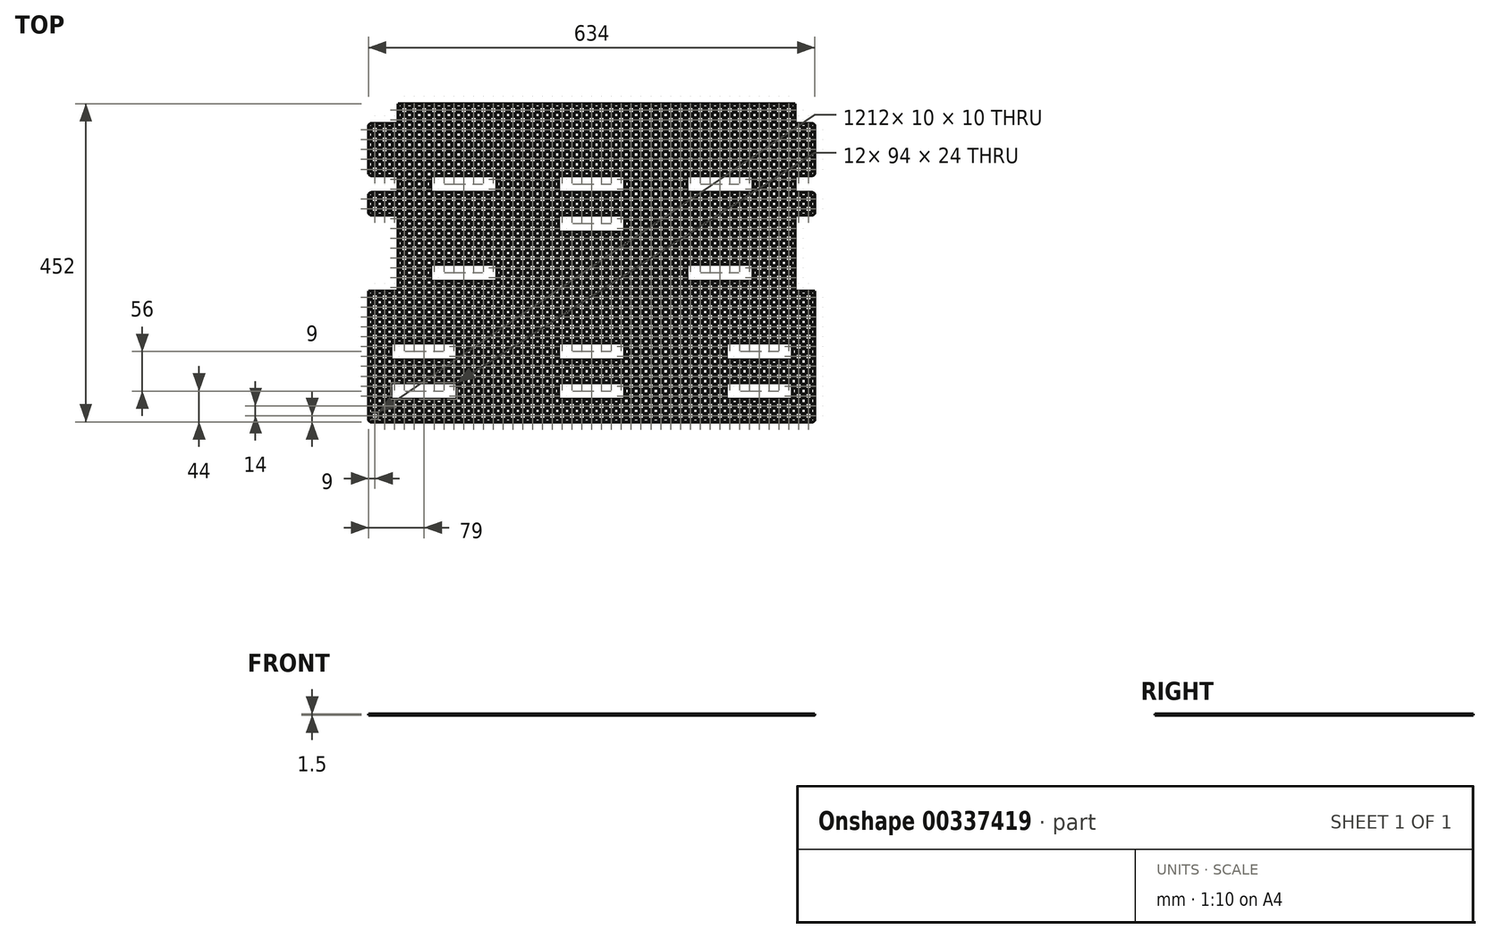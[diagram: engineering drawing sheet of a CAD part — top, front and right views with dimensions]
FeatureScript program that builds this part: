
annotation { "Feature Type Name" : "Feature", "Feature Type Description" : "" }
export const myFeature = defineFeature(function(context is Context, id is Id, definition is map)
    precondition{}
    {
        {
            var Q0;
            Q0=qCreatedBy(makeId("Top.planeOp"),FACE);
            var sketch = newSketch(context, id + "F0", { "sketchPlane" : qUnion([Q0])});
            skLineSegment(sketch, "E0.bottom", {"start": v(-317, 0) * mm, "end": v(317, 0) * mm});
            skLineSegment(sketch, "E0.top", {"start": v(-317, -452) * mm, "end": v(317, -452) * mm});
            skLineSegment(sketch, "E0.left", {"start": v(-317, 0) * mm, "end": v(-317, -452) * mm});
            skLineSegment(sketch, "E0.right", {"start": v(317, 0) * mm, "end": v(317, -452) * mm});
            skLineSegment(sketch, "E1", {"start": v(-317, 16) * mm, "end": v(317, 16) * mm, "construction": true});
            skLineSegment(sketch, "E2", {"start": v(-314.5, 16) * mm, "end": v(-314.5, -452) * mm, "construction": true});
            skLineSegment(sketch, "E3", {"start": v(-300, 16) * mm, "end": v(-300, -452) * mm, "construction": true});
            skLineSegment(sketch, "E4", {"start": v(-285.5, 16) * mm, "end": v(-285.5, -452) * mm, "construction": true});
            skLineSegment(sketch, "E5", {"start": v(285.5, 16) * mm, "end": v(285.5, -452) * mm, "construction": true});
            skLineSegment(sketch, "E6", {"start": v(300, 16) * mm, "end": v(300, -452) * mm, "construction": true});
            skLineSegment(sketch, "E7", {"start": v(314.5, 16) * mm, "end": v(314.5, -452) * mm, "construction": true});
            skLineSegment(sketch, "E8", {"start": v(-300, 0) * mm, "end": v(300, 0) * mm, "construction": true});
            skLineSegment(sketch, "E9", {"start": v(-314.5, -22) * mm, "end": v(314.5, -22) * mm, "construction": true});
            skLineSegment(sketch, "E10", {"start": v(-314.5, -112.5) * mm, "end": v(314.5, -112.5) * mm, "construction": true});
            skLineSegment(sketch, "E11", {"start": v(-314.5, -254) * mm, "end": v(314.5, -254) * mm, "construction": true});
            skLineSegment(sketch, "E12", {"start": v(-314.5, -231.78) * mm, "end": v(314.5, -231.78) * mm, "construction": true});
            skLineSegment(sketch, "E13", {"start": v(-314.5, -193) * mm, "end": v(314.5, -193) * mm, "construction": true});
            skCircle(sketch, "E14", {"center": v(-305, -22) * mm, "radius": 3.5 * mm, "construction": true});
            skCircle(sketch, "E15", {"center": v(-296, -112.5) * mm, "radius": 3.5 * mm, "construction": true});
            skCircle(sketch, "E16", {"center": v(-300, -254) * mm, "radius": 3.5 * mm, "construction": true});
            skCircle(sketch, "E17", {"center": v(295, -22) * mm, "radius": 3.5 * mm, "construction": true});
            skCircle(sketch, "E18", {"center": v(304, -112.5) * mm, "radius": 3.5 * mm, "construction": true});
            skCircle(sketch, "E19", {"center": v(300, -254) * mm, "radius": 3.5 * mm, "construction": true});
            skSolve(sketch);
        }
        {
            var Q0;
            Q0=qCreatedBy(makeId("Top.planeOp"),FACE);
            var sketch = newSketch(context, id + "F1", { "sketchPlane" : qUnion([Q0])});
            skLineSegment(sketch, "E20.bottom", {"start": v(-313, -438) * mm, "end": v(-303, -438) * mm});
            skLineSegment(sketch, "E20.top", {"start": v(-313, -448) * mm, "end": v(-303, -448) * mm});
            skLineSegment(sketch, "E20.left", {"start": v(-313, -438) * mm, "end": v(-313, -448) * mm});
            skLineSegment(sketch, "E20.right", {"start": v(-303, -438) * mm, "end": v(-303, -448) * mm});
            skLineSegment(sketch, "E21.0.1.0", {"start": v(-313, -424) * mm, "end": v(-303, -424) * mm});
            skLineSegment(sketch, "E21.0.1.1", {"start": v(-313, -434) * mm, "end": v(-303, -434) * mm});
            skLineSegment(sketch, "E21.0.1.2", {"start": v(-313, -424) * mm, "end": v(-313, -434) * mm});
            skLineSegment(sketch, "E21.0.1.3", {"start": v(-303, -424) * mm, "end": v(-303, -434) * mm});
            skLineSegment(sketch, "E21.0.2.0", {"start": v(-313, -410) * mm, "end": v(-303, -410) * mm});
            skLineSegment(sketch, "E21.0.2.1", {"start": v(-313, -420) * mm, "end": v(-303, -420) * mm});
            skLineSegment(sketch, "E21.0.2.2", {"start": v(-313, -410) * mm, "end": v(-313, -420) * mm});
            skLineSegment(sketch, "E21.0.2.3", {"start": v(-303, -410) * mm, "end": v(-303, -420) * mm});
            skLineSegment(sketch, "E21.0.3.0", {"start": v(-313, -396) * mm, "end": v(-303, -396) * mm});
            skLineSegment(sketch, "E21.0.3.1", {"start": v(-313, -406) * mm, "end": v(-303, -406) * mm});
            skLineSegment(sketch, "E21.0.3.2", {"start": v(-313, -396) * mm, "end": v(-313, -406) * mm});
            skLineSegment(sketch, "E21.0.3.3", {"start": v(-303, -396) * mm, "end": v(-303, -406) * mm});
            skLineSegment(sketch, "E21.0.4.0", {"start": v(-313, -382) * mm, "end": v(-303, -382) * mm});
            skLineSegment(sketch, "E21.0.4.1", {"start": v(-313, -392) * mm, "end": v(-303, -392) * mm});
            skLineSegment(sketch, "E21.0.4.2", {"start": v(-313, -382) * mm, "end": v(-313, -392) * mm});
            skLineSegment(sketch, "E21.0.4.3", {"start": v(-303, -382) * mm, "end": v(-303, -392) * mm});
            skLineSegment(sketch, "E21.0.5.0", {"start": v(-313, -368) * mm, "end": v(-303, -368) * mm});
            skLineSegment(sketch, "E21.0.5.1", {"start": v(-313, -378) * mm, "end": v(-303, -378) * mm});
            skLineSegment(sketch, "E21.0.5.2", {"start": v(-313, -368) * mm, "end": v(-313, -378) * mm});
            skLineSegment(sketch, "E21.0.5.3", {"start": v(-303, -368) * mm, "end": v(-303, -378) * mm});
            skLineSegment(sketch, "E21.0.6.0", {"start": v(-313, -354) * mm, "end": v(-303, -354) * mm});
            skLineSegment(sketch, "E21.0.6.1", {"start": v(-313, -364) * mm, "end": v(-303, -364) * mm});
            skLineSegment(sketch, "E21.0.6.2", {"start": v(-313, -354) * mm, "end": v(-313, -364) * mm});
            skLineSegment(sketch, "E21.0.6.3", {"start": v(-303, -354) * mm, "end": v(-303, -364) * mm});
            skLineSegment(sketch, "E21.0.7.0", {"start": v(-313, -340) * mm, "end": v(-303, -340) * mm});
            skLineSegment(sketch, "E21.0.7.1", {"start": v(-313, -350) * mm, "end": v(-303, -350) * mm});
            skLineSegment(sketch, "E21.0.7.2", {"start": v(-313, -340) * mm, "end": v(-313, -350) * mm});
            skLineSegment(sketch, "E21.0.7.3", {"start": v(-303, -340) * mm, "end": v(-303, -350) * mm});
            skLineSegment(sketch, "E21.0.8.0", {"start": v(-313, -326) * mm, "end": v(-303, -326) * mm});
            skLineSegment(sketch, "E21.0.8.1", {"start": v(-313, -336) * mm, "end": v(-303, -336) * mm});
            skLineSegment(sketch, "E21.0.8.2", {"start": v(-313, -326) * mm, "end": v(-313, -336) * mm});
            skLineSegment(sketch, "E21.0.8.3", {"start": v(-303, -326) * mm, "end": v(-303, -336) * mm});
            skLineSegment(sketch, "E21.0.9.0", {"start": v(-313, -312) * mm, "end": v(-303, -312) * mm});
            skLineSegment(sketch, "E21.0.9.1", {"start": v(-313, -322) * mm, "end": v(-303, -322) * mm});
            skLineSegment(sketch, "E21.0.9.2", {"start": v(-313, -312) * mm, "end": v(-313, -322) * mm});
            skLineSegment(sketch, "E21.0.9.3", {"start": v(-303, -312) * mm, "end": v(-303, -322) * mm});
            skLineSegment(sketch, "E21.0.10.0", {"start": v(-313, -298) * mm, "end": v(-303, -298) * mm});
            skLineSegment(sketch, "E21.0.10.1", {"start": v(-313, -308) * mm, "end": v(-303, -308) * mm});
            skLineSegment(sketch, "E21.0.10.2", {"start": v(-313, -298) * mm, "end": v(-313, -308) * mm});
            skLineSegment(sketch, "E21.0.10.3", {"start": v(-303, -298) * mm, "end": v(-303, -308) * mm});
            skLineSegment(sketch, "E21.0.11.0", {"start": v(-313, -284) * mm, "end": v(-303, -284) * mm});
            skLineSegment(sketch, "E21.0.11.1", {"start": v(-313, -294) * mm, "end": v(-303, -294) * mm});
            skLineSegment(sketch, "E21.0.11.2", {"start": v(-313, -284) * mm, "end": v(-313, -294) * mm});
            skLineSegment(sketch, "E21.0.11.3", {"start": v(-303, -284) * mm, "end": v(-303, -294) * mm});
            skLineSegment(sketch, "E21.0.12.0", {"start": v(-313, -270) * mm, "end": v(-303, -270) * mm});
            skLineSegment(sketch, "E21.0.12.1", {"start": v(-313, -280) * mm, "end": v(-303, -280) * mm});
            skLineSegment(sketch, "E21.0.12.2", {"start": v(-313, -270) * mm, "end": v(-313, -280) * mm});
            skLineSegment(sketch, "E21.0.12.3", {"start": v(-303, -270) * mm, "end": v(-303, -280) * mm});
            skLineSegment(sketch, "E21.0.13.0", {"start": v(-313, -256) * mm, "end": v(-303, -256) * mm});
            skLineSegment(sketch, "E21.0.13.1", {"start": v(-313, -266) * mm, "end": v(-303, -266) * mm});
            skLineSegment(sketch, "E21.0.13.2", {"start": v(-313, -256) * mm, "end": v(-313, -266) * mm});
            skLineSegment(sketch, "E21.0.13.3", {"start": v(-303, -256) * mm, "end": v(-303, -266) * mm});
            skLineSegment(sketch, "E21.0.14.0", {"start": v(-313, -242) * mm, "end": v(-303, -242) * mm});
            skLineSegment(sketch, "E21.0.14.1", {"start": v(-313, -252) * mm, "end": v(-303, -252) * mm});
            skLineSegment(sketch, "E21.0.14.2", {"start": v(-313, -242) * mm, "end": v(-313, -252) * mm});
            skLineSegment(sketch, "E21.0.14.3", {"start": v(-303, -242) * mm, "end": v(-303, -252) * mm});
            skLineSegment(sketch, "E21.0.15.0", {"start": v(-313, -228) * mm, "end": v(-303, -228) * mm});
            skLineSegment(sketch, "E21.0.15.1", {"start": v(-313, -238) * mm, "end": v(-303, -238) * mm});
            skLineSegment(sketch, "E21.0.15.2", {"start": v(-313, -228) * mm, "end": v(-313, -238) * mm});
            skLineSegment(sketch, "E21.0.15.3", {"start": v(-303, -228) * mm, "end": v(-303, -238) * mm});
            skLineSegment(sketch, "E21.0.16.0", {"start": v(-313, -214) * mm, "end": v(-303, -214) * mm});
            skLineSegment(sketch, "E21.0.16.1", {"start": v(-313, -224) * mm, "end": v(-303, -224) * mm});
            skLineSegment(sketch, "E21.0.16.2", {"start": v(-313, -214) * mm, "end": v(-313, -224) * mm});
            skLineSegment(sketch, "E21.0.16.3", {"start": v(-303, -214) * mm, "end": v(-303, -224) * mm});
            skLineSegment(sketch, "E21.0.17.0", {"start": v(-313, -200) * mm, "end": v(-303, -200) * mm});
            skLineSegment(sketch, "E21.0.17.1", {"start": v(-313, -210) * mm, "end": v(-303, -210) * mm});
            skLineSegment(sketch, "E21.0.17.2", {"start": v(-313, -200) * mm, "end": v(-313, -210) * mm});
            skLineSegment(sketch, "E21.0.17.3", {"start": v(-303, -200) * mm, "end": v(-303, -210) * mm});
            skLineSegment(sketch, "E21.0.18.0", {"start": v(-313, -186) * mm, "end": v(-303, -186) * mm});
            skLineSegment(sketch, "E21.0.18.1", {"start": v(-313, -196) * mm, "end": v(-303, -196) * mm});
            skLineSegment(sketch, "E21.0.18.2", {"start": v(-313, -186) * mm, "end": v(-313, -196) * mm});
            skLineSegment(sketch, "E21.0.18.3", {"start": v(-303, -186) * mm, "end": v(-303, -196) * mm});
            skLineSegment(sketch, "E21.0.19.0", {"start": v(-313, -172) * mm, "end": v(-303, -172) * mm});
            skLineSegment(sketch, "E21.0.19.1", {"start": v(-313, -182) * mm, "end": v(-303, -182) * mm});
            skLineSegment(sketch, "E21.0.19.2", {"start": v(-313, -172) * mm, "end": v(-313, -182) * mm});
            skLineSegment(sketch, "E21.0.19.3", {"start": v(-303, -172) * mm, "end": v(-303, -182) * mm});
            skLineSegment(sketch, "E21.0.20.0", {"start": v(-313, -158) * mm, "end": v(-303, -158) * mm});
            skLineSegment(sketch, "E21.0.20.1", {"start": v(-313, -168) * mm, "end": v(-303, -168) * mm});
            skLineSegment(sketch, "E21.0.20.2", {"start": v(-313, -158) * mm, "end": v(-313, -168) * mm});
            skLineSegment(sketch, "E21.0.20.3", {"start": v(-303, -158) * mm, "end": v(-303, -168) * mm});
            skLineSegment(sketch, "E21.0.21.0", {"start": v(-313, -144) * mm, "end": v(-303, -144) * mm});
            skLineSegment(sketch, "E21.0.21.1", {"start": v(-313, -154) * mm, "end": v(-303, -154) * mm});
            skLineSegment(sketch, "E21.0.21.2", {"start": v(-313, -144) * mm, "end": v(-313, -154) * mm});
            skLineSegment(sketch, "E21.0.21.3", {"start": v(-303, -144) * mm, "end": v(-303, -154) * mm});
            skLineSegment(sketch, "E21.0.22.0", {"start": v(-313, -130) * mm, "end": v(-303, -130) * mm});
            skLineSegment(sketch, "E21.0.22.1", {"start": v(-313, -140) * mm, "end": v(-303, -140) * mm});
            skLineSegment(sketch, "E21.0.22.2", {"start": v(-313, -130) * mm, "end": v(-313, -140) * mm});
            skLineSegment(sketch, "E21.0.22.3", {"start": v(-303, -130) * mm, "end": v(-303, -140) * mm});
            skLineSegment(sketch, "E21.0.23.0", {"start": v(-313, -116) * mm, "end": v(-303, -116) * mm});
            skLineSegment(sketch, "E21.0.23.1", {"start": v(-313, -126) * mm, "end": v(-303, -126) * mm});
            skLineSegment(sketch, "E21.0.23.2", {"start": v(-313, -116) * mm, "end": v(-313, -126) * mm});
            skLineSegment(sketch, "E21.0.23.3", {"start": v(-303, -116) * mm, "end": v(-303, -126) * mm});
            skLineSegment(sketch, "E21.0.24.0", {"start": v(-313, -102) * mm, "end": v(-303, -102) * mm});
            skLineSegment(sketch, "E21.0.24.1", {"start": v(-313, -112) * mm, "end": v(-303, -112) * mm});
            skLineSegment(sketch, "E21.0.24.2", {"start": v(-313, -102) * mm, "end": v(-313, -112) * mm});
            skLineSegment(sketch, "E21.0.24.3", {"start": v(-303, -102) * mm, "end": v(-303, -112) * mm});
            skLineSegment(sketch, "E21.0.25.0", {"start": v(-313, -88) * mm, "end": v(-303, -88) * mm});
            skLineSegment(sketch, "E21.0.25.1", {"start": v(-313, -98) * mm, "end": v(-303, -98) * mm});
            skLineSegment(sketch, "E21.0.25.2", {"start": v(-313, -88) * mm, "end": v(-313, -98) * mm});
            skLineSegment(sketch, "E21.0.25.3", {"start": v(-303, -88) * mm, "end": v(-303, -98) * mm});
            skLineSegment(sketch, "E21.0.26.0", {"start": v(-313, -74) * mm, "end": v(-303, -74) * mm});
            skLineSegment(sketch, "E21.0.26.1", {"start": v(-313, -84) * mm, "end": v(-303, -84) * mm});
            skLineSegment(sketch, "E21.0.26.2", {"start": v(-313, -74) * mm, "end": v(-313, -84) * mm});
            skLineSegment(sketch, "E21.0.26.3", {"start": v(-303, -74) * mm, "end": v(-303, -84) * mm});
            skLineSegment(sketch, "E21.0.27.0", {"start": v(-313, -60) * mm, "end": v(-303, -60) * mm});
            skLineSegment(sketch, "E21.0.27.1", {"start": v(-313, -70) * mm, "end": v(-303, -70) * mm});
            skLineSegment(sketch, "E21.0.27.2", {"start": v(-313, -60) * mm, "end": v(-313, -70) * mm});
            skLineSegment(sketch, "E21.0.27.3", {"start": v(-303, -60) * mm, "end": v(-303, -70) * mm});
            skLineSegment(sketch, "E21.0.28.0", {"start": v(-313, -46) * mm, "end": v(-303, -46) * mm});
            skLineSegment(sketch, "E21.0.28.1", {"start": v(-313, -56) * mm, "end": v(-303, -56) * mm});
            skLineSegment(sketch, "E21.0.28.2", {"start": v(-313, -46) * mm, "end": v(-313, -56) * mm});
            skLineSegment(sketch, "E21.0.28.3", {"start": v(-303, -46) * mm, "end": v(-303, -56) * mm});
            skLineSegment(sketch, "E21.0.29.0", {"start": v(-313, -32) * mm, "end": v(-303, -32) * mm});
            skLineSegment(sketch, "E21.0.29.1", {"start": v(-313, -42) * mm, "end": v(-303, -42) * mm});
            skLineSegment(sketch, "E21.0.29.2", {"start": v(-313, -32) * mm, "end": v(-313, -42) * mm});
            skLineSegment(sketch, "E21.0.29.3", {"start": v(-303, -32) * mm, "end": v(-303, -42) * mm});
            skLineSegment(sketch, "E21.0.30.0", {"start": v(-313, -18) * mm, "end": v(-303, -18) * mm});
            skLineSegment(sketch, "E21.0.30.1", {"start": v(-313, -28) * mm, "end": v(-303, -28) * mm});
            skLineSegment(sketch, "E21.0.30.2", {"start": v(-313, -18) * mm, "end": v(-313, -28) * mm});
            skLineSegment(sketch, "E21.0.30.3", {"start": v(-303, -18) * mm, "end": v(-303, -28) * mm});
            skLineSegment(sketch, "E21.0.31.0", {"start": v(-313, -4) * mm, "end": v(-303, -4) * mm});
            skLineSegment(sketch, "E21.0.31.1", {"start": v(-313, -14) * mm, "end": v(-303, -14) * mm});
            skLineSegment(sketch, "E21.0.31.2", {"start": v(-313, -4) * mm, "end": v(-313, -14) * mm});
            skLineSegment(sketch, "E21.0.31.3", {"start": v(-303, -4) * mm, "end": v(-303, -14) * mm});
            skLineSegment(sketch, "E21.1.0.0", {"start": v(-299, -438) * mm, "end": v(-289, -438) * mm});
            skLineSegment(sketch, "E21.1.0.1", {"start": v(-299, -448) * mm, "end": v(-289, -448) * mm});
            skLineSegment(sketch, "E21.1.0.2", {"start": v(-299, -438) * mm, "end": v(-299, -448) * mm});
            skLineSegment(sketch, "E21.1.0.3", {"start": v(-289, -438) * mm, "end": v(-289, -448) * mm});
            skLineSegment(sketch, "E21.1.1.0", {"start": v(-299, -424) * mm, "end": v(-289, -424) * mm});
            skLineSegment(sketch, "E21.1.1.1", {"start": v(-299, -434) * mm, "end": v(-289, -434) * mm});
            skLineSegment(sketch, "E21.1.1.2", {"start": v(-299, -424) * mm, "end": v(-299, -434) * mm});
            skLineSegment(sketch, "E21.1.1.3", {"start": v(-289, -424) * mm, "end": v(-289, -434) * mm});
            skLineSegment(sketch, "E21.1.2.0", {"start": v(-299, -410) * mm, "end": v(-289, -410) * mm});
            skLineSegment(sketch, "E21.1.2.1", {"start": v(-299, -420) * mm, "end": v(-289, -420) * mm});
            skLineSegment(sketch, "E21.1.2.2", {"start": v(-299, -410) * mm, "end": v(-299, -420) * mm});
            skLineSegment(sketch, "E21.1.2.3", {"start": v(-289, -410) * mm, "end": v(-289, -420) * mm});
            skLineSegment(sketch, "E21.1.3.0", {"start": v(-299, -396) * mm, "end": v(-289, -396) * mm});
            skLineSegment(sketch, "E21.1.3.1", {"start": v(-299, -406) * mm, "end": v(-289, -406) * mm});
            skLineSegment(sketch, "E21.1.3.2", {"start": v(-299, -396) * mm, "end": v(-299, -406) * mm});
            skLineSegment(sketch, "E21.1.3.3", {"start": v(-289, -396) * mm, "end": v(-289, -406) * mm});
            skLineSegment(sketch, "E21.1.4.0", {"start": v(-299, -382) * mm, "end": v(-289, -382) * mm});
            skLineSegment(sketch, "E21.1.4.1", {"start": v(-299, -392) * mm, "end": v(-289, -392) * mm});
            skLineSegment(sketch, "E21.1.4.2", {"start": v(-299, -382) * mm, "end": v(-299, -392) * mm});
            skLineSegment(sketch, "E21.1.4.3", {"start": v(-289, -382) * mm, "end": v(-289, -392) * mm});
            skLineSegment(sketch, "E21.1.5.0", {"start": v(-299, -368) * mm, "end": v(-289, -368) * mm});
            skLineSegment(sketch, "E21.1.5.1", {"start": v(-299, -378) * mm, "end": v(-289, -378) * mm});
            skLineSegment(sketch, "E21.1.5.2", {"start": v(-299, -368) * mm, "end": v(-299, -378) * mm});
            skLineSegment(sketch, "E21.1.5.3", {"start": v(-289, -368) * mm, "end": v(-289, -378) * mm});
            skLineSegment(sketch, "E21.1.6.0", {"start": v(-299, -354) * mm, "end": v(-289, -354) * mm});
            skLineSegment(sketch, "E21.1.6.1", {"start": v(-299, -364) * mm, "end": v(-289, -364) * mm});
            skLineSegment(sketch, "E21.1.6.2", {"start": v(-299, -354) * mm, "end": v(-299, -364) * mm});
            skLineSegment(sketch, "E21.1.6.3", {"start": v(-289, -354) * mm, "end": v(-289, -364) * mm});
            skLineSegment(sketch, "E21.1.7.0", {"start": v(-299, -340) * mm, "end": v(-289, -340) * mm});
            skLineSegment(sketch, "E21.1.7.1", {"start": v(-299, -350) * mm, "end": v(-289, -350) * mm});
            skLineSegment(sketch, "E21.1.7.2", {"start": v(-299, -340) * mm, "end": v(-299, -350) * mm});
            skLineSegment(sketch, "E21.1.7.3", {"start": v(-289, -340) * mm, "end": v(-289, -350) * mm});
            skLineSegment(sketch, "E21.1.8.0", {"start": v(-299, -326) * mm, "end": v(-289, -326) * mm});
            skLineSegment(sketch, "E21.1.8.1", {"start": v(-299, -336) * mm, "end": v(-289, -336) * mm});
            skLineSegment(sketch, "E21.1.8.2", {"start": v(-299, -326) * mm, "end": v(-299, -336) * mm});
            skLineSegment(sketch, "E21.1.8.3", {"start": v(-289, -326) * mm, "end": v(-289, -336) * mm});
            skLineSegment(sketch, "E21.1.9.0", {"start": v(-299, -312) * mm, "end": v(-289, -312) * mm});
            skLineSegment(sketch, "E21.1.9.1", {"start": v(-299, -322) * mm, "end": v(-289, -322) * mm});
            skLineSegment(sketch, "E21.1.9.2", {"start": v(-299, -312) * mm, "end": v(-299, -322) * mm});
            skLineSegment(sketch, "E21.1.9.3", {"start": v(-289, -312) * mm, "end": v(-289, -322) * mm});
            skLineSegment(sketch, "E21.1.10.0", {"start": v(-299, -298) * mm, "end": v(-289, -298) * mm});
            skLineSegment(sketch, "E21.1.10.1", {"start": v(-299, -308) * mm, "end": v(-289, -308) * mm});
            skLineSegment(sketch, "E21.1.10.2", {"start": v(-299, -298) * mm, "end": v(-299, -308) * mm});
            skLineSegment(sketch, "E21.1.10.3", {"start": v(-289, -298) * mm, "end": v(-289, -308) * mm});
            skLineSegment(sketch, "E21.1.11.0", {"start": v(-299, -284) * mm, "end": v(-289, -284) * mm});
            skLineSegment(sketch, "E21.1.11.1", {"start": v(-299, -294) * mm, "end": v(-289, -294) * mm});
            skLineSegment(sketch, "E21.1.11.2", {"start": v(-299, -284) * mm, "end": v(-299, -294) * mm});
            skLineSegment(sketch, "E21.1.11.3", {"start": v(-289, -284) * mm, "end": v(-289, -294) * mm});
            skLineSegment(sketch, "E21.1.12.0", {"start": v(-299, -270) * mm, "end": v(-289, -270) * mm});
            skLineSegment(sketch, "E21.1.12.1", {"start": v(-299, -280) * mm, "end": v(-289, -280) * mm});
            skLineSegment(sketch, "E21.1.12.2", {"start": v(-299, -270) * mm, "end": v(-299, -280) * mm});
            skLineSegment(sketch, "E21.1.12.3", {"start": v(-289, -270) * mm, "end": v(-289, -280) * mm});
            skLineSegment(sketch, "E21.1.13.0", {"start": v(-299, -256) * mm, "end": v(-289, -256) * mm});
            skLineSegment(sketch, "E21.1.13.1", {"start": v(-299, -266) * mm, "end": v(-289, -266) * mm});
            skLineSegment(sketch, "E21.1.13.2", {"start": v(-299, -256) * mm, "end": v(-299, -266) * mm});
            skLineSegment(sketch, "E21.1.13.3", {"start": v(-289, -256) * mm, "end": v(-289, -266) * mm});
            skLineSegment(sketch, "E21.1.14.0", {"start": v(-299, -242) * mm, "end": v(-289, -242) * mm});
            skLineSegment(sketch, "E21.1.14.1", {"start": v(-299, -252) * mm, "end": v(-289, -252) * mm});
            skLineSegment(sketch, "E21.1.14.2", {"start": v(-299, -242) * mm, "end": v(-299, -252) * mm});
            skLineSegment(sketch, "E21.1.14.3", {"start": v(-289, -242) * mm, "end": v(-289, -252) * mm});
            skLineSegment(sketch, "E21.1.15.0", {"start": v(-299, -228) * mm, "end": v(-289, -228) * mm});
            skLineSegment(sketch, "E21.1.15.1", {"start": v(-299, -238) * mm, "end": v(-289, -238) * mm});
            skLineSegment(sketch, "E21.1.15.2", {"start": v(-299, -228) * mm, "end": v(-299, -238) * mm});
            skLineSegment(sketch, "E21.1.15.3", {"start": v(-289, -228) * mm, "end": v(-289, -238) * mm});
            skLineSegment(sketch, "E21.1.16.0", {"start": v(-299, -214) * mm, "end": v(-289, -214) * mm});
            skLineSegment(sketch, "E21.1.16.1", {"start": v(-299, -224) * mm, "end": v(-289, -224) * mm});
            skLineSegment(sketch, "E21.1.16.2", {"start": v(-299, -214) * mm, "end": v(-299, -224) * mm});
            skLineSegment(sketch, "E21.1.16.3", {"start": v(-289, -214) * mm, "end": v(-289, -224) * mm});
            skLineSegment(sketch, "E21.1.17.0", {"start": v(-299, -200) * mm, "end": v(-289, -200) * mm});
            skLineSegment(sketch, "E21.1.17.1", {"start": v(-299, -210) * mm, "end": v(-289, -210) * mm});
            skLineSegment(sketch, "E21.1.17.2", {"start": v(-299, -200) * mm, "end": v(-299, -210) * mm});
            skLineSegment(sketch, "E21.1.17.3", {"start": v(-289, -200) * mm, "end": v(-289, -210) * mm});
            skLineSegment(sketch, "E21.1.18.0", {"start": v(-299, -186) * mm, "end": v(-289, -186) * mm});
            skLineSegment(sketch, "E21.1.18.1", {"start": v(-299, -196) * mm, "end": v(-289, -196) * mm});
            skLineSegment(sketch, "E21.1.18.2", {"start": v(-299, -186) * mm, "end": v(-299, -196) * mm});
            skLineSegment(sketch, "E21.1.18.3", {"start": v(-289, -186) * mm, "end": v(-289, -196) * mm});
            skLineSegment(sketch, "E21.1.19.0", {"start": v(-299, -172) * mm, "end": v(-289, -172) * mm});
            skLineSegment(sketch, "E21.1.19.1", {"start": v(-299, -182) * mm, "end": v(-289, -182) * mm});
            skLineSegment(sketch, "E21.1.19.2", {"start": v(-299, -172) * mm, "end": v(-299, -182) * mm});
            skLineSegment(sketch, "E21.1.19.3", {"start": v(-289, -172) * mm, "end": v(-289, -182) * mm});
            skLineSegment(sketch, "E21.1.20.0", {"start": v(-299, -158) * mm, "end": v(-289, -158) * mm});
            skLineSegment(sketch, "E21.1.20.1", {"start": v(-299, -168) * mm, "end": v(-289, -168) * mm});
            skLineSegment(sketch, "E21.1.20.2", {"start": v(-299, -158) * mm, "end": v(-299, -168) * mm});
            skLineSegment(sketch, "E21.1.20.3", {"start": v(-289, -158) * mm, "end": v(-289, -168) * mm});
            skLineSegment(sketch, "E21.1.21.0", {"start": v(-299, -144) * mm, "end": v(-289, -144) * mm});
            skLineSegment(sketch, "E21.1.21.1", {"start": v(-299, -154) * mm, "end": v(-289, -154) * mm});
            skLineSegment(sketch, "E21.1.21.2", {"start": v(-299, -144) * mm, "end": v(-299, -154) * mm});
            skLineSegment(sketch, "E21.1.21.3", {"start": v(-289, -144) * mm, "end": v(-289, -154) * mm});
            skLineSegment(sketch, "E21.1.22.0", {"start": v(-299, -130) * mm, "end": v(-289, -130) * mm});
            skLineSegment(sketch, "E21.1.22.1", {"start": v(-299, -140) * mm, "end": v(-289, -140) * mm});
            skLineSegment(sketch, "E21.1.22.2", {"start": v(-299, -130) * mm, "end": v(-299, -140) * mm});
            skLineSegment(sketch, "E21.1.22.3", {"start": v(-289, -130) * mm, "end": v(-289, -140) * mm});
            skLineSegment(sketch, "E21.1.23.0", {"start": v(-299, -116) * mm, "end": v(-289, -116) * mm});
            skLineSegment(sketch, "E21.1.23.1", {"start": v(-299, -126) * mm, "end": v(-289, -126) * mm});
            skLineSegment(sketch, "E21.1.23.2", {"start": v(-299, -116) * mm, "end": v(-299, -126) * mm});
            skLineSegment(sketch, "E21.1.23.3", {"start": v(-289, -116) * mm, "end": v(-289, -126) * mm});
            skLineSegment(sketch, "E21.1.24.0", {"start": v(-299, -102) * mm, "end": v(-289, -102) * mm});
            skLineSegment(sketch, "E21.1.24.1", {"start": v(-299, -112) * mm, "end": v(-289, -112) * mm});
            skLineSegment(sketch, "E21.1.24.2", {"start": v(-299, -102) * mm, "end": v(-299, -112) * mm});
            skLineSegment(sketch, "E21.1.24.3", {"start": v(-289, -102) * mm, "end": v(-289, -112) * mm});
            skLineSegment(sketch, "E21.1.25.0", {"start": v(-299, -88) * mm, "end": v(-289, -88) * mm});
            skLineSegment(sketch, "E21.1.25.1", {"start": v(-299, -98) * mm, "end": v(-289, -98) * mm});
            skLineSegment(sketch, "E21.1.25.2", {"start": v(-299, -88) * mm, "end": v(-299, -98) * mm});
            skLineSegment(sketch, "E21.1.25.3", {"start": v(-289, -88) * mm, "end": v(-289, -98) * mm});
            skLineSegment(sketch, "E21.1.26.0", {"start": v(-299, -74) * mm, "end": v(-289, -74) * mm});
            skLineSegment(sketch, "E21.1.26.1", {"start": v(-299, -84) * mm, "end": v(-289, -84) * mm});
            skLineSegment(sketch, "E21.1.26.2", {"start": v(-299, -74) * mm, "end": v(-299, -84) * mm});
            skLineSegment(sketch, "E21.1.26.3", {"start": v(-289, -74) * mm, "end": v(-289, -84) * mm});
            skLineSegment(sketch, "E21.1.27.0", {"start": v(-299, -60) * mm, "end": v(-289, -60) * mm});
            skLineSegment(sketch, "E21.1.27.1", {"start": v(-299, -70) * mm, "end": v(-289, -70) * mm});
            skLineSegment(sketch, "E21.1.27.2", {"start": v(-299, -60) * mm, "end": v(-299, -70) * mm});
            skLineSegment(sketch, "E21.1.27.3", {"start": v(-289, -60) * mm, "end": v(-289, -70) * mm});
            skLineSegment(sketch, "E21.1.28.0", {"start": v(-299, -46) * mm, "end": v(-289, -46) * mm});
            skLineSegment(sketch, "E21.1.28.1", {"start": v(-299, -56) * mm, "end": v(-289, -56) * mm});
            skLineSegment(sketch, "E21.1.28.2", {"start": v(-299, -46) * mm, "end": v(-299, -56) * mm});
            skLineSegment(sketch, "E21.1.28.3", {"start": v(-289, -46) * mm, "end": v(-289, -56) * mm});
            skLineSegment(sketch, "E21.1.29.0", {"start": v(-299, -32) * mm, "end": v(-289, -32) * mm});
            skLineSegment(sketch, "E21.1.29.1", {"start": v(-299, -42) * mm, "end": v(-289, -42) * mm});
            skLineSegment(sketch, "E21.1.29.2", {"start": v(-299, -32) * mm, "end": v(-299, -42) * mm});
            skLineSegment(sketch, "E21.1.29.3", {"start": v(-289, -32) * mm, "end": v(-289, -42) * mm});
            skLineSegment(sketch, "E21.1.30.0", {"start": v(-299, -18) * mm, "end": v(-289, -18) * mm});
            skLineSegment(sketch, "E21.1.30.1", {"start": v(-299, -28) * mm, "end": v(-289, -28) * mm});
            skLineSegment(sketch, "E21.1.30.2", {"start": v(-299, -18) * mm, "end": v(-299, -28) * mm});
            skLineSegment(sketch, "E21.1.30.3", {"start": v(-289, -18) * mm, "end": v(-289, -28) * mm});
            skLineSegment(sketch, "E21.1.31.0", {"start": v(-299, -4) * mm, "end": v(-289, -4) * mm});
            skLineSegment(sketch, "E21.1.31.1", {"start": v(-299, -14) * mm, "end": v(-289, -14) * mm});
            skLineSegment(sketch, "E21.1.31.2", {"start": v(-299, -4) * mm, "end": v(-299, -14) * mm});
            skLineSegment(sketch, "E21.1.31.3", {"start": v(-289, -4) * mm, "end": v(-289, -14) * mm});
            skLineSegment(sketch, "E21.2.0.0", {"start": v(-285, -438) * mm, "end": v(-275, -438) * mm});
            skLineSegment(sketch, "E21.2.0.1", {"start": v(-285, -448) * mm, "end": v(-275, -448) * mm});
            skLineSegment(sketch, "E21.2.0.2", {"start": v(-285, -438) * mm, "end": v(-285, -448) * mm});
            skLineSegment(sketch, "E21.2.0.3", {"start": v(-275, -438) * mm, "end": v(-275, -448) * mm});
            skLineSegment(sketch, "E21.2.1.0", {"start": v(-285, -424) * mm, "end": v(-275, -424) * mm});
            skLineSegment(sketch, "E21.2.1.1", {"start": v(-285, -434) * mm, "end": v(-275, -434) * mm});
            skLineSegment(sketch, "E21.2.1.2", {"start": v(-285, -424) * mm, "end": v(-285, -434) * mm});
            skLineSegment(sketch, "E21.2.1.3", {"start": v(-275, -424) * mm, "end": v(-275, -434) * mm});
            skLineSegment(sketch, "E21.2.2.0", {"start": v(-285, -410) * mm, "end": v(-275, -410) * mm});
            skLineSegment(sketch, "E21.2.2.1", {"start": v(-285, -420) * mm, "end": v(-275, -420) * mm});
            skLineSegment(sketch, "E21.2.2.2", {"start": v(-285, -410) * mm, "end": v(-285, -420) * mm});
            skLineSegment(sketch, "E21.2.2.3", {"start": v(-275, -410) * mm, "end": v(-275, -420) * mm});
            skLineSegment(sketch, "E21.2.3.0", {"start": v(-285, -396) * mm, "end": v(-275, -396) * mm});
            skLineSegment(sketch, "E21.2.3.1", {"start": v(-285, -406) * mm, "end": v(-275, -406) * mm});
            skLineSegment(sketch, "E21.2.3.2", {"start": v(-285, -396) * mm, "end": v(-285, -406) * mm});
            skLineSegment(sketch, "E21.2.3.3", {"start": v(-275, -396) * mm, "end": v(-275, -406) * mm});
            skLineSegment(sketch, "E21.2.4.0", {"start": v(-285, -382) * mm, "end": v(-275, -382) * mm});
            skLineSegment(sketch, "E21.2.4.1", {"start": v(-285, -392) * mm, "end": v(-275, -392) * mm});
            skLineSegment(sketch, "E21.2.4.2", {"start": v(-285, -382) * mm, "end": v(-285, -392) * mm});
            skLineSegment(sketch, "E21.2.4.3", {"start": v(-275, -382) * mm, "end": v(-275, -392) * mm});
            skLineSegment(sketch, "E21.2.5.0", {"start": v(-285, -368) * mm, "end": v(-275, -368) * mm});
            skLineSegment(sketch, "E21.2.5.1", {"start": v(-285, -378) * mm, "end": v(-275, -378) * mm});
            skLineSegment(sketch, "E21.2.5.2", {"start": v(-285, -368) * mm, "end": v(-285, -378) * mm});
            skLineSegment(sketch, "E21.2.5.3", {"start": v(-275, -368) * mm, "end": v(-275, -378) * mm});
            skLineSegment(sketch, "E21.2.6.0", {"start": v(-285, -354) * mm, "end": v(-275, -354) * mm});
            skLineSegment(sketch, "E21.2.6.1", {"start": v(-285, -364) * mm, "end": v(-275, -364) * mm});
            skLineSegment(sketch, "E21.2.6.2", {"start": v(-285, -354) * mm, "end": v(-285, -364) * mm});
            skLineSegment(sketch, "E21.2.6.3", {"start": v(-275, -354) * mm, "end": v(-275, -364) * mm});
            skLineSegment(sketch, "E21.2.7.0", {"start": v(-285, -340) * mm, "end": v(-275, -340) * mm});
            skLineSegment(sketch, "E21.2.7.1", {"start": v(-285, -350) * mm, "end": v(-275, -350) * mm});
            skLineSegment(sketch, "E21.2.7.2", {"start": v(-285, -340) * mm, "end": v(-285, -350) * mm});
            skLineSegment(sketch, "E21.2.7.3", {"start": v(-275, -340) * mm, "end": v(-275, -350) * mm});
            skLineSegment(sketch, "E21.2.8.0", {"start": v(-285, -326) * mm, "end": v(-275, -326) * mm});
            skLineSegment(sketch, "E21.2.8.1", {"start": v(-285, -336) * mm, "end": v(-275, -336) * mm});
            skLineSegment(sketch, "E21.2.8.2", {"start": v(-285, -326) * mm, "end": v(-285, -336) * mm});
            skLineSegment(sketch, "E21.2.8.3", {"start": v(-275, -326) * mm, "end": v(-275, -336) * mm});
            skLineSegment(sketch, "E21.2.9.0", {"start": v(-285, -312) * mm, "end": v(-275, -312) * mm});
            skLineSegment(sketch, "E21.2.9.1", {"start": v(-285, -322) * mm, "end": v(-275, -322) * mm});
            skLineSegment(sketch, "E21.2.9.2", {"start": v(-285, -312) * mm, "end": v(-285, -322) * mm});
            skLineSegment(sketch, "E21.2.9.3", {"start": v(-275, -312) * mm, "end": v(-275, -322) * mm});
            skLineSegment(sketch, "E21.2.10.0", {"start": v(-285, -298) * mm, "end": v(-275, -298) * mm});
            skLineSegment(sketch, "E21.2.10.1", {"start": v(-285, -308) * mm, "end": v(-275, -308) * mm});
            skLineSegment(sketch, "E21.2.10.2", {"start": v(-285, -298) * mm, "end": v(-285, -308) * mm});
            skLineSegment(sketch, "E21.2.10.3", {"start": v(-275, -298) * mm, "end": v(-275, -308) * mm});
            skLineSegment(sketch, "E21.2.11.0", {"start": v(-285, -284) * mm, "end": v(-275, -284) * mm});
            skLineSegment(sketch, "E21.2.11.1", {"start": v(-285, -294) * mm, "end": v(-275, -294) * mm});
            skLineSegment(sketch, "E21.2.11.2", {"start": v(-285, -284) * mm, "end": v(-285, -294) * mm});
            skLineSegment(sketch, "E21.2.11.3", {"start": v(-275, -284) * mm, "end": v(-275, -294) * mm});
            skLineSegment(sketch, "E21.2.12.0", {"start": v(-285, -270) * mm, "end": v(-275, -270) * mm});
            skLineSegment(sketch, "E21.2.12.1", {"start": v(-285, -280) * mm, "end": v(-275, -280) * mm});
            skLineSegment(sketch, "E21.2.12.2", {"start": v(-285, -270) * mm, "end": v(-285, -280) * mm});
            skLineSegment(sketch, "E21.2.12.3", {"start": v(-275, -270) * mm, "end": v(-275, -280) * mm});
            skLineSegment(sketch, "E21.2.13.0", {"start": v(-285, -256) * mm, "end": v(-275, -256) * mm});
            skLineSegment(sketch, "E21.2.13.1", {"start": v(-285, -266) * mm, "end": v(-275, -266) * mm});
            skLineSegment(sketch, "E21.2.13.2", {"start": v(-285, -256) * mm, "end": v(-285, -266) * mm});
            skLineSegment(sketch, "E21.2.13.3", {"start": v(-275, -256) * mm, "end": v(-275, -266) * mm});
            skLineSegment(sketch, "E21.2.14.0", {"start": v(-285, -242) * mm, "end": v(-275, -242) * mm});
            skLineSegment(sketch, "E21.2.14.1", {"start": v(-285, -252) * mm, "end": v(-275, -252) * mm});
            skLineSegment(sketch, "E21.2.14.2", {"start": v(-285, -242) * mm, "end": v(-285, -252) * mm});
            skLineSegment(sketch, "E21.2.14.3", {"start": v(-275, -242) * mm, "end": v(-275, -252) * mm});
            skLineSegment(sketch, "E21.2.15.0", {"start": v(-285, -228) * mm, "end": v(-275, -228) * mm});
            skLineSegment(sketch, "E21.2.15.1", {"start": v(-285, -238) * mm, "end": v(-275, -238) * mm});
            skLineSegment(sketch, "E21.2.15.2", {"start": v(-285, -228) * mm, "end": v(-285, -238) * mm});
            skLineSegment(sketch, "E21.2.15.3", {"start": v(-275, -228) * mm, "end": v(-275, -238) * mm});
            skLineSegment(sketch, "E21.2.16.0", {"start": v(-285, -214) * mm, "end": v(-275, -214) * mm});
            skLineSegment(sketch, "E21.2.16.1", {"start": v(-285, -224) * mm, "end": v(-275, -224) * mm});
            skLineSegment(sketch, "E21.2.16.2", {"start": v(-285, -214) * mm, "end": v(-285, -224) * mm});
            skLineSegment(sketch, "E21.2.16.3", {"start": v(-275, -214) * mm, "end": v(-275, -224) * mm});
            skLineSegment(sketch, "E21.2.17.0", {"start": v(-285, -200) * mm, "end": v(-275, -200) * mm});
            skLineSegment(sketch, "E21.2.17.1", {"start": v(-285, -210) * mm, "end": v(-275, -210) * mm});
            skLineSegment(sketch, "E21.2.17.2", {"start": v(-285, -200) * mm, "end": v(-285, -210) * mm});
            skLineSegment(sketch, "E21.2.17.3", {"start": v(-275, -200) * mm, "end": v(-275, -210) * mm});
            skLineSegment(sketch, "E21.2.18.0", {"start": v(-285, -186) * mm, "end": v(-275, -186) * mm});
            skLineSegment(sketch, "E21.2.18.1", {"start": v(-285, -196) * mm, "end": v(-275, -196) * mm});
            skLineSegment(sketch, "E21.2.18.2", {"start": v(-285, -186) * mm, "end": v(-285, -196) * mm});
            skLineSegment(sketch, "E21.2.18.3", {"start": v(-275, -186) * mm, "end": v(-275, -196) * mm});
            skLineSegment(sketch, "E21.2.19.0", {"start": v(-285, -172) * mm, "end": v(-275, -172) * mm});
            skLineSegment(sketch, "E21.2.19.1", {"start": v(-285, -182) * mm, "end": v(-275, -182) * mm});
            skLineSegment(sketch, "E21.2.19.2", {"start": v(-285, -172) * mm, "end": v(-285, -182) * mm});
            skLineSegment(sketch, "E21.2.19.3", {"start": v(-275, -172) * mm, "end": v(-275, -182) * mm});
            skLineSegment(sketch, "E21.2.20.0", {"start": v(-285, -158) * mm, "end": v(-275, -158) * mm});
            skLineSegment(sketch, "E21.2.20.1", {"start": v(-285, -168) * mm, "end": v(-275, -168) * mm});
            skLineSegment(sketch, "E21.2.20.2", {"start": v(-285, -158) * mm, "end": v(-285, -168) * mm});
            skLineSegment(sketch, "E21.2.20.3", {"start": v(-275, -158) * mm, "end": v(-275, -168) * mm});
            skLineSegment(sketch, "E21.2.21.0", {"start": v(-285, -144) * mm, "end": v(-275, -144) * mm});
            skLineSegment(sketch, "E21.2.21.1", {"start": v(-285, -154) * mm, "end": v(-275, -154) * mm});
            skLineSegment(sketch, "E21.2.21.2", {"start": v(-285, -144) * mm, "end": v(-285, -154) * mm});
            skLineSegment(sketch, "E21.2.21.3", {"start": v(-275, -144) * mm, "end": v(-275, -154) * mm});
            skLineSegment(sketch, "E21.2.22.0", {"start": v(-285, -130) * mm, "end": v(-275, -130) * mm});
            skLineSegment(sketch, "E21.2.22.1", {"start": v(-285, -140) * mm, "end": v(-275, -140) * mm});
            skLineSegment(sketch, "E21.2.22.2", {"start": v(-285, -130) * mm, "end": v(-285, -140) * mm});
            skLineSegment(sketch, "E21.2.22.3", {"start": v(-275, -130) * mm, "end": v(-275, -140) * mm});
            skLineSegment(sketch, "E21.2.23.0", {"start": v(-285, -116) * mm, "end": v(-275, -116) * mm});
            skLineSegment(sketch, "E21.2.23.1", {"start": v(-285, -126) * mm, "end": v(-275, -126) * mm});
            skLineSegment(sketch, "E21.2.23.2", {"start": v(-285, -116) * mm, "end": v(-285, -126) * mm});
            skLineSegment(sketch, "E21.2.23.3", {"start": v(-275, -116) * mm, "end": v(-275, -126) * mm});
            skLineSegment(sketch, "E21.2.24.0", {"start": v(-285, -102) * mm, "end": v(-275, -102) * mm});
            skLineSegment(sketch, "E21.2.24.1", {"start": v(-285, -112) * mm, "end": v(-275, -112) * mm});
            skLineSegment(sketch, "E21.2.24.2", {"start": v(-285, -102) * mm, "end": v(-285, -112) * mm});
            skLineSegment(sketch, "E21.2.24.3", {"start": v(-275, -102) * mm, "end": v(-275, -112) * mm});
            skLineSegment(sketch, "E21.2.25.0", {"start": v(-285, -88) * mm, "end": v(-275, -88) * mm});
            skLineSegment(sketch, "E21.2.25.1", {"start": v(-285, -98) * mm, "end": v(-275, -98) * mm});
            skLineSegment(sketch, "E21.2.25.2", {"start": v(-285, -88) * mm, "end": v(-285, -98) * mm});
            skLineSegment(sketch, "E21.2.25.3", {"start": v(-275, -88) * mm, "end": v(-275, -98) * mm});
            skLineSegment(sketch, "E21.2.26.0", {"start": v(-285, -74) * mm, "end": v(-275, -74) * mm});
            skLineSegment(sketch, "E21.2.26.1", {"start": v(-285, -84) * mm, "end": v(-275, -84) * mm});
            skLineSegment(sketch, "E21.2.26.2", {"start": v(-285, -74) * mm, "end": v(-285, -84) * mm});
            skLineSegment(sketch, "E21.2.26.3", {"start": v(-275, -74) * mm, "end": v(-275, -84) * mm});
            skLineSegment(sketch, "E21.2.27.0", {"start": v(-285, -60) * mm, "end": v(-275, -60) * mm});
            skLineSegment(sketch, "E21.2.27.1", {"start": v(-285, -70) * mm, "end": v(-275, -70) * mm});
            skLineSegment(sketch, "E21.2.27.2", {"start": v(-285, -60) * mm, "end": v(-285, -70) * mm});
            skLineSegment(sketch, "E21.2.27.3", {"start": v(-275, -60) * mm, "end": v(-275, -70) * mm});
            skLineSegment(sketch, "E21.2.28.0", {"start": v(-285, -46) * mm, "end": v(-275, -46) * mm});
            skLineSegment(sketch, "E21.2.28.1", {"start": v(-285, -56) * mm, "end": v(-275, -56) * mm});
            skLineSegment(sketch, "E21.2.28.2", {"start": v(-285, -46) * mm, "end": v(-285, -56) * mm});
            skLineSegment(sketch, "E21.2.28.3", {"start": v(-275, -46) * mm, "end": v(-275, -56) * mm});
            skLineSegment(sketch, "E21.2.29.0", {"start": v(-285, -32) * mm, "end": v(-275, -32) * mm});
            skLineSegment(sketch, "E21.2.29.1", {"start": v(-285, -42) * mm, "end": v(-275, -42) * mm});
            skLineSegment(sketch, "E21.2.29.2", {"start": v(-285, -32) * mm, "end": v(-285, -42) * mm});
            skLineSegment(sketch, "E21.2.29.3", {"start": v(-275, -32) * mm, "end": v(-275, -42) * mm});
            skLineSegment(sketch, "E21.2.30.0", {"start": v(-285, -18) * mm, "end": v(-275, -18) * mm});
            skLineSegment(sketch, "E21.2.30.1", {"start": v(-285, -28) * mm, "end": v(-275, -28) * mm});
            skLineSegment(sketch, "E21.2.30.2", {"start": v(-285, -18) * mm, "end": v(-285, -28) * mm});
            skLineSegment(sketch, "E21.2.30.3", {"start": v(-275, -18) * mm, "end": v(-275, -28) * mm});
            skLineSegment(sketch, "E21.2.31.0", {"start": v(-285, -4) * mm, "end": v(-275, -4) * mm});
            skLineSegment(sketch, "E21.2.31.1", {"start": v(-285, -14) * mm, "end": v(-275, -14) * mm});
            skLineSegment(sketch, "E21.2.31.2", {"start": v(-285, -4) * mm, "end": v(-285, -14) * mm});
            skLineSegment(sketch, "E21.2.31.3", {"start": v(-275, -4) * mm, "end": v(-275, -14) * mm});
            skLineSegment(sketch, "E21.3.0.0", {"start": v(-271, -438) * mm, "end": v(-261, -438) * mm});
            skLineSegment(sketch, "E21.3.0.1", {"start": v(-271, -448) * mm, "end": v(-261, -448) * mm});
            skLineSegment(sketch, "E21.3.0.2", {"start": v(-271, -438) * mm, "end": v(-271, -448) * mm});
            skLineSegment(sketch, "E21.3.0.3", {"start": v(-261, -438) * mm, "end": v(-261, -448) * mm});
            skLineSegment(sketch, "E21.3.1.0", {"start": v(-271, -424) * mm, "end": v(-261, -424) * mm});
            skLineSegment(sketch, "E21.3.1.1", {"start": v(-271, -434) * mm, "end": v(-261, -434) * mm});
            skLineSegment(sketch, "E21.3.1.2", {"start": v(-271, -424) * mm, "end": v(-271, -434) * mm});
            skLineSegment(sketch, "E21.3.1.3", {"start": v(-261, -424) * mm, "end": v(-261, -434) * mm});
            skLineSegment(sketch, "E21.3.2.0", {"start": v(-271, -410) * mm, "end": v(-261, -410) * mm});
            skLineSegment(sketch, "E21.3.2.1", {"start": v(-271, -420) * mm, "end": v(-261, -420) * mm});
            skLineSegment(sketch, "E21.3.2.2", {"start": v(-271, -410) * mm, "end": v(-271, -420) * mm});
            skLineSegment(sketch, "E21.3.2.3", {"start": v(-261, -410) * mm, "end": v(-261, -420) * mm});
            skLineSegment(sketch, "E21.3.3.0", {"start": v(-271, -396) * mm, "end": v(-261, -396) * mm});
            skLineSegment(sketch, "E21.3.3.1", {"start": v(-271, -406) * mm, "end": v(-261, -406) * mm});
            skLineSegment(sketch, "E21.3.3.2", {"start": v(-271, -396) * mm, "end": v(-271, -406) * mm});
            skLineSegment(sketch, "E21.3.3.3", {"start": v(-261, -396) * mm, "end": v(-261, -406) * mm});
            skLineSegment(sketch, "E21.3.4.0", {"start": v(-271, -382) * mm, "end": v(-261, -382) * mm});
            skLineSegment(sketch, "E21.3.4.1", {"start": v(-271, -392) * mm, "end": v(-261, -392) * mm});
            skLineSegment(sketch, "E21.3.4.2", {"start": v(-271, -382) * mm, "end": v(-271, -392) * mm});
            skLineSegment(sketch, "E21.3.4.3", {"start": v(-261, -382) * mm, "end": v(-261, -392) * mm});
            skLineSegment(sketch, "E21.3.5.0", {"start": v(-271, -368) * mm, "end": v(-261, -368) * mm});
            skLineSegment(sketch, "E21.3.5.1", {"start": v(-271, -378) * mm, "end": v(-261, -378) * mm});
            skLineSegment(sketch, "E21.3.5.2", {"start": v(-271, -368) * mm, "end": v(-271, -378) * mm});
            skLineSegment(sketch, "E21.3.5.3", {"start": v(-261, -368) * mm, "end": v(-261, -378) * mm});
            skLineSegment(sketch, "E21.3.6.0", {"start": v(-271, -354) * mm, "end": v(-261, -354) * mm});
            skLineSegment(sketch, "E21.3.6.1", {"start": v(-271, -364) * mm, "end": v(-261, -364) * mm});
            skLineSegment(sketch, "E21.3.6.2", {"start": v(-271, -354) * mm, "end": v(-271, -364) * mm});
            skLineSegment(sketch, "E21.3.6.3", {"start": v(-261, -354) * mm, "end": v(-261, -364) * mm});
            skLineSegment(sketch, "E21.3.7.0", {"start": v(-271, -340) * mm, "end": v(-261, -340) * mm});
            skLineSegment(sketch, "E21.3.7.1", {"start": v(-271, -350) * mm, "end": v(-261, -350) * mm});
            skLineSegment(sketch, "E21.3.7.2", {"start": v(-271, -340) * mm, "end": v(-271, -350) * mm});
            skLineSegment(sketch, "E21.3.7.3", {"start": v(-261, -340) * mm, "end": v(-261, -350) * mm});
            skLineSegment(sketch, "E21.3.8.0", {"start": v(-271, -326) * mm, "end": v(-261, -326) * mm});
            skLineSegment(sketch, "E21.3.8.1", {"start": v(-271, -336) * mm, "end": v(-261, -336) * mm});
            skLineSegment(sketch, "E21.3.8.2", {"start": v(-271, -326) * mm, "end": v(-271, -336) * mm});
            skLineSegment(sketch, "E21.3.8.3", {"start": v(-261, -326) * mm, "end": v(-261, -336) * mm});
            skLineSegment(sketch, "E21.3.9.0", {"start": v(-271, -312) * mm, "end": v(-261, -312) * mm});
            skLineSegment(sketch, "E21.3.9.1", {"start": v(-271, -322) * mm, "end": v(-261, -322) * mm});
            skLineSegment(sketch, "E21.3.9.2", {"start": v(-271, -312) * mm, "end": v(-271, -322) * mm});
            skLineSegment(sketch, "E21.3.9.3", {"start": v(-261, -312) * mm, "end": v(-261, -322) * mm});
            skLineSegment(sketch, "E21.3.10.0", {"start": v(-271, -298) * mm, "end": v(-261, -298) * mm});
            skLineSegment(sketch, "E21.3.10.1", {"start": v(-271, -308) * mm, "end": v(-261, -308) * mm});
            skLineSegment(sketch, "E21.3.10.2", {"start": v(-271, -298) * mm, "end": v(-271, -308) * mm});
            skLineSegment(sketch, "E21.3.10.3", {"start": v(-261, -298) * mm, "end": v(-261, -308) * mm});
            skLineSegment(sketch, "E21.3.11.0", {"start": v(-271, -284) * mm, "end": v(-261, -284) * mm});
            skLineSegment(sketch, "E21.3.11.1", {"start": v(-271, -294) * mm, "end": v(-261, -294) * mm});
            skLineSegment(sketch, "E21.3.11.2", {"start": v(-271, -284) * mm, "end": v(-271, -294) * mm});
            skLineSegment(sketch, "E21.3.11.3", {"start": v(-261, -284) * mm, "end": v(-261, -294) * mm});
            skLineSegment(sketch, "E21.3.12.0", {"start": v(-271, -270) * mm, "end": v(-261, -270) * mm});
            skLineSegment(sketch, "E21.3.12.1", {"start": v(-271, -280) * mm, "end": v(-261, -280) * mm});
            skLineSegment(sketch, "E21.3.12.2", {"start": v(-271, -270) * mm, "end": v(-271, -280) * mm});
            skLineSegment(sketch, "E21.3.12.3", {"start": v(-261, -270) * mm, "end": v(-261, -280) * mm});
            skLineSegment(sketch, "E21.3.13.0", {"start": v(-271, -256) * mm, "end": v(-261, -256) * mm});
            skLineSegment(sketch, "E21.3.13.1", {"start": v(-271, -266) * mm, "end": v(-261, -266) * mm});
            skLineSegment(sketch, "E21.3.13.2", {"start": v(-271, -256) * mm, "end": v(-271, -266) * mm});
            skLineSegment(sketch, "E21.3.13.3", {"start": v(-261, -256) * mm, "end": v(-261, -266) * mm});
            skLineSegment(sketch, "E21.3.14.0", {"start": v(-271, -242) * mm, "end": v(-261, -242) * mm});
            skLineSegment(sketch, "E21.3.14.1", {"start": v(-271, -252) * mm, "end": v(-261, -252) * mm});
            skLineSegment(sketch, "E21.3.14.2", {"start": v(-271, -242) * mm, "end": v(-271, -252) * mm});
            skLineSegment(sketch, "E21.3.14.3", {"start": v(-261, -242) * mm, "end": v(-261, -252) * mm});
            skLineSegment(sketch, "E21.3.15.0", {"start": v(-271, -228) * mm, "end": v(-261, -228) * mm});
            skLineSegment(sketch, "E21.3.15.1", {"start": v(-271, -238) * mm, "end": v(-261, -238) * mm});
            skLineSegment(sketch, "E21.3.15.2", {"start": v(-271, -228) * mm, "end": v(-271, -238) * mm});
            skLineSegment(sketch, "E21.3.15.3", {"start": v(-261, -228) * mm, "end": v(-261, -238) * mm});
            skLineSegment(sketch, "E21.3.16.0", {"start": v(-271, -214) * mm, "end": v(-261, -214) * mm});
            skLineSegment(sketch, "E21.3.16.1", {"start": v(-271, -224) * mm, "end": v(-261, -224) * mm});
            skLineSegment(sketch, "E21.3.16.2", {"start": v(-271, -214) * mm, "end": v(-271, -224) * mm});
            skLineSegment(sketch, "E21.3.16.3", {"start": v(-261, -214) * mm, "end": v(-261, -224) * mm});
            skLineSegment(sketch, "E21.3.17.0", {"start": v(-271, -200) * mm, "end": v(-261, -200) * mm});
            skLineSegment(sketch, "E21.3.17.1", {"start": v(-271, -210) * mm, "end": v(-261, -210) * mm});
            skLineSegment(sketch, "E21.3.17.2", {"start": v(-271, -200) * mm, "end": v(-271, -210) * mm});
            skLineSegment(sketch, "E21.3.17.3", {"start": v(-261, -200) * mm, "end": v(-261, -210) * mm});
            skLineSegment(sketch, "E21.3.18.0", {"start": v(-271, -186) * mm, "end": v(-261, -186) * mm});
            skLineSegment(sketch, "E21.3.18.1", {"start": v(-271, -196) * mm, "end": v(-261, -196) * mm});
            skLineSegment(sketch, "E21.3.18.2", {"start": v(-271, -186) * mm, "end": v(-271, -196) * mm});
            skLineSegment(sketch, "E21.3.18.3", {"start": v(-261, -186) * mm, "end": v(-261, -196) * mm});
            skLineSegment(sketch, "E21.3.19.0", {"start": v(-271, -172) * mm, "end": v(-261, -172) * mm});
            skLineSegment(sketch, "E21.3.19.1", {"start": v(-271, -182) * mm, "end": v(-261, -182) * mm});
            skLineSegment(sketch, "E21.3.19.2", {"start": v(-271, -172) * mm, "end": v(-271, -182) * mm});
            skLineSegment(sketch, "E21.3.19.3", {"start": v(-261, -172) * mm, "end": v(-261, -182) * mm});
            skLineSegment(sketch, "E21.3.20.0", {"start": v(-271, -158) * mm, "end": v(-261, -158) * mm});
            skLineSegment(sketch, "E21.3.20.1", {"start": v(-271, -168) * mm, "end": v(-261, -168) * mm});
            skLineSegment(sketch, "E21.3.20.2", {"start": v(-271, -158) * mm, "end": v(-271, -168) * mm});
            skLineSegment(sketch, "E21.3.20.3", {"start": v(-261, -158) * mm, "end": v(-261, -168) * mm});
            skLineSegment(sketch, "E21.3.21.0", {"start": v(-271, -144) * mm, "end": v(-261, -144) * mm});
            skLineSegment(sketch, "E21.3.21.1", {"start": v(-271, -154) * mm, "end": v(-261, -154) * mm});
            skLineSegment(sketch, "E21.3.21.2", {"start": v(-271, -144) * mm, "end": v(-271, -154) * mm});
            skLineSegment(sketch, "E21.3.21.3", {"start": v(-261, -144) * mm, "end": v(-261, -154) * mm});
            skLineSegment(sketch, "E21.3.22.0", {"start": v(-271, -130) * mm, "end": v(-261, -130) * mm});
            skLineSegment(sketch, "E21.3.22.1", {"start": v(-271, -140) * mm, "end": v(-261, -140) * mm});
            skLineSegment(sketch, "E21.3.22.2", {"start": v(-271, -130) * mm, "end": v(-271, -140) * mm});
            skLineSegment(sketch, "E21.3.22.3", {"start": v(-261, -130) * mm, "end": v(-261, -140) * mm});
            skLineSegment(sketch, "E21.3.23.0", {"start": v(-271, -116) * mm, "end": v(-261, -116) * mm});
            skLineSegment(sketch, "E21.3.23.1", {"start": v(-271, -126) * mm, "end": v(-261, -126) * mm});
            skLineSegment(sketch, "E21.3.23.2", {"start": v(-271, -116) * mm, "end": v(-271, -126) * mm});
            skLineSegment(sketch, "E21.3.23.3", {"start": v(-261, -116) * mm, "end": v(-261, -126) * mm});
            skLineSegment(sketch, "E21.3.24.0", {"start": v(-271, -102) * mm, "end": v(-261, -102) * mm});
            skLineSegment(sketch, "E21.3.24.1", {"start": v(-271, -112) * mm, "end": v(-261, -112) * mm});
            skLineSegment(sketch, "E21.3.24.2", {"start": v(-271, -102) * mm, "end": v(-271, -112) * mm});
            skLineSegment(sketch, "E21.3.24.3", {"start": v(-261, -102) * mm, "end": v(-261, -112) * mm});
            skLineSegment(sketch, "E21.3.25.0", {"start": v(-271, -88) * mm, "end": v(-261, -88) * mm});
            skLineSegment(sketch, "E21.3.25.1", {"start": v(-271, -98) * mm, "end": v(-261, -98) * mm});
            skLineSegment(sketch, "E21.3.25.2", {"start": v(-271, -88) * mm, "end": v(-271, -98) * mm});
            skLineSegment(sketch, "E21.3.25.3", {"start": v(-261, -88) * mm, "end": v(-261, -98) * mm});
            skLineSegment(sketch, "E21.3.26.0", {"start": v(-271, -74) * mm, "end": v(-261, -74) * mm});
            skLineSegment(sketch, "E21.3.26.1", {"start": v(-271, -84) * mm, "end": v(-261, -84) * mm});
            skLineSegment(sketch, "E21.3.26.2", {"start": v(-271, -74) * mm, "end": v(-271, -84) * mm});
            skLineSegment(sketch, "E21.3.26.3", {"start": v(-261, -74) * mm, "end": v(-261, -84) * mm});
            skLineSegment(sketch, "E21.3.27.0", {"start": v(-271, -60) * mm, "end": v(-261, -60) * mm});
            skLineSegment(sketch, "E21.3.27.1", {"start": v(-271, -70) * mm, "end": v(-261, -70) * mm});
            skLineSegment(sketch, "E21.3.27.2", {"start": v(-271, -60) * mm, "end": v(-271, -70) * mm});
            skLineSegment(sketch, "E21.3.27.3", {"start": v(-261, -60) * mm, "end": v(-261, -70) * mm});
            skLineSegment(sketch, "E21.3.28.0", {"start": v(-271, -46) * mm, "end": v(-261, -46) * mm});
            skLineSegment(sketch, "E21.3.28.1", {"start": v(-271, -56) * mm, "end": v(-261, -56) * mm});
            skLineSegment(sketch, "E21.3.28.2", {"start": v(-271, -46) * mm, "end": v(-271, -56) * mm});
            skLineSegment(sketch, "E21.3.28.3", {"start": v(-261, -46) * mm, "end": v(-261, -56) * mm});
            skLineSegment(sketch, "E21.3.29.0", {"start": v(-271, -32) * mm, "end": v(-261, -32) * mm});
            skLineSegment(sketch, "E21.3.29.1", {"start": v(-271, -42) * mm, "end": v(-261, -42) * mm});
            skLineSegment(sketch, "E21.3.29.2", {"start": v(-271, -32) * mm, "end": v(-271, -42) * mm});
            skLineSegment(sketch, "E21.3.29.3", {"start": v(-261, -32) * mm, "end": v(-261, -42) * mm});
            skLineSegment(sketch, "E21.3.30.0", {"start": v(-271, -18) * mm, "end": v(-261, -18) * mm});
            skLineSegment(sketch, "E21.3.30.1", {"start": v(-271, -28) * mm, "end": v(-261, -28) * mm});
            skLineSegment(sketch, "E21.3.30.2", {"start": v(-271, -18) * mm, "end": v(-271, -28) * mm});
            skLineSegment(sketch, "E21.3.30.3", {"start": v(-261, -18) * mm, "end": v(-261, -28) * mm});
            skLineSegment(sketch, "E21.3.31.0", {"start": v(-271, -4) * mm, "end": v(-261, -4) * mm});
            skLineSegment(sketch, "E21.3.31.1", {"start": v(-271, -14) * mm, "end": v(-261, -14) * mm});
            skLineSegment(sketch, "E21.3.31.2", {"start": v(-271, -4) * mm, "end": v(-271, -14) * mm});
            skLineSegment(sketch, "E21.3.31.3", {"start": v(-261, -4) * mm, "end": v(-261, -14) * mm});
            skLineSegment(sketch, "E21.direction1", {"start": v(-313, -448) * mm, "end": v(-299, -448) * mm, "construction": true});
            skLineSegment(sketch, "E21.direction2", {"start": v(-313, -448) * mm, "end": v(-313, -434) * mm, "construction": true});
            skLineSegment(sketch, "E22.bottom", {"start": v(303, -438) * mm, "end": v(313, -438) * mm});
            skLineSegment(sketch, "E22.top", {"start": v(303, -448) * mm, "end": v(313, -448) * mm});
            skLineSegment(sketch, "E22.left", {"start": v(303, -438) * mm, "end": v(303, -448) * mm});
            skLineSegment(sketch, "E22.right", {"start": v(313, -438) * mm, "end": v(313, -448) * mm});
            skLineSegment(sketch, "E23.0.1.0", {"start": v(303, -424) * mm, "end": v(313, -424) * mm});
            skLineSegment(sketch, "E23.0.1.1", {"start": v(303, -434) * mm, "end": v(313, -434) * mm});
            skLineSegment(sketch, "E23.0.1.2", {"start": v(303, -424) * mm, "end": v(303, -434) * mm});
            skLineSegment(sketch, "E23.0.1.3", {"start": v(313, -424) * mm, "end": v(313, -434) * mm});
            skLineSegment(sketch, "E23.0.2.0", {"start": v(303, -410) * mm, "end": v(313, -410) * mm});
            skLineSegment(sketch, "E23.0.2.1", {"start": v(303, -420) * mm, "end": v(313, -420) * mm});
            skLineSegment(sketch, "E23.0.2.2", {"start": v(303, -410) * mm, "end": v(303, -420) * mm});
            skLineSegment(sketch, "E23.0.2.3", {"start": v(313, -410) * mm, "end": v(313, -420) * mm});
            skLineSegment(sketch, "E23.0.3.0", {"start": v(303, -396) * mm, "end": v(313, -396) * mm});
            skLineSegment(sketch, "E23.0.3.1", {"start": v(303, -406) * mm, "end": v(313, -406) * mm});
            skLineSegment(sketch, "E23.0.3.2", {"start": v(303, -396) * mm, "end": v(303, -406) * mm});
            skLineSegment(sketch, "E23.0.3.3", {"start": v(313, -396) * mm, "end": v(313, -406) * mm});
            skLineSegment(sketch, "E23.0.4.0", {"start": v(303, -382) * mm, "end": v(313, -382) * mm});
            skLineSegment(sketch, "E23.0.4.1", {"start": v(303, -392) * mm, "end": v(313, -392) * mm});
            skLineSegment(sketch, "E23.0.4.2", {"start": v(303, -382) * mm, "end": v(303, -392) * mm});
            skLineSegment(sketch, "E23.0.4.3", {"start": v(313, -382) * mm, "end": v(313, -392) * mm});
            skLineSegment(sketch, "E23.0.5.0", {"start": v(303, -368) * mm, "end": v(313, -368) * mm});
            skLineSegment(sketch, "E23.0.5.1", {"start": v(303, -378) * mm, "end": v(313, -378) * mm});
            skLineSegment(sketch, "E23.0.5.2", {"start": v(303, -368) * mm, "end": v(303, -378) * mm});
            skLineSegment(sketch, "E23.0.5.3", {"start": v(313, -368) * mm, "end": v(313, -378) * mm});
            skLineSegment(sketch, "E23.0.6.0", {"start": v(303, -354) * mm, "end": v(313, -354) * mm});
            skLineSegment(sketch, "E23.0.6.1", {"start": v(303, -364) * mm, "end": v(313, -364) * mm});
            skLineSegment(sketch, "E23.0.6.2", {"start": v(303, -354) * mm, "end": v(303, -364) * mm});
            skLineSegment(sketch, "E23.0.6.3", {"start": v(313, -354) * mm, "end": v(313, -364) * mm});
            skLineSegment(sketch, "E23.0.7.0", {"start": v(303, -340) * mm, "end": v(313, -340) * mm});
            skLineSegment(sketch, "E23.0.7.1", {"start": v(303, -350) * mm, "end": v(313, -350) * mm});
            skLineSegment(sketch, "E23.0.7.2", {"start": v(303, -340) * mm, "end": v(303, -350) * mm});
            skLineSegment(sketch, "E23.0.7.3", {"start": v(313, -340) * mm, "end": v(313, -350) * mm});
            skLineSegment(sketch, "E23.0.8.0", {"start": v(303, -326) * mm, "end": v(313, -326) * mm});
            skLineSegment(sketch, "E23.0.8.1", {"start": v(303, -336) * mm, "end": v(313, -336) * mm});
            skLineSegment(sketch, "E23.0.8.2", {"start": v(303, -326) * mm, "end": v(303, -336) * mm});
            skLineSegment(sketch, "E23.0.8.3", {"start": v(313, -326) * mm, "end": v(313, -336) * mm});
            skLineSegment(sketch, "E23.0.9.0", {"start": v(303, -312) * mm, "end": v(313, -312) * mm});
            skLineSegment(sketch, "E23.0.9.1", {"start": v(303, -322) * mm, "end": v(313, -322) * mm});
            skLineSegment(sketch, "E23.0.9.2", {"start": v(303, -312) * mm, "end": v(303, -322) * mm});
            skLineSegment(sketch, "E23.0.9.3", {"start": v(313, -312) * mm, "end": v(313, -322) * mm});
            skLineSegment(sketch, "E23.0.10.0", {"start": v(303, -298) * mm, "end": v(313, -298) * mm});
            skLineSegment(sketch, "E23.0.10.1", {"start": v(303, -308) * mm, "end": v(313, -308) * mm});
            skLineSegment(sketch, "E23.0.10.2", {"start": v(303, -298) * mm, "end": v(303, -308) * mm});
            skLineSegment(sketch, "E23.0.10.3", {"start": v(313, -298) * mm, "end": v(313, -308) * mm});
            skLineSegment(sketch, "E23.0.11.0", {"start": v(303, -284) * mm, "end": v(313, -284) * mm});
            skLineSegment(sketch, "E23.0.11.1", {"start": v(303, -294) * mm, "end": v(313, -294) * mm});
            skLineSegment(sketch, "E23.0.11.2", {"start": v(303, -284) * mm, "end": v(303, -294) * mm});
            skLineSegment(sketch, "E23.0.11.3", {"start": v(313, -284) * mm, "end": v(313, -294) * mm});
            skLineSegment(sketch, "E23.0.12.0", {"start": v(303, -270) * mm, "end": v(313, -270) * mm});
            skLineSegment(sketch, "E23.0.12.1", {"start": v(303, -280) * mm, "end": v(313, -280) * mm});
            skLineSegment(sketch, "E23.0.12.2", {"start": v(303, -270) * mm, "end": v(303, -280) * mm});
            skLineSegment(sketch, "E23.0.12.3", {"start": v(313, -270) * mm, "end": v(313, -280) * mm});
            skLineSegment(sketch, "E23.0.13.0", {"start": v(303, -256) * mm, "end": v(313, -256) * mm});
            skLineSegment(sketch, "E23.0.13.1", {"start": v(303, -266) * mm, "end": v(313, -266) * mm});
            skLineSegment(sketch, "E23.0.13.2", {"start": v(303, -256) * mm, "end": v(303, -266) * mm});
            skLineSegment(sketch, "E23.0.13.3", {"start": v(313, -256) * mm, "end": v(313, -266) * mm});
            skLineSegment(sketch, "E23.0.14.0", {"start": v(303, -242) * mm, "end": v(313, -242) * mm});
            skLineSegment(sketch, "E23.0.14.1", {"start": v(303, -252) * mm, "end": v(313, -252) * mm});
            skLineSegment(sketch, "E23.0.14.2", {"start": v(303, -242) * mm, "end": v(303, -252) * mm});
            skLineSegment(sketch, "E23.0.14.3", {"start": v(313, -242) * mm, "end": v(313, -252) * mm});
            skLineSegment(sketch, "E23.0.15.0", {"start": v(303, -228) * mm, "end": v(313, -228) * mm});
            skLineSegment(sketch, "E23.0.15.1", {"start": v(303, -238) * mm, "end": v(313, -238) * mm});
            skLineSegment(sketch, "E23.0.15.2", {"start": v(303, -228) * mm, "end": v(303, -238) * mm});
            skLineSegment(sketch, "E23.0.15.3", {"start": v(313, -228) * mm, "end": v(313, -238) * mm});
            skLineSegment(sketch, "E23.0.16.0", {"start": v(303, -214) * mm, "end": v(313, -214) * mm});
            skLineSegment(sketch, "E23.0.16.1", {"start": v(303, -224) * mm, "end": v(313, -224) * mm});
            skLineSegment(sketch, "E23.0.16.2", {"start": v(303, -214) * mm, "end": v(303, -224) * mm});
            skLineSegment(sketch, "E23.0.16.3", {"start": v(313, -214) * mm, "end": v(313, -224) * mm});
            skLineSegment(sketch, "E23.0.17.0", {"start": v(303, -200) * mm, "end": v(313, -200) * mm});
            skLineSegment(sketch, "E23.0.17.1", {"start": v(303, -210) * mm, "end": v(313, -210) * mm});
            skLineSegment(sketch, "E23.0.17.2", {"start": v(303, -200) * mm, "end": v(303, -210) * mm});
            skLineSegment(sketch, "E23.0.17.3", {"start": v(313, -200) * mm, "end": v(313, -210) * mm});
            skLineSegment(sketch, "E23.0.18.0", {"start": v(303, -186) * mm, "end": v(313, -186) * mm});
            skLineSegment(sketch, "E23.0.18.1", {"start": v(303, -196) * mm, "end": v(313, -196) * mm});
            skLineSegment(sketch, "E23.0.18.2", {"start": v(303, -186) * mm, "end": v(303, -196) * mm});
            skLineSegment(sketch, "E23.0.18.3", {"start": v(313, -186) * mm, "end": v(313, -196) * mm});
            skLineSegment(sketch, "E23.0.19.0", {"start": v(303, -172) * mm, "end": v(313, -172) * mm});
            skLineSegment(sketch, "E23.0.19.1", {"start": v(303, -182) * mm, "end": v(313, -182) * mm});
            skLineSegment(sketch, "E23.0.19.2", {"start": v(303, -172) * mm, "end": v(303, -182) * mm});
            skLineSegment(sketch, "E23.0.19.3", {"start": v(313, -172) * mm, "end": v(313, -182) * mm});
            skLineSegment(sketch, "E23.0.20.0", {"start": v(303, -158) * mm, "end": v(313, -158) * mm});
            skLineSegment(sketch, "E23.0.20.1", {"start": v(303, -168) * mm, "end": v(313, -168) * mm});
            skLineSegment(sketch, "E23.0.20.2", {"start": v(303, -158) * mm, "end": v(303, -168) * mm});
            skLineSegment(sketch, "E23.0.20.3", {"start": v(313, -158) * mm, "end": v(313, -168) * mm});
            skLineSegment(sketch, "E23.0.21.0", {"start": v(303, -144) * mm, "end": v(313, -144) * mm});
            skLineSegment(sketch, "E23.0.21.1", {"start": v(303, -154) * mm, "end": v(313, -154) * mm});
            skLineSegment(sketch, "E23.0.21.2", {"start": v(303, -144) * mm, "end": v(303, -154) * mm});
            skLineSegment(sketch, "E23.0.21.3", {"start": v(313, -144) * mm, "end": v(313, -154) * mm});
            skLineSegment(sketch, "E23.0.22.0", {"start": v(303, -130) * mm, "end": v(313, -130) * mm});
            skLineSegment(sketch, "E23.0.22.1", {"start": v(303, -140) * mm, "end": v(313, -140) * mm});
            skLineSegment(sketch, "E23.0.22.2", {"start": v(303, -130) * mm, "end": v(303, -140) * mm});
            skLineSegment(sketch, "E23.0.22.3", {"start": v(313, -130) * mm, "end": v(313, -140) * mm});
            skLineSegment(sketch, "E23.0.23.0", {"start": v(303, -116) * mm, "end": v(313, -116) * mm});
            skLineSegment(sketch, "E23.0.23.1", {"start": v(303, -126) * mm, "end": v(313, -126) * mm});
            skLineSegment(sketch, "E23.0.23.2", {"start": v(303, -116) * mm, "end": v(303, -126) * mm});
            skLineSegment(sketch, "E23.0.23.3", {"start": v(313, -116) * mm, "end": v(313, -126) * mm});
            skLineSegment(sketch, "E23.0.24.0", {"start": v(303, -102) * mm, "end": v(313, -102) * mm});
            skLineSegment(sketch, "E23.0.24.1", {"start": v(303, -112) * mm, "end": v(313, -112) * mm});
            skLineSegment(sketch, "E23.0.24.2", {"start": v(303, -102) * mm, "end": v(303, -112) * mm});
            skLineSegment(sketch, "E23.0.24.3", {"start": v(313, -102) * mm, "end": v(313, -112) * mm});
            skLineSegment(sketch, "E23.0.25.0", {"start": v(303, -88) * mm, "end": v(313, -88) * mm});
            skLineSegment(sketch, "E23.0.25.1", {"start": v(303, -98) * mm, "end": v(313, -98) * mm});
            skLineSegment(sketch, "E23.0.25.2", {"start": v(303, -88) * mm, "end": v(303, -98) * mm});
            skLineSegment(sketch, "E23.0.25.3", {"start": v(313, -88) * mm, "end": v(313, -98) * mm});
            skLineSegment(sketch, "E23.0.26.0", {"start": v(303, -74) * mm, "end": v(313, -74) * mm});
            skLineSegment(sketch, "E23.0.26.1", {"start": v(303, -84) * mm, "end": v(313, -84) * mm});
            skLineSegment(sketch, "E23.0.26.2", {"start": v(303, -74) * mm, "end": v(303, -84) * mm});
            skLineSegment(sketch, "E23.0.26.3", {"start": v(313, -74) * mm, "end": v(313, -84) * mm});
            skLineSegment(sketch, "E23.0.27.0", {"start": v(303, -60) * mm, "end": v(313, -60) * mm});
            skLineSegment(sketch, "E23.0.27.1", {"start": v(303, -70) * mm, "end": v(313, -70) * mm});
            skLineSegment(sketch, "E23.0.27.2", {"start": v(303, -60) * mm, "end": v(303, -70) * mm});
            skLineSegment(sketch, "E23.0.27.3", {"start": v(313, -60) * mm, "end": v(313, -70) * mm});
            skLineSegment(sketch, "E23.0.28.0", {"start": v(303, -46) * mm, "end": v(313, -46) * mm});
            skLineSegment(sketch, "E23.0.28.1", {"start": v(303, -56) * mm, "end": v(313, -56) * mm});
            skLineSegment(sketch, "E23.0.28.2", {"start": v(303, -46) * mm, "end": v(303, -56) * mm});
            skLineSegment(sketch, "E23.0.28.3", {"start": v(313, -46) * mm, "end": v(313, -56) * mm});
            skLineSegment(sketch, "E23.0.29.0", {"start": v(303, -32) * mm, "end": v(313, -32) * mm});
            skLineSegment(sketch, "E23.0.29.1", {"start": v(303, -42) * mm, "end": v(313, -42) * mm});
            skLineSegment(sketch, "E23.0.29.2", {"start": v(303, -32) * mm, "end": v(303, -42) * mm});
            skLineSegment(sketch, "E23.0.29.3", {"start": v(313, -32) * mm, "end": v(313, -42) * mm});
            skLineSegment(sketch, "E23.0.30.0", {"start": v(303, -18) * mm, "end": v(313, -18) * mm});
            skLineSegment(sketch, "E23.0.30.1", {"start": v(303, -28) * mm, "end": v(313, -28) * mm});
            skLineSegment(sketch, "E23.0.30.2", {"start": v(303, -18) * mm, "end": v(303, -28) * mm});
            skLineSegment(sketch, "E23.0.30.3", {"start": v(313, -18) * mm, "end": v(313, -28) * mm});
            skLineSegment(sketch, "E23.0.31.0", {"start": v(303, -4) * mm, "end": v(313, -4) * mm});
            skLineSegment(sketch, "E23.0.31.1", {"start": v(303, -14) * mm, "end": v(313, -14) * mm});
            skLineSegment(sketch, "E23.0.31.2", {"start": v(303, -4) * mm, "end": v(303, -14) * mm});
            skLineSegment(sketch, "E23.0.31.3", {"start": v(313, -4) * mm, "end": v(313, -14) * mm});
            skLineSegment(sketch, "E23.1.0.0", {"start": v(289, -438) * mm, "end": v(299, -438) * mm});
            skLineSegment(sketch, "E23.1.0.1", {"start": v(289, -448) * mm, "end": v(299, -448) * mm});
            skLineSegment(sketch, "E23.1.0.2", {"start": v(289, -438) * mm, "end": v(289, -448) * mm});
            skLineSegment(sketch, "E23.1.0.3", {"start": v(299, -438) * mm, "end": v(299, -448) * mm});
            skLineSegment(sketch, "E23.1.1.0", {"start": v(289, -424) * mm, "end": v(299, -424) * mm});
            skLineSegment(sketch, "E23.1.1.1", {"start": v(289, -434) * mm, "end": v(299, -434) * mm});
            skLineSegment(sketch, "E23.1.1.2", {"start": v(289, -424) * mm, "end": v(289, -434) * mm});
            skLineSegment(sketch, "E23.1.1.3", {"start": v(299, -424) * mm, "end": v(299, -434) * mm});
            skLineSegment(sketch, "E23.1.2.0", {"start": v(289, -410) * mm, "end": v(299, -410) * mm});
            skLineSegment(sketch, "E23.1.2.1", {"start": v(289, -420) * mm, "end": v(299, -420) * mm});
            skLineSegment(sketch, "E23.1.2.2", {"start": v(289, -410) * mm, "end": v(289, -420) * mm});
            skLineSegment(sketch, "E23.1.2.3", {"start": v(299, -410) * mm, "end": v(299, -420) * mm});
            skLineSegment(sketch, "E23.1.3.0", {"start": v(289, -396) * mm, "end": v(299, -396) * mm});
            skLineSegment(sketch, "E23.1.3.1", {"start": v(289, -406) * mm, "end": v(299, -406) * mm});
            skLineSegment(sketch, "E23.1.3.2", {"start": v(289, -396) * mm, "end": v(289, -406) * mm});
            skLineSegment(sketch, "E23.1.3.3", {"start": v(299, -396) * mm, "end": v(299, -406) * mm});
            skLineSegment(sketch, "E23.1.4.0", {"start": v(289, -382) * mm, "end": v(299, -382) * mm});
            skLineSegment(sketch, "E23.1.4.1", {"start": v(289, -392) * mm, "end": v(299, -392) * mm});
            skLineSegment(sketch, "E23.1.4.2", {"start": v(289, -382) * mm, "end": v(289, -392) * mm});
            skLineSegment(sketch, "E23.1.4.3", {"start": v(299, -382) * mm, "end": v(299, -392) * mm});
            skLineSegment(sketch, "E23.1.5.0", {"start": v(289, -368) * mm, "end": v(299, -368) * mm});
            skLineSegment(sketch, "E23.1.5.1", {"start": v(289, -378) * mm, "end": v(299, -378) * mm});
            skLineSegment(sketch, "E23.1.5.2", {"start": v(289, -368) * mm, "end": v(289, -378) * mm});
            skLineSegment(sketch, "E23.1.5.3", {"start": v(299, -368) * mm, "end": v(299, -378) * mm});
            skLineSegment(sketch, "E23.1.6.0", {"start": v(289, -354) * mm, "end": v(299, -354) * mm});
            skLineSegment(sketch, "E23.1.6.1", {"start": v(289, -364) * mm, "end": v(299, -364) * mm});
            skLineSegment(sketch, "E23.1.6.2", {"start": v(289, -354) * mm, "end": v(289, -364) * mm});
            skLineSegment(sketch, "E23.1.6.3", {"start": v(299, -354) * mm, "end": v(299, -364) * mm});
            skLineSegment(sketch, "E23.1.7.0", {"start": v(289, -340) * mm, "end": v(299, -340) * mm});
            skLineSegment(sketch, "E23.1.7.1", {"start": v(289, -350) * mm, "end": v(299, -350) * mm});
            skLineSegment(sketch, "E23.1.7.2", {"start": v(289, -340) * mm, "end": v(289, -350) * mm});
            skLineSegment(sketch, "E23.1.7.3", {"start": v(299, -340) * mm, "end": v(299, -350) * mm});
            skLineSegment(sketch, "E23.1.8.0", {"start": v(289, -326) * mm, "end": v(299, -326) * mm});
            skLineSegment(sketch, "E23.1.8.1", {"start": v(289, -336) * mm, "end": v(299, -336) * mm});
            skLineSegment(sketch, "E23.1.8.2", {"start": v(289, -326) * mm, "end": v(289, -336) * mm});
            skLineSegment(sketch, "E23.1.8.3", {"start": v(299, -326) * mm, "end": v(299, -336) * mm});
            skLineSegment(sketch, "E23.1.9.0", {"start": v(289, -312) * mm, "end": v(299, -312) * mm});
            skLineSegment(sketch, "E23.1.9.1", {"start": v(289, -322) * mm, "end": v(299, -322) * mm});
            skLineSegment(sketch, "E23.1.9.2", {"start": v(289, -312) * mm, "end": v(289, -322) * mm});
            skLineSegment(sketch, "E23.1.9.3", {"start": v(299, -312) * mm, "end": v(299, -322) * mm});
            skLineSegment(sketch, "E23.1.10.0", {"start": v(289, -298) * mm, "end": v(299, -298) * mm});
            skLineSegment(sketch, "E23.1.10.1", {"start": v(289, -308) * mm, "end": v(299, -308) * mm});
            skLineSegment(sketch, "E23.1.10.2", {"start": v(289, -298) * mm, "end": v(289, -308) * mm});
            skLineSegment(sketch, "E23.1.10.3", {"start": v(299, -298) * mm, "end": v(299, -308) * mm});
            skLineSegment(sketch, "E23.1.11.0", {"start": v(289, -284) * mm, "end": v(299, -284) * mm});
            skLineSegment(sketch, "E23.1.11.1", {"start": v(289, -294) * mm, "end": v(299, -294) * mm});
            skLineSegment(sketch, "E23.1.11.2", {"start": v(289, -284) * mm, "end": v(289, -294) * mm});
            skLineSegment(sketch, "E23.1.11.3", {"start": v(299, -284) * mm, "end": v(299, -294) * mm});
            skLineSegment(sketch, "E23.1.12.0", {"start": v(289, -270) * mm, "end": v(299, -270) * mm});
            skLineSegment(sketch, "E23.1.12.1", {"start": v(289, -280) * mm, "end": v(299, -280) * mm});
            skLineSegment(sketch, "E23.1.12.2", {"start": v(289, -270) * mm, "end": v(289, -280) * mm});
            skLineSegment(sketch, "E23.1.12.3", {"start": v(299, -270) * mm, "end": v(299, -280) * mm});
            skLineSegment(sketch, "E23.1.13.0", {"start": v(289, -256) * mm, "end": v(299, -256) * mm});
            skLineSegment(sketch, "E23.1.13.1", {"start": v(289, -266) * mm, "end": v(299, -266) * mm});
            skLineSegment(sketch, "E23.1.13.2", {"start": v(289, -256) * mm, "end": v(289, -266) * mm});
            skLineSegment(sketch, "E23.1.13.3", {"start": v(299, -256) * mm, "end": v(299, -266) * mm});
            skLineSegment(sketch, "E23.1.14.0", {"start": v(289, -242) * mm, "end": v(299, -242) * mm});
            skLineSegment(sketch, "E23.1.14.1", {"start": v(289, -252) * mm, "end": v(299, -252) * mm});
            skLineSegment(sketch, "E23.1.14.2", {"start": v(289, -242) * mm, "end": v(289, -252) * mm});
            skLineSegment(sketch, "E23.1.14.3", {"start": v(299, -242) * mm, "end": v(299, -252) * mm});
            skLineSegment(sketch, "E23.1.15.0", {"start": v(289, -228) * mm, "end": v(299, -228) * mm});
            skLineSegment(sketch, "E23.1.15.1", {"start": v(289, -238) * mm, "end": v(299, -238) * mm});
            skLineSegment(sketch, "E23.1.15.2", {"start": v(289, -228) * mm, "end": v(289, -238) * mm});
            skLineSegment(sketch, "E23.1.15.3", {"start": v(299, -228) * mm, "end": v(299, -238) * mm});
            skLineSegment(sketch, "E23.1.16.0", {"start": v(289, -214) * mm, "end": v(299, -214) * mm});
            skLineSegment(sketch, "E23.1.16.1", {"start": v(289, -224) * mm, "end": v(299, -224) * mm});
            skLineSegment(sketch, "E23.1.16.2", {"start": v(289, -214) * mm, "end": v(289, -224) * mm});
            skLineSegment(sketch, "E23.1.16.3", {"start": v(299, -214) * mm, "end": v(299, -224) * mm});
            skLineSegment(sketch, "E23.1.17.0", {"start": v(289, -200) * mm, "end": v(299, -200) * mm});
            skLineSegment(sketch, "E23.1.17.1", {"start": v(289, -210) * mm, "end": v(299, -210) * mm});
            skLineSegment(sketch, "E23.1.17.2", {"start": v(289, -200) * mm, "end": v(289, -210) * mm});
            skLineSegment(sketch, "E23.1.17.3", {"start": v(299, -200) * mm, "end": v(299, -210) * mm});
            skLineSegment(sketch, "E23.1.18.0", {"start": v(289, -186) * mm, "end": v(299, -186) * mm});
            skLineSegment(sketch, "E23.1.18.1", {"start": v(289, -196) * mm, "end": v(299, -196) * mm});
            skLineSegment(sketch, "E23.1.18.2", {"start": v(289, -186) * mm, "end": v(289, -196) * mm});
            skLineSegment(sketch, "E23.1.18.3", {"start": v(299, -186) * mm, "end": v(299, -196) * mm});
            skLineSegment(sketch, "E23.1.19.0", {"start": v(289, -172) * mm, "end": v(299, -172) * mm});
            skLineSegment(sketch, "E23.1.19.1", {"start": v(289, -182) * mm, "end": v(299, -182) * mm});
            skLineSegment(sketch, "E23.1.19.2", {"start": v(289, -172) * mm, "end": v(289, -182) * mm});
            skLineSegment(sketch, "E23.1.19.3", {"start": v(299, -172) * mm, "end": v(299, -182) * mm});
            skLineSegment(sketch, "E23.1.20.0", {"start": v(289, -158) * mm, "end": v(299, -158) * mm});
            skLineSegment(sketch, "E23.1.20.1", {"start": v(289, -168) * mm, "end": v(299, -168) * mm});
            skLineSegment(sketch, "E23.1.20.2", {"start": v(289, -158) * mm, "end": v(289, -168) * mm});
            skLineSegment(sketch, "E23.1.20.3", {"start": v(299, -158) * mm, "end": v(299, -168) * mm});
            skLineSegment(sketch, "E23.1.21.0", {"start": v(289, -144) * mm, "end": v(299, -144) * mm});
            skLineSegment(sketch, "E23.1.21.1", {"start": v(289, -154) * mm, "end": v(299, -154) * mm});
            skLineSegment(sketch, "E23.1.21.2", {"start": v(289, -144) * mm, "end": v(289, -154) * mm});
            skLineSegment(sketch, "E23.1.21.3", {"start": v(299, -144) * mm, "end": v(299, -154) * mm});
            skLineSegment(sketch, "E23.1.22.0", {"start": v(289, -130) * mm, "end": v(299, -130) * mm});
            skLineSegment(sketch, "E23.1.22.1", {"start": v(289, -140) * mm, "end": v(299, -140) * mm});
            skLineSegment(sketch, "E23.1.22.2", {"start": v(289, -130) * mm, "end": v(289, -140) * mm});
            skLineSegment(sketch, "E23.1.22.3", {"start": v(299, -130) * mm, "end": v(299, -140) * mm});
            skLineSegment(sketch, "E23.1.23.0", {"start": v(289, -116) * mm, "end": v(299, -116) * mm});
            skLineSegment(sketch, "E23.1.23.1", {"start": v(289, -126) * mm, "end": v(299, -126) * mm});
            skLineSegment(sketch, "E23.1.23.2", {"start": v(289, -116) * mm, "end": v(289, -126) * mm});
            skLineSegment(sketch, "E23.1.23.3", {"start": v(299, -116) * mm, "end": v(299, -126) * mm});
            skLineSegment(sketch, "E23.1.24.0", {"start": v(289, -102) * mm, "end": v(299, -102) * mm});
            skLineSegment(sketch, "E23.1.24.1", {"start": v(289, -112) * mm, "end": v(299, -112) * mm});
            skLineSegment(sketch, "E23.1.24.2", {"start": v(289, -102) * mm, "end": v(289, -112) * mm});
            skLineSegment(sketch, "E23.1.24.3", {"start": v(299, -102) * mm, "end": v(299, -112) * mm});
            skLineSegment(sketch, "E23.1.25.0", {"start": v(289, -88) * mm, "end": v(299, -88) * mm});
            skLineSegment(sketch, "E23.1.25.1", {"start": v(289, -98) * mm, "end": v(299, -98) * mm});
            skLineSegment(sketch, "E23.1.25.2", {"start": v(289, -88) * mm, "end": v(289, -98) * mm});
            skLineSegment(sketch, "E23.1.25.3", {"start": v(299, -88) * mm, "end": v(299, -98) * mm});
            skLineSegment(sketch, "E23.1.26.0", {"start": v(289, -74) * mm, "end": v(299, -74) * mm});
            skLineSegment(sketch, "E23.1.26.1", {"start": v(289, -84) * mm, "end": v(299, -84) * mm});
            skLineSegment(sketch, "E23.1.26.2", {"start": v(289, -74) * mm, "end": v(289, -84) * mm});
            skLineSegment(sketch, "E23.1.26.3", {"start": v(299, -74) * mm, "end": v(299, -84) * mm});
            skLineSegment(sketch, "E23.1.27.0", {"start": v(289, -60) * mm, "end": v(299, -60) * mm});
            skLineSegment(sketch, "E23.1.27.1", {"start": v(289, -70) * mm, "end": v(299, -70) * mm});
            skLineSegment(sketch, "E23.1.27.2", {"start": v(289, -60) * mm, "end": v(289, -70) * mm});
            skLineSegment(sketch, "E23.1.27.3", {"start": v(299, -60) * mm, "end": v(299, -70) * mm});
            skLineSegment(sketch, "E23.1.28.0", {"start": v(289, -46) * mm, "end": v(299, -46) * mm});
            skLineSegment(sketch, "E23.1.28.1", {"start": v(289, -56) * mm, "end": v(299, -56) * mm});
            skLineSegment(sketch, "E23.1.28.2", {"start": v(289, -46) * mm, "end": v(289, -56) * mm});
            skLineSegment(sketch, "E23.1.28.3", {"start": v(299, -46) * mm, "end": v(299, -56) * mm});
            skLineSegment(sketch, "E23.1.29.0", {"start": v(289, -32) * mm, "end": v(299, -32) * mm});
            skLineSegment(sketch, "E23.1.29.1", {"start": v(289, -42) * mm, "end": v(299, -42) * mm});
            skLineSegment(sketch, "E23.1.29.2", {"start": v(289, -32) * mm, "end": v(289, -42) * mm});
            skLineSegment(sketch, "E23.1.29.3", {"start": v(299, -32) * mm, "end": v(299, -42) * mm});
            skLineSegment(sketch, "E23.1.30.0", {"start": v(289, -18) * mm, "end": v(299, -18) * mm});
            skLineSegment(sketch, "E23.1.30.1", {"start": v(289, -28) * mm, "end": v(299, -28) * mm});
            skLineSegment(sketch, "E23.1.30.2", {"start": v(289, -18) * mm, "end": v(289, -28) * mm});
            skLineSegment(sketch, "E23.1.30.3", {"start": v(299, -18) * mm, "end": v(299, -28) * mm});
            skLineSegment(sketch, "E23.1.31.0", {"start": v(289, -4) * mm, "end": v(299, -4) * mm});
            skLineSegment(sketch, "E23.1.31.1", {"start": v(289, -14) * mm, "end": v(299, -14) * mm});
            skLineSegment(sketch, "E23.1.31.2", {"start": v(289, -4) * mm, "end": v(289, -14) * mm});
            skLineSegment(sketch, "E23.1.31.3", {"start": v(299, -4) * mm, "end": v(299, -14) * mm});
            skLineSegment(sketch, "E23.2.0.0", {"start": v(275, -438) * mm, "end": v(285, -438) * mm});
            skLineSegment(sketch, "E23.2.0.1", {"start": v(275, -448) * mm, "end": v(285, -448) * mm});
            skLineSegment(sketch, "E23.2.0.2", {"start": v(275, -438) * mm, "end": v(275, -448) * mm});
            skLineSegment(sketch, "E23.2.0.3", {"start": v(285, -438) * mm, "end": v(285, -448) * mm});
            skLineSegment(sketch, "E23.2.1.0", {"start": v(275, -424) * mm, "end": v(285, -424) * mm});
            skLineSegment(sketch, "E23.2.1.1", {"start": v(275, -434) * mm, "end": v(285, -434) * mm});
            skLineSegment(sketch, "E23.2.1.2", {"start": v(275, -424) * mm, "end": v(275, -434) * mm});
            skLineSegment(sketch, "E23.2.1.3", {"start": v(285, -424) * mm, "end": v(285, -434) * mm});
            skLineSegment(sketch, "E23.2.2.0", {"start": v(275, -410) * mm, "end": v(285, -410) * mm});
            skLineSegment(sketch, "E23.2.2.1", {"start": v(275, -420) * mm, "end": v(285, -420) * mm});
            skLineSegment(sketch, "E23.2.2.2", {"start": v(275, -410) * mm, "end": v(275, -420) * mm});
            skLineSegment(sketch, "E23.2.2.3", {"start": v(285, -410) * mm, "end": v(285, -420) * mm});
            skLineSegment(sketch, "E23.2.3.0", {"start": v(275, -396) * mm, "end": v(285, -396) * mm});
            skLineSegment(sketch, "E23.2.3.1", {"start": v(275, -406) * mm, "end": v(285, -406) * mm});
            skLineSegment(sketch, "E23.2.3.2", {"start": v(275, -396) * mm, "end": v(275, -406) * mm});
            skLineSegment(sketch, "E23.2.3.3", {"start": v(285, -396) * mm, "end": v(285, -406) * mm});
            skLineSegment(sketch, "E23.2.4.0", {"start": v(275, -382) * mm, "end": v(285, -382) * mm});
            skLineSegment(sketch, "E23.2.4.1", {"start": v(275, -392) * mm, "end": v(285, -392) * mm});
            skLineSegment(sketch, "E23.2.4.2", {"start": v(275, -382) * mm, "end": v(275, -392) * mm});
            skLineSegment(sketch, "E23.2.4.3", {"start": v(285, -382) * mm, "end": v(285, -392) * mm});
            skLineSegment(sketch, "E23.2.5.0", {"start": v(275, -368) * mm, "end": v(285, -368) * mm});
            skLineSegment(sketch, "E23.2.5.1", {"start": v(275, -378) * mm, "end": v(285, -378) * mm});
            skLineSegment(sketch, "E23.2.5.2", {"start": v(275, -368) * mm, "end": v(275, -378) * mm});
            skLineSegment(sketch, "E23.2.5.3", {"start": v(285, -368) * mm, "end": v(285, -378) * mm});
            skLineSegment(sketch, "E23.2.6.0", {"start": v(275, -354) * mm, "end": v(285, -354) * mm});
            skLineSegment(sketch, "E23.2.6.1", {"start": v(275, -364) * mm, "end": v(285, -364) * mm});
            skLineSegment(sketch, "E23.2.6.2", {"start": v(275, -354) * mm, "end": v(275, -364) * mm});
            skLineSegment(sketch, "E23.2.6.3", {"start": v(285, -354) * mm, "end": v(285, -364) * mm});
            skLineSegment(sketch, "E23.2.7.0", {"start": v(275, -340) * mm, "end": v(285, -340) * mm});
            skLineSegment(sketch, "E23.2.7.1", {"start": v(275, -350) * mm, "end": v(285, -350) * mm});
            skLineSegment(sketch, "E23.2.7.2", {"start": v(275, -340) * mm, "end": v(275, -350) * mm});
            skLineSegment(sketch, "E23.2.7.3", {"start": v(285, -340) * mm, "end": v(285, -350) * mm});
            skLineSegment(sketch, "E23.2.8.0", {"start": v(275, -326) * mm, "end": v(285, -326) * mm});
            skLineSegment(sketch, "E23.2.8.1", {"start": v(275, -336) * mm, "end": v(285, -336) * mm});
            skLineSegment(sketch, "E23.2.8.2", {"start": v(275, -326) * mm, "end": v(275, -336) * mm});
            skLineSegment(sketch, "E23.2.8.3", {"start": v(285, -326) * mm, "end": v(285, -336) * mm});
            skLineSegment(sketch, "E23.2.9.0", {"start": v(275, -312) * mm, "end": v(285, -312) * mm});
            skLineSegment(sketch, "E23.2.9.1", {"start": v(275, -322) * mm, "end": v(285, -322) * mm});
            skLineSegment(sketch, "E23.2.9.2", {"start": v(275, -312) * mm, "end": v(275, -322) * mm});
            skLineSegment(sketch, "E23.2.9.3", {"start": v(285, -312) * mm, "end": v(285, -322) * mm});
            skLineSegment(sketch, "E23.2.10.0", {"start": v(275, -298) * mm, "end": v(285, -298) * mm});
            skLineSegment(sketch, "E23.2.10.1", {"start": v(275, -308) * mm, "end": v(285, -308) * mm});
            skLineSegment(sketch, "E23.2.10.2", {"start": v(275, -298) * mm, "end": v(275, -308) * mm});
            skLineSegment(sketch, "E23.2.10.3", {"start": v(285, -298) * mm, "end": v(285, -308) * mm});
            skLineSegment(sketch, "E23.2.11.0", {"start": v(275, -284) * mm, "end": v(285, -284) * mm});
            skLineSegment(sketch, "E23.2.11.1", {"start": v(275, -294) * mm, "end": v(285, -294) * mm});
            skLineSegment(sketch, "E23.2.11.2", {"start": v(275, -284) * mm, "end": v(275, -294) * mm});
            skLineSegment(sketch, "E23.2.11.3", {"start": v(285, -284) * mm, "end": v(285, -294) * mm});
            skLineSegment(sketch, "E23.2.12.0", {"start": v(275, -270) * mm, "end": v(285, -270) * mm});
            skLineSegment(sketch, "E23.2.12.1", {"start": v(275, -280) * mm, "end": v(285, -280) * mm});
            skLineSegment(sketch, "E23.2.12.2", {"start": v(275, -270) * mm, "end": v(275, -280) * mm});
            skLineSegment(sketch, "E23.2.12.3", {"start": v(285, -270) * mm, "end": v(285, -280) * mm});
            skLineSegment(sketch, "E23.2.13.0", {"start": v(275, -256) * mm, "end": v(285, -256) * mm});
            skLineSegment(sketch, "E23.2.13.1", {"start": v(275, -266) * mm, "end": v(285, -266) * mm});
            skLineSegment(sketch, "E23.2.13.2", {"start": v(275, -256) * mm, "end": v(275, -266) * mm});
            skLineSegment(sketch, "E23.2.13.3", {"start": v(285, -256) * mm, "end": v(285, -266) * mm});
            skLineSegment(sketch, "E23.2.14.0", {"start": v(275, -242) * mm, "end": v(285, -242) * mm});
            skLineSegment(sketch, "E23.2.14.1", {"start": v(275, -252) * mm, "end": v(285, -252) * mm});
            skLineSegment(sketch, "E23.2.14.2", {"start": v(275, -242) * mm, "end": v(275, -252) * mm});
            skLineSegment(sketch, "E23.2.14.3", {"start": v(285, -242) * mm, "end": v(285, -252) * mm});
            skLineSegment(sketch, "E23.2.15.0", {"start": v(275, -228) * mm, "end": v(285, -228) * mm});
            skLineSegment(sketch, "E23.2.15.1", {"start": v(275, -238) * mm, "end": v(285, -238) * mm});
            skLineSegment(sketch, "E23.2.15.2", {"start": v(275, -228) * mm, "end": v(275, -238) * mm});
            skLineSegment(sketch, "E23.2.15.3", {"start": v(285, -228) * mm, "end": v(285, -238) * mm});
            skLineSegment(sketch, "E23.2.16.0", {"start": v(275, -214) * mm, "end": v(285, -214) * mm});
            skLineSegment(sketch, "E23.2.16.1", {"start": v(275, -224) * mm, "end": v(285, -224) * mm});
            skLineSegment(sketch, "E23.2.16.2", {"start": v(275, -214) * mm, "end": v(275, -224) * mm});
            skLineSegment(sketch, "E23.2.16.3", {"start": v(285, -214) * mm, "end": v(285, -224) * mm});
            skLineSegment(sketch, "E23.2.17.0", {"start": v(275, -200) * mm, "end": v(285, -200) * mm});
            skLineSegment(sketch, "E23.2.17.1", {"start": v(275, -210) * mm, "end": v(285, -210) * mm});
            skLineSegment(sketch, "E23.2.17.2", {"start": v(275, -200) * mm, "end": v(275, -210) * mm});
            skLineSegment(sketch, "E23.2.17.3", {"start": v(285, -200) * mm, "end": v(285, -210) * mm});
            skLineSegment(sketch, "E23.2.18.0", {"start": v(275, -186) * mm, "end": v(285, -186) * mm});
            skLineSegment(sketch, "E23.2.18.1", {"start": v(275, -196) * mm, "end": v(285, -196) * mm});
            skLineSegment(sketch, "E23.2.18.2", {"start": v(275, -186) * mm, "end": v(275, -196) * mm});
            skLineSegment(sketch, "E23.2.18.3", {"start": v(285, -186) * mm, "end": v(285, -196) * mm});
            skLineSegment(sketch, "E23.2.19.0", {"start": v(275, -172) * mm, "end": v(285, -172) * mm});
            skLineSegment(sketch, "E23.2.19.1", {"start": v(275, -182) * mm, "end": v(285, -182) * mm});
            skLineSegment(sketch, "E23.2.19.2", {"start": v(275, -172) * mm, "end": v(275, -182) * mm});
            skLineSegment(sketch, "E23.2.19.3", {"start": v(285, -172) * mm, "end": v(285, -182) * mm});
            skLineSegment(sketch, "E23.2.20.0", {"start": v(275, -158) * mm, "end": v(285, -158) * mm});
            skLineSegment(sketch, "E23.2.20.1", {"start": v(275, -168) * mm, "end": v(285, -168) * mm});
            skLineSegment(sketch, "E23.2.20.2", {"start": v(275, -158) * mm, "end": v(275, -168) * mm});
            skLineSegment(sketch, "E23.2.20.3", {"start": v(285, -158) * mm, "end": v(285, -168) * mm});
            skLineSegment(sketch, "E23.2.21.0", {"start": v(275, -144) * mm, "end": v(285, -144) * mm});
            skLineSegment(sketch, "E23.2.21.1", {"start": v(275, -154) * mm, "end": v(285, -154) * mm});
            skLineSegment(sketch, "E23.2.21.2", {"start": v(275, -144) * mm, "end": v(275, -154) * mm});
            skLineSegment(sketch, "E23.2.21.3", {"start": v(285, -144) * mm, "end": v(285, -154) * mm});
            skLineSegment(sketch, "E23.2.22.0", {"start": v(275, -130) * mm, "end": v(285, -130) * mm});
            skLineSegment(sketch, "E23.2.22.1", {"start": v(275, -140) * mm, "end": v(285, -140) * mm});
            skLineSegment(sketch, "E23.2.22.2", {"start": v(275, -130) * mm, "end": v(275, -140) * mm});
            skLineSegment(sketch, "E23.2.22.3", {"start": v(285, -130) * mm, "end": v(285, -140) * mm});
            skLineSegment(sketch, "E23.2.23.0", {"start": v(275, -116) * mm, "end": v(285, -116) * mm});
            skLineSegment(sketch, "E23.2.23.1", {"start": v(275, -126) * mm, "end": v(285, -126) * mm});
            skLineSegment(sketch, "E23.2.23.2", {"start": v(275, -116) * mm, "end": v(275, -126) * mm});
            skLineSegment(sketch, "E23.2.23.3", {"start": v(285, -116) * mm, "end": v(285, -126) * mm});
            skLineSegment(sketch, "E23.2.24.0", {"start": v(275, -102) * mm, "end": v(285, -102) * mm});
            skLineSegment(sketch, "E23.2.24.1", {"start": v(275, -112) * mm, "end": v(285, -112) * mm});
            skLineSegment(sketch, "E23.2.24.2", {"start": v(275, -102) * mm, "end": v(275, -112) * mm});
            skLineSegment(sketch, "E23.2.24.3", {"start": v(285, -102) * mm, "end": v(285, -112) * mm});
            skLineSegment(sketch, "E23.2.25.0", {"start": v(275, -88) * mm, "end": v(285, -88) * mm});
            skLineSegment(sketch, "E23.2.25.1", {"start": v(275, -98) * mm, "end": v(285, -98) * mm});
            skLineSegment(sketch, "E23.2.25.2", {"start": v(275, -88) * mm, "end": v(275, -98) * mm});
            skLineSegment(sketch, "E23.2.25.3", {"start": v(285, -88) * mm, "end": v(285, -98) * mm});
            skLineSegment(sketch, "E23.2.26.0", {"start": v(275, -74) * mm, "end": v(285, -74) * mm});
            skLineSegment(sketch, "E23.2.26.1", {"start": v(275, -84) * mm, "end": v(285, -84) * mm});
            skLineSegment(sketch, "E23.2.26.2", {"start": v(275, -74) * mm, "end": v(275, -84) * mm});
            skLineSegment(sketch, "E23.2.26.3", {"start": v(285, -74) * mm, "end": v(285, -84) * mm});
            skLineSegment(sketch, "E23.2.27.0", {"start": v(275, -60) * mm, "end": v(285, -60) * mm});
            skLineSegment(sketch, "E23.2.27.1", {"start": v(275, -70) * mm, "end": v(285, -70) * mm});
            skLineSegment(sketch, "E23.2.27.2", {"start": v(275, -60) * mm, "end": v(275, -70) * mm});
            skLineSegment(sketch, "E23.2.27.3", {"start": v(285, -60) * mm, "end": v(285, -70) * mm});
            skLineSegment(sketch, "E23.2.28.0", {"start": v(275, -46) * mm, "end": v(285, -46) * mm});
            skLineSegment(sketch, "E23.2.28.1", {"start": v(275, -56) * mm, "end": v(285, -56) * mm});
            skLineSegment(sketch, "E23.2.28.2", {"start": v(275, -46) * mm, "end": v(275, -56) * mm});
            skLineSegment(sketch, "E23.2.28.3", {"start": v(285, -46) * mm, "end": v(285, -56) * mm});
            skLineSegment(sketch, "E23.2.29.0", {"start": v(275, -32) * mm, "end": v(285, -32) * mm});
            skLineSegment(sketch, "E23.2.29.1", {"start": v(275, -42) * mm, "end": v(285, -42) * mm});
            skLineSegment(sketch, "E23.2.29.2", {"start": v(275, -32) * mm, "end": v(275, -42) * mm});
            skLineSegment(sketch, "E23.2.29.3", {"start": v(285, -32) * mm, "end": v(285, -42) * mm});
            skLineSegment(sketch, "E23.2.30.0", {"start": v(275, -18) * mm, "end": v(285, -18) * mm});
            skLineSegment(sketch, "E23.2.30.1", {"start": v(275, -28) * mm, "end": v(285, -28) * mm});
            skLineSegment(sketch, "E23.2.30.2", {"start": v(275, -18) * mm, "end": v(275, -28) * mm});
            skLineSegment(sketch, "E23.2.30.3", {"start": v(285, -18) * mm, "end": v(285, -28) * mm});
            skLineSegment(sketch, "E23.2.31.0", {"start": v(275, -4) * mm, "end": v(285, -4) * mm});
            skLineSegment(sketch, "E23.2.31.1", {"start": v(275, -14) * mm, "end": v(285, -14) * mm});
            skLineSegment(sketch, "E23.2.31.2", {"start": v(275, -4) * mm, "end": v(275, -14) * mm});
            skLineSegment(sketch, "E23.2.31.3", {"start": v(285, -4) * mm, "end": v(285, -14) * mm});
            skLineSegment(sketch, "E23.3.0.0", {"start": v(261, -438) * mm, "end": v(271, -438) * mm});
            skLineSegment(sketch, "E23.3.0.1", {"start": v(261, -448) * mm, "end": v(271, -448) * mm});
            skLineSegment(sketch, "E23.3.0.2", {"start": v(261, -438) * mm, "end": v(261, -448) * mm});
            skLineSegment(sketch, "E23.3.0.3", {"start": v(271, -438) * mm, "end": v(271, -448) * mm});
            skLineSegment(sketch, "E23.3.1.0", {"start": v(261, -424) * mm, "end": v(271, -424) * mm});
            skLineSegment(sketch, "E23.3.1.1", {"start": v(261, -434) * mm, "end": v(271, -434) * mm});
            skLineSegment(sketch, "E23.3.1.2", {"start": v(261, -424) * mm, "end": v(261, -434) * mm});
            skLineSegment(sketch, "E23.3.1.3", {"start": v(271, -424) * mm, "end": v(271, -434) * mm});
            skLineSegment(sketch, "E23.3.2.0", {"start": v(261, -410) * mm, "end": v(271, -410) * mm});
            skLineSegment(sketch, "E23.3.2.1", {"start": v(261, -420) * mm, "end": v(271, -420) * mm});
            skLineSegment(sketch, "E23.3.2.2", {"start": v(261, -410) * mm, "end": v(261, -420) * mm});
            skLineSegment(sketch, "E23.3.2.3", {"start": v(271, -410) * mm, "end": v(271, -420) * mm});
            skLineSegment(sketch, "E23.3.3.0", {"start": v(261, -396) * mm, "end": v(271, -396) * mm});
            skLineSegment(sketch, "E23.3.3.1", {"start": v(261, -406) * mm, "end": v(271, -406) * mm});
            skLineSegment(sketch, "E23.3.3.2", {"start": v(261, -396) * mm, "end": v(261, -406) * mm});
            skLineSegment(sketch, "E23.3.3.3", {"start": v(271, -396) * mm, "end": v(271, -406) * mm});
            skLineSegment(sketch, "E23.3.4.0", {"start": v(261, -382) * mm, "end": v(271, -382) * mm});
            skLineSegment(sketch, "E23.3.4.1", {"start": v(261, -392) * mm, "end": v(271, -392) * mm});
            skLineSegment(sketch, "E23.3.4.2", {"start": v(261, -382) * mm, "end": v(261, -392) * mm});
            skLineSegment(sketch, "E23.3.4.3", {"start": v(271, -382) * mm, "end": v(271, -392) * mm});
            skLineSegment(sketch, "E23.3.5.0", {"start": v(261, -368) * mm, "end": v(271, -368) * mm});
            skLineSegment(sketch, "E23.3.5.1", {"start": v(261, -378) * mm, "end": v(271, -378) * mm});
            skLineSegment(sketch, "E23.3.5.2", {"start": v(261, -368) * mm, "end": v(261, -378) * mm});
            skLineSegment(sketch, "E23.3.5.3", {"start": v(271, -368) * mm, "end": v(271, -378) * mm});
            skLineSegment(sketch, "E23.3.6.0", {"start": v(261, -354) * mm, "end": v(271, -354) * mm});
            skLineSegment(sketch, "E23.3.6.1", {"start": v(261, -364) * mm, "end": v(271, -364) * mm});
            skLineSegment(sketch, "E23.3.6.2", {"start": v(261, -354) * mm, "end": v(261, -364) * mm});
            skLineSegment(sketch, "E23.3.6.3", {"start": v(271, -354) * mm, "end": v(271, -364) * mm});
            skLineSegment(sketch, "E23.3.7.0", {"start": v(261, -340) * mm, "end": v(271, -340) * mm});
            skLineSegment(sketch, "E23.3.7.1", {"start": v(261, -350) * mm, "end": v(271, -350) * mm});
            skLineSegment(sketch, "E23.3.7.2", {"start": v(261, -340) * mm, "end": v(261, -350) * mm});
            skLineSegment(sketch, "E23.3.7.3", {"start": v(271, -340) * mm, "end": v(271, -350) * mm});
            skLineSegment(sketch, "E23.3.8.0", {"start": v(261, -326) * mm, "end": v(271, -326) * mm});
            skLineSegment(sketch, "E23.3.8.1", {"start": v(261, -336) * mm, "end": v(271, -336) * mm});
            skLineSegment(sketch, "E23.3.8.2", {"start": v(261, -326) * mm, "end": v(261, -336) * mm});
            skLineSegment(sketch, "E23.3.8.3", {"start": v(271, -326) * mm, "end": v(271, -336) * mm});
            skLineSegment(sketch, "E23.3.9.0", {"start": v(261, -312) * mm, "end": v(271, -312) * mm});
            skLineSegment(sketch, "E23.3.9.1", {"start": v(261, -322) * mm, "end": v(271, -322) * mm});
            skLineSegment(sketch, "E23.3.9.2", {"start": v(261, -312) * mm, "end": v(261, -322) * mm});
            skLineSegment(sketch, "E23.3.9.3", {"start": v(271, -312) * mm, "end": v(271, -322) * mm});
            skLineSegment(sketch, "E23.3.10.0", {"start": v(261, -298) * mm, "end": v(271, -298) * mm});
            skLineSegment(sketch, "E23.3.10.1", {"start": v(261, -308) * mm, "end": v(271, -308) * mm});
            skLineSegment(sketch, "E23.3.10.2", {"start": v(261, -298) * mm, "end": v(261, -308) * mm});
            skLineSegment(sketch, "E23.3.10.3", {"start": v(271, -298) * mm, "end": v(271, -308) * mm});
            skLineSegment(sketch, "E23.3.11.0", {"start": v(261, -284) * mm, "end": v(271, -284) * mm});
            skLineSegment(sketch, "E23.3.11.1", {"start": v(261, -294) * mm, "end": v(271, -294) * mm});
            skLineSegment(sketch, "E23.3.11.2", {"start": v(261, -284) * mm, "end": v(261, -294) * mm});
            skLineSegment(sketch, "E23.3.11.3", {"start": v(271, -284) * mm, "end": v(271, -294) * mm});
            skLineSegment(sketch, "E23.3.12.0", {"start": v(261, -270) * mm, "end": v(271, -270) * mm});
            skLineSegment(sketch, "E23.3.12.1", {"start": v(261, -280) * mm, "end": v(271, -280) * mm});
            skLineSegment(sketch, "E23.3.12.2", {"start": v(261, -270) * mm, "end": v(261, -280) * mm});
            skLineSegment(sketch, "E23.3.12.3", {"start": v(271, -270) * mm, "end": v(271, -280) * mm});
            skLineSegment(sketch, "E23.3.13.0", {"start": v(261, -256) * mm, "end": v(271, -256) * mm});
            skLineSegment(sketch, "E23.3.13.1", {"start": v(261, -266) * mm, "end": v(271, -266) * mm});
            skLineSegment(sketch, "E23.3.13.2", {"start": v(261, -256) * mm, "end": v(261, -266) * mm});
            skLineSegment(sketch, "E23.3.13.3", {"start": v(271, -256) * mm, "end": v(271, -266) * mm});
            skLineSegment(sketch, "E23.3.14.0", {"start": v(261, -242) * mm, "end": v(271, -242) * mm});
            skLineSegment(sketch, "E23.3.14.1", {"start": v(261, -252) * mm, "end": v(271, -252) * mm});
            skLineSegment(sketch, "E23.3.14.2", {"start": v(261, -242) * mm, "end": v(261, -252) * mm});
            skLineSegment(sketch, "E23.3.14.3", {"start": v(271, -242) * mm, "end": v(271, -252) * mm});
            skLineSegment(sketch, "E23.3.15.0", {"start": v(261, -228) * mm, "end": v(271, -228) * mm});
            skLineSegment(sketch, "E23.3.15.1", {"start": v(261, -238) * mm, "end": v(271, -238) * mm});
            skLineSegment(sketch, "E23.3.15.2", {"start": v(261, -228) * mm, "end": v(261, -238) * mm});
            skLineSegment(sketch, "E23.3.15.3", {"start": v(271, -228) * mm, "end": v(271, -238) * mm});
            skLineSegment(sketch, "E23.3.16.0", {"start": v(261, -214) * mm, "end": v(271, -214) * mm});
            skLineSegment(sketch, "E23.3.16.1", {"start": v(261, -224) * mm, "end": v(271, -224) * mm});
            skLineSegment(sketch, "E23.3.16.2", {"start": v(261, -214) * mm, "end": v(261, -224) * mm});
            skLineSegment(sketch, "E23.3.16.3", {"start": v(271, -214) * mm, "end": v(271, -224) * mm});
            skLineSegment(sketch, "E23.3.17.0", {"start": v(261, -200) * mm, "end": v(271, -200) * mm});
            skLineSegment(sketch, "E23.3.17.1", {"start": v(261, -210) * mm, "end": v(271, -210) * mm});
            skLineSegment(sketch, "E23.3.17.2", {"start": v(261, -200) * mm, "end": v(261, -210) * mm});
            skLineSegment(sketch, "E23.3.17.3", {"start": v(271, -200) * mm, "end": v(271, -210) * mm});
            skLineSegment(sketch, "E23.3.18.0", {"start": v(261, -186) * mm, "end": v(271, -186) * mm});
            skLineSegment(sketch, "E23.3.18.1", {"start": v(261, -196) * mm, "end": v(271, -196) * mm});
            skLineSegment(sketch, "E23.3.18.2", {"start": v(261, -186) * mm, "end": v(261, -196) * mm});
            skLineSegment(sketch, "E23.3.18.3", {"start": v(271, -186) * mm, "end": v(271, -196) * mm});
            skLineSegment(sketch, "E23.3.19.0", {"start": v(261, -172) * mm, "end": v(271, -172) * mm});
            skLineSegment(sketch, "E23.3.19.1", {"start": v(261, -182) * mm, "end": v(271, -182) * mm});
            skLineSegment(sketch, "E23.3.19.2", {"start": v(261, -172) * mm, "end": v(261, -182) * mm});
            skLineSegment(sketch, "E23.3.19.3", {"start": v(271, -172) * mm, "end": v(271, -182) * mm});
            skLineSegment(sketch, "E23.3.20.0", {"start": v(261, -158) * mm, "end": v(271, -158) * mm});
            skLineSegment(sketch, "E23.3.20.1", {"start": v(261, -168) * mm, "end": v(271, -168) * mm});
            skLineSegment(sketch, "E23.3.20.2", {"start": v(261, -158) * mm, "end": v(261, -168) * mm});
            skLineSegment(sketch, "E23.3.20.3", {"start": v(271, -158) * mm, "end": v(271, -168) * mm});
            skLineSegment(sketch, "E23.3.21.0", {"start": v(261, -144) * mm, "end": v(271, -144) * mm});
            skLineSegment(sketch, "E23.3.21.1", {"start": v(261, -154) * mm, "end": v(271, -154) * mm});
            skLineSegment(sketch, "E23.3.21.2", {"start": v(261, -144) * mm, "end": v(261, -154) * mm});
            skLineSegment(sketch, "E23.3.21.3", {"start": v(271, -144) * mm, "end": v(271, -154) * mm});
            skLineSegment(sketch, "E23.3.22.0", {"start": v(261, -130) * mm, "end": v(271, -130) * mm});
            skLineSegment(sketch, "E23.3.22.1", {"start": v(261, -140) * mm, "end": v(271, -140) * mm});
            skLineSegment(sketch, "E23.3.22.2", {"start": v(261, -130) * mm, "end": v(261, -140) * mm});
            skLineSegment(sketch, "E23.3.22.3", {"start": v(271, -130) * mm, "end": v(271, -140) * mm});
            skLineSegment(sketch, "E23.3.23.0", {"start": v(261, -116) * mm, "end": v(271, -116) * mm});
            skLineSegment(sketch, "E23.3.23.1", {"start": v(261, -126) * mm, "end": v(271, -126) * mm});
            skLineSegment(sketch, "E23.3.23.2", {"start": v(261, -116) * mm, "end": v(261, -126) * mm});
            skLineSegment(sketch, "E23.3.23.3", {"start": v(271, -116) * mm, "end": v(271, -126) * mm});
            skLineSegment(sketch, "E23.3.24.0", {"start": v(261, -102) * mm, "end": v(271, -102) * mm});
            skLineSegment(sketch, "E23.3.24.1", {"start": v(261, -112) * mm, "end": v(271, -112) * mm});
            skLineSegment(sketch, "E23.3.24.2", {"start": v(261, -102) * mm, "end": v(261, -112) * mm});
            skLineSegment(sketch, "E23.3.24.3", {"start": v(271, -102) * mm, "end": v(271, -112) * mm});
            skLineSegment(sketch, "E23.3.25.0", {"start": v(261, -88) * mm, "end": v(271, -88) * mm});
            skLineSegment(sketch, "E23.3.25.1", {"start": v(261, -98) * mm, "end": v(271, -98) * mm});
            skLineSegment(sketch, "E23.3.25.2", {"start": v(261, -88) * mm, "end": v(261, -98) * mm});
            skLineSegment(sketch, "E23.3.25.3", {"start": v(271, -88) * mm, "end": v(271, -98) * mm});
            skLineSegment(sketch, "E23.3.26.0", {"start": v(261, -74) * mm, "end": v(271, -74) * mm});
            skLineSegment(sketch, "E23.3.26.1", {"start": v(261, -84) * mm, "end": v(271, -84) * mm});
            skLineSegment(sketch, "E23.3.26.2", {"start": v(261, -74) * mm, "end": v(261, -84) * mm});
            skLineSegment(sketch, "E23.3.26.3", {"start": v(271, -74) * mm, "end": v(271, -84) * mm});
            skLineSegment(sketch, "E23.3.27.0", {"start": v(261, -60) * mm, "end": v(271, -60) * mm});
            skLineSegment(sketch, "E23.3.27.1", {"start": v(261, -70) * mm, "end": v(271, -70) * mm});
            skLineSegment(sketch, "E23.3.27.2", {"start": v(261, -60) * mm, "end": v(261, -70) * mm});
            skLineSegment(sketch, "E23.3.27.3", {"start": v(271, -60) * mm, "end": v(271, -70) * mm});
            skLineSegment(sketch, "E23.3.28.0", {"start": v(261, -46) * mm, "end": v(271, -46) * mm});
            skLineSegment(sketch, "E23.3.28.1", {"start": v(261, -56) * mm, "end": v(271, -56) * mm});
            skLineSegment(sketch, "E23.3.28.2", {"start": v(261, -46) * mm, "end": v(261, -56) * mm});
            skLineSegment(sketch, "E23.3.28.3", {"start": v(271, -46) * mm, "end": v(271, -56) * mm});
            skLineSegment(sketch, "E23.3.29.0", {"start": v(261, -32) * mm, "end": v(271, -32) * mm});
            skLineSegment(sketch, "E23.3.29.1", {"start": v(261, -42) * mm, "end": v(271, -42) * mm});
            skLineSegment(sketch, "E23.3.29.2", {"start": v(261, -32) * mm, "end": v(261, -42) * mm});
            skLineSegment(sketch, "E23.3.29.3", {"start": v(271, -32) * mm, "end": v(271, -42) * mm});
            skLineSegment(sketch, "E23.3.30.0", {"start": v(261, -18) * mm, "end": v(271, -18) * mm});
            skLineSegment(sketch, "E23.3.30.1", {"start": v(261, -28) * mm, "end": v(271, -28) * mm});
            skLineSegment(sketch, "E23.3.30.2", {"start": v(261, -18) * mm, "end": v(261, -28) * mm});
            skLineSegment(sketch, "E23.3.30.3", {"start": v(271, -18) * mm, "end": v(271, -28) * mm});
            skLineSegment(sketch, "E23.3.31.0", {"start": v(261, -4) * mm, "end": v(271, -4) * mm});
            skLineSegment(sketch, "E23.3.31.1", {"start": v(261, -14) * mm, "end": v(271, -14) * mm});
            skLineSegment(sketch, "E23.3.31.2", {"start": v(261, -4) * mm, "end": v(261, -14) * mm});
            skLineSegment(sketch, "E23.3.31.3", {"start": v(271, -4) * mm, "end": v(271, -14) * mm});
            skLineSegment(sketch, "E23.direction1", {"start": v(303, -448) * mm, "end": v(289, -448) * mm, "construction": true});
            skLineSegment(sketch, "E23.direction2", {"start": v(303, -448) * mm, "end": v(303, -434) * mm, "construction": true});
            skSolve(sketch);
        }
        {
            var Q0;
            Q0=qCreatedBy(makeId("Top.planeOp"),FACE);
            var sketch = newSketch(context, id + "F2", { "sketchPlane" : qUnion([Q0])});
            skLineSegment(sketch, "E24.bottom", {"start": v(-317, 0) * mm, "end": v(-275, 0) * mm});
            skLineSegment(sketch, "E24.top", {"start": v(-317, -28) * mm, "end": v(-275, -28) * mm});
            skLineSegment(sketch, "E24.left", {"start": v(-317, 0) * mm, "end": v(-317, -28) * mm});
            skLineSegment(sketch, "E24.right", {"start": v(-275, 0) * mm, "end": v(-275, -28) * mm});
            skLineSegment(sketch, "E25.bottom", {"start": v(-317, -102) * mm, "end": v(-275, -102) * mm});
            skLineSegment(sketch, "E25.top", {"start": v(-317, -126) * mm, "end": v(-275, -126) * mm});
            skLineSegment(sketch, "E25.left", {"start": v(-317, -102) * mm, "end": v(-317, -126) * mm});
            skLineSegment(sketch, "E25.right", {"start": v(-275, -102) * mm, "end": v(-275, -126) * mm});
            skLineSegment(sketch, "E26.bottom", {"start": v(-317, -158) * mm, "end": v(-275, -158) * mm});
            skLineSegment(sketch, "E26.top", {"start": v(-317, -266) * mm, "end": v(-275, -266) * mm});
            skLineSegment(sketch, "E26.left", {"start": v(-317, -158) * mm, "end": v(-317, -266) * mm});
            skLineSegment(sketch, "E26.right", {"start": v(-275, -158) * mm, "end": v(-275, -266) * mm});
            skLineSegment(sketch, "E27.bottom", {"start": v(289, 0) * mm, "end": v(317, 0) * mm});
            skLineSegment(sketch, "E27.top", {"start": v(289, -28) * mm, "end": v(317, -28) * mm});
            skLineSegment(sketch, "E27.left", {"start": v(289, 0) * mm, "end": v(289, -28) * mm});
            skLineSegment(sketch, "E27.right", {"start": v(317, 0) * mm, "end": v(317, -28) * mm});
            skLineSegment(sketch, "E28.bottom", {"start": v(289, -102) * mm, "end": v(317, -102) * mm});
            skLineSegment(sketch, "E28.top", {"start": v(289, -126) * mm, "end": v(317, -126) * mm});
            skLineSegment(sketch, "E28.left", {"start": v(289, -102) * mm, "end": v(289, -126) * mm});
            skLineSegment(sketch, "E28.right", {"start": v(317, -102) * mm, "end": v(317, -126) * mm});
            skLineSegment(sketch, "E29.bottom", {"start": v(289, -158) * mm, "end": v(317, -158) * mm});
            skLineSegment(sketch, "E29.top", {"start": v(289, -266) * mm, "end": v(317, -266) * mm});
            skLineSegment(sketch, "E29.left", {"start": v(289, -158) * mm, "end": v(289, -266) * mm});
            skLineSegment(sketch, "E29.right", {"start": v(317, -158) * mm, "end": v(317, -266) * mm});
            skSolve(sketch);
        }
        {
            var Q0;
            Q0=qCreatedBy(makeId("Top.planeOp"),FACE);
            var sketch = newSketch(context, id + "F3", { "sketchPlane" : qUnion([Q0])});
            skLineSegment(sketch, "E30.bottom", {"start": v(-257, -438) * mm, "end": v(-247, -438) * mm});
            skLineSegment(sketch, "E30.top", {"start": v(-257, -448) * mm, "end": v(-247, -448) * mm});
            skLineSegment(sketch, "E30.left", {"start": v(-257, -438) * mm, "end": v(-257, -448) * mm});
            skLineSegment(sketch, "E30.right", {"start": v(-247, -438) * mm, "end": v(-247, -448) * mm});
            skLineSegment(sketch, "E31.0.1.0", {"start": v(-257, -424) * mm, "end": v(-247, -424) * mm});
            skLineSegment(sketch, "E31.0.1.1", {"start": v(-257, -434) * mm, "end": v(-247, -434) * mm});
            skLineSegment(sketch, "E31.0.1.2", {"start": v(-257, -424) * mm, "end": v(-257, -434) * mm});
            skLineSegment(sketch, "E31.0.1.3", {"start": v(-247, -424) * mm, "end": v(-247, -434) * mm});
            skLineSegment(sketch, "E31.0.2.0", {"start": v(-257, -410) * mm, "end": v(-247, -410) * mm});
            skLineSegment(sketch, "E31.0.2.1", {"start": v(-257, -420) * mm, "end": v(-247, -420) * mm});
            skLineSegment(sketch, "E31.0.2.2", {"start": v(-257, -410) * mm, "end": v(-257, -420) * mm});
            skLineSegment(sketch, "E31.0.2.3", {"start": v(-247, -410) * mm, "end": v(-247, -420) * mm});
            skLineSegment(sketch, "E31.0.3.0", {"start": v(-257, -396) * mm, "end": v(-247, -396) * mm});
            skLineSegment(sketch, "E31.0.3.1", {"start": v(-257, -406) * mm, "end": v(-247, -406) * mm});
            skLineSegment(sketch, "E31.0.3.2", {"start": v(-257, -396) * mm, "end": v(-257, -406) * mm});
            skLineSegment(sketch, "E31.0.3.3", {"start": v(-247, -396) * mm, "end": v(-247, -406) * mm});
            skLineSegment(sketch, "E31.0.4.0", {"start": v(-257, -382) * mm, "end": v(-247, -382) * mm});
            skLineSegment(sketch, "E31.0.4.1", {"start": v(-257, -392) * mm, "end": v(-247, -392) * mm});
            skLineSegment(sketch, "E31.0.4.2", {"start": v(-257, -382) * mm, "end": v(-257, -392) * mm});
            skLineSegment(sketch, "E31.0.4.3", {"start": v(-247, -382) * mm, "end": v(-247, -392) * mm});
            skLineSegment(sketch, "E31.0.5.0", {"start": v(-257, -368) * mm, "end": v(-247, -368) * mm});
            skLineSegment(sketch, "E31.0.5.1", {"start": v(-257, -378) * mm, "end": v(-247, -378) * mm});
            skLineSegment(sketch, "E31.0.5.2", {"start": v(-257, -368) * mm, "end": v(-257, -378) * mm});
            skLineSegment(sketch, "E31.0.5.3", {"start": v(-247, -368) * mm, "end": v(-247, -378) * mm});
            skLineSegment(sketch, "E31.0.6.0", {"start": v(-257, -354) * mm, "end": v(-247, -354) * mm});
            skLineSegment(sketch, "E31.0.6.1", {"start": v(-257, -364) * mm, "end": v(-247, -364) * mm});
            skLineSegment(sketch, "E31.0.6.2", {"start": v(-257, -354) * mm, "end": v(-257, -364) * mm});
            skLineSegment(sketch, "E31.0.6.3", {"start": v(-247, -354) * mm, "end": v(-247, -364) * mm});
            skLineSegment(sketch, "E31.0.7.0", {"start": v(-257, -340) * mm, "end": v(-247, -340) * mm});
            skLineSegment(sketch, "E31.0.7.1", {"start": v(-257, -350) * mm, "end": v(-247, -350) * mm});
            skLineSegment(sketch, "E31.0.7.2", {"start": v(-257, -340) * mm, "end": v(-257, -350) * mm});
            skLineSegment(sketch, "E31.0.7.3", {"start": v(-247, -340) * mm, "end": v(-247, -350) * mm});
            skLineSegment(sketch, "E31.0.8.0", {"start": v(-257, -326) * mm, "end": v(-247, -326) * mm});
            skLineSegment(sketch, "E31.0.8.1", {"start": v(-257, -336) * mm, "end": v(-247, -336) * mm});
            skLineSegment(sketch, "E31.0.8.2", {"start": v(-257, -326) * mm, "end": v(-257, -336) * mm});
            skLineSegment(sketch, "E31.0.8.3", {"start": v(-247, -326) * mm, "end": v(-247, -336) * mm});
            skLineSegment(sketch, "E31.0.9.0", {"start": v(-257, -312) * mm, "end": v(-247, -312) * mm});
            skLineSegment(sketch, "E31.0.9.1", {"start": v(-257, -322) * mm, "end": v(-247, -322) * mm});
            skLineSegment(sketch, "E31.0.9.2", {"start": v(-257, -312) * mm, "end": v(-257, -322) * mm});
            skLineSegment(sketch, "E31.0.9.3", {"start": v(-247, -312) * mm, "end": v(-247, -322) * mm});
            skLineSegment(sketch, "E31.0.10.0", {"start": v(-257, -298) * mm, "end": v(-247, -298) * mm});
            skLineSegment(sketch, "E31.0.10.1", {"start": v(-257, -308) * mm, "end": v(-247, -308) * mm});
            skLineSegment(sketch, "E31.0.10.2", {"start": v(-257, -298) * mm, "end": v(-257, -308) * mm});
            skLineSegment(sketch, "E31.0.10.3", {"start": v(-247, -298) * mm, "end": v(-247, -308) * mm});
            skLineSegment(sketch, "E31.0.11.0", {"start": v(-257, -284) * mm, "end": v(-247, -284) * mm});
            skLineSegment(sketch, "E31.0.11.1", {"start": v(-257, -294) * mm, "end": v(-247, -294) * mm});
            skLineSegment(sketch, "E31.0.11.2", {"start": v(-257, -284) * mm, "end": v(-257, -294) * mm});
            skLineSegment(sketch, "E31.0.11.3", {"start": v(-247, -284) * mm, "end": v(-247, -294) * mm});
            skLineSegment(sketch, "E31.0.12.0", {"start": v(-257, -270) * mm, "end": v(-247, -270) * mm});
            skLineSegment(sketch, "E31.0.12.1", {"start": v(-257, -280) * mm, "end": v(-247, -280) * mm});
            skLineSegment(sketch, "E31.0.12.2", {"start": v(-257, -270) * mm, "end": v(-257, -280) * mm});
            skLineSegment(sketch, "E31.0.12.3", {"start": v(-247, -270) * mm, "end": v(-247, -280) * mm});
            skLineSegment(sketch, "E31.0.13.0", {"start": v(-257, -256) * mm, "end": v(-247, -256) * mm});
            skLineSegment(sketch, "E31.0.13.1", {"start": v(-257, -266) * mm, "end": v(-247, -266) * mm});
            skLineSegment(sketch, "E31.0.13.2", {"start": v(-257, -256) * mm, "end": v(-257, -266) * mm});
            skLineSegment(sketch, "E31.0.13.3", {"start": v(-247, -256) * mm, "end": v(-247, -266) * mm});
            skLineSegment(sketch, "E31.0.14.0", {"start": v(-257, -242) * mm, "end": v(-247, -242) * mm});
            skLineSegment(sketch, "E31.0.14.1", {"start": v(-257, -252) * mm, "end": v(-247, -252) * mm});
            skLineSegment(sketch, "E31.0.14.2", {"start": v(-257, -242) * mm, "end": v(-257, -252) * mm});
            skLineSegment(sketch, "E31.0.14.3", {"start": v(-247, -242) * mm, "end": v(-247, -252) * mm});
            skLineSegment(sketch, "E31.0.15.0", {"start": v(-257, -228) * mm, "end": v(-247, -228) * mm});
            skLineSegment(sketch, "E31.0.15.1", {"start": v(-257, -238) * mm, "end": v(-247, -238) * mm});
            skLineSegment(sketch, "E31.0.15.2", {"start": v(-257, -228) * mm, "end": v(-257, -238) * mm});
            skLineSegment(sketch, "E31.0.15.3", {"start": v(-247, -228) * mm, "end": v(-247, -238) * mm});
            skLineSegment(sketch, "E31.0.16.0", {"start": v(-257, -214) * mm, "end": v(-247, -214) * mm});
            skLineSegment(sketch, "E31.0.16.1", {"start": v(-257, -224) * mm, "end": v(-247, -224) * mm});
            skLineSegment(sketch, "E31.0.16.2", {"start": v(-257, -214) * mm, "end": v(-257, -224) * mm});
            skLineSegment(sketch, "E31.0.16.3", {"start": v(-247, -214) * mm, "end": v(-247, -224) * mm});
            skLineSegment(sketch, "E31.0.17.0", {"start": v(-257, -200) * mm, "end": v(-247, -200) * mm});
            skLineSegment(sketch, "E31.0.17.1", {"start": v(-257, -210) * mm, "end": v(-247, -210) * mm});
            skLineSegment(sketch, "E31.0.17.2", {"start": v(-257, -200) * mm, "end": v(-257, -210) * mm});
            skLineSegment(sketch, "E31.0.17.3", {"start": v(-247, -200) * mm, "end": v(-247, -210) * mm});
            skLineSegment(sketch, "E31.0.18.0", {"start": v(-257, -186) * mm, "end": v(-247, -186) * mm});
            skLineSegment(sketch, "E31.0.18.1", {"start": v(-257, -196) * mm, "end": v(-247, -196) * mm});
            skLineSegment(sketch, "E31.0.18.2", {"start": v(-257, -186) * mm, "end": v(-257, -196) * mm});
            skLineSegment(sketch, "E31.0.18.3", {"start": v(-247, -186) * mm, "end": v(-247, -196) * mm});
            skLineSegment(sketch, "E31.0.19.0", {"start": v(-257, -172) * mm, "end": v(-247, -172) * mm});
            skLineSegment(sketch, "E31.0.19.1", {"start": v(-257, -182) * mm, "end": v(-247, -182) * mm});
            skLineSegment(sketch, "E31.0.19.2", {"start": v(-257, -172) * mm, "end": v(-257, -182) * mm});
            skLineSegment(sketch, "E31.0.19.3", {"start": v(-247, -172) * mm, "end": v(-247, -182) * mm});
            skLineSegment(sketch, "E31.0.20.0", {"start": v(-257, -158) * mm, "end": v(-247, -158) * mm});
            skLineSegment(sketch, "E31.0.20.1", {"start": v(-257, -168) * mm, "end": v(-247, -168) * mm});
            skLineSegment(sketch, "E31.0.20.2", {"start": v(-257, -158) * mm, "end": v(-257, -168) * mm});
            skLineSegment(sketch, "E31.0.20.3", {"start": v(-247, -158) * mm, "end": v(-247, -168) * mm});
            skLineSegment(sketch, "E31.0.21.0", {"start": v(-257, -144) * mm, "end": v(-247, -144) * mm});
            skLineSegment(sketch, "E31.0.21.1", {"start": v(-257, -154) * mm, "end": v(-247, -154) * mm});
            skLineSegment(sketch, "E31.0.21.2", {"start": v(-257, -144) * mm, "end": v(-257, -154) * mm});
            skLineSegment(sketch, "E31.0.21.3", {"start": v(-247, -144) * mm, "end": v(-247, -154) * mm});
            skLineSegment(sketch, "E31.0.22.0", {"start": v(-257, -130) * mm, "end": v(-247, -130) * mm});
            skLineSegment(sketch, "E31.0.22.1", {"start": v(-257, -140) * mm, "end": v(-247, -140) * mm});
            skLineSegment(sketch, "E31.0.22.2", {"start": v(-257, -130) * mm, "end": v(-257, -140) * mm});
            skLineSegment(sketch, "E31.0.22.3", {"start": v(-247, -130) * mm, "end": v(-247, -140) * mm});
            skLineSegment(sketch, "E31.0.23.0", {"start": v(-257, -116) * mm, "end": v(-247, -116) * mm});
            skLineSegment(sketch, "E31.0.23.1", {"start": v(-257, -126) * mm, "end": v(-247, -126) * mm});
            skLineSegment(sketch, "E31.0.23.2", {"start": v(-257, -116) * mm, "end": v(-257, -126) * mm});
            skLineSegment(sketch, "E31.0.23.3", {"start": v(-247, -116) * mm, "end": v(-247, -126) * mm});
            skLineSegment(sketch, "E31.0.24.0", {"start": v(-257, -102) * mm, "end": v(-247, -102) * mm});
            skLineSegment(sketch, "E31.0.24.1", {"start": v(-257, -112) * mm, "end": v(-247, -112) * mm});
            skLineSegment(sketch, "E31.0.24.2", {"start": v(-257, -102) * mm, "end": v(-257, -112) * mm});
            skLineSegment(sketch, "E31.0.24.3", {"start": v(-247, -102) * mm, "end": v(-247, -112) * mm});
            skLineSegment(sketch, "E31.0.25.0", {"start": v(-257, -88) * mm, "end": v(-247, -88) * mm});
            skLineSegment(sketch, "E31.0.25.1", {"start": v(-257, -98) * mm, "end": v(-247, -98) * mm});
            skLineSegment(sketch, "E31.0.25.2", {"start": v(-257, -88) * mm, "end": v(-257, -98) * mm});
            skLineSegment(sketch, "E31.0.25.3", {"start": v(-247, -88) * mm, "end": v(-247, -98) * mm});
            skLineSegment(sketch, "E31.0.26.0", {"start": v(-257, -74) * mm, "end": v(-247, -74) * mm});
            skLineSegment(sketch, "E31.0.26.1", {"start": v(-257, -84) * mm, "end": v(-247, -84) * mm});
            skLineSegment(sketch, "E31.0.26.2", {"start": v(-257, -74) * mm, "end": v(-257, -84) * mm});
            skLineSegment(sketch, "E31.0.26.3", {"start": v(-247, -74) * mm, "end": v(-247, -84) * mm});
            skLineSegment(sketch, "E31.0.27.0", {"start": v(-257, -60) * mm, "end": v(-247, -60) * mm});
            skLineSegment(sketch, "E31.0.27.1", {"start": v(-257, -70) * mm, "end": v(-247, -70) * mm});
            skLineSegment(sketch, "E31.0.27.2", {"start": v(-257, -60) * mm, "end": v(-257, -70) * mm});
            skLineSegment(sketch, "E31.0.27.3", {"start": v(-247, -60) * mm, "end": v(-247, -70) * mm});
            skLineSegment(sketch, "E31.0.28.0", {"start": v(-257, -46) * mm, "end": v(-247, -46) * mm});
            skLineSegment(sketch, "E31.0.28.1", {"start": v(-257, -56) * mm, "end": v(-247, -56) * mm});
            skLineSegment(sketch, "E31.0.28.2", {"start": v(-257, -46) * mm, "end": v(-257, -56) * mm});
            skLineSegment(sketch, "E31.0.28.3", {"start": v(-247, -46) * mm, "end": v(-247, -56) * mm});
            skLineSegment(sketch, "E31.0.29.0", {"start": v(-257, -32) * mm, "end": v(-247, -32) * mm});
            skLineSegment(sketch, "E31.0.29.1", {"start": v(-257, -42) * mm, "end": v(-247, -42) * mm});
            skLineSegment(sketch, "E31.0.29.2", {"start": v(-257, -32) * mm, "end": v(-257, -42) * mm});
            skLineSegment(sketch, "E31.0.29.3", {"start": v(-247, -32) * mm, "end": v(-247, -42) * mm});
            skLineSegment(sketch, "E31.0.30.0", {"start": v(-257, -18) * mm, "end": v(-247, -18) * mm});
            skLineSegment(sketch, "E31.0.30.1", {"start": v(-257, -28) * mm, "end": v(-247, -28) * mm});
            skLineSegment(sketch, "E31.0.30.2", {"start": v(-257, -18) * mm, "end": v(-257, -28) * mm});
            skLineSegment(sketch, "E31.0.30.3", {"start": v(-247, -18) * mm, "end": v(-247, -28) * mm});
            skLineSegment(sketch, "E31.0.31.0", {"start": v(-257, -4) * mm, "end": v(-247, -4) * mm});
            skLineSegment(sketch, "E31.0.31.1", {"start": v(-257, -14) * mm, "end": v(-247, -14) * mm});
            skLineSegment(sketch, "E31.0.31.2", {"start": v(-257, -4) * mm, "end": v(-257, -14) * mm});
            skLineSegment(sketch, "E31.0.31.3", {"start": v(-247, -4) * mm, "end": v(-247, -14) * mm});
            skLineSegment(sketch, "E31.1.0.0", {"start": v(-243, -438) * mm, "end": v(-233, -438) * mm});
            skLineSegment(sketch, "E31.1.0.1", {"start": v(-243, -448) * mm, "end": v(-233, -448) * mm});
            skLineSegment(sketch, "E31.1.0.2", {"start": v(-243, -438) * mm, "end": v(-243, -448) * mm});
            skLineSegment(sketch, "E31.1.0.3", {"start": v(-233, -438) * mm, "end": v(-233, -448) * mm});
            skLineSegment(sketch, "E31.1.1.0", {"start": v(-243, -424) * mm, "end": v(-233, -424) * mm});
            skLineSegment(sketch, "E31.1.1.1", {"start": v(-243, -434) * mm, "end": v(-233, -434) * mm});
            skLineSegment(sketch, "E31.1.1.2", {"start": v(-243, -424) * mm, "end": v(-243, -434) * mm});
            skLineSegment(sketch, "E31.1.1.3", {"start": v(-233, -424) * mm, "end": v(-233, -434) * mm});
            skLineSegment(sketch, "E31.1.2.0", {"start": v(-243, -410) * mm, "end": v(-233, -410) * mm});
            skLineSegment(sketch, "E31.1.2.1", {"start": v(-243, -420) * mm, "end": v(-233, -420) * mm});
            skLineSegment(sketch, "E31.1.2.2", {"start": v(-243, -410) * mm, "end": v(-243, -420) * mm});
            skLineSegment(sketch, "E31.1.2.3", {"start": v(-233, -410) * mm, "end": v(-233, -420) * mm});
            skLineSegment(sketch, "E31.1.3.0", {"start": v(-243, -396) * mm, "end": v(-233, -396) * mm});
            skLineSegment(sketch, "E31.1.3.1", {"start": v(-243, -406) * mm, "end": v(-233, -406) * mm});
            skLineSegment(sketch, "E31.1.3.2", {"start": v(-243, -396) * mm, "end": v(-243, -406) * mm});
            skLineSegment(sketch, "E31.1.3.3", {"start": v(-233, -396) * mm, "end": v(-233, -406) * mm});
            skLineSegment(sketch, "E31.1.4.0", {"start": v(-243, -382) * mm, "end": v(-233, -382) * mm});
            skLineSegment(sketch, "E31.1.4.1", {"start": v(-243, -392) * mm, "end": v(-233, -392) * mm});
            skLineSegment(sketch, "E31.1.4.2", {"start": v(-243, -382) * mm, "end": v(-243, -392) * mm});
            skLineSegment(sketch, "E31.1.4.3", {"start": v(-233, -382) * mm, "end": v(-233, -392) * mm});
            skLineSegment(sketch, "E31.1.5.0", {"start": v(-243, -368) * mm, "end": v(-233, -368) * mm});
            skLineSegment(sketch, "E31.1.5.1", {"start": v(-243, -378) * mm, "end": v(-233, -378) * mm});
            skLineSegment(sketch, "E31.1.5.2", {"start": v(-243, -368) * mm, "end": v(-243, -378) * mm});
            skLineSegment(sketch, "E31.1.5.3", {"start": v(-233, -368) * mm, "end": v(-233, -378) * mm});
            skLineSegment(sketch, "E31.1.6.0", {"start": v(-243, -354) * mm, "end": v(-233, -354) * mm});
            skLineSegment(sketch, "E31.1.6.1", {"start": v(-243, -364) * mm, "end": v(-233, -364) * mm});
            skLineSegment(sketch, "E31.1.6.2", {"start": v(-243, -354) * mm, "end": v(-243, -364) * mm});
            skLineSegment(sketch, "E31.1.6.3", {"start": v(-233, -354) * mm, "end": v(-233, -364) * mm});
            skLineSegment(sketch, "E31.1.7.0", {"start": v(-243, -340) * mm, "end": v(-233, -340) * mm});
            skLineSegment(sketch, "E31.1.7.1", {"start": v(-243, -350) * mm, "end": v(-233, -350) * mm});
            skLineSegment(sketch, "E31.1.7.2", {"start": v(-243, -340) * mm, "end": v(-243, -350) * mm});
            skLineSegment(sketch, "E31.1.7.3", {"start": v(-233, -340) * mm, "end": v(-233, -350) * mm});
            skLineSegment(sketch, "E31.1.8.0", {"start": v(-243, -326) * mm, "end": v(-233, -326) * mm});
            skLineSegment(sketch, "E31.1.8.1", {"start": v(-243, -336) * mm, "end": v(-233, -336) * mm});
            skLineSegment(sketch, "E31.1.8.2", {"start": v(-243, -326) * mm, "end": v(-243, -336) * mm});
            skLineSegment(sketch, "E31.1.8.3", {"start": v(-233, -326) * mm, "end": v(-233, -336) * mm});
            skLineSegment(sketch, "E31.1.9.0", {"start": v(-243, -312) * mm, "end": v(-233, -312) * mm});
            skLineSegment(sketch, "E31.1.9.1", {"start": v(-243, -322) * mm, "end": v(-233, -322) * mm});
            skLineSegment(sketch, "E31.1.9.2", {"start": v(-243, -312) * mm, "end": v(-243, -322) * mm});
            skLineSegment(sketch, "E31.1.9.3", {"start": v(-233, -312) * mm, "end": v(-233, -322) * mm});
            skLineSegment(sketch, "E31.1.10.0", {"start": v(-243, -298) * mm, "end": v(-233, -298) * mm});
            skLineSegment(sketch, "E31.1.10.1", {"start": v(-243, -308) * mm, "end": v(-233, -308) * mm});
            skLineSegment(sketch, "E31.1.10.2", {"start": v(-243, -298) * mm, "end": v(-243, -308) * mm});
            skLineSegment(sketch, "E31.1.10.3", {"start": v(-233, -298) * mm, "end": v(-233, -308) * mm});
            skLineSegment(sketch, "E31.1.11.0", {"start": v(-243, -284) * mm, "end": v(-233, -284) * mm});
            skLineSegment(sketch, "E31.1.11.1", {"start": v(-243, -294) * mm, "end": v(-233, -294) * mm});
            skLineSegment(sketch, "E31.1.11.2", {"start": v(-243, -284) * mm, "end": v(-243, -294) * mm});
            skLineSegment(sketch, "E31.1.11.3", {"start": v(-233, -284) * mm, "end": v(-233, -294) * mm});
            skLineSegment(sketch, "E31.1.12.0", {"start": v(-243, -270) * mm, "end": v(-233, -270) * mm});
            skLineSegment(sketch, "E31.1.12.1", {"start": v(-243, -280) * mm, "end": v(-233, -280) * mm});
            skLineSegment(sketch, "E31.1.12.2", {"start": v(-243, -270) * mm, "end": v(-243, -280) * mm});
            skLineSegment(sketch, "E31.1.12.3", {"start": v(-233, -270) * mm, "end": v(-233, -280) * mm});
            skLineSegment(sketch, "E31.1.13.0", {"start": v(-243, -256) * mm, "end": v(-233, -256) * mm});
            skLineSegment(sketch, "E31.1.13.1", {"start": v(-243, -266) * mm, "end": v(-233, -266) * mm});
            skLineSegment(sketch, "E31.1.13.2", {"start": v(-243, -256) * mm, "end": v(-243, -266) * mm});
            skLineSegment(sketch, "E31.1.13.3", {"start": v(-233, -256) * mm, "end": v(-233, -266) * mm});
            skLineSegment(sketch, "E31.1.14.0", {"start": v(-243, -242) * mm, "end": v(-233, -242) * mm});
            skLineSegment(sketch, "E31.1.14.1", {"start": v(-243, -252) * mm, "end": v(-233, -252) * mm});
            skLineSegment(sketch, "E31.1.14.2", {"start": v(-243, -242) * mm, "end": v(-243, -252) * mm});
            skLineSegment(sketch, "E31.1.14.3", {"start": v(-233, -242) * mm, "end": v(-233, -252) * mm});
            skLineSegment(sketch, "E31.1.15.0", {"start": v(-243, -228) * mm, "end": v(-233, -228) * mm});
            skLineSegment(sketch, "E31.1.15.1", {"start": v(-243, -238) * mm, "end": v(-233, -238) * mm});
            skLineSegment(sketch, "E31.1.15.2", {"start": v(-243, -228) * mm, "end": v(-243, -238) * mm});
            skLineSegment(sketch, "E31.1.15.3", {"start": v(-233, -228) * mm, "end": v(-233, -238) * mm});
            skLineSegment(sketch, "E31.1.16.0", {"start": v(-243, -214) * mm, "end": v(-233, -214) * mm});
            skLineSegment(sketch, "E31.1.16.1", {"start": v(-243, -224) * mm, "end": v(-233, -224) * mm});
            skLineSegment(sketch, "E31.1.16.2", {"start": v(-243, -214) * mm, "end": v(-243, -224) * mm});
            skLineSegment(sketch, "E31.1.16.3", {"start": v(-233, -214) * mm, "end": v(-233, -224) * mm});
            skLineSegment(sketch, "E31.1.17.0", {"start": v(-243, -200) * mm, "end": v(-233, -200) * mm});
            skLineSegment(sketch, "E31.1.17.1", {"start": v(-243, -210) * mm, "end": v(-233, -210) * mm});
            skLineSegment(sketch, "E31.1.17.2", {"start": v(-243, -200) * mm, "end": v(-243, -210) * mm});
            skLineSegment(sketch, "E31.1.17.3", {"start": v(-233, -200) * mm, "end": v(-233, -210) * mm});
            skLineSegment(sketch, "E31.1.18.0", {"start": v(-243, -186) * mm, "end": v(-233, -186) * mm});
            skLineSegment(sketch, "E31.1.18.1", {"start": v(-243, -196) * mm, "end": v(-233, -196) * mm});
            skLineSegment(sketch, "E31.1.18.2", {"start": v(-243, -186) * mm, "end": v(-243, -196) * mm});
            skLineSegment(sketch, "E31.1.18.3", {"start": v(-233, -186) * mm, "end": v(-233, -196) * mm});
            skLineSegment(sketch, "E31.1.19.0", {"start": v(-243, -172) * mm, "end": v(-233, -172) * mm});
            skLineSegment(sketch, "E31.1.19.1", {"start": v(-243, -182) * mm, "end": v(-233, -182) * mm});
            skLineSegment(sketch, "E31.1.19.2", {"start": v(-243, -172) * mm, "end": v(-243, -182) * mm});
            skLineSegment(sketch, "E31.1.19.3", {"start": v(-233, -172) * mm, "end": v(-233, -182) * mm});
            skLineSegment(sketch, "E31.1.20.0", {"start": v(-243, -158) * mm, "end": v(-233, -158) * mm});
            skLineSegment(sketch, "E31.1.20.1", {"start": v(-243, -168) * mm, "end": v(-233, -168) * mm});
            skLineSegment(sketch, "E31.1.20.2", {"start": v(-243, -158) * mm, "end": v(-243, -168) * mm});
            skLineSegment(sketch, "E31.1.20.3", {"start": v(-233, -158) * mm, "end": v(-233, -168) * mm});
            skLineSegment(sketch, "E31.1.21.0", {"start": v(-243, -144) * mm, "end": v(-233, -144) * mm});
            skLineSegment(sketch, "E31.1.21.1", {"start": v(-243, -154) * mm, "end": v(-233, -154) * mm});
            skLineSegment(sketch, "E31.1.21.2", {"start": v(-243, -144) * mm, "end": v(-243, -154) * mm});
            skLineSegment(sketch, "E31.1.21.3", {"start": v(-233, -144) * mm, "end": v(-233, -154) * mm});
            skLineSegment(sketch, "E31.1.22.0", {"start": v(-243, -130) * mm, "end": v(-233, -130) * mm});
            skLineSegment(sketch, "E31.1.22.1", {"start": v(-243, -140) * mm, "end": v(-233, -140) * mm});
            skLineSegment(sketch, "E31.1.22.2", {"start": v(-243, -130) * mm, "end": v(-243, -140) * mm});
            skLineSegment(sketch, "E31.1.22.3", {"start": v(-233, -130) * mm, "end": v(-233, -140) * mm});
            skLineSegment(sketch, "E31.1.23.0", {"start": v(-243, -116) * mm, "end": v(-233, -116) * mm});
            skLineSegment(sketch, "E31.1.23.1", {"start": v(-243, -126) * mm, "end": v(-233, -126) * mm});
            skLineSegment(sketch, "E31.1.23.2", {"start": v(-243, -116) * mm, "end": v(-243, -126) * mm});
            skLineSegment(sketch, "E31.1.23.3", {"start": v(-233, -116) * mm, "end": v(-233, -126) * mm});
            skLineSegment(sketch, "E31.1.24.0", {"start": v(-243, -102) * mm, "end": v(-233, -102) * mm});
            skLineSegment(sketch, "E31.1.24.1", {"start": v(-243, -112) * mm, "end": v(-233, -112) * mm});
            skLineSegment(sketch, "E31.1.24.2", {"start": v(-243, -102) * mm, "end": v(-243, -112) * mm});
            skLineSegment(sketch, "E31.1.24.3", {"start": v(-233, -102) * mm, "end": v(-233, -112) * mm});
            skLineSegment(sketch, "E31.1.25.0", {"start": v(-243, -88) * mm, "end": v(-233, -88) * mm});
            skLineSegment(sketch, "E31.1.25.1", {"start": v(-243, -98) * mm, "end": v(-233, -98) * mm});
            skLineSegment(sketch, "E31.1.25.2", {"start": v(-243, -88) * mm, "end": v(-243, -98) * mm});
            skLineSegment(sketch, "E31.1.25.3", {"start": v(-233, -88) * mm, "end": v(-233, -98) * mm});
            skLineSegment(sketch, "E31.1.26.0", {"start": v(-243, -74) * mm, "end": v(-233, -74) * mm});
            skLineSegment(sketch, "E31.1.26.1", {"start": v(-243, -84) * mm, "end": v(-233, -84) * mm});
            skLineSegment(sketch, "E31.1.26.2", {"start": v(-243, -74) * mm, "end": v(-243, -84) * mm});
            skLineSegment(sketch, "E31.1.26.3", {"start": v(-233, -74) * mm, "end": v(-233, -84) * mm});
            skLineSegment(sketch, "E31.1.27.0", {"start": v(-243, -60) * mm, "end": v(-233, -60) * mm});
            skLineSegment(sketch, "E31.1.27.1", {"start": v(-243, -70) * mm, "end": v(-233, -70) * mm});
            skLineSegment(sketch, "E31.1.27.2", {"start": v(-243, -60) * mm, "end": v(-243, -70) * mm});
            skLineSegment(sketch, "E31.1.27.3", {"start": v(-233, -60) * mm, "end": v(-233, -70) * mm});
            skLineSegment(sketch, "E31.1.28.0", {"start": v(-243, -46) * mm, "end": v(-233, -46) * mm});
            skLineSegment(sketch, "E31.1.28.1", {"start": v(-243, -56) * mm, "end": v(-233, -56) * mm});
            skLineSegment(sketch, "E31.1.28.2", {"start": v(-243, -46) * mm, "end": v(-243, -56) * mm});
            skLineSegment(sketch, "E31.1.28.3", {"start": v(-233, -46) * mm, "end": v(-233, -56) * mm});
            skLineSegment(sketch, "E31.1.29.0", {"start": v(-243, -32) * mm, "end": v(-233, -32) * mm});
            skLineSegment(sketch, "E31.1.29.1", {"start": v(-243, -42) * mm, "end": v(-233, -42) * mm});
            skLineSegment(sketch, "E31.1.29.2", {"start": v(-243, -32) * mm, "end": v(-243, -42) * mm});
            skLineSegment(sketch, "E31.1.29.3", {"start": v(-233, -32) * mm, "end": v(-233, -42) * mm});
            skLineSegment(sketch, "E31.1.30.0", {"start": v(-243, -18) * mm, "end": v(-233, -18) * mm});
            skLineSegment(sketch, "E31.1.30.1", {"start": v(-243, -28) * mm, "end": v(-233, -28) * mm});
            skLineSegment(sketch, "E31.1.30.2", {"start": v(-243, -18) * mm, "end": v(-243, -28) * mm});
            skLineSegment(sketch, "E31.1.30.3", {"start": v(-233, -18) * mm, "end": v(-233, -28) * mm});
            skLineSegment(sketch, "E31.1.31.0", {"start": v(-243, -4) * mm, "end": v(-233, -4) * mm});
            skLineSegment(sketch, "E31.1.31.1", {"start": v(-243, -14) * mm, "end": v(-233, -14) * mm});
            skLineSegment(sketch, "E31.1.31.2", {"start": v(-243, -4) * mm, "end": v(-243, -14) * mm});
            skLineSegment(sketch, "E31.1.31.3", {"start": v(-233, -4) * mm, "end": v(-233, -14) * mm});
            skLineSegment(sketch, "E31.2.0.0", {"start": v(-229, -438) * mm, "end": v(-219, -438) * mm});
            skLineSegment(sketch, "E31.2.0.1", {"start": v(-229, -448) * mm, "end": v(-219, -448) * mm});
            skLineSegment(sketch, "E31.2.0.2", {"start": v(-229, -438) * mm, "end": v(-229, -448) * mm});
            skLineSegment(sketch, "E31.2.0.3", {"start": v(-219, -438) * mm, "end": v(-219, -448) * mm});
            skLineSegment(sketch, "E31.2.1.0", {"start": v(-229, -424) * mm, "end": v(-219, -424) * mm});
            skLineSegment(sketch, "E31.2.1.1", {"start": v(-229, -434) * mm, "end": v(-219, -434) * mm});
            skLineSegment(sketch, "E31.2.1.2", {"start": v(-229, -424) * mm, "end": v(-229, -434) * mm});
            skLineSegment(sketch, "E31.2.1.3", {"start": v(-219, -424) * mm, "end": v(-219, -434) * mm});
            skLineSegment(sketch, "E31.2.2.0", {"start": v(-229, -410) * mm, "end": v(-219, -410) * mm});
            skLineSegment(sketch, "E31.2.2.1", {"start": v(-229, -420) * mm, "end": v(-219, -420) * mm});
            skLineSegment(sketch, "E31.2.2.2", {"start": v(-229, -410) * mm, "end": v(-229, -420) * mm});
            skLineSegment(sketch, "E31.2.2.3", {"start": v(-219, -410) * mm, "end": v(-219, -420) * mm});
            skLineSegment(sketch, "E31.2.3.0", {"start": v(-229, -396) * mm, "end": v(-219, -396) * mm});
            skLineSegment(sketch, "E31.2.3.1", {"start": v(-229, -406) * mm, "end": v(-219, -406) * mm});
            skLineSegment(sketch, "E31.2.3.2", {"start": v(-229, -396) * mm, "end": v(-229, -406) * mm});
            skLineSegment(sketch, "E31.2.3.3", {"start": v(-219, -396) * mm, "end": v(-219, -406) * mm});
            skLineSegment(sketch, "E31.2.4.0", {"start": v(-229, -382) * mm, "end": v(-219, -382) * mm});
            skLineSegment(sketch, "E31.2.4.1", {"start": v(-229, -392) * mm, "end": v(-219, -392) * mm});
            skLineSegment(sketch, "E31.2.4.2", {"start": v(-229, -382) * mm, "end": v(-229, -392) * mm});
            skLineSegment(sketch, "E31.2.4.3", {"start": v(-219, -382) * mm, "end": v(-219, -392) * mm});
            skLineSegment(sketch, "E31.2.5.0", {"start": v(-229, -368) * mm, "end": v(-219, -368) * mm});
            skLineSegment(sketch, "E31.2.5.1", {"start": v(-229, -378) * mm, "end": v(-219, -378) * mm});
            skLineSegment(sketch, "E31.2.5.2", {"start": v(-229, -368) * mm, "end": v(-229, -378) * mm});
            skLineSegment(sketch, "E31.2.5.3", {"start": v(-219, -368) * mm, "end": v(-219, -378) * mm});
            skLineSegment(sketch, "E31.2.6.0", {"start": v(-229, -354) * mm, "end": v(-219, -354) * mm});
            skLineSegment(sketch, "E31.2.6.1", {"start": v(-229, -364) * mm, "end": v(-219, -364) * mm});
            skLineSegment(sketch, "E31.2.6.2", {"start": v(-229, -354) * mm, "end": v(-229, -364) * mm});
            skLineSegment(sketch, "E31.2.6.3", {"start": v(-219, -354) * mm, "end": v(-219, -364) * mm});
            skLineSegment(sketch, "E31.2.7.0", {"start": v(-229, -340) * mm, "end": v(-219, -340) * mm});
            skLineSegment(sketch, "E31.2.7.1", {"start": v(-229, -350) * mm, "end": v(-219, -350) * mm});
            skLineSegment(sketch, "E31.2.7.2", {"start": v(-229, -340) * mm, "end": v(-229, -350) * mm});
            skLineSegment(sketch, "E31.2.7.3", {"start": v(-219, -340) * mm, "end": v(-219, -350) * mm});
            skLineSegment(sketch, "E31.2.8.0", {"start": v(-229, -326) * mm, "end": v(-219, -326) * mm});
            skLineSegment(sketch, "E31.2.8.1", {"start": v(-229, -336) * mm, "end": v(-219, -336) * mm});
            skLineSegment(sketch, "E31.2.8.2", {"start": v(-229, -326) * mm, "end": v(-229, -336) * mm});
            skLineSegment(sketch, "E31.2.8.3", {"start": v(-219, -326) * mm, "end": v(-219, -336) * mm});
            skLineSegment(sketch, "E31.2.9.0", {"start": v(-229, -312) * mm, "end": v(-219, -312) * mm});
            skLineSegment(sketch, "E31.2.9.1", {"start": v(-229, -322) * mm, "end": v(-219, -322) * mm});
            skLineSegment(sketch, "E31.2.9.2", {"start": v(-229, -312) * mm, "end": v(-229, -322) * mm});
            skLineSegment(sketch, "E31.2.9.3", {"start": v(-219, -312) * mm, "end": v(-219, -322) * mm});
            skLineSegment(sketch, "E31.2.10.0", {"start": v(-229, -298) * mm, "end": v(-219, -298) * mm});
            skLineSegment(sketch, "E31.2.10.1", {"start": v(-229, -308) * mm, "end": v(-219, -308) * mm});
            skLineSegment(sketch, "E31.2.10.2", {"start": v(-229, -298) * mm, "end": v(-229, -308) * mm});
            skLineSegment(sketch, "E31.2.10.3", {"start": v(-219, -298) * mm, "end": v(-219, -308) * mm});
            skLineSegment(sketch, "E31.2.11.0", {"start": v(-229, -284) * mm, "end": v(-219, -284) * mm});
            skLineSegment(sketch, "E31.2.11.1", {"start": v(-229, -294) * mm, "end": v(-219, -294) * mm});
            skLineSegment(sketch, "E31.2.11.2", {"start": v(-229, -284) * mm, "end": v(-229, -294) * mm});
            skLineSegment(sketch, "E31.2.11.3", {"start": v(-219, -284) * mm, "end": v(-219, -294) * mm});
            skLineSegment(sketch, "E31.2.12.0", {"start": v(-229, -270) * mm, "end": v(-219, -270) * mm});
            skLineSegment(sketch, "E31.2.12.1", {"start": v(-229, -280) * mm, "end": v(-219, -280) * mm});
            skLineSegment(sketch, "E31.2.12.2", {"start": v(-229, -270) * mm, "end": v(-229, -280) * mm});
            skLineSegment(sketch, "E31.2.12.3", {"start": v(-219, -270) * mm, "end": v(-219, -280) * mm});
            skLineSegment(sketch, "E31.2.13.0", {"start": v(-229, -256) * mm, "end": v(-219, -256) * mm});
            skLineSegment(sketch, "E31.2.13.1", {"start": v(-229, -266) * mm, "end": v(-219, -266) * mm});
            skLineSegment(sketch, "E31.2.13.2", {"start": v(-229, -256) * mm, "end": v(-229, -266) * mm});
            skLineSegment(sketch, "E31.2.13.3", {"start": v(-219, -256) * mm, "end": v(-219, -266) * mm});
            skLineSegment(sketch, "E31.2.14.0", {"start": v(-229, -242) * mm, "end": v(-219, -242) * mm});
            skLineSegment(sketch, "E31.2.14.1", {"start": v(-229, -252) * mm, "end": v(-219, -252) * mm});
            skLineSegment(sketch, "E31.2.14.2", {"start": v(-229, -242) * mm, "end": v(-229, -252) * mm});
            skLineSegment(sketch, "E31.2.14.3", {"start": v(-219, -242) * mm, "end": v(-219, -252) * mm});
            skLineSegment(sketch, "E31.2.15.0", {"start": v(-229, -228) * mm, "end": v(-219, -228) * mm});
            skLineSegment(sketch, "E31.2.15.1", {"start": v(-229, -238) * mm, "end": v(-219, -238) * mm});
            skLineSegment(sketch, "E31.2.15.2", {"start": v(-229, -228) * mm, "end": v(-229, -238) * mm});
            skLineSegment(sketch, "E31.2.15.3", {"start": v(-219, -228) * mm, "end": v(-219, -238) * mm});
            skLineSegment(sketch, "E31.2.16.0", {"start": v(-229, -214) * mm, "end": v(-219, -214) * mm});
            skLineSegment(sketch, "E31.2.16.1", {"start": v(-229, -224) * mm, "end": v(-219, -224) * mm});
            skLineSegment(sketch, "E31.2.16.2", {"start": v(-229, -214) * mm, "end": v(-229, -224) * mm});
            skLineSegment(sketch, "E31.2.16.3", {"start": v(-219, -214) * mm, "end": v(-219, -224) * mm});
            skLineSegment(sketch, "E31.2.17.0", {"start": v(-229, -200) * mm, "end": v(-219, -200) * mm});
            skLineSegment(sketch, "E31.2.17.1", {"start": v(-229, -210) * mm, "end": v(-219, -210) * mm});
            skLineSegment(sketch, "E31.2.17.2", {"start": v(-229, -200) * mm, "end": v(-229, -210) * mm});
            skLineSegment(sketch, "E31.2.17.3", {"start": v(-219, -200) * mm, "end": v(-219, -210) * mm});
            skLineSegment(sketch, "E31.2.18.0", {"start": v(-229, -186) * mm, "end": v(-219, -186) * mm});
            skLineSegment(sketch, "E31.2.18.1", {"start": v(-229, -196) * mm, "end": v(-219, -196) * mm});
            skLineSegment(sketch, "E31.2.18.2", {"start": v(-229, -186) * mm, "end": v(-229, -196) * mm});
            skLineSegment(sketch, "E31.2.18.3", {"start": v(-219, -186) * mm, "end": v(-219, -196) * mm});
            skLineSegment(sketch, "E31.2.19.0", {"start": v(-229, -172) * mm, "end": v(-219, -172) * mm});
            skLineSegment(sketch, "E31.2.19.1", {"start": v(-229, -182) * mm, "end": v(-219, -182) * mm});
            skLineSegment(sketch, "E31.2.19.2", {"start": v(-229, -172) * mm, "end": v(-229, -182) * mm});
            skLineSegment(sketch, "E31.2.19.3", {"start": v(-219, -172) * mm, "end": v(-219, -182) * mm});
            skLineSegment(sketch, "E31.2.20.0", {"start": v(-229, -158) * mm, "end": v(-219, -158) * mm});
            skLineSegment(sketch, "E31.2.20.1", {"start": v(-229, -168) * mm, "end": v(-219, -168) * mm});
            skLineSegment(sketch, "E31.2.20.2", {"start": v(-229, -158) * mm, "end": v(-229, -168) * mm});
            skLineSegment(sketch, "E31.2.20.3", {"start": v(-219, -158) * mm, "end": v(-219, -168) * mm});
            skLineSegment(sketch, "E31.2.21.0", {"start": v(-229, -144) * mm, "end": v(-219, -144) * mm});
            skLineSegment(sketch, "E31.2.21.1", {"start": v(-229, -154) * mm, "end": v(-219, -154) * mm});
            skLineSegment(sketch, "E31.2.21.2", {"start": v(-229, -144) * mm, "end": v(-229, -154) * mm});
            skLineSegment(sketch, "E31.2.21.3", {"start": v(-219, -144) * mm, "end": v(-219, -154) * mm});
            skLineSegment(sketch, "E31.2.22.0", {"start": v(-229, -130) * mm, "end": v(-219, -130) * mm});
            skLineSegment(sketch, "E31.2.22.1", {"start": v(-229, -140) * mm, "end": v(-219, -140) * mm});
            skLineSegment(sketch, "E31.2.22.2", {"start": v(-229, -130) * mm, "end": v(-229, -140) * mm});
            skLineSegment(sketch, "E31.2.22.3", {"start": v(-219, -130) * mm, "end": v(-219, -140) * mm});
            skLineSegment(sketch, "E31.2.23.0", {"start": v(-229, -116) * mm, "end": v(-219, -116) * mm});
            skLineSegment(sketch, "E31.2.23.1", {"start": v(-229, -126) * mm, "end": v(-219, -126) * mm});
            skLineSegment(sketch, "E31.2.23.2", {"start": v(-229, -116) * mm, "end": v(-229, -126) * mm});
            skLineSegment(sketch, "E31.2.23.3", {"start": v(-219, -116) * mm, "end": v(-219, -126) * mm});
            skLineSegment(sketch, "E31.2.24.0", {"start": v(-229, -102) * mm, "end": v(-219, -102) * mm});
            skLineSegment(sketch, "E31.2.24.1", {"start": v(-229, -112) * mm, "end": v(-219, -112) * mm});
            skLineSegment(sketch, "E31.2.24.2", {"start": v(-229, -102) * mm, "end": v(-229, -112) * mm});
            skLineSegment(sketch, "E31.2.24.3", {"start": v(-219, -102) * mm, "end": v(-219, -112) * mm});
            skLineSegment(sketch, "E31.2.25.0", {"start": v(-229, -88) * mm, "end": v(-219, -88) * mm});
            skLineSegment(sketch, "E31.2.25.1", {"start": v(-229, -98) * mm, "end": v(-219, -98) * mm});
            skLineSegment(sketch, "E31.2.25.2", {"start": v(-229, -88) * mm, "end": v(-229, -98) * mm});
            skLineSegment(sketch, "E31.2.25.3", {"start": v(-219, -88) * mm, "end": v(-219, -98) * mm});
            skLineSegment(sketch, "E31.2.26.0", {"start": v(-229, -74) * mm, "end": v(-219, -74) * mm});
            skLineSegment(sketch, "E31.2.26.1", {"start": v(-229, -84) * mm, "end": v(-219, -84) * mm});
            skLineSegment(sketch, "E31.2.26.2", {"start": v(-229, -74) * mm, "end": v(-229, -84) * mm});
            skLineSegment(sketch, "E31.2.26.3", {"start": v(-219, -74) * mm, "end": v(-219, -84) * mm});
            skLineSegment(sketch, "E31.2.27.0", {"start": v(-229, -60) * mm, "end": v(-219, -60) * mm});
            skLineSegment(sketch, "E31.2.27.1", {"start": v(-229, -70) * mm, "end": v(-219, -70) * mm});
            skLineSegment(sketch, "E31.2.27.2", {"start": v(-229, -60) * mm, "end": v(-229, -70) * mm});
            skLineSegment(sketch, "E31.2.27.3", {"start": v(-219, -60) * mm, "end": v(-219, -70) * mm});
            skLineSegment(sketch, "E31.2.28.0", {"start": v(-229, -46) * mm, "end": v(-219, -46) * mm});
            skLineSegment(sketch, "E31.2.28.1", {"start": v(-229, -56) * mm, "end": v(-219, -56) * mm});
            skLineSegment(sketch, "E31.2.28.2", {"start": v(-229, -46) * mm, "end": v(-229, -56) * mm});
            skLineSegment(sketch, "E31.2.28.3", {"start": v(-219, -46) * mm, "end": v(-219, -56) * mm});
            skLineSegment(sketch, "E31.2.29.0", {"start": v(-229, -32) * mm, "end": v(-219, -32) * mm});
            skLineSegment(sketch, "E31.2.29.1", {"start": v(-229, -42) * mm, "end": v(-219, -42) * mm});
            skLineSegment(sketch, "E31.2.29.2", {"start": v(-229, -32) * mm, "end": v(-229, -42) * mm});
            skLineSegment(sketch, "E31.2.29.3", {"start": v(-219, -32) * mm, "end": v(-219, -42) * mm});
            skLineSegment(sketch, "E31.2.30.0", {"start": v(-229, -18) * mm, "end": v(-219, -18) * mm});
            skLineSegment(sketch, "E31.2.30.1", {"start": v(-229, -28) * mm, "end": v(-219, -28) * mm});
            skLineSegment(sketch, "E31.2.30.2", {"start": v(-229, -18) * mm, "end": v(-229, -28) * mm});
            skLineSegment(sketch, "E31.2.30.3", {"start": v(-219, -18) * mm, "end": v(-219, -28) * mm});
            skLineSegment(sketch, "E31.2.31.0", {"start": v(-229, -4) * mm, "end": v(-219, -4) * mm});
            skLineSegment(sketch, "E31.2.31.1", {"start": v(-229, -14) * mm, "end": v(-219, -14) * mm});
            skLineSegment(sketch, "E31.2.31.2", {"start": v(-229, -4) * mm, "end": v(-229, -14) * mm});
            skLineSegment(sketch, "E31.2.31.3", {"start": v(-219, -4) * mm, "end": v(-219, -14) * mm});
            skLineSegment(sketch, "E31.3.0.0", {"start": v(-215, -438) * mm, "end": v(-205, -438) * mm});
            skLineSegment(sketch, "E31.3.0.1", {"start": v(-215, -448) * mm, "end": v(-205, -448) * mm});
            skLineSegment(sketch, "E31.3.0.2", {"start": v(-215, -438) * mm, "end": v(-215, -448) * mm});
            skLineSegment(sketch, "E31.3.0.3", {"start": v(-205, -438) * mm, "end": v(-205, -448) * mm});
            skLineSegment(sketch, "E31.3.1.0", {"start": v(-215, -424) * mm, "end": v(-205, -424) * mm});
            skLineSegment(sketch, "E31.3.1.1", {"start": v(-215, -434) * mm, "end": v(-205, -434) * mm});
            skLineSegment(sketch, "E31.3.1.2", {"start": v(-215, -424) * mm, "end": v(-215, -434) * mm});
            skLineSegment(sketch, "E31.3.1.3", {"start": v(-205, -424) * mm, "end": v(-205, -434) * mm});
            skLineSegment(sketch, "E31.3.2.0", {"start": v(-215, -410) * mm, "end": v(-205, -410) * mm});
            skLineSegment(sketch, "E31.3.2.1", {"start": v(-215, -420) * mm, "end": v(-205, -420) * mm});
            skLineSegment(sketch, "E31.3.2.2", {"start": v(-215, -410) * mm, "end": v(-215, -420) * mm});
            skLineSegment(sketch, "E31.3.2.3", {"start": v(-205, -410) * mm, "end": v(-205, -420) * mm});
            skLineSegment(sketch, "E31.3.3.0", {"start": v(-215, -396) * mm, "end": v(-205, -396) * mm});
            skLineSegment(sketch, "E31.3.3.1", {"start": v(-215, -406) * mm, "end": v(-205, -406) * mm});
            skLineSegment(sketch, "E31.3.3.2", {"start": v(-215, -396) * mm, "end": v(-215, -406) * mm});
            skLineSegment(sketch, "E31.3.3.3", {"start": v(-205, -396) * mm, "end": v(-205, -406) * mm});
            skLineSegment(sketch, "E31.3.4.0", {"start": v(-215, -382) * mm, "end": v(-205, -382) * mm});
            skLineSegment(sketch, "E31.3.4.1", {"start": v(-215, -392) * mm, "end": v(-205, -392) * mm});
            skLineSegment(sketch, "E31.3.4.2", {"start": v(-215, -382) * mm, "end": v(-215, -392) * mm});
            skLineSegment(sketch, "E31.3.4.3", {"start": v(-205, -382) * mm, "end": v(-205, -392) * mm});
            skLineSegment(sketch, "E31.3.5.0", {"start": v(-215, -368) * mm, "end": v(-205, -368) * mm});
            skLineSegment(sketch, "E31.3.5.1", {"start": v(-215, -378) * mm, "end": v(-205, -378) * mm});
            skLineSegment(sketch, "E31.3.5.2", {"start": v(-215, -368) * mm, "end": v(-215, -378) * mm});
            skLineSegment(sketch, "E31.3.5.3", {"start": v(-205, -368) * mm, "end": v(-205, -378) * mm});
            skLineSegment(sketch, "E31.3.6.0", {"start": v(-215, -354) * mm, "end": v(-205, -354) * mm});
            skLineSegment(sketch, "E31.3.6.1", {"start": v(-215, -364) * mm, "end": v(-205, -364) * mm});
            skLineSegment(sketch, "E31.3.6.2", {"start": v(-215, -354) * mm, "end": v(-215, -364) * mm});
            skLineSegment(sketch, "E31.3.6.3", {"start": v(-205, -354) * mm, "end": v(-205, -364) * mm});
            skLineSegment(sketch, "E31.3.7.0", {"start": v(-215, -340) * mm, "end": v(-205, -340) * mm});
            skLineSegment(sketch, "E31.3.7.1", {"start": v(-215, -350) * mm, "end": v(-205, -350) * mm});
            skLineSegment(sketch, "E31.3.7.2", {"start": v(-215, -340) * mm, "end": v(-215, -350) * mm});
            skLineSegment(sketch, "E31.3.7.3", {"start": v(-205, -340) * mm, "end": v(-205, -350) * mm});
            skLineSegment(sketch, "E31.3.8.0", {"start": v(-215, -326) * mm, "end": v(-205, -326) * mm});
            skLineSegment(sketch, "E31.3.8.1", {"start": v(-215, -336) * mm, "end": v(-205, -336) * mm});
            skLineSegment(sketch, "E31.3.8.2", {"start": v(-215, -326) * mm, "end": v(-215, -336) * mm});
            skLineSegment(sketch, "E31.3.8.3", {"start": v(-205, -326) * mm, "end": v(-205, -336) * mm});
            skLineSegment(sketch, "E31.3.9.0", {"start": v(-215, -312) * mm, "end": v(-205, -312) * mm});
            skLineSegment(sketch, "E31.3.9.1", {"start": v(-215, -322) * mm, "end": v(-205, -322) * mm});
            skLineSegment(sketch, "E31.3.9.2", {"start": v(-215, -312) * mm, "end": v(-215, -322) * mm});
            skLineSegment(sketch, "E31.3.9.3", {"start": v(-205, -312) * mm, "end": v(-205, -322) * mm});
            skLineSegment(sketch, "E31.3.10.0", {"start": v(-215, -298) * mm, "end": v(-205, -298) * mm});
            skLineSegment(sketch, "E31.3.10.1", {"start": v(-215, -308) * mm, "end": v(-205, -308) * mm});
            skLineSegment(sketch, "E31.3.10.2", {"start": v(-215, -298) * mm, "end": v(-215, -308) * mm});
            skLineSegment(sketch, "E31.3.10.3", {"start": v(-205, -298) * mm, "end": v(-205, -308) * mm});
            skLineSegment(sketch, "E31.3.11.0", {"start": v(-215, -284) * mm, "end": v(-205, -284) * mm});
            skLineSegment(sketch, "E31.3.11.1", {"start": v(-215, -294) * mm, "end": v(-205, -294) * mm});
            skLineSegment(sketch, "E31.3.11.2", {"start": v(-215, -284) * mm, "end": v(-215, -294) * mm});
            skLineSegment(sketch, "E31.3.11.3", {"start": v(-205, -284) * mm, "end": v(-205, -294) * mm});
            skLineSegment(sketch, "E31.3.12.0", {"start": v(-215, -270) * mm, "end": v(-205, -270) * mm});
            skLineSegment(sketch, "E31.3.12.1", {"start": v(-215, -280) * mm, "end": v(-205, -280) * mm});
            skLineSegment(sketch, "E31.3.12.2", {"start": v(-215, -270) * mm, "end": v(-215, -280) * mm});
            skLineSegment(sketch, "E31.3.12.3", {"start": v(-205, -270) * mm, "end": v(-205, -280) * mm});
            skLineSegment(sketch, "E31.3.13.0", {"start": v(-215, -256) * mm, "end": v(-205, -256) * mm});
            skLineSegment(sketch, "E31.3.13.1", {"start": v(-215, -266) * mm, "end": v(-205, -266) * mm});
            skLineSegment(sketch, "E31.3.13.2", {"start": v(-215, -256) * mm, "end": v(-215, -266) * mm});
            skLineSegment(sketch, "E31.3.13.3", {"start": v(-205, -256) * mm, "end": v(-205, -266) * mm});
            skLineSegment(sketch, "E31.3.14.0", {"start": v(-215, -242) * mm, "end": v(-205, -242) * mm});
            skLineSegment(sketch, "E31.3.14.1", {"start": v(-215, -252) * mm, "end": v(-205, -252) * mm});
            skLineSegment(sketch, "E31.3.14.2", {"start": v(-215, -242) * mm, "end": v(-215, -252) * mm});
            skLineSegment(sketch, "E31.3.14.3", {"start": v(-205, -242) * mm, "end": v(-205, -252) * mm});
            skLineSegment(sketch, "E31.3.15.0", {"start": v(-215, -228) * mm, "end": v(-205, -228) * mm});
            skLineSegment(sketch, "E31.3.15.1", {"start": v(-215, -238) * mm, "end": v(-205, -238) * mm});
            skLineSegment(sketch, "E31.3.15.2", {"start": v(-215, -228) * mm, "end": v(-215, -238) * mm});
            skLineSegment(sketch, "E31.3.15.3", {"start": v(-205, -228) * mm, "end": v(-205, -238) * mm});
            skLineSegment(sketch, "E31.3.16.0", {"start": v(-215, -214) * mm, "end": v(-205, -214) * mm});
            skLineSegment(sketch, "E31.3.16.1", {"start": v(-215, -224) * mm, "end": v(-205, -224) * mm});
            skLineSegment(sketch, "E31.3.16.2", {"start": v(-215, -214) * mm, "end": v(-215, -224) * mm});
            skLineSegment(sketch, "E31.3.16.3", {"start": v(-205, -214) * mm, "end": v(-205, -224) * mm});
            skLineSegment(sketch, "E31.3.17.0", {"start": v(-215, -200) * mm, "end": v(-205, -200) * mm});
            skLineSegment(sketch, "E31.3.17.1", {"start": v(-215, -210) * mm, "end": v(-205, -210) * mm});
            skLineSegment(sketch, "E31.3.17.2", {"start": v(-215, -200) * mm, "end": v(-215, -210) * mm});
            skLineSegment(sketch, "E31.3.17.3", {"start": v(-205, -200) * mm, "end": v(-205, -210) * mm});
            skLineSegment(sketch, "E31.3.18.0", {"start": v(-215, -186) * mm, "end": v(-205, -186) * mm});
            skLineSegment(sketch, "E31.3.18.1", {"start": v(-215, -196) * mm, "end": v(-205, -196) * mm});
            skLineSegment(sketch, "E31.3.18.2", {"start": v(-215, -186) * mm, "end": v(-215, -196) * mm});
            skLineSegment(sketch, "E31.3.18.3", {"start": v(-205, -186) * mm, "end": v(-205, -196) * mm});
            skLineSegment(sketch, "E31.3.19.0", {"start": v(-215, -172) * mm, "end": v(-205, -172) * mm});
            skLineSegment(sketch, "E31.3.19.1", {"start": v(-215, -182) * mm, "end": v(-205, -182) * mm});
            skLineSegment(sketch, "E31.3.19.2", {"start": v(-215, -172) * mm, "end": v(-215, -182) * mm});
            skLineSegment(sketch, "E31.3.19.3", {"start": v(-205, -172) * mm, "end": v(-205, -182) * mm});
            skLineSegment(sketch, "E31.3.20.0", {"start": v(-215, -158) * mm, "end": v(-205, -158) * mm});
            skLineSegment(sketch, "E31.3.20.1", {"start": v(-215, -168) * mm, "end": v(-205, -168) * mm});
            skLineSegment(sketch, "E31.3.20.2", {"start": v(-215, -158) * mm, "end": v(-215, -168) * mm});
            skLineSegment(sketch, "E31.3.20.3", {"start": v(-205, -158) * mm, "end": v(-205, -168) * mm});
            skLineSegment(sketch, "E31.3.21.0", {"start": v(-215, -144) * mm, "end": v(-205, -144) * mm});
            skLineSegment(sketch, "E31.3.21.1", {"start": v(-215, -154) * mm, "end": v(-205, -154) * mm});
            skLineSegment(sketch, "E31.3.21.2", {"start": v(-215, -144) * mm, "end": v(-215, -154) * mm});
            skLineSegment(sketch, "E31.3.21.3", {"start": v(-205, -144) * mm, "end": v(-205, -154) * mm});
            skLineSegment(sketch, "E31.3.22.0", {"start": v(-215, -130) * mm, "end": v(-205, -130) * mm});
            skLineSegment(sketch, "E31.3.22.1", {"start": v(-215, -140) * mm, "end": v(-205, -140) * mm});
            skLineSegment(sketch, "E31.3.22.2", {"start": v(-215, -130) * mm, "end": v(-215, -140) * mm});
            skLineSegment(sketch, "E31.3.22.3", {"start": v(-205, -130) * mm, "end": v(-205, -140) * mm});
            skLineSegment(sketch, "E31.3.23.0", {"start": v(-215, -116) * mm, "end": v(-205, -116) * mm});
            skLineSegment(sketch, "E31.3.23.1", {"start": v(-215, -126) * mm, "end": v(-205, -126) * mm});
            skLineSegment(sketch, "E31.3.23.2", {"start": v(-215, -116) * mm, "end": v(-215, -126) * mm});
            skLineSegment(sketch, "E31.3.23.3", {"start": v(-205, -116) * mm, "end": v(-205, -126) * mm});
            skLineSegment(sketch, "E31.3.24.0", {"start": v(-215, -102) * mm, "end": v(-205, -102) * mm});
            skLineSegment(sketch, "E31.3.24.1", {"start": v(-215, -112) * mm, "end": v(-205, -112) * mm});
            skLineSegment(sketch, "E31.3.24.2", {"start": v(-215, -102) * mm, "end": v(-215, -112) * mm});
            skLineSegment(sketch, "E31.3.24.3", {"start": v(-205, -102) * mm, "end": v(-205, -112) * mm});
            skLineSegment(sketch, "E31.3.25.0", {"start": v(-215, -88) * mm, "end": v(-205, -88) * mm});
            skLineSegment(sketch, "E31.3.25.1", {"start": v(-215, -98) * mm, "end": v(-205, -98) * mm});
            skLineSegment(sketch, "E31.3.25.2", {"start": v(-215, -88) * mm, "end": v(-215, -98) * mm});
            skLineSegment(sketch, "E31.3.25.3", {"start": v(-205, -88) * mm, "end": v(-205, -98) * mm});
            skLineSegment(sketch, "E31.3.26.0", {"start": v(-215, -74) * mm, "end": v(-205, -74) * mm});
            skLineSegment(sketch, "E31.3.26.1", {"start": v(-215, -84) * mm, "end": v(-205, -84) * mm});
            skLineSegment(sketch, "E31.3.26.2", {"start": v(-215, -74) * mm, "end": v(-215, -84) * mm});
            skLineSegment(sketch, "E31.3.26.3", {"start": v(-205, -74) * mm, "end": v(-205, -84) * mm});
            skLineSegment(sketch, "E31.3.27.0", {"start": v(-215, -60) * mm, "end": v(-205, -60) * mm});
            skLineSegment(sketch, "E31.3.27.1", {"start": v(-215, -70) * mm, "end": v(-205, -70) * mm});
            skLineSegment(sketch, "E31.3.27.2", {"start": v(-215, -60) * mm, "end": v(-215, -70) * mm});
            skLineSegment(sketch, "E31.3.27.3", {"start": v(-205, -60) * mm, "end": v(-205, -70) * mm});
            skLineSegment(sketch, "E31.3.28.0", {"start": v(-215, -46) * mm, "end": v(-205, -46) * mm});
            skLineSegment(sketch, "E31.3.28.1", {"start": v(-215, -56) * mm, "end": v(-205, -56) * mm});
            skLineSegment(sketch, "E31.3.28.2", {"start": v(-215, -46) * mm, "end": v(-215, -56) * mm});
            skLineSegment(sketch, "E31.3.28.3", {"start": v(-205, -46) * mm, "end": v(-205, -56) * mm});
            skLineSegment(sketch, "E31.3.29.0", {"start": v(-215, -32) * mm, "end": v(-205, -32) * mm});
            skLineSegment(sketch, "E31.3.29.1", {"start": v(-215, -42) * mm, "end": v(-205, -42) * mm});
            skLineSegment(sketch, "E31.3.29.2", {"start": v(-215, -32) * mm, "end": v(-215, -42) * mm});
            skLineSegment(sketch, "E31.3.29.3", {"start": v(-205, -32) * mm, "end": v(-205, -42) * mm});
            skLineSegment(sketch, "E31.3.30.0", {"start": v(-215, -18) * mm, "end": v(-205, -18) * mm});
            skLineSegment(sketch, "E31.3.30.1", {"start": v(-215, -28) * mm, "end": v(-205, -28) * mm});
            skLineSegment(sketch, "E31.3.30.2", {"start": v(-215, -18) * mm, "end": v(-215, -28) * mm});
            skLineSegment(sketch, "E31.3.30.3", {"start": v(-205, -18) * mm, "end": v(-205, -28) * mm});
            skLineSegment(sketch, "E31.3.31.0", {"start": v(-215, -4) * mm, "end": v(-205, -4) * mm});
            skLineSegment(sketch, "E31.3.31.1", {"start": v(-215, -14) * mm, "end": v(-205, -14) * mm});
            skLineSegment(sketch, "E31.3.31.2", {"start": v(-215, -4) * mm, "end": v(-215, -14) * mm});
            skLineSegment(sketch, "E31.3.31.3", {"start": v(-205, -4) * mm, "end": v(-205, -14) * mm});
            skLineSegment(sketch, "E31.4.0.0", {"start": v(-201, -438) * mm, "end": v(-191, -438) * mm});
            skLineSegment(sketch, "E31.4.0.1", {"start": v(-201, -448) * mm, "end": v(-191, -448) * mm});
            skLineSegment(sketch, "E31.4.0.2", {"start": v(-201, -438) * mm, "end": v(-201, -448) * mm});
            skLineSegment(sketch, "E31.4.0.3", {"start": v(-191, -438) * mm, "end": v(-191, -448) * mm});
            skLineSegment(sketch, "E31.4.1.0", {"start": v(-201, -424) * mm, "end": v(-191, -424) * mm});
            skLineSegment(sketch, "E31.4.1.1", {"start": v(-201, -434) * mm, "end": v(-191, -434) * mm});
            skLineSegment(sketch, "E31.4.1.2", {"start": v(-201, -424) * mm, "end": v(-201, -434) * mm});
            skLineSegment(sketch, "E31.4.1.3", {"start": v(-191, -424) * mm, "end": v(-191, -434) * mm});
            skLineSegment(sketch, "E31.4.2.0", {"start": v(-201, -410) * mm, "end": v(-191, -410) * mm});
            skLineSegment(sketch, "E31.4.2.1", {"start": v(-201, -420) * mm, "end": v(-191, -420) * mm});
            skLineSegment(sketch, "E31.4.2.2", {"start": v(-201, -410) * mm, "end": v(-201, -420) * mm});
            skLineSegment(sketch, "E31.4.2.3", {"start": v(-191, -410) * mm, "end": v(-191, -420) * mm});
            skLineSegment(sketch, "E31.4.3.0", {"start": v(-201, -396) * mm, "end": v(-191, -396) * mm});
            skLineSegment(sketch, "E31.4.3.1", {"start": v(-201, -406) * mm, "end": v(-191, -406) * mm});
            skLineSegment(sketch, "E31.4.3.2", {"start": v(-201, -396) * mm, "end": v(-201, -406) * mm});
            skLineSegment(sketch, "E31.4.3.3", {"start": v(-191, -396) * mm, "end": v(-191, -406) * mm});
            skLineSegment(sketch, "E31.4.4.0", {"start": v(-201, -382) * mm, "end": v(-191, -382) * mm});
            skLineSegment(sketch, "E31.4.4.1", {"start": v(-201, -392) * mm, "end": v(-191, -392) * mm});
            skLineSegment(sketch, "E31.4.4.2", {"start": v(-201, -382) * mm, "end": v(-201, -392) * mm});
            skLineSegment(sketch, "E31.4.4.3", {"start": v(-191, -382) * mm, "end": v(-191, -392) * mm});
            skLineSegment(sketch, "E31.4.5.0", {"start": v(-201, -368) * mm, "end": v(-191, -368) * mm});
            skLineSegment(sketch, "E31.4.5.1", {"start": v(-201, -378) * mm, "end": v(-191, -378) * mm});
            skLineSegment(sketch, "E31.4.5.2", {"start": v(-201, -368) * mm, "end": v(-201, -378) * mm});
            skLineSegment(sketch, "E31.4.5.3", {"start": v(-191, -368) * mm, "end": v(-191, -378) * mm});
            skLineSegment(sketch, "E31.4.6.0", {"start": v(-201, -354) * mm, "end": v(-191, -354) * mm});
            skLineSegment(sketch, "E31.4.6.1", {"start": v(-201, -364) * mm, "end": v(-191, -364) * mm});
            skLineSegment(sketch, "E31.4.6.2", {"start": v(-201, -354) * mm, "end": v(-201, -364) * mm});
            skLineSegment(sketch, "E31.4.6.3", {"start": v(-191, -354) * mm, "end": v(-191, -364) * mm});
            skLineSegment(sketch, "E31.4.7.0", {"start": v(-201, -340) * mm, "end": v(-191, -340) * mm});
            skLineSegment(sketch, "E31.4.7.1", {"start": v(-201, -350) * mm, "end": v(-191, -350) * mm});
            skLineSegment(sketch, "E31.4.7.2", {"start": v(-201, -340) * mm, "end": v(-201, -350) * mm});
            skLineSegment(sketch, "E31.4.7.3", {"start": v(-191, -340) * mm, "end": v(-191, -350) * mm});
            skLineSegment(sketch, "E31.4.8.0", {"start": v(-201, -326) * mm, "end": v(-191, -326) * mm});
            skLineSegment(sketch, "E31.4.8.1", {"start": v(-201, -336) * mm, "end": v(-191, -336) * mm});
            skLineSegment(sketch, "E31.4.8.2", {"start": v(-201, -326) * mm, "end": v(-201, -336) * mm});
            skLineSegment(sketch, "E31.4.8.3", {"start": v(-191, -326) * mm, "end": v(-191, -336) * mm});
            skLineSegment(sketch, "E31.4.9.0", {"start": v(-201, -312) * mm, "end": v(-191, -312) * mm});
            skLineSegment(sketch, "E31.4.9.1", {"start": v(-201, -322) * mm, "end": v(-191, -322) * mm});
            skLineSegment(sketch, "E31.4.9.2", {"start": v(-201, -312) * mm, "end": v(-201, -322) * mm});
            skLineSegment(sketch, "E31.4.9.3", {"start": v(-191, -312) * mm, "end": v(-191, -322) * mm});
            skLineSegment(sketch, "E31.4.10.0", {"start": v(-201, -298) * mm, "end": v(-191, -298) * mm});
            skLineSegment(sketch, "E31.4.10.1", {"start": v(-201, -308) * mm, "end": v(-191, -308) * mm});
            skLineSegment(sketch, "E31.4.10.2", {"start": v(-201, -298) * mm, "end": v(-201, -308) * mm});
            skLineSegment(sketch, "E31.4.10.3", {"start": v(-191, -298) * mm, "end": v(-191, -308) * mm});
            skLineSegment(sketch, "E31.4.11.0", {"start": v(-201, -284) * mm, "end": v(-191, -284) * mm});
            skLineSegment(sketch, "E31.4.11.1", {"start": v(-201, -294) * mm, "end": v(-191, -294) * mm});
            skLineSegment(sketch, "E31.4.11.2", {"start": v(-201, -284) * mm, "end": v(-201, -294) * mm});
            skLineSegment(sketch, "E31.4.11.3", {"start": v(-191, -284) * mm, "end": v(-191, -294) * mm});
            skLineSegment(sketch, "E31.4.12.0", {"start": v(-201, -270) * mm, "end": v(-191, -270) * mm});
            skLineSegment(sketch, "E31.4.12.1", {"start": v(-201, -280) * mm, "end": v(-191, -280) * mm});
            skLineSegment(sketch, "E31.4.12.2", {"start": v(-201, -270) * mm, "end": v(-201, -280) * mm});
            skLineSegment(sketch, "E31.4.12.3", {"start": v(-191, -270) * mm, "end": v(-191, -280) * mm});
            skLineSegment(sketch, "E31.4.13.0", {"start": v(-201, -256) * mm, "end": v(-191, -256) * mm});
            skLineSegment(sketch, "E31.4.13.1", {"start": v(-201, -266) * mm, "end": v(-191, -266) * mm});
            skLineSegment(sketch, "E31.4.13.2", {"start": v(-201, -256) * mm, "end": v(-201, -266) * mm});
            skLineSegment(sketch, "E31.4.13.3", {"start": v(-191, -256) * mm, "end": v(-191, -266) * mm});
            skLineSegment(sketch, "E31.4.14.0", {"start": v(-201, -242) * mm, "end": v(-191, -242) * mm});
            skLineSegment(sketch, "E31.4.14.1", {"start": v(-201, -252) * mm, "end": v(-191, -252) * mm});
            skLineSegment(sketch, "E31.4.14.2", {"start": v(-201, -242) * mm, "end": v(-201, -252) * mm});
            skLineSegment(sketch, "E31.4.14.3", {"start": v(-191, -242) * mm, "end": v(-191, -252) * mm});
            skLineSegment(sketch, "E31.4.15.0", {"start": v(-201, -228) * mm, "end": v(-191, -228) * mm});
            skLineSegment(sketch, "E31.4.15.1", {"start": v(-201, -238) * mm, "end": v(-191, -238) * mm});
            skLineSegment(sketch, "E31.4.15.2", {"start": v(-201, -228) * mm, "end": v(-201, -238) * mm});
            skLineSegment(sketch, "E31.4.15.3", {"start": v(-191, -228) * mm, "end": v(-191, -238) * mm});
            skLineSegment(sketch, "E31.4.16.0", {"start": v(-201, -214) * mm, "end": v(-191, -214) * mm});
            skLineSegment(sketch, "E31.4.16.1", {"start": v(-201, -224) * mm, "end": v(-191, -224) * mm});
            skLineSegment(sketch, "E31.4.16.2", {"start": v(-201, -214) * mm, "end": v(-201, -224) * mm});
            skLineSegment(sketch, "E31.4.16.3", {"start": v(-191, -214) * mm, "end": v(-191, -224) * mm});
            skLineSegment(sketch, "E31.4.17.0", {"start": v(-201, -200) * mm, "end": v(-191, -200) * mm});
            skLineSegment(sketch, "E31.4.17.1", {"start": v(-201, -210) * mm, "end": v(-191, -210) * mm});
            skLineSegment(sketch, "E31.4.17.2", {"start": v(-201, -200) * mm, "end": v(-201, -210) * mm});
            skLineSegment(sketch, "E31.4.17.3", {"start": v(-191, -200) * mm, "end": v(-191, -210) * mm});
            skLineSegment(sketch, "E31.4.18.0", {"start": v(-201, -186) * mm, "end": v(-191, -186) * mm});
            skLineSegment(sketch, "E31.4.18.1", {"start": v(-201, -196) * mm, "end": v(-191, -196) * mm});
            skLineSegment(sketch, "E31.4.18.2", {"start": v(-201, -186) * mm, "end": v(-201, -196) * mm});
            skLineSegment(sketch, "E31.4.18.3", {"start": v(-191, -186) * mm, "end": v(-191, -196) * mm});
            skLineSegment(sketch, "E31.4.19.0", {"start": v(-201, -172) * mm, "end": v(-191, -172) * mm});
            skLineSegment(sketch, "E31.4.19.1", {"start": v(-201, -182) * mm, "end": v(-191, -182) * mm});
            skLineSegment(sketch, "E31.4.19.2", {"start": v(-201, -172) * mm, "end": v(-201, -182) * mm});
            skLineSegment(sketch, "E31.4.19.3", {"start": v(-191, -172) * mm, "end": v(-191, -182) * mm});
            skLineSegment(sketch, "E31.4.20.0", {"start": v(-201, -158) * mm, "end": v(-191, -158) * mm});
            skLineSegment(sketch, "E31.4.20.1", {"start": v(-201, -168) * mm, "end": v(-191, -168) * mm});
            skLineSegment(sketch, "E31.4.20.2", {"start": v(-201, -158) * mm, "end": v(-201, -168) * mm});
            skLineSegment(sketch, "E31.4.20.3", {"start": v(-191, -158) * mm, "end": v(-191, -168) * mm});
            skLineSegment(sketch, "E31.4.21.0", {"start": v(-201, -144) * mm, "end": v(-191, -144) * mm});
            skLineSegment(sketch, "E31.4.21.1", {"start": v(-201, -154) * mm, "end": v(-191, -154) * mm});
            skLineSegment(sketch, "E31.4.21.2", {"start": v(-201, -144) * mm, "end": v(-201, -154) * mm});
            skLineSegment(sketch, "E31.4.21.3", {"start": v(-191, -144) * mm, "end": v(-191, -154) * mm});
            skLineSegment(sketch, "E31.4.22.0", {"start": v(-201, -130) * mm, "end": v(-191, -130) * mm});
            skLineSegment(sketch, "E31.4.22.1", {"start": v(-201, -140) * mm, "end": v(-191, -140) * mm});
            skLineSegment(sketch, "E31.4.22.2", {"start": v(-201, -130) * mm, "end": v(-201, -140) * mm});
            skLineSegment(sketch, "E31.4.22.3", {"start": v(-191, -130) * mm, "end": v(-191, -140) * mm});
            skLineSegment(sketch, "E31.4.23.0", {"start": v(-201, -116) * mm, "end": v(-191, -116) * mm});
            skLineSegment(sketch, "E31.4.23.1", {"start": v(-201, -126) * mm, "end": v(-191, -126) * mm});
            skLineSegment(sketch, "E31.4.23.2", {"start": v(-201, -116) * mm, "end": v(-201, -126) * mm});
            skLineSegment(sketch, "E31.4.23.3", {"start": v(-191, -116) * mm, "end": v(-191, -126) * mm});
            skLineSegment(sketch, "E31.4.24.0", {"start": v(-201, -102) * mm, "end": v(-191, -102) * mm});
            skLineSegment(sketch, "E31.4.24.1", {"start": v(-201, -112) * mm, "end": v(-191, -112) * mm});
            skLineSegment(sketch, "E31.4.24.2", {"start": v(-201, -102) * mm, "end": v(-201, -112) * mm});
            skLineSegment(sketch, "E31.4.24.3", {"start": v(-191, -102) * mm, "end": v(-191, -112) * mm});
            skLineSegment(sketch, "E31.4.25.0", {"start": v(-201, -88) * mm, "end": v(-191, -88) * mm});
            skLineSegment(sketch, "E31.4.25.1", {"start": v(-201, -98) * mm, "end": v(-191, -98) * mm});
            skLineSegment(sketch, "E31.4.25.2", {"start": v(-201, -88) * mm, "end": v(-201, -98) * mm});
            skLineSegment(sketch, "E31.4.25.3", {"start": v(-191, -88) * mm, "end": v(-191, -98) * mm});
            skLineSegment(sketch, "E31.4.26.0", {"start": v(-201, -74) * mm, "end": v(-191, -74) * mm});
            skLineSegment(sketch, "E31.4.26.1", {"start": v(-201, -84) * mm, "end": v(-191, -84) * mm});
            skLineSegment(sketch, "E31.4.26.2", {"start": v(-201, -74) * mm, "end": v(-201, -84) * mm});
            skLineSegment(sketch, "E31.4.26.3", {"start": v(-191, -74) * mm, "end": v(-191, -84) * mm});
            skLineSegment(sketch, "E31.4.27.0", {"start": v(-201, -60) * mm, "end": v(-191, -60) * mm});
            skLineSegment(sketch, "E31.4.27.1", {"start": v(-201, -70) * mm, "end": v(-191, -70) * mm});
            skLineSegment(sketch, "E31.4.27.2", {"start": v(-201, -60) * mm, "end": v(-201, -70) * mm});
            skLineSegment(sketch, "E31.4.27.3", {"start": v(-191, -60) * mm, "end": v(-191, -70) * mm});
            skLineSegment(sketch, "E31.4.28.0", {"start": v(-201, -46) * mm, "end": v(-191, -46) * mm});
            skLineSegment(sketch, "E31.4.28.1", {"start": v(-201, -56) * mm, "end": v(-191, -56) * mm});
            skLineSegment(sketch, "E31.4.28.2", {"start": v(-201, -46) * mm, "end": v(-201, -56) * mm});
            skLineSegment(sketch, "E31.4.28.3", {"start": v(-191, -46) * mm, "end": v(-191, -56) * mm});
            skLineSegment(sketch, "E31.4.29.0", {"start": v(-201, -32) * mm, "end": v(-191, -32) * mm});
            skLineSegment(sketch, "E31.4.29.1", {"start": v(-201, -42) * mm, "end": v(-191, -42) * mm});
            skLineSegment(sketch, "E31.4.29.2", {"start": v(-201, -32) * mm, "end": v(-201, -42) * mm});
            skLineSegment(sketch, "E31.4.29.3", {"start": v(-191, -32) * mm, "end": v(-191, -42) * mm});
            skLineSegment(sketch, "E31.4.30.0", {"start": v(-201, -18) * mm, "end": v(-191, -18) * mm});
            skLineSegment(sketch, "E31.4.30.1", {"start": v(-201, -28) * mm, "end": v(-191, -28) * mm});
            skLineSegment(sketch, "E31.4.30.2", {"start": v(-201, -18) * mm, "end": v(-201, -28) * mm});
            skLineSegment(sketch, "E31.4.30.3", {"start": v(-191, -18) * mm, "end": v(-191, -28) * mm});
            skLineSegment(sketch, "E31.4.31.0", {"start": v(-201, -4) * mm, "end": v(-191, -4) * mm});
            skLineSegment(sketch, "E31.4.31.1", {"start": v(-201, -14) * mm, "end": v(-191, -14) * mm});
            skLineSegment(sketch, "E31.4.31.2", {"start": v(-201, -4) * mm, "end": v(-201, -14) * mm});
            skLineSegment(sketch, "E31.4.31.3", {"start": v(-191, -4) * mm, "end": v(-191, -14) * mm});
            skLineSegment(sketch, "E31.5.0.0", {"start": v(-187, -438) * mm, "end": v(-177, -438) * mm});
            skLineSegment(sketch, "E31.5.0.1", {"start": v(-187, -448) * mm, "end": v(-177, -448) * mm});
            skLineSegment(sketch, "E31.5.0.2", {"start": v(-187, -438) * mm, "end": v(-187, -448) * mm});
            skLineSegment(sketch, "E31.5.0.3", {"start": v(-177, -438) * mm, "end": v(-177, -448) * mm});
            skLineSegment(sketch, "E31.5.1.0", {"start": v(-187, -424) * mm, "end": v(-177, -424) * mm});
            skLineSegment(sketch, "E31.5.1.1", {"start": v(-187, -434) * mm, "end": v(-177, -434) * mm});
            skLineSegment(sketch, "E31.5.1.2", {"start": v(-187, -424) * mm, "end": v(-187, -434) * mm});
            skLineSegment(sketch, "E31.5.1.3", {"start": v(-177, -424) * mm, "end": v(-177, -434) * mm});
            skLineSegment(sketch, "E31.5.2.0", {"start": v(-187, -410) * mm, "end": v(-177, -410) * mm});
            skLineSegment(sketch, "E31.5.2.1", {"start": v(-187, -420) * mm, "end": v(-177, -420) * mm});
            skLineSegment(sketch, "E31.5.2.2", {"start": v(-187, -410) * mm, "end": v(-187, -420) * mm});
            skLineSegment(sketch, "E31.5.2.3", {"start": v(-177, -410) * mm, "end": v(-177, -420) * mm});
            skLineSegment(sketch, "E31.5.3.0", {"start": v(-187, -396) * mm, "end": v(-177, -396) * mm});
            skLineSegment(sketch, "E31.5.3.1", {"start": v(-187, -406) * mm, "end": v(-177, -406) * mm});
            skLineSegment(sketch, "E31.5.3.2", {"start": v(-187, -396) * mm, "end": v(-187, -406) * mm});
            skLineSegment(sketch, "E31.5.3.3", {"start": v(-177, -396) * mm, "end": v(-177, -406) * mm});
            skLineSegment(sketch, "E31.5.4.0", {"start": v(-187, -382) * mm, "end": v(-177, -382) * mm});
            skLineSegment(sketch, "E31.5.4.1", {"start": v(-187, -392) * mm, "end": v(-177, -392) * mm});
            skLineSegment(sketch, "E31.5.4.2", {"start": v(-187, -382) * mm, "end": v(-187, -392) * mm});
            skLineSegment(sketch, "E31.5.4.3", {"start": v(-177, -382) * mm, "end": v(-177, -392) * mm});
            skLineSegment(sketch, "E31.5.5.0", {"start": v(-187, -368) * mm, "end": v(-177, -368) * mm});
            skLineSegment(sketch, "E31.5.5.1", {"start": v(-187, -378) * mm, "end": v(-177, -378) * mm});
            skLineSegment(sketch, "E31.5.5.2", {"start": v(-187, -368) * mm, "end": v(-187, -378) * mm});
            skLineSegment(sketch, "E31.5.5.3", {"start": v(-177, -368) * mm, "end": v(-177, -378) * mm});
            skLineSegment(sketch, "E31.5.6.0", {"start": v(-187, -354) * mm, "end": v(-177, -354) * mm});
            skLineSegment(sketch, "E31.5.6.1", {"start": v(-187, -364) * mm, "end": v(-177, -364) * mm});
            skLineSegment(sketch, "E31.5.6.2", {"start": v(-187, -354) * mm, "end": v(-187, -364) * mm});
            skLineSegment(sketch, "E31.5.6.3", {"start": v(-177, -354) * mm, "end": v(-177, -364) * mm});
            skLineSegment(sketch, "E31.5.7.0", {"start": v(-187, -340) * mm, "end": v(-177, -340) * mm});
            skLineSegment(sketch, "E31.5.7.1", {"start": v(-187, -350) * mm, "end": v(-177, -350) * mm});
            skLineSegment(sketch, "E31.5.7.2", {"start": v(-187, -340) * mm, "end": v(-187, -350) * mm});
            skLineSegment(sketch, "E31.5.7.3", {"start": v(-177, -340) * mm, "end": v(-177, -350) * mm});
            skLineSegment(sketch, "E31.5.8.0", {"start": v(-187, -326) * mm, "end": v(-177, -326) * mm});
            skLineSegment(sketch, "E31.5.8.1", {"start": v(-187, -336) * mm, "end": v(-177, -336) * mm});
            skLineSegment(sketch, "E31.5.8.2", {"start": v(-187, -326) * mm, "end": v(-187, -336) * mm});
            skLineSegment(sketch, "E31.5.8.3", {"start": v(-177, -326) * mm, "end": v(-177, -336) * mm});
            skLineSegment(sketch, "E31.5.9.0", {"start": v(-187, -312) * mm, "end": v(-177, -312) * mm});
            skLineSegment(sketch, "E31.5.9.1", {"start": v(-187, -322) * mm, "end": v(-177, -322) * mm});
            skLineSegment(sketch, "E31.5.9.2", {"start": v(-187, -312) * mm, "end": v(-187, -322) * mm});
            skLineSegment(sketch, "E31.5.9.3", {"start": v(-177, -312) * mm, "end": v(-177, -322) * mm});
            skLineSegment(sketch, "E31.5.10.0", {"start": v(-187, -298) * mm, "end": v(-177, -298) * mm});
            skLineSegment(sketch, "E31.5.10.1", {"start": v(-187, -308) * mm, "end": v(-177, -308) * mm});
            skLineSegment(sketch, "E31.5.10.2", {"start": v(-187, -298) * mm, "end": v(-187, -308) * mm});
            skLineSegment(sketch, "E31.5.10.3", {"start": v(-177, -298) * mm, "end": v(-177, -308) * mm});
            skLineSegment(sketch, "E31.5.11.0", {"start": v(-187, -284) * mm, "end": v(-177, -284) * mm});
            skLineSegment(sketch, "E31.5.11.1", {"start": v(-187, -294) * mm, "end": v(-177, -294) * mm});
            skLineSegment(sketch, "E31.5.11.2", {"start": v(-187, -284) * mm, "end": v(-187, -294) * mm});
            skLineSegment(sketch, "E31.5.11.3", {"start": v(-177, -284) * mm, "end": v(-177, -294) * mm});
            skLineSegment(sketch, "E31.5.12.0", {"start": v(-187, -270) * mm, "end": v(-177, -270) * mm});
            skLineSegment(sketch, "E31.5.12.1", {"start": v(-187, -280) * mm, "end": v(-177, -280) * mm});
            skLineSegment(sketch, "E31.5.12.2", {"start": v(-187, -270) * mm, "end": v(-187, -280) * mm});
            skLineSegment(sketch, "E31.5.12.3", {"start": v(-177, -270) * mm, "end": v(-177, -280) * mm});
            skLineSegment(sketch, "E31.5.13.0", {"start": v(-187, -256) * mm, "end": v(-177, -256) * mm});
            skLineSegment(sketch, "E31.5.13.1", {"start": v(-187, -266) * mm, "end": v(-177, -266) * mm});
            skLineSegment(sketch, "E31.5.13.2", {"start": v(-187, -256) * mm, "end": v(-187, -266) * mm});
            skLineSegment(sketch, "E31.5.13.3", {"start": v(-177, -256) * mm, "end": v(-177, -266) * mm});
            skLineSegment(sketch, "E31.5.14.0", {"start": v(-187, -242) * mm, "end": v(-177, -242) * mm});
            skLineSegment(sketch, "E31.5.14.1", {"start": v(-187, -252) * mm, "end": v(-177, -252) * mm});
            skLineSegment(sketch, "E31.5.14.2", {"start": v(-187, -242) * mm, "end": v(-187, -252) * mm});
            skLineSegment(sketch, "E31.5.14.3", {"start": v(-177, -242) * mm, "end": v(-177, -252) * mm});
            skLineSegment(sketch, "E31.5.15.0", {"start": v(-187, -228) * mm, "end": v(-177, -228) * mm});
            skLineSegment(sketch, "E31.5.15.1", {"start": v(-187, -238) * mm, "end": v(-177, -238) * mm});
            skLineSegment(sketch, "E31.5.15.2", {"start": v(-187, -228) * mm, "end": v(-187, -238) * mm});
            skLineSegment(sketch, "E31.5.15.3", {"start": v(-177, -228) * mm, "end": v(-177, -238) * mm});
            skLineSegment(sketch, "E31.5.16.0", {"start": v(-187, -214) * mm, "end": v(-177, -214) * mm});
            skLineSegment(sketch, "E31.5.16.1", {"start": v(-187, -224) * mm, "end": v(-177, -224) * mm});
            skLineSegment(sketch, "E31.5.16.2", {"start": v(-187, -214) * mm, "end": v(-187, -224) * mm});
            skLineSegment(sketch, "E31.5.16.3", {"start": v(-177, -214) * mm, "end": v(-177, -224) * mm});
            skLineSegment(sketch, "E31.5.17.0", {"start": v(-187, -200) * mm, "end": v(-177, -200) * mm});
            skLineSegment(sketch, "E31.5.17.1", {"start": v(-187, -210) * mm, "end": v(-177, -210) * mm});
            skLineSegment(sketch, "E31.5.17.2", {"start": v(-187, -200) * mm, "end": v(-187, -210) * mm});
            skLineSegment(sketch, "E31.5.17.3", {"start": v(-177, -200) * mm, "end": v(-177, -210) * mm});
            skLineSegment(sketch, "E31.5.18.0", {"start": v(-187, -186) * mm, "end": v(-177, -186) * mm});
            skLineSegment(sketch, "E31.5.18.1", {"start": v(-187, -196) * mm, "end": v(-177, -196) * mm});
            skLineSegment(sketch, "E31.5.18.2", {"start": v(-187, -186) * mm, "end": v(-187, -196) * mm});
            skLineSegment(sketch, "E31.5.18.3", {"start": v(-177, -186) * mm, "end": v(-177, -196) * mm});
            skLineSegment(sketch, "E31.5.19.0", {"start": v(-187, -172) * mm, "end": v(-177, -172) * mm});
            skLineSegment(sketch, "E31.5.19.1", {"start": v(-187, -182) * mm, "end": v(-177, -182) * mm});
            skLineSegment(sketch, "E31.5.19.2", {"start": v(-187, -172) * mm, "end": v(-187, -182) * mm});
            skLineSegment(sketch, "E31.5.19.3", {"start": v(-177, -172) * mm, "end": v(-177, -182) * mm});
            skLineSegment(sketch, "E31.5.20.0", {"start": v(-187, -158) * mm, "end": v(-177, -158) * mm});
            skLineSegment(sketch, "E31.5.20.1", {"start": v(-187, -168) * mm, "end": v(-177, -168) * mm});
            skLineSegment(sketch, "E31.5.20.2", {"start": v(-187, -158) * mm, "end": v(-187, -168) * mm});
            skLineSegment(sketch, "E31.5.20.3", {"start": v(-177, -158) * mm, "end": v(-177, -168) * mm});
            skLineSegment(sketch, "E31.5.21.0", {"start": v(-187, -144) * mm, "end": v(-177, -144) * mm});
            skLineSegment(sketch, "E31.5.21.1", {"start": v(-187, -154) * mm, "end": v(-177, -154) * mm});
            skLineSegment(sketch, "E31.5.21.2", {"start": v(-187, -144) * mm, "end": v(-187, -154) * mm});
            skLineSegment(sketch, "E31.5.21.3", {"start": v(-177, -144) * mm, "end": v(-177, -154) * mm});
            skLineSegment(sketch, "E31.5.22.0", {"start": v(-187, -130) * mm, "end": v(-177, -130) * mm});
            skLineSegment(sketch, "E31.5.22.1", {"start": v(-187, -140) * mm, "end": v(-177, -140) * mm});
            skLineSegment(sketch, "E31.5.22.2", {"start": v(-187, -130) * mm, "end": v(-187, -140) * mm});
            skLineSegment(sketch, "E31.5.22.3", {"start": v(-177, -130) * mm, "end": v(-177, -140) * mm});
            skLineSegment(sketch, "E31.5.23.0", {"start": v(-187, -116) * mm, "end": v(-177, -116) * mm});
            skLineSegment(sketch, "E31.5.23.1", {"start": v(-187, -126) * mm, "end": v(-177, -126) * mm});
            skLineSegment(sketch, "E31.5.23.2", {"start": v(-187, -116) * mm, "end": v(-187, -126) * mm});
            skLineSegment(sketch, "E31.5.23.3", {"start": v(-177, -116) * mm, "end": v(-177, -126) * mm});
            skLineSegment(sketch, "E31.5.24.0", {"start": v(-187, -102) * mm, "end": v(-177, -102) * mm});
            skLineSegment(sketch, "E31.5.24.1", {"start": v(-187, -112) * mm, "end": v(-177, -112) * mm});
            skLineSegment(sketch, "E31.5.24.2", {"start": v(-187, -102) * mm, "end": v(-187, -112) * mm});
            skLineSegment(sketch, "E31.5.24.3", {"start": v(-177, -102) * mm, "end": v(-177, -112) * mm});
            skLineSegment(sketch, "E31.5.25.0", {"start": v(-187, -88) * mm, "end": v(-177, -88) * mm});
            skLineSegment(sketch, "E31.5.25.1", {"start": v(-187, -98) * mm, "end": v(-177, -98) * mm});
            skLineSegment(sketch, "E31.5.25.2", {"start": v(-187, -88) * mm, "end": v(-187, -98) * mm});
            skLineSegment(sketch, "E31.5.25.3", {"start": v(-177, -88) * mm, "end": v(-177, -98) * mm});
            skLineSegment(sketch, "E31.5.26.0", {"start": v(-187, -74) * mm, "end": v(-177, -74) * mm});
            skLineSegment(sketch, "E31.5.26.1", {"start": v(-187, -84) * mm, "end": v(-177, -84) * mm});
            skLineSegment(sketch, "E31.5.26.2", {"start": v(-187, -74) * mm, "end": v(-187, -84) * mm});
            skLineSegment(sketch, "E31.5.26.3", {"start": v(-177, -74) * mm, "end": v(-177, -84) * mm});
            skLineSegment(sketch, "E31.5.27.0", {"start": v(-187, -60) * mm, "end": v(-177, -60) * mm});
            skLineSegment(sketch, "E31.5.27.1", {"start": v(-187, -70) * mm, "end": v(-177, -70) * mm});
            skLineSegment(sketch, "E31.5.27.2", {"start": v(-187, -60) * mm, "end": v(-187, -70) * mm});
            skLineSegment(sketch, "E31.5.27.3", {"start": v(-177, -60) * mm, "end": v(-177, -70) * mm});
            skLineSegment(sketch, "E31.5.28.0", {"start": v(-187, -46) * mm, "end": v(-177, -46) * mm});
            skLineSegment(sketch, "E31.5.28.1", {"start": v(-187, -56) * mm, "end": v(-177, -56) * mm});
            skLineSegment(sketch, "E31.5.28.2", {"start": v(-187, -46) * mm, "end": v(-187, -56) * mm});
            skLineSegment(sketch, "E31.5.28.3", {"start": v(-177, -46) * mm, "end": v(-177, -56) * mm});
            skLineSegment(sketch, "E31.5.29.0", {"start": v(-187, -32) * mm, "end": v(-177, -32) * mm});
            skLineSegment(sketch, "E31.5.29.1", {"start": v(-187, -42) * mm, "end": v(-177, -42) * mm});
            skLineSegment(sketch, "E31.5.29.2", {"start": v(-187, -32) * mm, "end": v(-187, -42) * mm});
            skLineSegment(sketch, "E31.5.29.3", {"start": v(-177, -32) * mm, "end": v(-177, -42) * mm});
            skLineSegment(sketch, "E31.5.30.0", {"start": v(-187, -18) * mm, "end": v(-177, -18) * mm});
            skLineSegment(sketch, "E31.5.30.1", {"start": v(-187, -28) * mm, "end": v(-177, -28) * mm});
            skLineSegment(sketch, "E31.5.30.2", {"start": v(-187, -18) * mm, "end": v(-187, -28) * mm});
            skLineSegment(sketch, "E31.5.30.3", {"start": v(-177, -18) * mm, "end": v(-177, -28) * mm});
            skLineSegment(sketch, "E31.5.31.0", {"start": v(-187, -4) * mm, "end": v(-177, -4) * mm});
            skLineSegment(sketch, "E31.5.31.1", {"start": v(-187, -14) * mm, "end": v(-177, -14) * mm});
            skLineSegment(sketch, "E31.5.31.2", {"start": v(-187, -4) * mm, "end": v(-187, -14) * mm});
            skLineSegment(sketch, "E31.5.31.3", {"start": v(-177, -4) * mm, "end": v(-177, -14) * mm});
            skLineSegment(sketch, "E31.6.0.0", {"start": v(-173, -438) * mm, "end": v(-163, -438) * mm});
            skLineSegment(sketch, "E31.6.0.1", {"start": v(-173, -448) * mm, "end": v(-163, -448) * mm});
            skLineSegment(sketch, "E31.6.0.2", {"start": v(-173, -438) * mm, "end": v(-173, -448) * mm});
            skLineSegment(sketch, "E31.6.0.3", {"start": v(-163, -438) * mm, "end": v(-163, -448) * mm});
            skLineSegment(sketch, "E31.6.1.0", {"start": v(-173, -424) * mm, "end": v(-163, -424) * mm});
            skLineSegment(sketch, "E31.6.1.1", {"start": v(-173, -434) * mm, "end": v(-163, -434) * mm});
            skLineSegment(sketch, "E31.6.1.2", {"start": v(-173, -424) * mm, "end": v(-173, -434) * mm});
            skLineSegment(sketch, "E31.6.1.3", {"start": v(-163, -424) * mm, "end": v(-163, -434) * mm});
            skLineSegment(sketch, "E31.6.2.0", {"start": v(-173, -410) * mm, "end": v(-163, -410) * mm});
            skLineSegment(sketch, "E31.6.2.1", {"start": v(-173, -420) * mm, "end": v(-163, -420) * mm});
            skLineSegment(sketch, "E31.6.2.2", {"start": v(-173, -410) * mm, "end": v(-173, -420) * mm});
            skLineSegment(sketch, "E31.6.2.3", {"start": v(-163, -410) * mm, "end": v(-163, -420) * mm});
            skLineSegment(sketch, "E31.6.3.0", {"start": v(-173, -396) * mm, "end": v(-163, -396) * mm});
            skLineSegment(sketch, "E31.6.3.1", {"start": v(-173, -406) * mm, "end": v(-163, -406) * mm});
            skLineSegment(sketch, "E31.6.3.2", {"start": v(-173, -396) * mm, "end": v(-173, -406) * mm});
            skLineSegment(sketch, "E31.6.3.3", {"start": v(-163, -396) * mm, "end": v(-163, -406) * mm});
            skLineSegment(sketch, "E31.6.4.0", {"start": v(-173, -382) * mm, "end": v(-163, -382) * mm});
            skLineSegment(sketch, "E31.6.4.1", {"start": v(-173, -392) * mm, "end": v(-163, -392) * mm});
            skLineSegment(sketch, "E31.6.4.2", {"start": v(-173, -382) * mm, "end": v(-173, -392) * mm});
            skLineSegment(sketch, "E31.6.4.3", {"start": v(-163, -382) * mm, "end": v(-163, -392) * mm});
            skLineSegment(sketch, "E31.6.5.0", {"start": v(-173, -368) * mm, "end": v(-163, -368) * mm});
            skLineSegment(sketch, "E31.6.5.1", {"start": v(-173, -378) * mm, "end": v(-163, -378) * mm});
            skLineSegment(sketch, "E31.6.5.2", {"start": v(-173, -368) * mm, "end": v(-173, -378) * mm});
            skLineSegment(sketch, "E31.6.5.3", {"start": v(-163, -368) * mm, "end": v(-163, -378) * mm});
            skLineSegment(sketch, "E31.6.6.0", {"start": v(-173, -354) * mm, "end": v(-163, -354) * mm});
            skLineSegment(sketch, "E31.6.6.1", {"start": v(-173, -364) * mm, "end": v(-163, -364) * mm});
            skLineSegment(sketch, "E31.6.6.2", {"start": v(-173, -354) * mm, "end": v(-173, -364) * mm});
            skLineSegment(sketch, "E31.6.6.3", {"start": v(-163, -354) * mm, "end": v(-163, -364) * mm});
            skLineSegment(sketch, "E31.6.7.0", {"start": v(-173, -340) * mm, "end": v(-163, -340) * mm});
            skLineSegment(sketch, "E31.6.7.1", {"start": v(-173, -350) * mm, "end": v(-163, -350) * mm});
            skLineSegment(sketch, "E31.6.7.2", {"start": v(-173, -340) * mm, "end": v(-173, -350) * mm});
            skLineSegment(sketch, "E31.6.7.3", {"start": v(-163, -340) * mm, "end": v(-163, -350) * mm});
            skLineSegment(sketch, "E31.6.8.0", {"start": v(-173, -326) * mm, "end": v(-163, -326) * mm});
            skLineSegment(sketch, "E31.6.8.1", {"start": v(-173, -336) * mm, "end": v(-163, -336) * mm});
            skLineSegment(sketch, "E31.6.8.2", {"start": v(-173, -326) * mm, "end": v(-173, -336) * mm});
            skLineSegment(sketch, "E31.6.8.3", {"start": v(-163, -326) * mm, "end": v(-163, -336) * mm});
            skLineSegment(sketch, "E31.6.9.0", {"start": v(-173, -312) * mm, "end": v(-163, -312) * mm});
            skLineSegment(sketch, "E31.6.9.1", {"start": v(-173, -322) * mm, "end": v(-163, -322) * mm});
            skLineSegment(sketch, "E31.6.9.2", {"start": v(-173, -312) * mm, "end": v(-173, -322) * mm});
            skLineSegment(sketch, "E31.6.9.3", {"start": v(-163, -312) * mm, "end": v(-163, -322) * mm});
            skLineSegment(sketch, "E31.6.10.0", {"start": v(-173, -298) * mm, "end": v(-163, -298) * mm});
            skLineSegment(sketch, "E31.6.10.1", {"start": v(-173, -308) * mm, "end": v(-163, -308) * mm});
            skLineSegment(sketch, "E31.6.10.2", {"start": v(-173, -298) * mm, "end": v(-173, -308) * mm});
            skLineSegment(sketch, "E31.6.10.3", {"start": v(-163, -298) * mm, "end": v(-163, -308) * mm});
            skLineSegment(sketch, "E31.6.11.0", {"start": v(-173, -284) * mm, "end": v(-163, -284) * mm});
            skLineSegment(sketch, "E31.6.11.1", {"start": v(-173, -294) * mm, "end": v(-163, -294) * mm});
            skLineSegment(sketch, "E31.6.11.2", {"start": v(-173, -284) * mm, "end": v(-173, -294) * mm});
            skLineSegment(sketch, "E31.6.11.3", {"start": v(-163, -284) * mm, "end": v(-163, -294) * mm});
            skLineSegment(sketch, "E31.6.12.0", {"start": v(-173, -270) * mm, "end": v(-163, -270) * mm});
            skLineSegment(sketch, "E31.6.12.1", {"start": v(-173, -280) * mm, "end": v(-163, -280) * mm});
            skLineSegment(sketch, "E31.6.12.2", {"start": v(-173, -270) * mm, "end": v(-173, -280) * mm});
            skLineSegment(sketch, "E31.6.12.3", {"start": v(-163, -270) * mm, "end": v(-163, -280) * mm});
            skLineSegment(sketch, "E31.6.13.0", {"start": v(-173, -256) * mm, "end": v(-163, -256) * mm});
            skLineSegment(sketch, "E31.6.13.1", {"start": v(-173, -266) * mm, "end": v(-163, -266) * mm});
            skLineSegment(sketch, "E31.6.13.2", {"start": v(-173, -256) * mm, "end": v(-173, -266) * mm});
            skLineSegment(sketch, "E31.6.13.3", {"start": v(-163, -256) * mm, "end": v(-163, -266) * mm});
            skLineSegment(sketch, "E31.6.14.0", {"start": v(-173, -242) * mm, "end": v(-163, -242) * mm});
            skLineSegment(sketch, "E31.6.14.1", {"start": v(-173, -252) * mm, "end": v(-163, -252) * mm});
            skLineSegment(sketch, "E31.6.14.2", {"start": v(-173, -242) * mm, "end": v(-173, -252) * mm});
            skLineSegment(sketch, "E31.6.14.3", {"start": v(-163, -242) * mm, "end": v(-163, -252) * mm});
            skLineSegment(sketch, "E31.6.15.0", {"start": v(-173, -228) * mm, "end": v(-163, -228) * mm});
            skLineSegment(sketch, "E31.6.15.1", {"start": v(-173, -238) * mm, "end": v(-163, -238) * mm});
            skLineSegment(sketch, "E31.6.15.2", {"start": v(-173, -228) * mm, "end": v(-173, -238) * mm});
            skLineSegment(sketch, "E31.6.15.3", {"start": v(-163, -228) * mm, "end": v(-163, -238) * mm});
            skLineSegment(sketch, "E31.6.16.0", {"start": v(-173, -214) * mm, "end": v(-163, -214) * mm});
            skLineSegment(sketch, "E31.6.16.1", {"start": v(-173, -224) * mm, "end": v(-163, -224) * mm});
            skLineSegment(sketch, "E31.6.16.2", {"start": v(-173, -214) * mm, "end": v(-173, -224) * mm});
            skLineSegment(sketch, "E31.6.16.3", {"start": v(-163, -214) * mm, "end": v(-163, -224) * mm});
            skLineSegment(sketch, "E31.6.17.0", {"start": v(-173, -200) * mm, "end": v(-163, -200) * mm});
            skLineSegment(sketch, "E31.6.17.1", {"start": v(-173, -210) * mm, "end": v(-163, -210) * mm});
            skLineSegment(sketch, "E31.6.17.2", {"start": v(-173, -200) * mm, "end": v(-173, -210) * mm});
            skLineSegment(sketch, "E31.6.17.3", {"start": v(-163, -200) * mm, "end": v(-163, -210) * mm});
            skLineSegment(sketch, "E31.6.18.0", {"start": v(-173, -186) * mm, "end": v(-163, -186) * mm});
            skLineSegment(sketch, "E31.6.18.1", {"start": v(-173, -196) * mm, "end": v(-163, -196) * mm});
            skLineSegment(sketch, "E31.6.18.2", {"start": v(-173, -186) * mm, "end": v(-173, -196) * mm});
            skLineSegment(sketch, "E31.6.18.3", {"start": v(-163, -186) * mm, "end": v(-163, -196) * mm});
            skLineSegment(sketch, "E31.6.19.0", {"start": v(-173, -172) * mm, "end": v(-163, -172) * mm});
            skLineSegment(sketch, "E31.6.19.1", {"start": v(-173, -182) * mm, "end": v(-163, -182) * mm});
            skLineSegment(sketch, "E31.6.19.2", {"start": v(-173, -172) * mm, "end": v(-173, -182) * mm});
            skLineSegment(sketch, "E31.6.19.3", {"start": v(-163, -172) * mm, "end": v(-163, -182) * mm});
            skLineSegment(sketch, "E31.6.20.0", {"start": v(-173, -158) * mm, "end": v(-163, -158) * mm});
            skLineSegment(sketch, "E31.6.20.1", {"start": v(-173, -168) * mm, "end": v(-163, -168) * mm});
            skLineSegment(sketch, "E31.6.20.2", {"start": v(-173, -158) * mm, "end": v(-173, -168) * mm});
            skLineSegment(sketch, "E31.6.20.3", {"start": v(-163, -158) * mm, "end": v(-163, -168) * mm});
            skLineSegment(sketch, "E31.6.21.0", {"start": v(-173, -144) * mm, "end": v(-163, -144) * mm});
            skLineSegment(sketch, "E31.6.21.1", {"start": v(-173, -154) * mm, "end": v(-163, -154) * mm});
            skLineSegment(sketch, "E31.6.21.2", {"start": v(-173, -144) * mm, "end": v(-173, -154) * mm});
            skLineSegment(sketch, "E31.6.21.3", {"start": v(-163, -144) * mm, "end": v(-163, -154) * mm});
            skLineSegment(sketch, "E31.6.22.0", {"start": v(-173, -130) * mm, "end": v(-163, -130) * mm});
            skLineSegment(sketch, "E31.6.22.1", {"start": v(-173, -140) * mm, "end": v(-163, -140) * mm});
            skLineSegment(sketch, "E31.6.22.2", {"start": v(-173, -130) * mm, "end": v(-173, -140) * mm});
            skLineSegment(sketch, "E31.6.22.3", {"start": v(-163, -130) * mm, "end": v(-163, -140) * mm});
            skLineSegment(sketch, "E31.6.23.0", {"start": v(-173, -116) * mm, "end": v(-163, -116) * mm});
            skLineSegment(sketch, "E31.6.23.1", {"start": v(-173, -126) * mm, "end": v(-163, -126) * mm});
            skLineSegment(sketch, "E31.6.23.2", {"start": v(-173, -116) * mm, "end": v(-173, -126) * mm});
            skLineSegment(sketch, "E31.6.23.3", {"start": v(-163, -116) * mm, "end": v(-163, -126) * mm});
            skLineSegment(sketch, "E31.6.24.0", {"start": v(-173, -102) * mm, "end": v(-163, -102) * mm});
            skLineSegment(sketch, "E31.6.24.1", {"start": v(-173, -112) * mm, "end": v(-163, -112) * mm});
            skLineSegment(sketch, "E31.6.24.2", {"start": v(-173, -102) * mm, "end": v(-173, -112) * mm});
            skLineSegment(sketch, "E31.6.24.3", {"start": v(-163, -102) * mm, "end": v(-163, -112) * mm});
            skLineSegment(sketch, "E31.6.25.0", {"start": v(-173, -88) * mm, "end": v(-163, -88) * mm});
            skLineSegment(sketch, "E31.6.25.1", {"start": v(-173, -98) * mm, "end": v(-163, -98) * mm});
            skLineSegment(sketch, "E31.6.25.2", {"start": v(-173, -88) * mm, "end": v(-173, -98) * mm});
            skLineSegment(sketch, "E31.6.25.3", {"start": v(-163, -88) * mm, "end": v(-163, -98) * mm});
            skLineSegment(sketch, "E31.6.26.0", {"start": v(-173, -74) * mm, "end": v(-163, -74) * mm});
            skLineSegment(sketch, "E31.6.26.1", {"start": v(-173, -84) * mm, "end": v(-163, -84) * mm});
            skLineSegment(sketch, "E31.6.26.2", {"start": v(-173, -74) * mm, "end": v(-173, -84) * mm});
            skLineSegment(sketch, "E31.6.26.3", {"start": v(-163, -74) * mm, "end": v(-163, -84) * mm});
            skLineSegment(sketch, "E31.6.27.0", {"start": v(-173, -60) * mm, "end": v(-163, -60) * mm});
            skLineSegment(sketch, "E31.6.27.1", {"start": v(-173, -70) * mm, "end": v(-163, -70) * mm});
            skLineSegment(sketch, "E31.6.27.2", {"start": v(-173, -60) * mm, "end": v(-173, -70) * mm});
            skLineSegment(sketch, "E31.6.27.3", {"start": v(-163, -60) * mm, "end": v(-163, -70) * mm});
            skLineSegment(sketch, "E31.6.28.0", {"start": v(-173, -46) * mm, "end": v(-163, -46) * mm});
            skLineSegment(sketch, "E31.6.28.1", {"start": v(-173, -56) * mm, "end": v(-163, -56) * mm});
            skLineSegment(sketch, "E31.6.28.2", {"start": v(-173, -46) * mm, "end": v(-173, -56) * mm});
            skLineSegment(sketch, "E31.6.28.3", {"start": v(-163, -46) * mm, "end": v(-163, -56) * mm});
            skLineSegment(sketch, "E31.6.29.0", {"start": v(-173, -32) * mm, "end": v(-163, -32) * mm});
            skLineSegment(sketch, "E31.6.29.1", {"start": v(-173, -42) * mm, "end": v(-163, -42) * mm});
            skLineSegment(sketch, "E31.6.29.2", {"start": v(-173, -32) * mm, "end": v(-173, -42) * mm});
            skLineSegment(sketch, "E31.6.29.3", {"start": v(-163, -32) * mm, "end": v(-163, -42) * mm});
            skLineSegment(sketch, "E31.6.30.0", {"start": v(-173, -18) * mm, "end": v(-163, -18) * mm});
            skLineSegment(sketch, "E31.6.30.1", {"start": v(-173, -28) * mm, "end": v(-163, -28) * mm});
            skLineSegment(sketch, "E31.6.30.2", {"start": v(-173, -18) * mm, "end": v(-173, -28) * mm});
            skLineSegment(sketch, "E31.6.30.3", {"start": v(-163, -18) * mm, "end": v(-163, -28) * mm});
            skLineSegment(sketch, "E31.6.31.0", {"start": v(-173, -4) * mm, "end": v(-163, -4) * mm});
            skLineSegment(sketch, "E31.6.31.1", {"start": v(-173, -14) * mm, "end": v(-163, -14) * mm});
            skLineSegment(sketch, "E31.6.31.2", {"start": v(-173, -4) * mm, "end": v(-173, -14) * mm});
            skLineSegment(sketch, "E31.6.31.3", {"start": v(-163, -4) * mm, "end": v(-163, -14) * mm});
            skLineSegment(sketch, "E31.7.0.0", {"start": v(-159, -438) * mm, "end": v(-149, -438) * mm});
            skLineSegment(sketch, "E31.7.0.1", {"start": v(-159, -448) * mm, "end": v(-149, -448) * mm});
            skLineSegment(sketch, "E31.7.0.2", {"start": v(-159, -438) * mm, "end": v(-159, -448) * mm});
            skLineSegment(sketch, "E31.7.0.3", {"start": v(-149, -438) * mm, "end": v(-149, -448) * mm});
            skLineSegment(sketch, "E31.7.1.0", {"start": v(-159, -424) * mm, "end": v(-149, -424) * mm});
            skLineSegment(sketch, "E31.7.1.1", {"start": v(-159, -434) * mm, "end": v(-149, -434) * mm});
            skLineSegment(sketch, "E31.7.1.2", {"start": v(-159, -424) * mm, "end": v(-159, -434) * mm});
            skLineSegment(sketch, "E31.7.1.3", {"start": v(-149, -424) * mm, "end": v(-149, -434) * mm});
            skLineSegment(sketch, "E31.7.2.0", {"start": v(-159, -410) * mm, "end": v(-149, -410) * mm});
            skLineSegment(sketch, "E31.7.2.1", {"start": v(-159, -420) * mm, "end": v(-149, -420) * mm});
            skLineSegment(sketch, "E31.7.2.2", {"start": v(-159, -410) * mm, "end": v(-159, -420) * mm});
            skLineSegment(sketch, "E31.7.2.3", {"start": v(-149, -410) * mm, "end": v(-149, -420) * mm});
            skLineSegment(sketch, "E31.7.3.0", {"start": v(-159, -396) * mm, "end": v(-149, -396) * mm});
            skLineSegment(sketch, "E31.7.3.1", {"start": v(-159, -406) * mm, "end": v(-149, -406) * mm});
            skLineSegment(sketch, "E31.7.3.2", {"start": v(-159, -396) * mm, "end": v(-159, -406) * mm});
            skLineSegment(sketch, "E31.7.3.3", {"start": v(-149, -396) * mm, "end": v(-149, -406) * mm});
            skLineSegment(sketch, "E31.7.4.0", {"start": v(-159, -382) * mm, "end": v(-149, -382) * mm});
            skLineSegment(sketch, "E31.7.4.1", {"start": v(-159, -392) * mm, "end": v(-149, -392) * mm});
            skLineSegment(sketch, "E31.7.4.2", {"start": v(-159, -382) * mm, "end": v(-159, -392) * mm});
            skLineSegment(sketch, "E31.7.4.3", {"start": v(-149, -382) * mm, "end": v(-149, -392) * mm});
            skLineSegment(sketch, "E31.7.5.0", {"start": v(-159, -368) * mm, "end": v(-149, -368) * mm});
            skLineSegment(sketch, "E31.7.5.1", {"start": v(-159, -378) * mm, "end": v(-149, -378) * mm});
            skLineSegment(sketch, "E31.7.5.2", {"start": v(-159, -368) * mm, "end": v(-159, -378) * mm});
            skLineSegment(sketch, "E31.7.5.3", {"start": v(-149, -368) * mm, "end": v(-149, -378) * mm});
            skLineSegment(sketch, "E31.7.6.0", {"start": v(-159, -354) * mm, "end": v(-149, -354) * mm});
            skLineSegment(sketch, "E31.7.6.1", {"start": v(-159, -364) * mm, "end": v(-149, -364) * mm});
            skLineSegment(sketch, "E31.7.6.2", {"start": v(-159, -354) * mm, "end": v(-159, -364) * mm});
            skLineSegment(sketch, "E31.7.6.3", {"start": v(-149, -354) * mm, "end": v(-149, -364) * mm});
            skLineSegment(sketch, "E31.7.7.0", {"start": v(-159, -340) * mm, "end": v(-149, -340) * mm});
            skLineSegment(sketch, "E31.7.7.1", {"start": v(-159, -350) * mm, "end": v(-149, -350) * mm});
            skLineSegment(sketch, "E31.7.7.2", {"start": v(-159, -340) * mm, "end": v(-159, -350) * mm});
            skLineSegment(sketch, "E31.7.7.3", {"start": v(-149, -340) * mm, "end": v(-149, -350) * mm});
            skLineSegment(sketch, "E31.7.8.0", {"start": v(-159, -326) * mm, "end": v(-149, -326) * mm});
            skLineSegment(sketch, "E31.7.8.1", {"start": v(-159, -336) * mm, "end": v(-149, -336) * mm});
            skLineSegment(sketch, "E31.7.8.2", {"start": v(-159, -326) * mm, "end": v(-159, -336) * mm});
            skLineSegment(sketch, "E31.7.8.3", {"start": v(-149, -326) * mm, "end": v(-149, -336) * mm});
            skLineSegment(sketch, "E31.7.9.0", {"start": v(-159, -312) * mm, "end": v(-149, -312) * mm});
            skLineSegment(sketch, "E31.7.9.1", {"start": v(-159, -322) * mm, "end": v(-149, -322) * mm});
            skLineSegment(sketch, "E31.7.9.2", {"start": v(-159, -312) * mm, "end": v(-159, -322) * mm});
            skLineSegment(sketch, "E31.7.9.3", {"start": v(-149, -312) * mm, "end": v(-149, -322) * mm});
            skLineSegment(sketch, "E31.7.10.0", {"start": v(-159, -298) * mm, "end": v(-149, -298) * mm});
            skLineSegment(sketch, "E31.7.10.1", {"start": v(-159, -308) * mm, "end": v(-149, -308) * mm});
            skLineSegment(sketch, "E31.7.10.2", {"start": v(-159, -298) * mm, "end": v(-159, -308) * mm});
            skLineSegment(sketch, "E31.7.10.3", {"start": v(-149, -298) * mm, "end": v(-149, -308) * mm});
            skLineSegment(sketch, "E31.7.11.0", {"start": v(-159, -284) * mm, "end": v(-149, -284) * mm});
            skLineSegment(sketch, "E31.7.11.1", {"start": v(-159, -294) * mm, "end": v(-149, -294) * mm});
            skLineSegment(sketch, "E31.7.11.2", {"start": v(-159, -284) * mm, "end": v(-159, -294) * mm});
            skLineSegment(sketch, "E31.7.11.3", {"start": v(-149, -284) * mm, "end": v(-149, -294) * mm});
            skLineSegment(sketch, "E31.7.12.0", {"start": v(-159, -270) * mm, "end": v(-149, -270) * mm});
            skLineSegment(sketch, "E31.7.12.1", {"start": v(-159, -280) * mm, "end": v(-149, -280) * mm});
            skLineSegment(sketch, "E31.7.12.2", {"start": v(-159, -270) * mm, "end": v(-159, -280) * mm});
            skLineSegment(sketch, "E31.7.12.3", {"start": v(-149, -270) * mm, "end": v(-149, -280) * mm});
            skLineSegment(sketch, "E31.7.13.0", {"start": v(-159, -256) * mm, "end": v(-149, -256) * mm});
            skLineSegment(sketch, "E31.7.13.1", {"start": v(-159, -266) * mm, "end": v(-149, -266) * mm});
            skLineSegment(sketch, "E31.7.13.2", {"start": v(-159, -256) * mm, "end": v(-159, -266) * mm});
            skLineSegment(sketch, "E31.7.13.3", {"start": v(-149, -256) * mm, "end": v(-149, -266) * mm});
            skLineSegment(sketch, "E31.7.14.0", {"start": v(-159, -242) * mm, "end": v(-149, -242) * mm});
            skLineSegment(sketch, "E31.7.14.1", {"start": v(-159, -252) * mm, "end": v(-149, -252) * mm});
            skLineSegment(sketch, "E31.7.14.2", {"start": v(-159, -242) * mm, "end": v(-159, -252) * mm});
            skLineSegment(sketch, "E31.7.14.3", {"start": v(-149, -242) * mm, "end": v(-149, -252) * mm});
            skLineSegment(sketch, "E31.7.15.0", {"start": v(-159, -228) * mm, "end": v(-149, -228) * mm});
            skLineSegment(sketch, "E31.7.15.1", {"start": v(-159, -238) * mm, "end": v(-149, -238) * mm});
            skLineSegment(sketch, "E31.7.15.2", {"start": v(-159, -228) * mm, "end": v(-159, -238) * mm});
            skLineSegment(sketch, "E31.7.15.3", {"start": v(-149, -228) * mm, "end": v(-149, -238) * mm});
            skLineSegment(sketch, "E31.7.16.0", {"start": v(-159, -214) * mm, "end": v(-149, -214) * mm});
            skLineSegment(sketch, "E31.7.16.1", {"start": v(-159, -224) * mm, "end": v(-149, -224) * mm});
            skLineSegment(sketch, "E31.7.16.2", {"start": v(-159, -214) * mm, "end": v(-159, -224) * mm});
            skLineSegment(sketch, "E31.7.16.3", {"start": v(-149, -214) * mm, "end": v(-149, -224) * mm});
            skLineSegment(sketch, "E31.7.17.0", {"start": v(-159, -200) * mm, "end": v(-149, -200) * mm});
            skLineSegment(sketch, "E31.7.17.1", {"start": v(-159, -210) * mm, "end": v(-149, -210) * mm});
            skLineSegment(sketch, "E31.7.17.2", {"start": v(-159, -200) * mm, "end": v(-159, -210) * mm});
            skLineSegment(sketch, "E31.7.17.3", {"start": v(-149, -200) * mm, "end": v(-149, -210) * mm});
            skLineSegment(sketch, "E31.7.18.0", {"start": v(-159, -186) * mm, "end": v(-149, -186) * mm});
            skLineSegment(sketch, "E31.7.18.1", {"start": v(-159, -196) * mm, "end": v(-149, -196) * mm});
            skLineSegment(sketch, "E31.7.18.2", {"start": v(-159, -186) * mm, "end": v(-159, -196) * mm});
            skLineSegment(sketch, "E31.7.18.3", {"start": v(-149, -186) * mm, "end": v(-149, -196) * mm});
            skLineSegment(sketch, "E31.7.19.0", {"start": v(-159, -172) * mm, "end": v(-149, -172) * mm});
            skLineSegment(sketch, "E31.7.19.1", {"start": v(-159, -182) * mm, "end": v(-149, -182) * mm});
            skLineSegment(sketch, "E31.7.19.2", {"start": v(-159, -172) * mm, "end": v(-159, -182) * mm});
            skLineSegment(sketch, "E31.7.19.3", {"start": v(-149, -172) * mm, "end": v(-149, -182) * mm});
            skLineSegment(sketch, "E31.7.20.0", {"start": v(-159, -158) * mm, "end": v(-149, -158) * mm});
            skLineSegment(sketch, "E31.7.20.1", {"start": v(-159, -168) * mm, "end": v(-149, -168) * mm});
            skLineSegment(sketch, "E31.7.20.2", {"start": v(-159, -158) * mm, "end": v(-159, -168) * mm});
            skLineSegment(sketch, "E31.7.20.3", {"start": v(-149, -158) * mm, "end": v(-149, -168) * mm});
            skLineSegment(sketch, "E31.7.21.0", {"start": v(-159, -144) * mm, "end": v(-149, -144) * mm});
            skLineSegment(sketch, "E31.7.21.1", {"start": v(-159, -154) * mm, "end": v(-149, -154) * mm});
            skLineSegment(sketch, "E31.7.21.2", {"start": v(-159, -144) * mm, "end": v(-159, -154) * mm});
            skLineSegment(sketch, "E31.7.21.3", {"start": v(-149, -144) * mm, "end": v(-149, -154) * mm});
            skLineSegment(sketch, "E31.7.22.0", {"start": v(-159, -130) * mm, "end": v(-149, -130) * mm});
            skLineSegment(sketch, "E31.7.22.1", {"start": v(-159, -140) * mm, "end": v(-149, -140) * mm});
            skLineSegment(sketch, "E31.7.22.2", {"start": v(-159, -130) * mm, "end": v(-159, -140) * mm});
            skLineSegment(sketch, "E31.7.22.3", {"start": v(-149, -130) * mm, "end": v(-149, -140) * mm});
            skLineSegment(sketch, "E31.7.23.0", {"start": v(-159, -116) * mm, "end": v(-149, -116) * mm});
            skLineSegment(sketch, "E31.7.23.1", {"start": v(-159, -126) * mm, "end": v(-149, -126) * mm});
            skLineSegment(sketch, "E31.7.23.2", {"start": v(-159, -116) * mm, "end": v(-159, -126) * mm});
            skLineSegment(sketch, "E31.7.23.3", {"start": v(-149, -116) * mm, "end": v(-149, -126) * mm});
            skLineSegment(sketch, "E31.7.24.0", {"start": v(-159, -102) * mm, "end": v(-149, -102) * mm});
            skLineSegment(sketch, "E31.7.24.1", {"start": v(-159, -112) * mm, "end": v(-149, -112) * mm});
            skLineSegment(sketch, "E31.7.24.2", {"start": v(-159, -102) * mm, "end": v(-159, -112) * mm});
            skLineSegment(sketch, "E31.7.24.3", {"start": v(-149, -102) * mm, "end": v(-149, -112) * mm});
            skLineSegment(sketch, "E31.7.25.0", {"start": v(-159, -88) * mm, "end": v(-149, -88) * mm});
            skLineSegment(sketch, "E31.7.25.1", {"start": v(-159, -98) * mm, "end": v(-149, -98) * mm});
            skLineSegment(sketch, "E31.7.25.2", {"start": v(-159, -88) * mm, "end": v(-159, -98) * mm});
            skLineSegment(sketch, "E31.7.25.3", {"start": v(-149, -88) * mm, "end": v(-149, -98) * mm});
            skLineSegment(sketch, "E31.7.26.0", {"start": v(-159, -74) * mm, "end": v(-149, -74) * mm});
            skLineSegment(sketch, "E31.7.26.1", {"start": v(-159, -84) * mm, "end": v(-149, -84) * mm});
            skLineSegment(sketch, "E31.7.26.2", {"start": v(-159, -74) * mm, "end": v(-159, -84) * mm});
            skLineSegment(sketch, "E31.7.26.3", {"start": v(-149, -74) * mm, "end": v(-149, -84) * mm});
            skLineSegment(sketch, "E31.7.27.0", {"start": v(-159, -60) * mm, "end": v(-149, -60) * mm});
            skLineSegment(sketch, "E31.7.27.1", {"start": v(-159, -70) * mm, "end": v(-149, -70) * mm});
            skLineSegment(sketch, "E31.7.27.2", {"start": v(-159, -60) * mm, "end": v(-159, -70) * mm});
            skLineSegment(sketch, "E31.7.27.3", {"start": v(-149, -60) * mm, "end": v(-149, -70) * mm});
            skLineSegment(sketch, "E31.7.28.0", {"start": v(-159, -46) * mm, "end": v(-149, -46) * mm});
            skLineSegment(sketch, "E31.7.28.1", {"start": v(-159, -56) * mm, "end": v(-149, -56) * mm});
            skLineSegment(sketch, "E31.7.28.2", {"start": v(-159, -46) * mm, "end": v(-159, -56) * mm});
            skLineSegment(sketch, "E31.7.28.3", {"start": v(-149, -46) * mm, "end": v(-149, -56) * mm});
            skLineSegment(sketch, "E31.7.29.0", {"start": v(-159, -32) * mm, "end": v(-149, -32) * mm});
            skLineSegment(sketch, "E31.7.29.1", {"start": v(-159, -42) * mm, "end": v(-149, -42) * mm});
            skLineSegment(sketch, "E31.7.29.2", {"start": v(-159, -32) * mm, "end": v(-159, -42) * mm});
            skLineSegment(sketch, "E31.7.29.3", {"start": v(-149, -32) * mm, "end": v(-149, -42) * mm});
            skLineSegment(sketch, "E31.7.30.0", {"start": v(-159, -18) * mm, "end": v(-149, -18) * mm});
            skLineSegment(sketch, "E31.7.30.1", {"start": v(-159, -28) * mm, "end": v(-149, -28) * mm});
            skLineSegment(sketch, "E31.7.30.2", {"start": v(-159, -18) * mm, "end": v(-159, -28) * mm});
            skLineSegment(sketch, "E31.7.30.3", {"start": v(-149, -18) * mm, "end": v(-149, -28) * mm});
            skLineSegment(sketch, "E31.7.31.0", {"start": v(-159, -4) * mm, "end": v(-149, -4) * mm});
            skLineSegment(sketch, "E31.7.31.1", {"start": v(-159, -14) * mm, "end": v(-149, -14) * mm});
            skLineSegment(sketch, "E31.7.31.2", {"start": v(-159, -4) * mm, "end": v(-159, -14) * mm});
            skLineSegment(sketch, "E31.7.31.3", {"start": v(-149, -4) * mm, "end": v(-149, -14) * mm});
            skLineSegment(sketch, "E31.8.0.0", {"start": v(-145, -438) * mm, "end": v(-135, -438) * mm});
            skLineSegment(sketch, "E31.8.0.1", {"start": v(-145, -448) * mm, "end": v(-135, -448) * mm});
            skLineSegment(sketch, "E31.8.0.2", {"start": v(-145, -438) * mm, "end": v(-145, -448) * mm});
            skLineSegment(sketch, "E31.8.0.3", {"start": v(-135, -438) * mm, "end": v(-135, -448) * mm});
            skLineSegment(sketch, "E31.8.1.0", {"start": v(-145, -424) * mm, "end": v(-135, -424) * mm});
            skLineSegment(sketch, "E31.8.1.1", {"start": v(-145, -434) * mm, "end": v(-135, -434) * mm});
            skLineSegment(sketch, "E31.8.1.2", {"start": v(-145, -424) * mm, "end": v(-145, -434) * mm});
            skLineSegment(sketch, "E31.8.1.3", {"start": v(-135, -424) * mm, "end": v(-135, -434) * mm});
            skLineSegment(sketch, "E31.8.2.0", {"start": v(-145, -410) * mm, "end": v(-135, -410) * mm});
            skLineSegment(sketch, "E31.8.2.1", {"start": v(-145, -420) * mm, "end": v(-135, -420) * mm});
            skLineSegment(sketch, "E31.8.2.2", {"start": v(-145, -410) * mm, "end": v(-145, -420) * mm});
            skLineSegment(sketch, "E31.8.2.3", {"start": v(-135, -410) * mm, "end": v(-135, -420) * mm});
            skLineSegment(sketch, "E31.8.3.0", {"start": v(-145, -396) * mm, "end": v(-135, -396) * mm});
            skLineSegment(sketch, "E31.8.3.1", {"start": v(-145, -406) * mm, "end": v(-135, -406) * mm});
            skLineSegment(sketch, "E31.8.3.2", {"start": v(-145, -396) * mm, "end": v(-145, -406) * mm});
            skLineSegment(sketch, "E31.8.3.3", {"start": v(-135, -396) * mm, "end": v(-135, -406) * mm});
            skLineSegment(sketch, "E31.8.4.0", {"start": v(-145, -382) * mm, "end": v(-135, -382) * mm});
            skLineSegment(sketch, "E31.8.4.1", {"start": v(-145, -392) * mm, "end": v(-135, -392) * mm});
            skLineSegment(sketch, "E31.8.4.2", {"start": v(-145, -382) * mm, "end": v(-145, -392) * mm});
            skLineSegment(sketch, "E31.8.4.3", {"start": v(-135, -382) * mm, "end": v(-135, -392) * mm});
            skLineSegment(sketch, "E31.8.5.0", {"start": v(-145, -368) * mm, "end": v(-135, -368) * mm});
            skLineSegment(sketch, "E31.8.5.1", {"start": v(-145, -378) * mm, "end": v(-135, -378) * mm});
            skLineSegment(sketch, "E31.8.5.2", {"start": v(-145, -368) * mm, "end": v(-145, -378) * mm});
            skLineSegment(sketch, "E31.8.5.3", {"start": v(-135, -368) * mm, "end": v(-135, -378) * mm});
            skLineSegment(sketch, "E31.8.6.0", {"start": v(-145, -354) * mm, "end": v(-135, -354) * mm});
            skLineSegment(sketch, "E31.8.6.1", {"start": v(-145, -364) * mm, "end": v(-135, -364) * mm});
            skLineSegment(sketch, "E31.8.6.2", {"start": v(-145, -354) * mm, "end": v(-145, -364) * mm});
            skLineSegment(sketch, "E31.8.6.3", {"start": v(-135, -354) * mm, "end": v(-135, -364) * mm});
            skLineSegment(sketch, "E31.8.7.0", {"start": v(-145, -340) * mm, "end": v(-135, -340) * mm});
            skLineSegment(sketch, "E31.8.7.1", {"start": v(-145, -350) * mm, "end": v(-135, -350) * mm});
            skLineSegment(sketch, "E31.8.7.2", {"start": v(-145, -340) * mm, "end": v(-145, -350) * mm});
            skLineSegment(sketch, "E31.8.7.3", {"start": v(-135, -340) * mm, "end": v(-135, -350) * mm});
            skLineSegment(sketch, "E31.8.8.0", {"start": v(-145, -326) * mm, "end": v(-135, -326) * mm});
            skLineSegment(sketch, "E31.8.8.1", {"start": v(-145, -336) * mm, "end": v(-135, -336) * mm});
            skLineSegment(sketch, "E31.8.8.2", {"start": v(-145, -326) * mm, "end": v(-145, -336) * mm});
            skLineSegment(sketch, "E31.8.8.3", {"start": v(-135, -326) * mm, "end": v(-135, -336) * mm});
            skLineSegment(sketch, "E31.8.9.0", {"start": v(-145, -312) * mm, "end": v(-135, -312) * mm});
            skLineSegment(sketch, "E31.8.9.1", {"start": v(-145, -322) * mm, "end": v(-135, -322) * mm});
            skLineSegment(sketch, "E31.8.9.2", {"start": v(-145, -312) * mm, "end": v(-145, -322) * mm});
            skLineSegment(sketch, "E31.8.9.3", {"start": v(-135, -312) * mm, "end": v(-135, -322) * mm});
            skLineSegment(sketch, "E31.8.10.0", {"start": v(-145, -298) * mm, "end": v(-135, -298) * mm});
            skLineSegment(sketch, "E31.8.10.1", {"start": v(-145, -308) * mm, "end": v(-135, -308) * mm});
            skLineSegment(sketch, "E31.8.10.2", {"start": v(-145, -298) * mm, "end": v(-145, -308) * mm});
            skLineSegment(sketch, "E31.8.10.3", {"start": v(-135, -298) * mm, "end": v(-135, -308) * mm});
            skLineSegment(sketch, "E31.8.11.0", {"start": v(-145, -284) * mm, "end": v(-135, -284) * mm});
            skLineSegment(sketch, "E31.8.11.1", {"start": v(-145, -294) * mm, "end": v(-135, -294) * mm});
            skLineSegment(sketch, "E31.8.11.2", {"start": v(-145, -284) * mm, "end": v(-145, -294) * mm});
            skLineSegment(sketch, "E31.8.11.3", {"start": v(-135, -284) * mm, "end": v(-135, -294) * mm});
            skLineSegment(sketch, "E31.8.12.0", {"start": v(-145, -270) * mm, "end": v(-135, -270) * mm});
            skLineSegment(sketch, "E31.8.12.1", {"start": v(-145, -280) * mm, "end": v(-135, -280) * mm});
            skLineSegment(sketch, "E31.8.12.2", {"start": v(-145, -270) * mm, "end": v(-145, -280) * mm});
            skLineSegment(sketch, "E31.8.12.3", {"start": v(-135, -270) * mm, "end": v(-135, -280) * mm});
            skLineSegment(sketch, "E31.8.13.0", {"start": v(-145, -256) * mm, "end": v(-135, -256) * mm});
            skLineSegment(sketch, "E31.8.13.1", {"start": v(-145, -266) * mm, "end": v(-135, -266) * mm});
            skLineSegment(sketch, "E31.8.13.2", {"start": v(-145, -256) * mm, "end": v(-145, -266) * mm});
            skLineSegment(sketch, "E31.8.13.3", {"start": v(-135, -256) * mm, "end": v(-135, -266) * mm});
            skLineSegment(sketch, "E31.8.14.0", {"start": v(-145, -242) * mm, "end": v(-135, -242) * mm});
            skLineSegment(sketch, "E31.8.14.1", {"start": v(-145, -252) * mm, "end": v(-135, -252) * mm});
            skLineSegment(sketch, "E31.8.14.2", {"start": v(-145, -242) * mm, "end": v(-145, -252) * mm});
            skLineSegment(sketch, "E31.8.14.3", {"start": v(-135, -242) * mm, "end": v(-135, -252) * mm});
            skLineSegment(sketch, "E31.8.15.0", {"start": v(-145, -228) * mm, "end": v(-135, -228) * mm});
            skLineSegment(sketch, "E31.8.15.1", {"start": v(-145, -238) * mm, "end": v(-135, -238) * mm});
            skLineSegment(sketch, "E31.8.15.2", {"start": v(-145, -228) * mm, "end": v(-145, -238) * mm});
            skLineSegment(sketch, "E31.8.15.3", {"start": v(-135, -228) * mm, "end": v(-135, -238) * mm});
            skLineSegment(sketch, "E31.8.16.0", {"start": v(-145, -214) * mm, "end": v(-135, -214) * mm});
            skLineSegment(sketch, "E31.8.16.1", {"start": v(-145, -224) * mm, "end": v(-135, -224) * mm});
            skLineSegment(sketch, "E31.8.16.2", {"start": v(-145, -214) * mm, "end": v(-145, -224) * mm});
            skLineSegment(sketch, "E31.8.16.3", {"start": v(-135, -214) * mm, "end": v(-135, -224) * mm});
            skLineSegment(sketch, "E31.8.17.0", {"start": v(-145, -200) * mm, "end": v(-135, -200) * mm});
            skLineSegment(sketch, "E31.8.17.1", {"start": v(-145, -210) * mm, "end": v(-135, -210) * mm});
            skLineSegment(sketch, "E31.8.17.2", {"start": v(-145, -200) * mm, "end": v(-145, -210) * mm});
            skLineSegment(sketch, "E31.8.17.3", {"start": v(-135, -200) * mm, "end": v(-135, -210) * mm});
            skLineSegment(sketch, "E31.8.18.0", {"start": v(-145, -186) * mm, "end": v(-135, -186) * mm});
            skLineSegment(sketch, "E31.8.18.1", {"start": v(-145, -196) * mm, "end": v(-135, -196) * mm});
            skLineSegment(sketch, "E31.8.18.2", {"start": v(-145, -186) * mm, "end": v(-145, -196) * mm});
            skLineSegment(sketch, "E31.8.18.3", {"start": v(-135, -186) * mm, "end": v(-135, -196) * mm});
            skLineSegment(sketch, "E31.8.19.0", {"start": v(-145, -172) * mm, "end": v(-135, -172) * mm});
            skLineSegment(sketch, "E31.8.19.1", {"start": v(-145, -182) * mm, "end": v(-135, -182) * mm});
            skLineSegment(sketch, "E31.8.19.2", {"start": v(-145, -172) * mm, "end": v(-145, -182) * mm});
            skLineSegment(sketch, "E31.8.19.3", {"start": v(-135, -172) * mm, "end": v(-135, -182) * mm});
            skLineSegment(sketch, "E31.8.20.0", {"start": v(-145, -158) * mm, "end": v(-135, -158) * mm});
            skLineSegment(sketch, "E31.8.20.1", {"start": v(-145, -168) * mm, "end": v(-135, -168) * mm});
            skLineSegment(sketch, "E31.8.20.2", {"start": v(-145, -158) * mm, "end": v(-145, -168) * mm});
            skLineSegment(sketch, "E31.8.20.3", {"start": v(-135, -158) * mm, "end": v(-135, -168) * mm});
            skLineSegment(sketch, "E31.8.21.0", {"start": v(-145, -144) * mm, "end": v(-135, -144) * mm});
            skLineSegment(sketch, "E31.8.21.1", {"start": v(-145, -154) * mm, "end": v(-135, -154) * mm});
            skLineSegment(sketch, "E31.8.21.2", {"start": v(-145, -144) * mm, "end": v(-145, -154) * mm});
            skLineSegment(sketch, "E31.8.21.3", {"start": v(-135, -144) * mm, "end": v(-135, -154) * mm});
            skLineSegment(sketch, "E31.8.22.0", {"start": v(-145, -130) * mm, "end": v(-135, -130) * mm});
            skLineSegment(sketch, "E31.8.22.1", {"start": v(-145, -140) * mm, "end": v(-135, -140) * mm});
            skLineSegment(sketch, "E31.8.22.2", {"start": v(-145, -130) * mm, "end": v(-145, -140) * mm});
            skLineSegment(sketch, "E31.8.22.3", {"start": v(-135, -130) * mm, "end": v(-135, -140) * mm});
            skLineSegment(sketch, "E31.8.23.0", {"start": v(-145, -116) * mm, "end": v(-135, -116) * mm});
            skLineSegment(sketch, "E31.8.23.1", {"start": v(-145, -126) * mm, "end": v(-135, -126) * mm});
            skLineSegment(sketch, "E31.8.23.2", {"start": v(-145, -116) * mm, "end": v(-145, -126) * mm});
            skLineSegment(sketch, "E31.8.23.3", {"start": v(-135, -116) * mm, "end": v(-135, -126) * mm});
            skLineSegment(sketch, "E31.8.24.0", {"start": v(-145, -102) * mm, "end": v(-135, -102) * mm});
            skLineSegment(sketch, "E31.8.24.1", {"start": v(-145, -112) * mm, "end": v(-135, -112) * mm});
            skLineSegment(sketch, "E31.8.24.2", {"start": v(-145, -102) * mm, "end": v(-145, -112) * mm});
            skLineSegment(sketch, "E31.8.24.3", {"start": v(-135, -102) * mm, "end": v(-135, -112) * mm});
            skLineSegment(sketch, "E31.8.25.0", {"start": v(-145, -88) * mm, "end": v(-135, -88) * mm});
            skLineSegment(sketch, "E31.8.25.1", {"start": v(-145, -98) * mm, "end": v(-135, -98) * mm});
            skLineSegment(sketch, "E31.8.25.2", {"start": v(-145, -88) * mm, "end": v(-145, -98) * mm});
            skLineSegment(sketch, "E31.8.25.3", {"start": v(-135, -88) * mm, "end": v(-135, -98) * mm});
            skLineSegment(sketch, "E31.8.26.0", {"start": v(-145, -74) * mm, "end": v(-135, -74) * mm});
            skLineSegment(sketch, "E31.8.26.1", {"start": v(-145, -84) * mm, "end": v(-135, -84) * mm});
            skLineSegment(sketch, "E31.8.26.2", {"start": v(-145, -74) * mm, "end": v(-145, -84) * mm});
            skLineSegment(sketch, "E31.8.26.3", {"start": v(-135, -74) * mm, "end": v(-135, -84) * mm});
            skLineSegment(sketch, "E31.8.27.0", {"start": v(-145, -60) * mm, "end": v(-135, -60) * mm});
            skLineSegment(sketch, "E31.8.27.1", {"start": v(-145, -70) * mm, "end": v(-135, -70) * mm});
            skLineSegment(sketch, "E31.8.27.2", {"start": v(-145, -60) * mm, "end": v(-145, -70) * mm});
            skLineSegment(sketch, "E31.8.27.3", {"start": v(-135, -60) * mm, "end": v(-135, -70) * mm});
            skLineSegment(sketch, "E31.8.28.0", {"start": v(-145, -46) * mm, "end": v(-135, -46) * mm});
            skLineSegment(sketch, "E31.8.28.1", {"start": v(-145, -56) * mm, "end": v(-135, -56) * mm});
            skLineSegment(sketch, "E31.8.28.2", {"start": v(-145, -46) * mm, "end": v(-145, -56) * mm});
            skLineSegment(sketch, "E31.8.28.3", {"start": v(-135, -46) * mm, "end": v(-135, -56) * mm});
            skLineSegment(sketch, "E31.8.29.0", {"start": v(-145, -32) * mm, "end": v(-135, -32) * mm});
            skLineSegment(sketch, "E31.8.29.1", {"start": v(-145, -42) * mm, "end": v(-135, -42) * mm});
            skLineSegment(sketch, "E31.8.29.2", {"start": v(-145, -32) * mm, "end": v(-145, -42) * mm});
            skLineSegment(sketch, "E31.8.29.3", {"start": v(-135, -32) * mm, "end": v(-135, -42) * mm});
            skLineSegment(sketch, "E31.8.30.0", {"start": v(-145, -18) * mm, "end": v(-135, -18) * mm});
            skLineSegment(sketch, "E31.8.30.1", {"start": v(-145, -28) * mm, "end": v(-135, -28) * mm});
            skLineSegment(sketch, "E31.8.30.2", {"start": v(-145, -18) * mm, "end": v(-145, -28) * mm});
            skLineSegment(sketch, "E31.8.30.3", {"start": v(-135, -18) * mm, "end": v(-135, -28) * mm});
            skLineSegment(sketch, "E31.8.31.0", {"start": v(-145, -4) * mm, "end": v(-135, -4) * mm});
            skLineSegment(sketch, "E31.8.31.1", {"start": v(-145, -14) * mm, "end": v(-135, -14) * mm});
            skLineSegment(sketch, "E31.8.31.2", {"start": v(-145, -4) * mm, "end": v(-145, -14) * mm});
            skLineSegment(sketch, "E31.8.31.3", {"start": v(-135, -4) * mm, "end": v(-135, -14) * mm});
            skLineSegment(sketch, "E31.9.0.0", {"start": v(-131, -438) * mm, "end": v(-121, -438) * mm});
            skLineSegment(sketch, "E31.9.0.1", {"start": v(-131, -448) * mm, "end": v(-121, -448) * mm});
            skLineSegment(sketch, "E31.9.0.2", {"start": v(-131, -438) * mm, "end": v(-131, -448) * mm});
            skLineSegment(sketch, "E31.9.0.3", {"start": v(-121, -438) * mm, "end": v(-121, -448) * mm});
            skLineSegment(sketch, "E31.9.1.0", {"start": v(-131, -424) * mm, "end": v(-121, -424) * mm});
            skLineSegment(sketch, "E31.9.1.1", {"start": v(-131, -434) * mm, "end": v(-121, -434) * mm});
            skLineSegment(sketch, "E31.9.1.2", {"start": v(-131, -424) * mm, "end": v(-131, -434) * mm});
            skLineSegment(sketch, "E31.9.1.3", {"start": v(-121, -424) * mm, "end": v(-121, -434) * mm});
            skLineSegment(sketch, "E31.9.2.0", {"start": v(-131, -410) * mm, "end": v(-121, -410) * mm});
            skLineSegment(sketch, "E31.9.2.1", {"start": v(-131, -420) * mm, "end": v(-121, -420) * mm});
            skLineSegment(sketch, "E31.9.2.2", {"start": v(-131, -410) * mm, "end": v(-131, -420) * mm});
            skLineSegment(sketch, "E31.9.2.3", {"start": v(-121, -410) * mm, "end": v(-121, -420) * mm});
            skLineSegment(sketch, "E31.9.3.0", {"start": v(-131, -396) * mm, "end": v(-121, -396) * mm});
            skLineSegment(sketch, "E31.9.3.1", {"start": v(-131, -406) * mm, "end": v(-121, -406) * mm});
            skLineSegment(sketch, "E31.9.3.2", {"start": v(-131, -396) * mm, "end": v(-131, -406) * mm});
            skLineSegment(sketch, "E31.9.3.3", {"start": v(-121, -396) * mm, "end": v(-121, -406) * mm});
            skLineSegment(sketch, "E31.9.4.0", {"start": v(-131, -382) * mm, "end": v(-121, -382) * mm});
            skLineSegment(sketch, "E31.9.4.1", {"start": v(-131, -392) * mm, "end": v(-121, -392) * mm});
            skLineSegment(sketch, "E31.9.4.2", {"start": v(-131, -382) * mm, "end": v(-131, -392) * mm});
            skLineSegment(sketch, "E31.9.4.3", {"start": v(-121, -382) * mm, "end": v(-121, -392) * mm});
            skLineSegment(sketch, "E31.9.5.0", {"start": v(-131, -368) * mm, "end": v(-121, -368) * mm});
            skLineSegment(sketch, "E31.9.5.1", {"start": v(-131, -378) * mm, "end": v(-121, -378) * mm});
            skLineSegment(sketch, "E31.9.5.2", {"start": v(-131, -368) * mm, "end": v(-131, -378) * mm});
            skLineSegment(sketch, "E31.9.5.3", {"start": v(-121, -368) * mm, "end": v(-121, -378) * mm});
            skLineSegment(sketch, "E31.9.6.0", {"start": v(-131, -354) * mm, "end": v(-121, -354) * mm});
            skLineSegment(sketch, "E31.9.6.1", {"start": v(-131, -364) * mm, "end": v(-121, -364) * mm});
            skLineSegment(sketch, "E31.9.6.2", {"start": v(-131, -354) * mm, "end": v(-131, -364) * mm});
            skLineSegment(sketch, "E31.9.6.3", {"start": v(-121, -354) * mm, "end": v(-121, -364) * mm});
            skLineSegment(sketch, "E31.9.7.0", {"start": v(-131, -340) * mm, "end": v(-121, -340) * mm});
            skLineSegment(sketch, "E31.9.7.1", {"start": v(-131, -350) * mm, "end": v(-121, -350) * mm});
            skLineSegment(sketch, "E31.9.7.2", {"start": v(-131, -340) * mm, "end": v(-131, -350) * mm});
            skLineSegment(sketch, "E31.9.7.3", {"start": v(-121, -340) * mm, "end": v(-121, -350) * mm});
            skLineSegment(sketch, "E31.9.8.0", {"start": v(-131, -326) * mm, "end": v(-121, -326) * mm});
            skLineSegment(sketch, "E31.9.8.1", {"start": v(-131, -336) * mm, "end": v(-121, -336) * mm});
            skLineSegment(sketch, "E31.9.8.2", {"start": v(-131, -326) * mm, "end": v(-131, -336) * mm});
            skLineSegment(sketch, "E31.9.8.3", {"start": v(-121, -326) * mm, "end": v(-121, -336) * mm});
            skLineSegment(sketch, "E31.9.9.0", {"start": v(-131, -312) * mm, "end": v(-121, -312) * mm});
            skLineSegment(sketch, "E31.9.9.1", {"start": v(-131, -322) * mm, "end": v(-121, -322) * mm});
            skLineSegment(sketch, "E31.9.9.2", {"start": v(-131, -312) * mm, "end": v(-131, -322) * mm});
            skLineSegment(sketch, "E31.9.9.3", {"start": v(-121, -312) * mm, "end": v(-121, -322) * mm});
            skLineSegment(sketch, "E31.9.10.0", {"start": v(-131, -298) * mm, "end": v(-121, -298) * mm});
            skLineSegment(sketch, "E31.9.10.1", {"start": v(-131, -308) * mm, "end": v(-121, -308) * mm});
            skLineSegment(sketch, "E31.9.10.2", {"start": v(-131, -298) * mm, "end": v(-131, -308) * mm});
            skLineSegment(sketch, "E31.9.10.3", {"start": v(-121, -298) * mm, "end": v(-121, -308) * mm});
            skLineSegment(sketch, "E31.9.11.0", {"start": v(-131, -284) * mm, "end": v(-121, -284) * mm});
            skLineSegment(sketch, "E31.9.11.1", {"start": v(-131, -294) * mm, "end": v(-121, -294) * mm});
            skLineSegment(sketch, "E31.9.11.2", {"start": v(-131, -284) * mm, "end": v(-131, -294) * mm});
            skLineSegment(sketch, "E31.9.11.3", {"start": v(-121, -284) * mm, "end": v(-121, -294) * mm});
            skLineSegment(sketch, "E31.9.12.0", {"start": v(-131, -270) * mm, "end": v(-121, -270) * mm});
            skLineSegment(sketch, "E31.9.12.1", {"start": v(-131, -280) * mm, "end": v(-121, -280) * mm});
            skLineSegment(sketch, "E31.9.12.2", {"start": v(-131, -270) * mm, "end": v(-131, -280) * mm});
            skLineSegment(sketch, "E31.9.12.3", {"start": v(-121, -270) * mm, "end": v(-121, -280) * mm});
            skLineSegment(sketch, "E31.9.13.0", {"start": v(-131, -256) * mm, "end": v(-121, -256) * mm});
            skLineSegment(sketch, "E31.9.13.1", {"start": v(-131, -266) * mm, "end": v(-121, -266) * mm});
            skLineSegment(sketch, "E31.9.13.2", {"start": v(-131, -256) * mm, "end": v(-131, -266) * mm});
            skLineSegment(sketch, "E31.9.13.3", {"start": v(-121, -256) * mm, "end": v(-121, -266) * mm});
            skLineSegment(sketch, "E31.9.14.0", {"start": v(-131, -242) * mm, "end": v(-121, -242) * mm});
            skLineSegment(sketch, "E31.9.14.1", {"start": v(-131, -252) * mm, "end": v(-121, -252) * mm});
            skLineSegment(sketch, "E31.9.14.2", {"start": v(-131, -242) * mm, "end": v(-131, -252) * mm});
            skLineSegment(sketch, "E31.9.14.3", {"start": v(-121, -242) * mm, "end": v(-121, -252) * mm});
            skLineSegment(sketch, "E31.9.15.0", {"start": v(-131, -228) * mm, "end": v(-121, -228) * mm});
            skLineSegment(sketch, "E31.9.15.1", {"start": v(-131, -238) * mm, "end": v(-121, -238) * mm});
            skLineSegment(sketch, "E31.9.15.2", {"start": v(-131, -228) * mm, "end": v(-131, -238) * mm});
            skLineSegment(sketch, "E31.9.15.3", {"start": v(-121, -228) * mm, "end": v(-121, -238) * mm});
            skLineSegment(sketch, "E31.9.16.0", {"start": v(-131, -214) * mm, "end": v(-121, -214) * mm});
            skLineSegment(sketch, "E31.9.16.1", {"start": v(-131, -224) * mm, "end": v(-121, -224) * mm});
            skLineSegment(sketch, "E31.9.16.2", {"start": v(-131, -214) * mm, "end": v(-131, -224) * mm});
            skLineSegment(sketch, "E31.9.16.3", {"start": v(-121, -214) * mm, "end": v(-121, -224) * mm});
            skLineSegment(sketch, "E31.9.17.0", {"start": v(-131, -200) * mm, "end": v(-121, -200) * mm});
            skLineSegment(sketch, "E31.9.17.1", {"start": v(-131, -210) * mm, "end": v(-121, -210) * mm});
            skLineSegment(sketch, "E31.9.17.2", {"start": v(-131, -200) * mm, "end": v(-131, -210) * mm});
            skLineSegment(sketch, "E31.9.17.3", {"start": v(-121, -200) * mm, "end": v(-121, -210) * mm});
            skLineSegment(sketch, "E31.9.18.0", {"start": v(-131, -186) * mm, "end": v(-121, -186) * mm});
            skLineSegment(sketch, "E31.9.18.1", {"start": v(-131, -196) * mm, "end": v(-121, -196) * mm});
            skLineSegment(sketch, "E31.9.18.2", {"start": v(-131, -186) * mm, "end": v(-131, -196) * mm});
            skLineSegment(sketch, "E31.9.18.3", {"start": v(-121, -186) * mm, "end": v(-121, -196) * mm});
            skLineSegment(sketch, "E31.9.19.0", {"start": v(-131, -172) * mm, "end": v(-121, -172) * mm});
            skLineSegment(sketch, "E31.9.19.1", {"start": v(-131, -182) * mm, "end": v(-121, -182) * mm});
            skLineSegment(sketch, "E31.9.19.2", {"start": v(-131, -172) * mm, "end": v(-131, -182) * mm});
            skLineSegment(sketch, "E31.9.19.3", {"start": v(-121, -172) * mm, "end": v(-121, -182) * mm});
            skLineSegment(sketch, "E31.9.20.0", {"start": v(-131, -158) * mm, "end": v(-121, -158) * mm});
            skLineSegment(sketch, "E31.9.20.1", {"start": v(-131, -168) * mm, "end": v(-121, -168) * mm});
            skLineSegment(sketch, "E31.9.20.2", {"start": v(-131, -158) * mm, "end": v(-131, -168) * mm});
            skLineSegment(sketch, "E31.9.20.3", {"start": v(-121, -158) * mm, "end": v(-121, -168) * mm});
            skLineSegment(sketch, "E31.9.21.0", {"start": v(-131, -144) * mm, "end": v(-121, -144) * mm});
            skLineSegment(sketch, "E31.9.21.1", {"start": v(-131, -154) * mm, "end": v(-121, -154) * mm});
            skLineSegment(sketch, "E31.9.21.2", {"start": v(-131, -144) * mm, "end": v(-131, -154) * mm});
            skLineSegment(sketch, "E31.9.21.3", {"start": v(-121, -144) * mm, "end": v(-121, -154) * mm});
            skLineSegment(sketch, "E31.9.22.0", {"start": v(-131, -130) * mm, "end": v(-121, -130) * mm});
            skLineSegment(sketch, "E31.9.22.1", {"start": v(-131, -140) * mm, "end": v(-121, -140) * mm});
            skLineSegment(sketch, "E31.9.22.2", {"start": v(-131, -130) * mm, "end": v(-131, -140) * mm});
            skLineSegment(sketch, "E31.9.22.3", {"start": v(-121, -130) * mm, "end": v(-121, -140) * mm});
            skLineSegment(sketch, "E31.9.23.0", {"start": v(-131, -116) * mm, "end": v(-121, -116) * mm});
            skLineSegment(sketch, "E31.9.23.1", {"start": v(-131, -126) * mm, "end": v(-121, -126) * mm});
            skLineSegment(sketch, "E31.9.23.2", {"start": v(-131, -116) * mm, "end": v(-131, -126) * mm});
            skLineSegment(sketch, "E31.9.23.3", {"start": v(-121, -116) * mm, "end": v(-121, -126) * mm});
            skLineSegment(sketch, "E31.9.24.0", {"start": v(-131, -102) * mm, "end": v(-121, -102) * mm});
            skLineSegment(sketch, "E31.9.24.1", {"start": v(-131, -112) * mm, "end": v(-121, -112) * mm});
            skLineSegment(sketch, "E31.9.24.2", {"start": v(-131, -102) * mm, "end": v(-131, -112) * mm});
            skLineSegment(sketch, "E31.9.24.3", {"start": v(-121, -102) * mm, "end": v(-121, -112) * mm});
            skLineSegment(sketch, "E31.9.25.0", {"start": v(-131, -88) * mm, "end": v(-121, -88) * mm});
            skLineSegment(sketch, "E31.9.25.1", {"start": v(-131, -98) * mm, "end": v(-121, -98) * mm});
            skLineSegment(sketch, "E31.9.25.2", {"start": v(-131, -88) * mm, "end": v(-131, -98) * mm});
            skLineSegment(sketch, "E31.9.25.3", {"start": v(-121, -88) * mm, "end": v(-121, -98) * mm});
            skLineSegment(sketch, "E31.9.26.0", {"start": v(-131, -74) * mm, "end": v(-121, -74) * mm});
            skLineSegment(sketch, "E31.9.26.1", {"start": v(-131, -84) * mm, "end": v(-121, -84) * mm});
            skLineSegment(sketch, "E31.9.26.2", {"start": v(-131, -74) * mm, "end": v(-131, -84) * mm});
            skLineSegment(sketch, "E31.9.26.3", {"start": v(-121, -74) * mm, "end": v(-121, -84) * mm});
            skLineSegment(sketch, "E31.9.27.0", {"start": v(-131, -60) * mm, "end": v(-121, -60) * mm});
            skLineSegment(sketch, "E31.9.27.1", {"start": v(-131, -70) * mm, "end": v(-121, -70) * mm});
            skLineSegment(sketch, "E31.9.27.2", {"start": v(-131, -60) * mm, "end": v(-131, -70) * mm});
            skLineSegment(sketch, "E31.9.27.3", {"start": v(-121, -60) * mm, "end": v(-121, -70) * mm});
            skLineSegment(sketch, "E31.9.28.0", {"start": v(-131, -46) * mm, "end": v(-121, -46) * mm});
            skLineSegment(sketch, "E31.9.28.1", {"start": v(-131, -56) * mm, "end": v(-121, -56) * mm});
            skLineSegment(sketch, "E31.9.28.2", {"start": v(-131, -46) * mm, "end": v(-131, -56) * mm});
            skLineSegment(sketch, "E31.9.28.3", {"start": v(-121, -46) * mm, "end": v(-121, -56) * mm});
            skLineSegment(sketch, "E31.9.29.0", {"start": v(-131, -32) * mm, "end": v(-121, -32) * mm});
            skLineSegment(sketch, "E31.9.29.1", {"start": v(-131, -42) * mm, "end": v(-121, -42) * mm});
            skLineSegment(sketch, "E31.9.29.2", {"start": v(-131, -32) * mm, "end": v(-131, -42) * mm});
            skLineSegment(sketch, "E31.9.29.3", {"start": v(-121, -32) * mm, "end": v(-121, -42) * mm});
            skLineSegment(sketch, "E31.9.30.0", {"start": v(-131, -18) * mm, "end": v(-121, -18) * mm});
            skLineSegment(sketch, "E31.9.30.1", {"start": v(-131, -28) * mm, "end": v(-121, -28) * mm});
            skLineSegment(sketch, "E31.9.30.2", {"start": v(-131, -18) * mm, "end": v(-131, -28) * mm});
            skLineSegment(sketch, "E31.9.30.3", {"start": v(-121, -18) * mm, "end": v(-121, -28) * mm});
            skLineSegment(sketch, "E31.9.31.0", {"start": v(-131, -4) * mm, "end": v(-121, -4) * mm});
            skLineSegment(sketch, "E31.9.31.1", {"start": v(-131, -14) * mm, "end": v(-121, -14) * mm});
            skLineSegment(sketch, "E31.9.31.2", {"start": v(-131, -4) * mm, "end": v(-131, -14) * mm});
            skLineSegment(sketch, "E31.9.31.3", {"start": v(-121, -4) * mm, "end": v(-121, -14) * mm});
            skLineSegment(sketch, "E31.10.0.0", {"start": v(-117, -438) * mm, "end": v(-107, -438) * mm});
            skLineSegment(sketch, "E31.10.0.1", {"start": v(-117, -448) * mm, "end": v(-107, -448) * mm});
            skLineSegment(sketch, "E31.10.0.2", {"start": v(-117, -438) * mm, "end": v(-117, -448) * mm});
            skLineSegment(sketch, "E31.10.0.3", {"start": v(-107, -438) * mm, "end": v(-107, -448) * mm});
            skLineSegment(sketch, "E31.10.1.0", {"start": v(-117, -424) * mm, "end": v(-107, -424) * mm});
            skLineSegment(sketch, "E31.10.1.1", {"start": v(-117, -434) * mm, "end": v(-107, -434) * mm});
            skLineSegment(sketch, "E31.10.1.2", {"start": v(-117, -424) * mm, "end": v(-117, -434) * mm});
            skLineSegment(sketch, "E31.10.1.3", {"start": v(-107, -424) * mm, "end": v(-107, -434) * mm});
            skLineSegment(sketch, "E31.10.2.0", {"start": v(-117, -410) * mm, "end": v(-107, -410) * mm});
            skLineSegment(sketch, "E31.10.2.1", {"start": v(-117, -420) * mm, "end": v(-107, -420) * mm});
            skLineSegment(sketch, "E31.10.2.2", {"start": v(-117, -410) * mm, "end": v(-117, -420) * mm});
            skLineSegment(sketch, "E31.10.2.3", {"start": v(-107, -410) * mm, "end": v(-107, -420) * mm});
            skLineSegment(sketch, "E31.10.3.0", {"start": v(-117, -396) * mm, "end": v(-107, -396) * mm});
            skLineSegment(sketch, "E31.10.3.1", {"start": v(-117, -406) * mm, "end": v(-107, -406) * mm});
            skLineSegment(sketch, "E31.10.3.2", {"start": v(-117, -396) * mm, "end": v(-117, -406) * mm});
            skLineSegment(sketch, "E31.10.3.3", {"start": v(-107, -396) * mm, "end": v(-107, -406) * mm});
            skLineSegment(sketch, "E31.10.4.0", {"start": v(-117, -382) * mm, "end": v(-107, -382) * mm});
            skLineSegment(sketch, "E31.10.4.1", {"start": v(-117, -392) * mm, "end": v(-107, -392) * mm});
            skLineSegment(sketch, "E31.10.4.2", {"start": v(-117, -382) * mm, "end": v(-117, -392) * mm});
            skLineSegment(sketch, "E31.10.4.3", {"start": v(-107, -382) * mm, "end": v(-107, -392) * mm});
            skLineSegment(sketch, "E31.10.5.0", {"start": v(-117, -368) * mm, "end": v(-107, -368) * mm});
            skLineSegment(sketch, "E31.10.5.1", {"start": v(-117, -378) * mm, "end": v(-107, -378) * mm});
            skLineSegment(sketch, "E31.10.5.2", {"start": v(-117, -368) * mm, "end": v(-117, -378) * mm});
            skLineSegment(sketch, "E31.10.5.3", {"start": v(-107, -368) * mm, "end": v(-107, -378) * mm});
            skLineSegment(sketch, "E31.10.6.0", {"start": v(-117, -354) * mm, "end": v(-107, -354) * mm});
            skLineSegment(sketch, "E31.10.6.1", {"start": v(-117, -364) * mm, "end": v(-107, -364) * mm});
            skLineSegment(sketch, "E31.10.6.2", {"start": v(-117, -354) * mm, "end": v(-117, -364) * mm});
            skLineSegment(sketch, "E31.10.6.3", {"start": v(-107, -354) * mm, "end": v(-107, -364) * mm});
            skLineSegment(sketch, "E31.10.7.0", {"start": v(-117, -340) * mm, "end": v(-107, -340) * mm});
            skLineSegment(sketch, "E31.10.7.1", {"start": v(-117, -350) * mm, "end": v(-107, -350) * mm});
            skLineSegment(sketch, "E31.10.7.2", {"start": v(-117, -340) * mm, "end": v(-117, -350) * mm});
            skLineSegment(sketch, "E31.10.7.3", {"start": v(-107, -340) * mm, "end": v(-107, -350) * mm});
            skLineSegment(sketch, "E31.10.8.0", {"start": v(-117, -326) * mm, "end": v(-107, -326) * mm});
            skLineSegment(sketch, "E31.10.8.1", {"start": v(-117, -336) * mm, "end": v(-107, -336) * mm});
            skLineSegment(sketch, "E31.10.8.2", {"start": v(-117, -326) * mm, "end": v(-117, -336) * mm});
            skLineSegment(sketch, "E31.10.8.3", {"start": v(-107, -326) * mm, "end": v(-107, -336) * mm});
            skLineSegment(sketch, "E31.10.9.0", {"start": v(-117, -312) * mm, "end": v(-107, -312) * mm});
            skLineSegment(sketch, "E31.10.9.1", {"start": v(-117, -322) * mm, "end": v(-107, -322) * mm});
            skLineSegment(sketch, "E31.10.9.2", {"start": v(-117, -312) * mm, "end": v(-117, -322) * mm});
            skLineSegment(sketch, "E31.10.9.3", {"start": v(-107, -312) * mm, "end": v(-107, -322) * mm});
            skLineSegment(sketch, "E31.10.10.0", {"start": v(-117, -298) * mm, "end": v(-107, -298) * mm});
            skLineSegment(sketch, "E31.10.10.1", {"start": v(-117, -308) * mm, "end": v(-107, -308) * mm});
            skLineSegment(sketch, "E31.10.10.2", {"start": v(-117, -298) * mm, "end": v(-117, -308) * mm});
            skLineSegment(sketch, "E31.10.10.3", {"start": v(-107, -298) * mm, "end": v(-107, -308) * mm});
            skLineSegment(sketch, "E31.10.11.0", {"start": v(-117, -284) * mm, "end": v(-107, -284) * mm});
            skLineSegment(sketch, "E31.10.11.1", {"start": v(-117, -294) * mm, "end": v(-107, -294) * mm});
            skLineSegment(sketch, "E31.10.11.2", {"start": v(-117, -284) * mm, "end": v(-117, -294) * mm});
            skLineSegment(sketch, "E31.10.11.3", {"start": v(-107, -284) * mm, "end": v(-107, -294) * mm});
            skLineSegment(sketch, "E31.10.12.0", {"start": v(-117, -270) * mm, "end": v(-107, -270) * mm});
            skLineSegment(sketch, "E31.10.12.1", {"start": v(-117, -280) * mm, "end": v(-107, -280) * mm});
            skLineSegment(sketch, "E31.10.12.2", {"start": v(-117, -270) * mm, "end": v(-117, -280) * mm});
            skLineSegment(sketch, "E31.10.12.3", {"start": v(-107, -270) * mm, "end": v(-107, -280) * mm});
            skLineSegment(sketch, "E31.10.13.0", {"start": v(-117, -256) * mm, "end": v(-107, -256) * mm});
            skLineSegment(sketch, "E31.10.13.1", {"start": v(-117, -266) * mm, "end": v(-107, -266) * mm});
            skLineSegment(sketch, "E31.10.13.2", {"start": v(-117, -256) * mm, "end": v(-117, -266) * mm});
            skLineSegment(sketch, "E31.10.13.3", {"start": v(-107, -256) * mm, "end": v(-107, -266) * mm});
            skLineSegment(sketch, "E31.10.14.0", {"start": v(-117, -242) * mm, "end": v(-107, -242) * mm});
            skLineSegment(sketch, "E31.10.14.1", {"start": v(-117, -252) * mm, "end": v(-107, -252) * mm});
            skLineSegment(sketch, "E31.10.14.2", {"start": v(-117, -242) * mm, "end": v(-117, -252) * mm});
            skLineSegment(sketch, "E31.10.14.3", {"start": v(-107, -242) * mm, "end": v(-107, -252) * mm});
            skLineSegment(sketch, "E31.10.15.0", {"start": v(-117, -228) * mm, "end": v(-107, -228) * mm});
            skLineSegment(sketch, "E31.10.15.1", {"start": v(-117, -238) * mm, "end": v(-107, -238) * mm});
            skLineSegment(sketch, "E31.10.15.2", {"start": v(-117, -228) * mm, "end": v(-117, -238) * mm});
            skLineSegment(sketch, "E31.10.15.3", {"start": v(-107, -228) * mm, "end": v(-107, -238) * mm});
            skLineSegment(sketch, "E31.10.16.0", {"start": v(-117, -214) * mm, "end": v(-107, -214) * mm});
            skLineSegment(sketch, "E31.10.16.1", {"start": v(-117, -224) * mm, "end": v(-107, -224) * mm});
            skLineSegment(sketch, "E31.10.16.2", {"start": v(-117, -214) * mm, "end": v(-117, -224) * mm});
            skLineSegment(sketch, "E31.10.16.3", {"start": v(-107, -214) * mm, "end": v(-107, -224) * mm});
            skLineSegment(sketch, "E31.10.17.0", {"start": v(-117, -200) * mm, "end": v(-107, -200) * mm});
            skLineSegment(sketch, "E31.10.17.1", {"start": v(-117, -210) * mm, "end": v(-107, -210) * mm});
            skLineSegment(sketch, "E31.10.17.2", {"start": v(-117, -200) * mm, "end": v(-117, -210) * mm});
            skLineSegment(sketch, "E31.10.17.3", {"start": v(-107, -200) * mm, "end": v(-107, -210) * mm});
            skLineSegment(sketch, "E31.10.18.0", {"start": v(-117, -186) * mm, "end": v(-107, -186) * mm});
            skLineSegment(sketch, "E31.10.18.1", {"start": v(-117, -196) * mm, "end": v(-107, -196) * mm});
            skLineSegment(sketch, "E31.10.18.2", {"start": v(-117, -186) * mm, "end": v(-117, -196) * mm});
            skLineSegment(sketch, "E31.10.18.3", {"start": v(-107, -186) * mm, "end": v(-107, -196) * mm});
            skLineSegment(sketch, "E31.10.19.0", {"start": v(-117, -172) * mm, "end": v(-107, -172) * mm});
            skLineSegment(sketch, "E31.10.19.1", {"start": v(-117, -182) * mm, "end": v(-107, -182) * mm});
            skLineSegment(sketch, "E31.10.19.2", {"start": v(-117, -172) * mm, "end": v(-117, -182) * mm});
            skLineSegment(sketch, "E31.10.19.3", {"start": v(-107, -172) * mm, "end": v(-107, -182) * mm});
            skLineSegment(sketch, "E31.10.20.0", {"start": v(-117, -158) * mm, "end": v(-107, -158) * mm});
            skLineSegment(sketch, "E31.10.20.1", {"start": v(-117, -168) * mm, "end": v(-107, -168) * mm});
            skLineSegment(sketch, "E31.10.20.2", {"start": v(-117, -158) * mm, "end": v(-117, -168) * mm});
            skLineSegment(sketch, "E31.10.20.3", {"start": v(-107, -158) * mm, "end": v(-107, -168) * mm});
            skLineSegment(sketch, "E31.10.21.0", {"start": v(-117, -144) * mm, "end": v(-107, -144) * mm});
            skLineSegment(sketch, "E31.10.21.1", {"start": v(-117, -154) * mm, "end": v(-107, -154) * mm});
            skLineSegment(sketch, "E31.10.21.2", {"start": v(-117, -144) * mm, "end": v(-117, -154) * mm});
            skLineSegment(sketch, "E31.10.21.3", {"start": v(-107, -144) * mm, "end": v(-107, -154) * mm});
            skLineSegment(sketch, "E31.10.22.0", {"start": v(-117, -130) * mm, "end": v(-107, -130) * mm});
            skLineSegment(sketch, "E31.10.22.1", {"start": v(-117, -140) * mm, "end": v(-107, -140) * mm});
            skLineSegment(sketch, "E31.10.22.2", {"start": v(-117, -130) * mm, "end": v(-117, -140) * mm});
            skLineSegment(sketch, "E31.10.22.3", {"start": v(-107, -130) * mm, "end": v(-107, -140) * mm});
            skLineSegment(sketch, "E31.10.23.0", {"start": v(-117, -116) * mm, "end": v(-107, -116) * mm});
            skLineSegment(sketch, "E31.10.23.1", {"start": v(-117, -126) * mm, "end": v(-107, -126) * mm});
            skLineSegment(sketch, "E31.10.23.2", {"start": v(-117, -116) * mm, "end": v(-117, -126) * mm});
            skLineSegment(sketch, "E31.10.23.3", {"start": v(-107, -116) * mm, "end": v(-107, -126) * mm});
            skLineSegment(sketch, "E31.10.24.0", {"start": v(-117, -102) * mm, "end": v(-107, -102) * mm});
            skLineSegment(sketch, "E31.10.24.1", {"start": v(-117, -112) * mm, "end": v(-107, -112) * mm});
            skLineSegment(sketch, "E31.10.24.2", {"start": v(-117, -102) * mm, "end": v(-117, -112) * mm});
            skLineSegment(sketch, "E31.10.24.3", {"start": v(-107, -102) * mm, "end": v(-107, -112) * mm});
            skLineSegment(sketch, "E31.10.25.0", {"start": v(-117, -88) * mm, "end": v(-107, -88) * mm});
            skLineSegment(sketch, "E31.10.25.1", {"start": v(-117, -98) * mm, "end": v(-107, -98) * mm});
            skLineSegment(sketch, "E31.10.25.2", {"start": v(-117, -88) * mm, "end": v(-117, -98) * mm});
            skLineSegment(sketch, "E31.10.25.3", {"start": v(-107, -88) * mm, "end": v(-107, -98) * mm});
            skLineSegment(sketch, "E31.10.26.0", {"start": v(-117, -74) * mm, "end": v(-107, -74) * mm});
            skLineSegment(sketch, "E31.10.26.1", {"start": v(-117, -84) * mm, "end": v(-107, -84) * mm});
            skLineSegment(sketch, "E31.10.26.2", {"start": v(-117, -74) * mm, "end": v(-117, -84) * mm});
            skLineSegment(sketch, "E31.10.26.3", {"start": v(-107, -74) * mm, "end": v(-107, -84) * mm});
            skLineSegment(sketch, "E31.10.27.0", {"start": v(-117, -60) * mm, "end": v(-107, -60) * mm});
            skLineSegment(sketch, "E31.10.27.1", {"start": v(-117, -70) * mm, "end": v(-107, -70) * mm});
            skLineSegment(sketch, "E31.10.27.2", {"start": v(-117, -60) * mm, "end": v(-117, -70) * mm});
            skLineSegment(sketch, "E31.10.27.3", {"start": v(-107, -60) * mm, "end": v(-107, -70) * mm});
            skLineSegment(sketch, "E31.10.28.0", {"start": v(-117, -46) * mm, "end": v(-107, -46) * mm});
            skLineSegment(sketch, "E31.10.28.1", {"start": v(-117, -56) * mm, "end": v(-107, -56) * mm});
            skLineSegment(sketch, "E31.10.28.2", {"start": v(-117, -46) * mm, "end": v(-117, -56) * mm});
            skLineSegment(sketch, "E31.10.28.3", {"start": v(-107, -46) * mm, "end": v(-107, -56) * mm});
            skLineSegment(sketch, "E31.10.29.0", {"start": v(-117, -32) * mm, "end": v(-107, -32) * mm});
            skLineSegment(sketch, "E31.10.29.1", {"start": v(-117, -42) * mm, "end": v(-107, -42) * mm});
            skLineSegment(sketch, "E31.10.29.2", {"start": v(-117, -32) * mm, "end": v(-117, -42) * mm});
            skLineSegment(sketch, "E31.10.29.3", {"start": v(-107, -32) * mm, "end": v(-107, -42) * mm});
            skLineSegment(sketch, "E31.10.30.0", {"start": v(-117, -18) * mm, "end": v(-107, -18) * mm});
            skLineSegment(sketch, "E31.10.30.1", {"start": v(-117, -28) * mm, "end": v(-107, -28) * mm});
            skLineSegment(sketch, "E31.10.30.2", {"start": v(-117, -18) * mm, "end": v(-117, -28) * mm});
            skLineSegment(sketch, "E31.10.30.3", {"start": v(-107, -18) * mm, "end": v(-107, -28) * mm});
            skLineSegment(sketch, "E31.10.31.0", {"start": v(-117, -4) * mm, "end": v(-107, -4) * mm});
            skLineSegment(sketch, "E31.10.31.1", {"start": v(-117, -14) * mm, "end": v(-107, -14) * mm});
            skLineSegment(sketch, "E31.10.31.2", {"start": v(-117, -4) * mm, "end": v(-117, -14) * mm});
            skLineSegment(sketch, "E31.10.31.3", {"start": v(-107, -4) * mm, "end": v(-107, -14) * mm});
            skLineSegment(sketch, "E31.11.0.0", {"start": v(-103, -438) * mm, "end": v(-93, -438) * mm});
            skLineSegment(sketch, "E31.11.0.1", {"start": v(-103, -448) * mm, "end": v(-93, -448) * mm});
            skLineSegment(sketch, "E31.11.0.2", {"start": v(-103, -438) * mm, "end": v(-103, -448) * mm});
            skLineSegment(sketch, "E31.11.0.3", {"start": v(-93, -438) * mm, "end": v(-93, -448) * mm});
            skLineSegment(sketch, "E31.11.1.0", {"start": v(-103, -424) * mm, "end": v(-93, -424) * mm});
            skLineSegment(sketch, "E31.11.1.1", {"start": v(-103, -434) * mm, "end": v(-93, -434) * mm});
            skLineSegment(sketch, "E31.11.1.2", {"start": v(-103, -424) * mm, "end": v(-103, -434) * mm});
            skLineSegment(sketch, "E31.11.1.3", {"start": v(-93, -424) * mm, "end": v(-93, -434) * mm});
            skLineSegment(sketch, "E31.11.2.0", {"start": v(-103, -410) * mm, "end": v(-93, -410) * mm});
            skLineSegment(sketch, "E31.11.2.1", {"start": v(-103, -420) * mm, "end": v(-93, -420) * mm});
            skLineSegment(sketch, "E31.11.2.2", {"start": v(-103, -410) * mm, "end": v(-103, -420) * mm});
            skLineSegment(sketch, "E31.11.2.3", {"start": v(-93, -410) * mm, "end": v(-93, -420) * mm});
            skLineSegment(sketch, "E31.11.3.0", {"start": v(-103, -396) * mm, "end": v(-93, -396) * mm});
            skLineSegment(sketch, "E31.11.3.1", {"start": v(-103, -406) * mm, "end": v(-93, -406) * mm});
            skLineSegment(sketch, "E31.11.3.2", {"start": v(-103, -396) * mm, "end": v(-103, -406) * mm});
            skLineSegment(sketch, "E31.11.3.3", {"start": v(-93, -396) * mm, "end": v(-93, -406) * mm});
            skLineSegment(sketch, "E31.11.4.0", {"start": v(-103, -382) * mm, "end": v(-93, -382) * mm});
            skLineSegment(sketch, "E31.11.4.1", {"start": v(-103, -392) * mm, "end": v(-93, -392) * mm});
            skLineSegment(sketch, "E31.11.4.2", {"start": v(-103, -382) * mm, "end": v(-103, -392) * mm});
            skLineSegment(sketch, "E31.11.4.3", {"start": v(-93, -382) * mm, "end": v(-93, -392) * mm});
            skLineSegment(sketch, "E31.11.5.0", {"start": v(-103, -368) * mm, "end": v(-93, -368) * mm});
            skLineSegment(sketch, "E31.11.5.1", {"start": v(-103, -378) * mm, "end": v(-93, -378) * mm});
            skLineSegment(sketch, "E31.11.5.2", {"start": v(-103, -368) * mm, "end": v(-103, -378) * mm});
            skLineSegment(sketch, "E31.11.5.3", {"start": v(-93, -368) * mm, "end": v(-93, -378) * mm});
            skLineSegment(sketch, "E31.11.6.0", {"start": v(-103, -354) * mm, "end": v(-93, -354) * mm});
            skLineSegment(sketch, "E31.11.6.1", {"start": v(-103, -364) * mm, "end": v(-93, -364) * mm});
            skLineSegment(sketch, "E31.11.6.2", {"start": v(-103, -354) * mm, "end": v(-103, -364) * mm});
            skLineSegment(sketch, "E31.11.6.3", {"start": v(-93, -354) * mm, "end": v(-93, -364) * mm});
            skLineSegment(sketch, "E31.11.7.0", {"start": v(-103, -340) * mm, "end": v(-93, -340) * mm});
            skLineSegment(sketch, "E31.11.7.1", {"start": v(-103, -350) * mm, "end": v(-93, -350) * mm});
            skLineSegment(sketch, "E31.11.7.2", {"start": v(-103, -340) * mm, "end": v(-103, -350) * mm});
            skLineSegment(sketch, "E31.11.7.3", {"start": v(-93, -340) * mm, "end": v(-93, -350) * mm});
            skLineSegment(sketch, "E31.11.8.0", {"start": v(-103, -326) * mm, "end": v(-93, -326) * mm});
            skLineSegment(sketch, "E31.11.8.1", {"start": v(-103, -336) * mm, "end": v(-93, -336) * mm});
            skLineSegment(sketch, "E31.11.8.2", {"start": v(-103, -326) * mm, "end": v(-103, -336) * mm});
            skLineSegment(sketch, "E31.11.8.3", {"start": v(-93, -326) * mm, "end": v(-93, -336) * mm});
            skLineSegment(sketch, "E31.11.9.0", {"start": v(-103, -312) * mm, "end": v(-93, -312) * mm});
            skLineSegment(sketch, "E31.11.9.1", {"start": v(-103, -322) * mm, "end": v(-93, -322) * mm});
            skLineSegment(sketch, "E31.11.9.2", {"start": v(-103, -312) * mm, "end": v(-103, -322) * mm});
            skLineSegment(sketch, "E31.11.9.3", {"start": v(-93, -312) * mm, "end": v(-93, -322) * mm});
            skLineSegment(sketch, "E31.11.10.0", {"start": v(-103, -298) * mm, "end": v(-93, -298) * mm});
            skLineSegment(sketch, "E31.11.10.1", {"start": v(-103, -308) * mm, "end": v(-93, -308) * mm});
            skLineSegment(sketch, "E31.11.10.2", {"start": v(-103, -298) * mm, "end": v(-103, -308) * mm});
            skLineSegment(sketch, "E31.11.10.3", {"start": v(-93, -298) * mm, "end": v(-93, -308) * mm});
            skLineSegment(sketch, "E31.11.11.0", {"start": v(-103, -284) * mm, "end": v(-93, -284) * mm});
            skLineSegment(sketch, "E31.11.11.1", {"start": v(-103, -294) * mm, "end": v(-93, -294) * mm});
            skLineSegment(sketch, "E31.11.11.2", {"start": v(-103, -284) * mm, "end": v(-103, -294) * mm});
            skLineSegment(sketch, "E31.11.11.3", {"start": v(-93, -284) * mm, "end": v(-93, -294) * mm});
            skLineSegment(sketch, "E31.11.12.0", {"start": v(-103, -270) * mm, "end": v(-93, -270) * mm});
            skLineSegment(sketch, "E31.11.12.1", {"start": v(-103, -280) * mm, "end": v(-93, -280) * mm});
            skLineSegment(sketch, "E31.11.12.2", {"start": v(-103, -270) * mm, "end": v(-103, -280) * mm});
            skLineSegment(sketch, "E31.11.12.3", {"start": v(-93, -270) * mm, "end": v(-93, -280) * mm});
            skLineSegment(sketch, "E31.11.13.0", {"start": v(-103, -256) * mm, "end": v(-93, -256) * mm});
            skLineSegment(sketch, "E31.11.13.1", {"start": v(-103, -266) * mm, "end": v(-93, -266) * mm});
            skLineSegment(sketch, "E31.11.13.2", {"start": v(-103, -256) * mm, "end": v(-103, -266) * mm});
            skLineSegment(sketch, "E31.11.13.3", {"start": v(-93, -256) * mm, "end": v(-93, -266) * mm});
            skLineSegment(sketch, "E31.11.14.0", {"start": v(-103, -242) * mm, "end": v(-93, -242) * mm});
            skLineSegment(sketch, "E31.11.14.1", {"start": v(-103, -252) * mm, "end": v(-93, -252) * mm});
            skLineSegment(sketch, "E31.11.14.2", {"start": v(-103, -242) * mm, "end": v(-103, -252) * mm});
            skLineSegment(sketch, "E31.11.14.3", {"start": v(-93, -242) * mm, "end": v(-93, -252) * mm});
            skLineSegment(sketch, "E31.11.15.0", {"start": v(-103, -228) * mm, "end": v(-93, -228) * mm});
            skLineSegment(sketch, "E31.11.15.1", {"start": v(-103, -238) * mm, "end": v(-93, -238) * mm});
            skLineSegment(sketch, "E31.11.15.2", {"start": v(-103, -228) * mm, "end": v(-103, -238) * mm});
            skLineSegment(sketch, "E31.11.15.3", {"start": v(-93, -228) * mm, "end": v(-93, -238) * mm});
            skLineSegment(sketch, "E31.11.16.0", {"start": v(-103, -214) * mm, "end": v(-93, -214) * mm});
            skLineSegment(sketch, "E31.11.16.1", {"start": v(-103, -224) * mm, "end": v(-93, -224) * mm});
            skLineSegment(sketch, "E31.11.16.2", {"start": v(-103, -214) * mm, "end": v(-103, -224) * mm});
            skLineSegment(sketch, "E31.11.16.3", {"start": v(-93, -214) * mm, "end": v(-93, -224) * mm});
            skLineSegment(sketch, "E31.11.17.0", {"start": v(-103, -200) * mm, "end": v(-93, -200) * mm});
            skLineSegment(sketch, "E31.11.17.1", {"start": v(-103, -210) * mm, "end": v(-93, -210) * mm});
            skLineSegment(sketch, "E31.11.17.2", {"start": v(-103, -200) * mm, "end": v(-103, -210) * mm});
            skLineSegment(sketch, "E31.11.17.3", {"start": v(-93, -200) * mm, "end": v(-93, -210) * mm});
            skLineSegment(sketch, "E31.11.18.0", {"start": v(-103, -186) * mm, "end": v(-93, -186) * mm});
            skLineSegment(sketch, "E31.11.18.1", {"start": v(-103, -196) * mm, "end": v(-93, -196) * mm});
            skLineSegment(sketch, "E31.11.18.2", {"start": v(-103, -186) * mm, "end": v(-103, -196) * mm});
            skLineSegment(sketch, "E31.11.18.3", {"start": v(-93, -186) * mm, "end": v(-93, -196) * mm});
            skLineSegment(sketch, "E31.11.19.0", {"start": v(-103, -172) * mm, "end": v(-93, -172) * mm});
            skLineSegment(sketch, "E31.11.19.1", {"start": v(-103, -182) * mm, "end": v(-93, -182) * mm});
            skLineSegment(sketch, "E31.11.19.2", {"start": v(-103, -172) * mm, "end": v(-103, -182) * mm});
            skLineSegment(sketch, "E31.11.19.3", {"start": v(-93, -172) * mm, "end": v(-93, -182) * mm});
            skLineSegment(sketch, "E31.11.20.0", {"start": v(-103, -158) * mm, "end": v(-93, -158) * mm});
            skLineSegment(sketch, "E31.11.20.1", {"start": v(-103, -168) * mm, "end": v(-93, -168) * mm});
            skLineSegment(sketch, "E31.11.20.2", {"start": v(-103, -158) * mm, "end": v(-103, -168) * mm});
            skLineSegment(sketch, "E31.11.20.3", {"start": v(-93, -158) * mm, "end": v(-93, -168) * mm});
            skLineSegment(sketch, "E31.11.21.0", {"start": v(-103, -144) * mm, "end": v(-93, -144) * mm});
            skLineSegment(sketch, "E31.11.21.1", {"start": v(-103, -154) * mm, "end": v(-93, -154) * mm});
            skLineSegment(sketch, "E31.11.21.2", {"start": v(-103, -144) * mm, "end": v(-103, -154) * mm});
            skLineSegment(sketch, "E31.11.21.3", {"start": v(-93, -144) * mm, "end": v(-93, -154) * mm});
            skLineSegment(sketch, "E31.11.22.0", {"start": v(-103, -130) * mm, "end": v(-93, -130) * mm});
            skLineSegment(sketch, "E31.11.22.1", {"start": v(-103, -140) * mm, "end": v(-93, -140) * mm});
            skLineSegment(sketch, "E31.11.22.2", {"start": v(-103, -130) * mm, "end": v(-103, -140) * mm});
            skLineSegment(sketch, "E31.11.22.3", {"start": v(-93, -130) * mm, "end": v(-93, -140) * mm});
            skLineSegment(sketch, "E31.11.23.0", {"start": v(-103, -116) * mm, "end": v(-93, -116) * mm});
            skLineSegment(sketch, "E31.11.23.1", {"start": v(-103, -126) * mm, "end": v(-93, -126) * mm});
            skLineSegment(sketch, "E31.11.23.2", {"start": v(-103, -116) * mm, "end": v(-103, -126) * mm});
            skLineSegment(sketch, "E31.11.23.3", {"start": v(-93, -116) * mm, "end": v(-93, -126) * mm});
            skLineSegment(sketch, "E31.11.24.0", {"start": v(-103, -102) * mm, "end": v(-93, -102) * mm});
            skLineSegment(sketch, "E31.11.24.1", {"start": v(-103, -112) * mm, "end": v(-93, -112) * mm});
            skLineSegment(sketch, "E31.11.24.2", {"start": v(-103, -102) * mm, "end": v(-103, -112) * mm});
            skLineSegment(sketch, "E31.11.24.3", {"start": v(-93, -102) * mm, "end": v(-93, -112) * mm});
            skLineSegment(sketch, "E31.11.25.0", {"start": v(-103, -88) * mm, "end": v(-93, -88) * mm});
            skLineSegment(sketch, "E31.11.25.1", {"start": v(-103, -98) * mm, "end": v(-93, -98) * mm});
            skLineSegment(sketch, "E31.11.25.2", {"start": v(-103, -88) * mm, "end": v(-103, -98) * mm});
            skLineSegment(sketch, "E31.11.25.3", {"start": v(-93, -88) * mm, "end": v(-93, -98) * mm});
            skLineSegment(sketch, "E31.11.26.0", {"start": v(-103, -74) * mm, "end": v(-93, -74) * mm});
            skLineSegment(sketch, "E31.11.26.1", {"start": v(-103, -84) * mm, "end": v(-93, -84) * mm});
            skLineSegment(sketch, "E31.11.26.2", {"start": v(-103, -74) * mm, "end": v(-103, -84) * mm});
            skLineSegment(sketch, "E31.11.26.3", {"start": v(-93, -74) * mm, "end": v(-93, -84) * mm});
            skLineSegment(sketch, "E31.11.27.0", {"start": v(-103, -60) * mm, "end": v(-93, -60) * mm});
            skLineSegment(sketch, "E31.11.27.1", {"start": v(-103, -70) * mm, "end": v(-93, -70) * mm});
            skLineSegment(sketch, "E31.11.27.2", {"start": v(-103, -60) * mm, "end": v(-103, -70) * mm});
            skLineSegment(sketch, "E31.11.27.3", {"start": v(-93, -60) * mm, "end": v(-93, -70) * mm});
            skLineSegment(sketch, "E31.11.28.0", {"start": v(-103, -46) * mm, "end": v(-93, -46) * mm});
            skLineSegment(sketch, "E31.11.28.1", {"start": v(-103, -56) * mm, "end": v(-93, -56) * mm});
            skLineSegment(sketch, "E31.11.28.2", {"start": v(-103, -46) * mm, "end": v(-103, -56) * mm});
            skLineSegment(sketch, "E31.11.28.3", {"start": v(-93, -46) * mm, "end": v(-93, -56) * mm});
            skLineSegment(sketch, "E31.11.29.0", {"start": v(-103, -32) * mm, "end": v(-93, -32) * mm});
            skLineSegment(sketch, "E31.11.29.1", {"start": v(-103, -42) * mm, "end": v(-93, -42) * mm});
            skLineSegment(sketch, "E31.11.29.2", {"start": v(-103, -32) * mm, "end": v(-103, -42) * mm});
            skLineSegment(sketch, "E31.11.29.3", {"start": v(-93, -32) * mm, "end": v(-93, -42) * mm});
            skLineSegment(sketch, "E31.11.30.0", {"start": v(-103, -18) * mm, "end": v(-93, -18) * mm});
            skLineSegment(sketch, "E31.11.30.1", {"start": v(-103, -28) * mm, "end": v(-93, -28) * mm});
            skLineSegment(sketch, "E31.11.30.2", {"start": v(-103, -18) * mm, "end": v(-103, -28) * mm});
            skLineSegment(sketch, "E31.11.30.3", {"start": v(-93, -18) * mm, "end": v(-93, -28) * mm});
            skLineSegment(sketch, "E31.11.31.0", {"start": v(-103, -4) * mm, "end": v(-93, -4) * mm});
            skLineSegment(sketch, "E31.11.31.1", {"start": v(-103, -14) * mm, "end": v(-93, -14) * mm});
            skLineSegment(sketch, "E31.11.31.2", {"start": v(-103, -4) * mm, "end": v(-103, -14) * mm});
            skLineSegment(sketch, "E31.11.31.3", {"start": v(-93, -4) * mm, "end": v(-93, -14) * mm});
            skLineSegment(sketch, "E31.12.0.0", {"start": v(-89, -438) * mm, "end": v(-79, -438) * mm});
            skLineSegment(sketch, "E31.12.0.1", {"start": v(-89, -448) * mm, "end": v(-79, -448) * mm});
            skLineSegment(sketch, "E31.12.0.2", {"start": v(-89, -438) * mm, "end": v(-89, -448) * mm});
            skLineSegment(sketch, "E31.12.0.3", {"start": v(-79, -438) * mm, "end": v(-79, -448) * mm});
            skLineSegment(sketch, "E31.12.1.0", {"start": v(-89, -424) * mm, "end": v(-79, -424) * mm});
            skLineSegment(sketch, "E31.12.1.1", {"start": v(-89, -434) * mm, "end": v(-79, -434) * mm});
            skLineSegment(sketch, "E31.12.1.2", {"start": v(-89, -424) * mm, "end": v(-89, -434) * mm});
            skLineSegment(sketch, "E31.12.1.3", {"start": v(-79, -424) * mm, "end": v(-79, -434) * mm});
            skLineSegment(sketch, "E31.12.2.0", {"start": v(-89, -410) * mm, "end": v(-79, -410) * mm});
            skLineSegment(sketch, "E31.12.2.1", {"start": v(-89, -420) * mm, "end": v(-79, -420) * mm});
            skLineSegment(sketch, "E31.12.2.2", {"start": v(-89, -410) * mm, "end": v(-89, -420) * mm});
            skLineSegment(sketch, "E31.12.2.3", {"start": v(-79, -410) * mm, "end": v(-79, -420) * mm});
            skLineSegment(sketch, "E31.12.3.0", {"start": v(-89, -396) * mm, "end": v(-79, -396) * mm});
            skLineSegment(sketch, "E31.12.3.1", {"start": v(-89, -406) * mm, "end": v(-79, -406) * mm});
            skLineSegment(sketch, "E31.12.3.2", {"start": v(-89, -396) * mm, "end": v(-89, -406) * mm});
            skLineSegment(sketch, "E31.12.3.3", {"start": v(-79, -396) * mm, "end": v(-79, -406) * mm});
            skLineSegment(sketch, "E31.12.4.0", {"start": v(-89, -382) * mm, "end": v(-79, -382) * mm});
            skLineSegment(sketch, "E31.12.4.1", {"start": v(-89, -392) * mm, "end": v(-79, -392) * mm});
            skLineSegment(sketch, "E31.12.4.2", {"start": v(-89, -382) * mm, "end": v(-89, -392) * mm});
            skLineSegment(sketch, "E31.12.4.3", {"start": v(-79, -382) * mm, "end": v(-79, -392) * mm});
            skLineSegment(sketch, "E31.12.5.0", {"start": v(-89, -368) * mm, "end": v(-79, -368) * mm});
            skLineSegment(sketch, "E31.12.5.1", {"start": v(-89, -378) * mm, "end": v(-79, -378) * mm});
            skLineSegment(sketch, "E31.12.5.2", {"start": v(-89, -368) * mm, "end": v(-89, -378) * mm});
            skLineSegment(sketch, "E31.12.5.3", {"start": v(-79, -368) * mm, "end": v(-79, -378) * mm});
            skLineSegment(sketch, "E31.12.6.0", {"start": v(-89, -354) * mm, "end": v(-79, -354) * mm});
            skLineSegment(sketch, "E31.12.6.1", {"start": v(-89, -364) * mm, "end": v(-79, -364) * mm});
            skLineSegment(sketch, "E31.12.6.2", {"start": v(-89, -354) * mm, "end": v(-89, -364) * mm});
            skLineSegment(sketch, "E31.12.6.3", {"start": v(-79, -354) * mm, "end": v(-79, -364) * mm});
            skLineSegment(sketch, "E31.12.7.0", {"start": v(-89, -340) * mm, "end": v(-79, -340) * mm});
            skLineSegment(sketch, "E31.12.7.1", {"start": v(-89, -350) * mm, "end": v(-79, -350) * mm});
            skLineSegment(sketch, "E31.12.7.2", {"start": v(-89, -340) * mm, "end": v(-89, -350) * mm});
            skLineSegment(sketch, "E31.12.7.3", {"start": v(-79, -340) * mm, "end": v(-79, -350) * mm});
            skLineSegment(sketch, "E31.12.8.0", {"start": v(-89, -326) * mm, "end": v(-79, -326) * mm});
            skLineSegment(sketch, "E31.12.8.1", {"start": v(-89, -336) * mm, "end": v(-79, -336) * mm});
            skLineSegment(sketch, "E31.12.8.2", {"start": v(-89, -326) * mm, "end": v(-89, -336) * mm});
            skLineSegment(sketch, "E31.12.8.3", {"start": v(-79, -326) * mm, "end": v(-79, -336) * mm});
            skLineSegment(sketch, "E31.12.9.0", {"start": v(-89, -312) * mm, "end": v(-79, -312) * mm});
            skLineSegment(sketch, "E31.12.9.1", {"start": v(-89, -322) * mm, "end": v(-79, -322) * mm});
            skLineSegment(sketch, "E31.12.9.2", {"start": v(-89, -312) * mm, "end": v(-89, -322) * mm});
            skLineSegment(sketch, "E31.12.9.3", {"start": v(-79, -312) * mm, "end": v(-79, -322) * mm});
            skLineSegment(sketch, "E31.12.10.0", {"start": v(-89, -298) * mm, "end": v(-79, -298) * mm});
            skLineSegment(sketch, "E31.12.10.1", {"start": v(-89, -308) * mm, "end": v(-79, -308) * mm});
            skLineSegment(sketch, "E31.12.10.2", {"start": v(-89, -298) * mm, "end": v(-89, -308) * mm});
            skLineSegment(sketch, "E31.12.10.3", {"start": v(-79, -298) * mm, "end": v(-79, -308) * mm});
            skLineSegment(sketch, "E31.12.11.0", {"start": v(-89, -284) * mm, "end": v(-79, -284) * mm});
            skLineSegment(sketch, "E31.12.11.1", {"start": v(-89, -294) * mm, "end": v(-79, -294) * mm});
            skLineSegment(sketch, "E31.12.11.2", {"start": v(-89, -284) * mm, "end": v(-89, -294) * mm});
            skLineSegment(sketch, "E31.12.11.3", {"start": v(-79, -284) * mm, "end": v(-79, -294) * mm});
            skLineSegment(sketch, "E31.12.12.0", {"start": v(-89, -270) * mm, "end": v(-79, -270) * mm});
            skLineSegment(sketch, "E31.12.12.1", {"start": v(-89, -280) * mm, "end": v(-79, -280) * mm});
            skLineSegment(sketch, "E31.12.12.2", {"start": v(-89, -270) * mm, "end": v(-89, -280) * mm});
            skLineSegment(sketch, "E31.12.12.3", {"start": v(-79, -270) * mm, "end": v(-79, -280) * mm});
            skLineSegment(sketch, "E31.12.13.0", {"start": v(-89, -256) * mm, "end": v(-79, -256) * mm});
            skLineSegment(sketch, "E31.12.13.1", {"start": v(-89, -266) * mm, "end": v(-79, -266) * mm});
            skLineSegment(sketch, "E31.12.13.2", {"start": v(-89, -256) * mm, "end": v(-89, -266) * mm});
            skLineSegment(sketch, "E31.12.13.3", {"start": v(-79, -256) * mm, "end": v(-79, -266) * mm});
            skLineSegment(sketch, "E31.12.14.0", {"start": v(-89, -242) * mm, "end": v(-79, -242) * mm});
            skLineSegment(sketch, "E31.12.14.1", {"start": v(-89, -252) * mm, "end": v(-79, -252) * mm});
            skLineSegment(sketch, "E31.12.14.2", {"start": v(-89, -242) * mm, "end": v(-89, -252) * mm});
            skLineSegment(sketch, "E31.12.14.3", {"start": v(-79, -242) * mm, "end": v(-79, -252) * mm});
            skLineSegment(sketch, "E31.12.15.0", {"start": v(-89, -228) * mm, "end": v(-79, -228) * mm});
            skLineSegment(sketch, "E31.12.15.1", {"start": v(-89, -238) * mm, "end": v(-79, -238) * mm});
            skLineSegment(sketch, "E31.12.15.2", {"start": v(-89, -228) * mm, "end": v(-89, -238) * mm});
            skLineSegment(sketch, "E31.12.15.3", {"start": v(-79, -228) * mm, "end": v(-79, -238) * mm});
            skLineSegment(sketch, "E31.12.16.0", {"start": v(-89, -214) * mm, "end": v(-79, -214) * mm});
            skLineSegment(sketch, "E31.12.16.1", {"start": v(-89, -224) * mm, "end": v(-79, -224) * mm});
            skLineSegment(sketch, "E31.12.16.2", {"start": v(-89, -214) * mm, "end": v(-89, -224) * mm});
            skLineSegment(sketch, "E31.12.16.3", {"start": v(-79, -214) * mm, "end": v(-79, -224) * mm});
            skLineSegment(sketch, "E31.12.17.0", {"start": v(-89, -200) * mm, "end": v(-79, -200) * mm});
            skLineSegment(sketch, "E31.12.17.1", {"start": v(-89, -210) * mm, "end": v(-79, -210) * mm});
            skLineSegment(sketch, "E31.12.17.2", {"start": v(-89, -200) * mm, "end": v(-89, -210) * mm});
            skLineSegment(sketch, "E31.12.17.3", {"start": v(-79, -200) * mm, "end": v(-79, -210) * mm});
            skLineSegment(sketch, "E31.12.18.0", {"start": v(-89, -186) * mm, "end": v(-79, -186) * mm});
            skLineSegment(sketch, "E31.12.18.1", {"start": v(-89, -196) * mm, "end": v(-79, -196) * mm});
            skLineSegment(sketch, "E31.12.18.2", {"start": v(-89, -186) * mm, "end": v(-89, -196) * mm});
            skLineSegment(sketch, "E31.12.18.3", {"start": v(-79, -186) * mm, "end": v(-79, -196) * mm});
            skLineSegment(sketch, "E31.12.19.0", {"start": v(-89, -172) * mm, "end": v(-79, -172) * mm});
            skLineSegment(sketch, "E31.12.19.1", {"start": v(-89, -182) * mm, "end": v(-79, -182) * mm});
            skLineSegment(sketch, "E31.12.19.2", {"start": v(-89, -172) * mm, "end": v(-89, -182) * mm});
            skLineSegment(sketch, "E31.12.19.3", {"start": v(-79, -172) * mm, "end": v(-79, -182) * mm});
            skLineSegment(sketch, "E31.12.20.0", {"start": v(-89, -158) * mm, "end": v(-79, -158) * mm});
            skLineSegment(sketch, "E31.12.20.1", {"start": v(-89, -168) * mm, "end": v(-79, -168) * mm});
            skLineSegment(sketch, "E31.12.20.2", {"start": v(-89, -158) * mm, "end": v(-89, -168) * mm});
            skLineSegment(sketch, "E31.12.20.3", {"start": v(-79, -158) * mm, "end": v(-79, -168) * mm});
            skLineSegment(sketch, "E31.12.21.0", {"start": v(-89, -144) * mm, "end": v(-79, -144) * mm});
            skLineSegment(sketch, "E31.12.21.1", {"start": v(-89, -154) * mm, "end": v(-79, -154) * mm});
            skLineSegment(sketch, "E31.12.21.2", {"start": v(-89, -144) * mm, "end": v(-89, -154) * mm});
            skLineSegment(sketch, "E31.12.21.3", {"start": v(-79, -144) * mm, "end": v(-79, -154) * mm});
            skLineSegment(sketch, "E31.12.22.0", {"start": v(-89, -130) * mm, "end": v(-79, -130) * mm});
            skLineSegment(sketch, "E31.12.22.1", {"start": v(-89, -140) * mm, "end": v(-79, -140) * mm});
            skLineSegment(sketch, "E31.12.22.2", {"start": v(-89, -130) * mm, "end": v(-89, -140) * mm});
            skLineSegment(sketch, "E31.12.22.3", {"start": v(-79, -130) * mm, "end": v(-79, -140) * mm});
            skLineSegment(sketch, "E31.12.23.0", {"start": v(-89, -116) * mm, "end": v(-79, -116) * mm});
            skLineSegment(sketch, "E31.12.23.1", {"start": v(-89, -126) * mm, "end": v(-79, -126) * mm});
            skLineSegment(sketch, "E31.12.23.2", {"start": v(-89, -116) * mm, "end": v(-89, -126) * mm});
            skLineSegment(sketch, "E31.12.23.3", {"start": v(-79, -116) * mm, "end": v(-79, -126) * mm});
            skLineSegment(sketch, "E31.12.24.0", {"start": v(-89, -102) * mm, "end": v(-79, -102) * mm});
            skLineSegment(sketch, "E31.12.24.1", {"start": v(-89, -112) * mm, "end": v(-79, -112) * mm});
            skLineSegment(sketch, "E31.12.24.2", {"start": v(-89, -102) * mm, "end": v(-89, -112) * mm});
            skLineSegment(sketch, "E31.12.24.3", {"start": v(-79, -102) * mm, "end": v(-79, -112) * mm});
            skLineSegment(sketch, "E31.12.25.0", {"start": v(-89, -88) * mm, "end": v(-79, -88) * mm});
            skLineSegment(sketch, "E31.12.25.1", {"start": v(-89, -98) * mm, "end": v(-79, -98) * mm});
            skLineSegment(sketch, "E31.12.25.2", {"start": v(-89, -88) * mm, "end": v(-89, -98) * mm});
            skLineSegment(sketch, "E31.12.25.3", {"start": v(-79, -88) * mm, "end": v(-79, -98) * mm});
            skLineSegment(sketch, "E31.12.26.0", {"start": v(-89, -74) * mm, "end": v(-79, -74) * mm});
            skLineSegment(sketch, "E31.12.26.1", {"start": v(-89, -84) * mm, "end": v(-79, -84) * mm});
            skLineSegment(sketch, "E31.12.26.2", {"start": v(-89, -74) * mm, "end": v(-89, -84) * mm});
            skLineSegment(sketch, "E31.12.26.3", {"start": v(-79, -74) * mm, "end": v(-79, -84) * mm});
            skLineSegment(sketch, "E31.12.27.0", {"start": v(-89, -60) * mm, "end": v(-79, -60) * mm});
            skLineSegment(sketch, "E31.12.27.1", {"start": v(-89, -70) * mm, "end": v(-79, -70) * mm});
            skLineSegment(sketch, "E31.12.27.2", {"start": v(-89, -60) * mm, "end": v(-89, -70) * mm});
            skLineSegment(sketch, "E31.12.27.3", {"start": v(-79, -60) * mm, "end": v(-79, -70) * mm});
            skLineSegment(sketch, "E31.12.28.0", {"start": v(-89, -46) * mm, "end": v(-79, -46) * mm});
            skLineSegment(sketch, "E31.12.28.1", {"start": v(-89, -56) * mm, "end": v(-79, -56) * mm});
            skLineSegment(sketch, "E31.12.28.2", {"start": v(-89, -46) * mm, "end": v(-89, -56) * mm});
            skLineSegment(sketch, "E31.12.28.3", {"start": v(-79, -46) * mm, "end": v(-79, -56) * mm});
            skLineSegment(sketch, "E31.12.29.0", {"start": v(-89, -32) * mm, "end": v(-79, -32) * mm});
            skLineSegment(sketch, "E31.12.29.1", {"start": v(-89, -42) * mm, "end": v(-79, -42) * mm});
            skLineSegment(sketch, "E31.12.29.2", {"start": v(-89, -32) * mm, "end": v(-89, -42) * mm});
            skLineSegment(sketch, "E31.12.29.3", {"start": v(-79, -32) * mm, "end": v(-79, -42) * mm});
            skLineSegment(sketch, "E31.12.30.0", {"start": v(-89, -18) * mm, "end": v(-79, -18) * mm});
            skLineSegment(sketch, "E31.12.30.1", {"start": v(-89, -28) * mm, "end": v(-79, -28) * mm});
            skLineSegment(sketch, "E31.12.30.2", {"start": v(-89, -18) * mm, "end": v(-89, -28) * mm});
            skLineSegment(sketch, "E31.12.30.3", {"start": v(-79, -18) * mm, "end": v(-79, -28) * mm});
            skLineSegment(sketch, "E31.12.31.0", {"start": v(-89, -4) * mm, "end": v(-79, -4) * mm});
            skLineSegment(sketch, "E31.12.31.1", {"start": v(-89, -14) * mm, "end": v(-79, -14) * mm});
            skLineSegment(sketch, "E31.12.31.2", {"start": v(-89, -4) * mm, "end": v(-89, -14) * mm});
            skLineSegment(sketch, "E31.12.31.3", {"start": v(-79, -4) * mm, "end": v(-79, -14) * mm});
            skLineSegment(sketch, "E31.13.0.0", {"start": v(-75, -438) * mm, "end": v(-65, -438) * mm});
            skLineSegment(sketch, "E31.13.0.1", {"start": v(-75, -448) * mm, "end": v(-65, -448) * mm});
            skLineSegment(sketch, "E31.13.0.2", {"start": v(-75, -438) * mm, "end": v(-75, -448) * mm});
            skLineSegment(sketch, "E31.13.0.3", {"start": v(-65, -438) * mm, "end": v(-65, -448) * mm});
            skLineSegment(sketch, "E31.13.1.0", {"start": v(-75, -424) * mm, "end": v(-65, -424) * mm});
            skLineSegment(sketch, "E31.13.1.1", {"start": v(-75, -434) * mm, "end": v(-65, -434) * mm});
            skLineSegment(sketch, "E31.13.1.2", {"start": v(-75, -424) * mm, "end": v(-75, -434) * mm});
            skLineSegment(sketch, "E31.13.1.3", {"start": v(-65, -424) * mm, "end": v(-65, -434) * mm});
            skLineSegment(sketch, "E31.13.2.0", {"start": v(-75, -410) * mm, "end": v(-65, -410) * mm});
            skLineSegment(sketch, "E31.13.2.1", {"start": v(-75, -420) * mm, "end": v(-65, -420) * mm});
            skLineSegment(sketch, "E31.13.2.2", {"start": v(-75, -410) * mm, "end": v(-75, -420) * mm});
            skLineSegment(sketch, "E31.13.2.3", {"start": v(-65, -410) * mm, "end": v(-65, -420) * mm});
            skLineSegment(sketch, "E31.13.3.0", {"start": v(-75, -396) * mm, "end": v(-65, -396) * mm});
            skLineSegment(sketch, "E31.13.3.1", {"start": v(-75, -406) * mm, "end": v(-65, -406) * mm});
            skLineSegment(sketch, "E31.13.3.2", {"start": v(-75, -396) * mm, "end": v(-75, -406) * mm});
            skLineSegment(sketch, "E31.13.3.3", {"start": v(-65, -396) * mm, "end": v(-65, -406) * mm});
            skLineSegment(sketch, "E31.13.4.0", {"start": v(-75, -382) * mm, "end": v(-65, -382) * mm});
            skLineSegment(sketch, "E31.13.4.1", {"start": v(-75, -392) * mm, "end": v(-65, -392) * mm});
            skLineSegment(sketch, "E31.13.4.2", {"start": v(-75, -382) * mm, "end": v(-75, -392) * mm});
            skLineSegment(sketch, "E31.13.4.3", {"start": v(-65, -382) * mm, "end": v(-65, -392) * mm});
            skLineSegment(sketch, "E31.13.5.0", {"start": v(-75, -368) * mm, "end": v(-65, -368) * mm});
            skLineSegment(sketch, "E31.13.5.1", {"start": v(-75, -378) * mm, "end": v(-65, -378) * mm});
            skLineSegment(sketch, "E31.13.5.2", {"start": v(-75, -368) * mm, "end": v(-75, -378) * mm});
            skLineSegment(sketch, "E31.13.5.3", {"start": v(-65, -368) * mm, "end": v(-65, -378) * mm});
            skLineSegment(sketch, "E31.13.6.0", {"start": v(-75, -354) * mm, "end": v(-65, -354) * mm});
            skLineSegment(sketch, "E31.13.6.1", {"start": v(-75, -364) * mm, "end": v(-65, -364) * mm});
            skLineSegment(sketch, "E31.13.6.2", {"start": v(-75, -354) * mm, "end": v(-75, -364) * mm});
            skLineSegment(sketch, "E31.13.6.3", {"start": v(-65, -354) * mm, "end": v(-65, -364) * mm});
            skLineSegment(sketch, "E31.13.7.0", {"start": v(-75, -340) * mm, "end": v(-65, -340) * mm});
            skLineSegment(sketch, "E31.13.7.1", {"start": v(-75, -350) * mm, "end": v(-65, -350) * mm});
            skLineSegment(sketch, "E31.13.7.2", {"start": v(-75, -340) * mm, "end": v(-75, -350) * mm});
            skLineSegment(sketch, "E31.13.7.3", {"start": v(-65, -340) * mm, "end": v(-65, -350) * mm});
            skLineSegment(sketch, "E31.13.8.0", {"start": v(-75, -326) * mm, "end": v(-65, -326) * mm});
            skLineSegment(sketch, "E31.13.8.1", {"start": v(-75, -336) * mm, "end": v(-65, -336) * mm});
            skLineSegment(sketch, "E31.13.8.2", {"start": v(-75, -326) * mm, "end": v(-75, -336) * mm});
            skLineSegment(sketch, "E31.13.8.3", {"start": v(-65, -326) * mm, "end": v(-65, -336) * mm});
            skLineSegment(sketch, "E31.13.9.0", {"start": v(-75, -312) * mm, "end": v(-65, -312) * mm});
            skLineSegment(sketch, "E31.13.9.1", {"start": v(-75, -322) * mm, "end": v(-65, -322) * mm});
            skLineSegment(sketch, "E31.13.9.2", {"start": v(-75, -312) * mm, "end": v(-75, -322) * mm});
            skLineSegment(sketch, "E31.13.9.3", {"start": v(-65, -312) * mm, "end": v(-65, -322) * mm});
            skLineSegment(sketch, "E31.13.10.0", {"start": v(-75, -298) * mm, "end": v(-65, -298) * mm});
            skLineSegment(sketch, "E31.13.10.1", {"start": v(-75, -308) * mm, "end": v(-65, -308) * mm});
            skLineSegment(sketch, "E31.13.10.2", {"start": v(-75, -298) * mm, "end": v(-75, -308) * mm});
            skLineSegment(sketch, "E31.13.10.3", {"start": v(-65, -298) * mm, "end": v(-65, -308) * mm});
            skLineSegment(sketch, "E31.13.11.0", {"start": v(-75, -284) * mm, "end": v(-65, -284) * mm});
            skLineSegment(sketch, "E31.13.11.1", {"start": v(-75, -294) * mm, "end": v(-65, -294) * mm});
            skLineSegment(sketch, "E31.13.11.2", {"start": v(-75, -284) * mm, "end": v(-75, -294) * mm});
            skLineSegment(sketch, "E31.13.11.3", {"start": v(-65, -284) * mm, "end": v(-65, -294) * mm});
            skLineSegment(sketch, "E31.13.12.0", {"start": v(-75, -270) * mm, "end": v(-65, -270) * mm});
            skLineSegment(sketch, "E31.13.12.1", {"start": v(-75, -280) * mm, "end": v(-65, -280) * mm});
            skLineSegment(sketch, "E31.13.12.2", {"start": v(-75, -270) * mm, "end": v(-75, -280) * mm});
            skLineSegment(sketch, "E31.13.12.3", {"start": v(-65, -270) * mm, "end": v(-65, -280) * mm});
            skLineSegment(sketch, "E31.13.13.0", {"start": v(-75, -256) * mm, "end": v(-65, -256) * mm});
            skLineSegment(sketch, "E31.13.13.1", {"start": v(-75, -266) * mm, "end": v(-65, -266) * mm});
            skLineSegment(sketch, "E31.13.13.2", {"start": v(-75, -256) * mm, "end": v(-75, -266) * mm});
            skLineSegment(sketch, "E31.13.13.3", {"start": v(-65, -256) * mm, "end": v(-65, -266) * mm});
            skLineSegment(sketch, "E31.13.14.0", {"start": v(-75, -242) * mm, "end": v(-65, -242) * mm});
            skLineSegment(sketch, "E31.13.14.1", {"start": v(-75, -252) * mm, "end": v(-65, -252) * mm});
            skLineSegment(sketch, "E31.13.14.2", {"start": v(-75, -242) * mm, "end": v(-75, -252) * mm});
            skLineSegment(sketch, "E31.13.14.3", {"start": v(-65, -242) * mm, "end": v(-65, -252) * mm});
            skLineSegment(sketch, "E31.13.15.0", {"start": v(-75, -228) * mm, "end": v(-65, -228) * mm});
            skLineSegment(sketch, "E31.13.15.1", {"start": v(-75, -238) * mm, "end": v(-65, -238) * mm});
            skLineSegment(sketch, "E31.13.15.2", {"start": v(-75, -228) * mm, "end": v(-75, -238) * mm});
            skLineSegment(sketch, "E31.13.15.3", {"start": v(-65, -228) * mm, "end": v(-65, -238) * mm});
            skLineSegment(sketch, "E31.13.16.0", {"start": v(-75, -214) * mm, "end": v(-65, -214) * mm});
            skLineSegment(sketch, "E31.13.16.1", {"start": v(-75, -224) * mm, "end": v(-65, -224) * mm});
            skLineSegment(sketch, "E31.13.16.2", {"start": v(-75, -214) * mm, "end": v(-75, -224) * mm});
            skLineSegment(sketch, "E31.13.16.3", {"start": v(-65, -214) * mm, "end": v(-65, -224) * mm});
            skLineSegment(sketch, "E31.13.17.0", {"start": v(-75, -200) * mm, "end": v(-65, -200) * mm});
            skLineSegment(sketch, "E31.13.17.1", {"start": v(-75, -210) * mm, "end": v(-65, -210) * mm});
            skLineSegment(sketch, "E31.13.17.2", {"start": v(-75, -200) * mm, "end": v(-75, -210) * mm});
            skLineSegment(sketch, "E31.13.17.3", {"start": v(-65, -200) * mm, "end": v(-65, -210) * mm});
            skLineSegment(sketch, "E31.13.18.0", {"start": v(-75, -186) * mm, "end": v(-65, -186) * mm});
            skLineSegment(sketch, "E31.13.18.1", {"start": v(-75, -196) * mm, "end": v(-65, -196) * mm});
            skLineSegment(sketch, "E31.13.18.2", {"start": v(-75, -186) * mm, "end": v(-75, -196) * mm});
            skLineSegment(sketch, "E31.13.18.3", {"start": v(-65, -186) * mm, "end": v(-65, -196) * mm});
            skLineSegment(sketch, "E31.13.19.0", {"start": v(-75, -172) * mm, "end": v(-65, -172) * mm});
            skLineSegment(sketch, "E31.13.19.1", {"start": v(-75, -182) * mm, "end": v(-65, -182) * mm});
            skLineSegment(sketch, "E31.13.19.2", {"start": v(-75, -172) * mm, "end": v(-75, -182) * mm});
            skLineSegment(sketch, "E31.13.19.3", {"start": v(-65, -172) * mm, "end": v(-65, -182) * mm});
            skLineSegment(sketch, "E31.13.20.0", {"start": v(-75, -158) * mm, "end": v(-65, -158) * mm});
            skLineSegment(sketch, "E31.13.20.1", {"start": v(-75, -168) * mm, "end": v(-65, -168) * mm});
            skLineSegment(sketch, "E31.13.20.2", {"start": v(-75, -158) * mm, "end": v(-75, -168) * mm});
            skLineSegment(sketch, "E31.13.20.3", {"start": v(-65, -158) * mm, "end": v(-65, -168) * mm});
            skLineSegment(sketch, "E31.13.21.0", {"start": v(-75, -144) * mm, "end": v(-65, -144) * mm});
            skLineSegment(sketch, "E31.13.21.1", {"start": v(-75, -154) * mm, "end": v(-65, -154) * mm});
            skLineSegment(sketch, "E31.13.21.2", {"start": v(-75, -144) * mm, "end": v(-75, -154) * mm});
            skLineSegment(sketch, "E31.13.21.3", {"start": v(-65, -144) * mm, "end": v(-65, -154) * mm});
            skLineSegment(sketch, "E31.13.22.0", {"start": v(-75, -130) * mm, "end": v(-65, -130) * mm});
            skLineSegment(sketch, "E31.13.22.1", {"start": v(-75, -140) * mm, "end": v(-65, -140) * mm});
            skLineSegment(sketch, "E31.13.22.2", {"start": v(-75, -130) * mm, "end": v(-75, -140) * mm});
            skLineSegment(sketch, "E31.13.22.3", {"start": v(-65, -130) * mm, "end": v(-65, -140) * mm});
            skLineSegment(sketch, "E31.13.23.0", {"start": v(-75, -116) * mm, "end": v(-65, -116) * mm});
            skLineSegment(sketch, "E31.13.23.1", {"start": v(-75, -126) * mm, "end": v(-65, -126) * mm});
            skLineSegment(sketch, "E31.13.23.2", {"start": v(-75, -116) * mm, "end": v(-75, -126) * mm});
            skLineSegment(sketch, "E31.13.23.3", {"start": v(-65, -116) * mm, "end": v(-65, -126) * mm});
            skLineSegment(sketch, "E31.13.24.0", {"start": v(-75, -102) * mm, "end": v(-65, -102) * mm});
            skLineSegment(sketch, "E31.13.24.1", {"start": v(-75, -112) * mm, "end": v(-65, -112) * mm});
            skLineSegment(sketch, "E31.13.24.2", {"start": v(-75, -102) * mm, "end": v(-75, -112) * mm});
            skLineSegment(sketch, "E31.13.24.3", {"start": v(-65, -102) * mm, "end": v(-65, -112) * mm});
            skLineSegment(sketch, "E31.13.25.0", {"start": v(-75, -88) * mm, "end": v(-65, -88) * mm});
            skLineSegment(sketch, "E31.13.25.1", {"start": v(-75, -98) * mm, "end": v(-65, -98) * mm});
            skLineSegment(sketch, "E31.13.25.2", {"start": v(-75, -88) * mm, "end": v(-75, -98) * mm});
            skLineSegment(sketch, "E31.13.25.3", {"start": v(-65, -88) * mm, "end": v(-65, -98) * mm});
            skLineSegment(sketch, "E31.13.26.0", {"start": v(-75, -74) * mm, "end": v(-65, -74) * mm});
            skLineSegment(sketch, "E31.13.26.1", {"start": v(-75, -84) * mm, "end": v(-65, -84) * mm});
            skLineSegment(sketch, "E31.13.26.2", {"start": v(-75, -74) * mm, "end": v(-75, -84) * mm});
            skLineSegment(sketch, "E31.13.26.3", {"start": v(-65, -74) * mm, "end": v(-65, -84) * mm});
            skLineSegment(sketch, "E31.13.27.0", {"start": v(-75, -60) * mm, "end": v(-65, -60) * mm});
            skLineSegment(sketch, "E31.13.27.1", {"start": v(-75, -70) * mm, "end": v(-65, -70) * mm});
            skLineSegment(sketch, "E31.13.27.2", {"start": v(-75, -60) * mm, "end": v(-75, -70) * mm});
            skLineSegment(sketch, "E31.13.27.3", {"start": v(-65, -60) * mm, "end": v(-65, -70) * mm});
            skLineSegment(sketch, "E31.13.28.0", {"start": v(-75, -46) * mm, "end": v(-65, -46) * mm});
            skLineSegment(sketch, "E31.13.28.1", {"start": v(-75, -56) * mm, "end": v(-65, -56) * mm});
            skLineSegment(sketch, "E31.13.28.2", {"start": v(-75, -46) * mm, "end": v(-75, -56) * mm});
            skLineSegment(sketch, "E31.13.28.3", {"start": v(-65, -46) * mm, "end": v(-65, -56) * mm});
            skLineSegment(sketch, "E31.13.29.0", {"start": v(-75, -32) * mm, "end": v(-65, -32) * mm});
            skLineSegment(sketch, "E31.13.29.1", {"start": v(-75, -42) * mm, "end": v(-65, -42) * mm});
            skLineSegment(sketch, "E31.13.29.2", {"start": v(-75, -32) * mm, "end": v(-75, -42) * mm});
            skLineSegment(sketch, "E31.13.29.3", {"start": v(-65, -32) * mm, "end": v(-65, -42) * mm});
            skLineSegment(sketch, "E31.13.30.0", {"start": v(-75, -18) * mm, "end": v(-65, -18) * mm});
            skLineSegment(sketch, "E31.13.30.1", {"start": v(-75, -28) * mm, "end": v(-65, -28) * mm});
            skLineSegment(sketch, "E31.13.30.2", {"start": v(-75, -18) * mm, "end": v(-75, -28) * mm});
            skLineSegment(sketch, "E31.13.30.3", {"start": v(-65, -18) * mm, "end": v(-65, -28) * mm});
            skLineSegment(sketch, "E31.13.31.0", {"start": v(-75, -4) * mm, "end": v(-65, -4) * mm});
            skLineSegment(sketch, "E31.13.31.1", {"start": v(-75, -14) * mm, "end": v(-65, -14) * mm});
            skLineSegment(sketch, "E31.13.31.2", {"start": v(-75, -4) * mm, "end": v(-75, -14) * mm});
            skLineSegment(sketch, "E31.13.31.3", {"start": v(-65, -4) * mm, "end": v(-65, -14) * mm});
            skLineSegment(sketch, "E31.14.0.0", {"start": v(-61, -438) * mm, "end": v(-51, -438) * mm});
            skLineSegment(sketch, "E31.14.0.1", {"start": v(-61, -448) * mm, "end": v(-51, -448) * mm});
            skLineSegment(sketch, "E31.14.0.2", {"start": v(-61, -438) * mm, "end": v(-61, -448) * mm});
            skLineSegment(sketch, "E31.14.0.3", {"start": v(-51, -438) * mm, "end": v(-51, -448) * mm});
            skLineSegment(sketch, "E31.14.1.0", {"start": v(-61, -424) * mm, "end": v(-51, -424) * mm});
            skLineSegment(sketch, "E31.14.1.1", {"start": v(-61, -434) * mm, "end": v(-51, -434) * mm});
            skLineSegment(sketch, "E31.14.1.2", {"start": v(-61, -424) * mm, "end": v(-61, -434) * mm});
            skLineSegment(sketch, "E31.14.1.3", {"start": v(-51, -424) * mm, "end": v(-51, -434) * mm});
            skLineSegment(sketch, "E31.14.2.0", {"start": v(-61, -410) * mm, "end": v(-51, -410) * mm});
            skLineSegment(sketch, "E31.14.2.1", {"start": v(-61, -420) * mm, "end": v(-51, -420) * mm});
            skLineSegment(sketch, "E31.14.2.2", {"start": v(-61, -410) * mm, "end": v(-61, -420) * mm});
            skLineSegment(sketch, "E31.14.2.3", {"start": v(-51, -410) * mm, "end": v(-51, -420) * mm});
            skLineSegment(sketch, "E31.14.3.0", {"start": v(-61, -396) * mm, "end": v(-51, -396) * mm});
            skLineSegment(sketch, "E31.14.3.1", {"start": v(-61, -406) * mm, "end": v(-51, -406) * mm});
            skLineSegment(sketch, "E31.14.3.2", {"start": v(-61, -396) * mm, "end": v(-61, -406) * mm});
            skLineSegment(sketch, "E31.14.3.3", {"start": v(-51, -396) * mm, "end": v(-51, -406) * mm});
            skLineSegment(sketch, "E31.14.4.0", {"start": v(-61, -382) * mm, "end": v(-51, -382) * mm});
            skLineSegment(sketch, "E31.14.4.1", {"start": v(-61, -392) * mm, "end": v(-51, -392) * mm});
            skLineSegment(sketch, "E31.14.4.2", {"start": v(-61, -382) * mm, "end": v(-61, -392) * mm});
            skLineSegment(sketch, "E31.14.4.3", {"start": v(-51, -382) * mm, "end": v(-51, -392) * mm});
            skLineSegment(sketch, "E31.14.5.0", {"start": v(-61, -368) * mm, "end": v(-51, -368) * mm});
            skLineSegment(sketch, "E31.14.5.1", {"start": v(-61, -378) * mm, "end": v(-51, -378) * mm});
            skLineSegment(sketch, "E31.14.5.2", {"start": v(-61, -368) * mm, "end": v(-61, -378) * mm});
            skLineSegment(sketch, "E31.14.5.3", {"start": v(-51, -368) * mm, "end": v(-51, -378) * mm});
            skLineSegment(sketch, "E31.14.6.0", {"start": v(-61, -354) * mm, "end": v(-51, -354) * mm});
            skLineSegment(sketch, "E31.14.6.1", {"start": v(-61, -364) * mm, "end": v(-51, -364) * mm});
            skLineSegment(sketch, "E31.14.6.2", {"start": v(-61, -354) * mm, "end": v(-61, -364) * mm});
            skLineSegment(sketch, "E31.14.6.3", {"start": v(-51, -354) * mm, "end": v(-51, -364) * mm});
            skLineSegment(sketch, "E31.14.7.0", {"start": v(-61, -340) * mm, "end": v(-51, -340) * mm});
            skLineSegment(sketch, "E31.14.7.1", {"start": v(-61, -350) * mm, "end": v(-51, -350) * mm});
            skLineSegment(sketch, "E31.14.7.2", {"start": v(-61, -340) * mm, "end": v(-61, -350) * mm});
            skLineSegment(sketch, "E31.14.7.3", {"start": v(-51, -340) * mm, "end": v(-51, -350) * mm});
            skLineSegment(sketch, "E31.14.8.0", {"start": v(-61, -326) * mm, "end": v(-51, -326) * mm});
            skLineSegment(sketch, "E31.14.8.1", {"start": v(-61, -336) * mm, "end": v(-51, -336) * mm});
            skLineSegment(sketch, "E31.14.8.2", {"start": v(-61, -326) * mm, "end": v(-61, -336) * mm});
            skLineSegment(sketch, "E31.14.8.3", {"start": v(-51, -326) * mm, "end": v(-51, -336) * mm});
            skLineSegment(sketch, "E31.14.9.0", {"start": v(-61, -312) * mm, "end": v(-51, -312) * mm});
            skLineSegment(sketch, "E31.14.9.1", {"start": v(-61, -322) * mm, "end": v(-51, -322) * mm});
            skLineSegment(sketch, "E31.14.9.2", {"start": v(-61, -312) * mm, "end": v(-61, -322) * mm});
            skLineSegment(sketch, "E31.14.9.3", {"start": v(-51, -312) * mm, "end": v(-51, -322) * mm});
            skLineSegment(sketch, "E31.14.10.0", {"start": v(-61, -298) * mm, "end": v(-51, -298) * mm});
            skLineSegment(sketch, "E31.14.10.1", {"start": v(-61, -308) * mm, "end": v(-51, -308) * mm});
            skLineSegment(sketch, "E31.14.10.2", {"start": v(-61, -298) * mm, "end": v(-61, -308) * mm});
            skLineSegment(sketch, "E31.14.10.3", {"start": v(-51, -298) * mm, "end": v(-51, -308) * mm});
            skLineSegment(sketch, "E31.14.11.0", {"start": v(-61, -284) * mm, "end": v(-51, -284) * mm});
            skLineSegment(sketch, "E31.14.11.1", {"start": v(-61, -294) * mm, "end": v(-51, -294) * mm});
            skLineSegment(sketch, "E31.14.11.2", {"start": v(-61, -284) * mm, "end": v(-61, -294) * mm});
            skLineSegment(sketch, "E31.14.11.3", {"start": v(-51, -284) * mm, "end": v(-51, -294) * mm});
            skLineSegment(sketch, "E31.14.12.0", {"start": v(-61, -270) * mm, "end": v(-51, -270) * mm});
            skLineSegment(sketch, "E31.14.12.1", {"start": v(-61, -280) * mm, "end": v(-51, -280) * mm});
            skLineSegment(sketch, "E31.14.12.2", {"start": v(-61, -270) * mm, "end": v(-61, -280) * mm});
            skLineSegment(sketch, "E31.14.12.3", {"start": v(-51, -270) * mm, "end": v(-51, -280) * mm});
            skLineSegment(sketch, "E31.14.13.0", {"start": v(-61, -256) * mm, "end": v(-51, -256) * mm});
            skLineSegment(sketch, "E31.14.13.1", {"start": v(-61, -266) * mm, "end": v(-51, -266) * mm});
            skLineSegment(sketch, "E31.14.13.2", {"start": v(-61, -256) * mm, "end": v(-61, -266) * mm});
            skLineSegment(sketch, "E31.14.13.3", {"start": v(-51, -256) * mm, "end": v(-51, -266) * mm});
            skLineSegment(sketch, "E31.14.14.0", {"start": v(-61, -242) * mm, "end": v(-51, -242) * mm});
            skLineSegment(sketch, "E31.14.14.1", {"start": v(-61, -252) * mm, "end": v(-51, -252) * mm});
            skLineSegment(sketch, "E31.14.14.2", {"start": v(-61, -242) * mm, "end": v(-61, -252) * mm});
            skLineSegment(sketch, "E31.14.14.3", {"start": v(-51, -242) * mm, "end": v(-51, -252) * mm});
            skLineSegment(sketch, "E31.14.15.0", {"start": v(-61, -228) * mm, "end": v(-51, -228) * mm});
            skLineSegment(sketch, "E31.14.15.1", {"start": v(-61, -238) * mm, "end": v(-51, -238) * mm});
            skLineSegment(sketch, "E31.14.15.2", {"start": v(-61, -228) * mm, "end": v(-61, -238) * mm});
            skLineSegment(sketch, "E31.14.15.3", {"start": v(-51, -228) * mm, "end": v(-51, -238) * mm});
            skLineSegment(sketch, "E31.14.16.0", {"start": v(-61, -214) * mm, "end": v(-51, -214) * mm});
            skLineSegment(sketch, "E31.14.16.1", {"start": v(-61, -224) * mm, "end": v(-51, -224) * mm});
            skLineSegment(sketch, "E31.14.16.2", {"start": v(-61, -214) * mm, "end": v(-61, -224) * mm});
            skLineSegment(sketch, "E31.14.16.3", {"start": v(-51, -214) * mm, "end": v(-51, -224) * mm});
            skLineSegment(sketch, "E31.14.17.0", {"start": v(-61, -200) * mm, "end": v(-51, -200) * mm});
            skLineSegment(sketch, "E31.14.17.1", {"start": v(-61, -210) * mm, "end": v(-51, -210) * mm});
            skLineSegment(sketch, "E31.14.17.2", {"start": v(-61, -200) * mm, "end": v(-61, -210) * mm});
            skLineSegment(sketch, "E31.14.17.3", {"start": v(-51, -200) * mm, "end": v(-51, -210) * mm});
            skLineSegment(sketch, "E31.14.18.0", {"start": v(-61, -186) * mm, "end": v(-51, -186) * mm});
            skLineSegment(sketch, "E31.14.18.1", {"start": v(-61, -196) * mm, "end": v(-51, -196) * mm});
            skLineSegment(sketch, "E31.14.18.2", {"start": v(-61, -186) * mm, "end": v(-61, -196) * mm});
            skLineSegment(sketch, "E31.14.18.3", {"start": v(-51, -186) * mm, "end": v(-51, -196) * mm});
            skLineSegment(sketch, "E31.14.19.0", {"start": v(-61, -172) * mm, "end": v(-51, -172) * mm});
            skLineSegment(sketch, "E31.14.19.1", {"start": v(-61, -182) * mm, "end": v(-51, -182) * mm});
            skLineSegment(sketch, "E31.14.19.2", {"start": v(-61, -172) * mm, "end": v(-61, -182) * mm});
            skLineSegment(sketch, "E31.14.19.3", {"start": v(-51, -172) * mm, "end": v(-51, -182) * mm});
            skLineSegment(sketch, "E31.14.20.0", {"start": v(-61, -158) * mm, "end": v(-51, -158) * mm});
            skLineSegment(sketch, "E31.14.20.1", {"start": v(-61, -168) * mm, "end": v(-51, -168) * mm});
            skLineSegment(sketch, "E31.14.20.2", {"start": v(-61, -158) * mm, "end": v(-61, -168) * mm});
            skLineSegment(sketch, "E31.14.20.3", {"start": v(-51, -158) * mm, "end": v(-51, -168) * mm});
            skLineSegment(sketch, "E31.14.21.0", {"start": v(-61, -144) * mm, "end": v(-51, -144) * mm});
            skLineSegment(sketch, "E31.14.21.1", {"start": v(-61, -154) * mm, "end": v(-51, -154) * mm});
            skLineSegment(sketch, "E31.14.21.2", {"start": v(-61, -144) * mm, "end": v(-61, -154) * mm});
            skLineSegment(sketch, "E31.14.21.3", {"start": v(-51, -144) * mm, "end": v(-51, -154) * mm});
            skLineSegment(sketch, "E31.14.22.0", {"start": v(-61, -130) * mm, "end": v(-51, -130) * mm});
            skLineSegment(sketch, "E31.14.22.1", {"start": v(-61, -140) * mm, "end": v(-51, -140) * mm});
            skLineSegment(sketch, "E31.14.22.2", {"start": v(-61, -130) * mm, "end": v(-61, -140) * mm});
            skLineSegment(sketch, "E31.14.22.3", {"start": v(-51, -130) * mm, "end": v(-51, -140) * mm});
            skLineSegment(sketch, "E31.14.23.0", {"start": v(-61, -116) * mm, "end": v(-51, -116) * mm});
            skLineSegment(sketch, "E31.14.23.1", {"start": v(-61, -126) * mm, "end": v(-51, -126) * mm});
            skLineSegment(sketch, "E31.14.23.2", {"start": v(-61, -116) * mm, "end": v(-61, -126) * mm});
            skLineSegment(sketch, "E31.14.23.3", {"start": v(-51, -116) * mm, "end": v(-51, -126) * mm});
            skLineSegment(sketch, "E31.14.24.0", {"start": v(-61, -102) * mm, "end": v(-51, -102) * mm});
            skLineSegment(sketch, "E31.14.24.1", {"start": v(-61, -112) * mm, "end": v(-51, -112) * mm});
            skLineSegment(sketch, "E31.14.24.2", {"start": v(-61, -102) * mm, "end": v(-61, -112) * mm});
            skLineSegment(sketch, "E31.14.24.3", {"start": v(-51, -102) * mm, "end": v(-51, -112) * mm});
            skLineSegment(sketch, "E31.14.25.0", {"start": v(-61, -88) * mm, "end": v(-51, -88) * mm});
            skLineSegment(sketch, "E31.14.25.1", {"start": v(-61, -98) * mm, "end": v(-51, -98) * mm});
            skLineSegment(sketch, "E31.14.25.2", {"start": v(-61, -88) * mm, "end": v(-61, -98) * mm});
            skLineSegment(sketch, "E31.14.25.3", {"start": v(-51, -88) * mm, "end": v(-51, -98) * mm});
            skLineSegment(sketch, "E31.14.26.0", {"start": v(-61, -74) * mm, "end": v(-51, -74) * mm});
            skLineSegment(sketch, "E31.14.26.1", {"start": v(-61, -84) * mm, "end": v(-51, -84) * mm});
            skLineSegment(sketch, "E31.14.26.2", {"start": v(-61, -74) * mm, "end": v(-61, -84) * mm});
            skLineSegment(sketch, "E31.14.26.3", {"start": v(-51, -74) * mm, "end": v(-51, -84) * mm});
            skLineSegment(sketch, "E31.14.27.0", {"start": v(-61, -60) * mm, "end": v(-51, -60) * mm});
            skLineSegment(sketch, "E31.14.27.1", {"start": v(-61, -70) * mm, "end": v(-51, -70) * mm});
            skLineSegment(sketch, "E31.14.27.2", {"start": v(-61, -60) * mm, "end": v(-61, -70) * mm});
            skLineSegment(sketch, "E31.14.27.3", {"start": v(-51, -60) * mm, "end": v(-51, -70) * mm});
            skLineSegment(sketch, "E31.14.28.0", {"start": v(-61, -46) * mm, "end": v(-51, -46) * mm});
            skLineSegment(sketch, "E31.14.28.1", {"start": v(-61, -56) * mm, "end": v(-51, -56) * mm});
            skLineSegment(sketch, "E31.14.28.2", {"start": v(-61, -46) * mm, "end": v(-61, -56) * mm});
            skLineSegment(sketch, "E31.14.28.3", {"start": v(-51, -46) * mm, "end": v(-51, -56) * mm});
            skLineSegment(sketch, "E31.14.29.0", {"start": v(-61, -32) * mm, "end": v(-51, -32) * mm});
            skLineSegment(sketch, "E31.14.29.1", {"start": v(-61, -42) * mm, "end": v(-51, -42) * mm});
            skLineSegment(sketch, "E31.14.29.2", {"start": v(-61, -32) * mm, "end": v(-61, -42) * mm});
            skLineSegment(sketch, "E31.14.29.3", {"start": v(-51, -32) * mm, "end": v(-51, -42) * mm});
            skLineSegment(sketch, "E31.14.30.0", {"start": v(-61, -18) * mm, "end": v(-51, -18) * mm});
            skLineSegment(sketch, "E31.14.30.1", {"start": v(-61, -28) * mm, "end": v(-51, -28) * mm});
            skLineSegment(sketch, "E31.14.30.2", {"start": v(-61, -18) * mm, "end": v(-61, -28) * mm});
            skLineSegment(sketch, "E31.14.30.3", {"start": v(-51, -18) * mm, "end": v(-51, -28) * mm});
            skLineSegment(sketch, "E31.14.31.0", {"start": v(-61, -4) * mm, "end": v(-51, -4) * mm});
            skLineSegment(sketch, "E31.14.31.1", {"start": v(-61, -14) * mm, "end": v(-51, -14) * mm});
            skLineSegment(sketch, "E31.14.31.2", {"start": v(-61, -4) * mm, "end": v(-61, -14) * mm});
            skLineSegment(sketch, "E31.14.31.3", {"start": v(-51, -4) * mm, "end": v(-51, -14) * mm});
            skLineSegment(sketch, "E31.15.0.0", {"start": v(-47, -438) * mm, "end": v(-37, -438) * mm});
            skLineSegment(sketch, "E31.15.0.1", {"start": v(-47, -448) * mm, "end": v(-37, -448) * mm});
            skLineSegment(sketch, "E31.15.0.2", {"start": v(-47, -438) * mm, "end": v(-47, -448) * mm});
            skLineSegment(sketch, "E31.15.0.3", {"start": v(-37, -438) * mm, "end": v(-37, -448) * mm});
            skLineSegment(sketch, "E31.15.1.0", {"start": v(-47, -424) * mm, "end": v(-37, -424) * mm});
            skLineSegment(sketch, "E31.15.1.1", {"start": v(-47, -434) * mm, "end": v(-37, -434) * mm});
            skLineSegment(sketch, "E31.15.1.2", {"start": v(-47, -424) * mm, "end": v(-47, -434) * mm});
            skLineSegment(sketch, "E31.15.1.3", {"start": v(-37, -424) * mm, "end": v(-37, -434) * mm});
            skLineSegment(sketch, "E31.15.2.0", {"start": v(-47, -410) * mm, "end": v(-37, -410) * mm});
            skLineSegment(sketch, "E31.15.2.1", {"start": v(-47, -420) * mm, "end": v(-37, -420) * mm});
            skLineSegment(sketch, "E31.15.2.2", {"start": v(-47, -410) * mm, "end": v(-47, -420) * mm});
            skLineSegment(sketch, "E31.15.2.3", {"start": v(-37, -410) * mm, "end": v(-37, -420) * mm});
            skLineSegment(sketch, "E31.15.3.0", {"start": v(-47, -396) * mm, "end": v(-37, -396) * mm});
            skLineSegment(sketch, "E31.15.3.1", {"start": v(-47, -406) * mm, "end": v(-37, -406) * mm});
            skLineSegment(sketch, "E31.15.3.2", {"start": v(-47, -396) * mm, "end": v(-47, -406) * mm});
            skLineSegment(sketch, "E31.15.3.3", {"start": v(-37, -396) * mm, "end": v(-37, -406) * mm});
            skLineSegment(sketch, "E31.15.4.0", {"start": v(-47, -382) * mm, "end": v(-37, -382) * mm});
            skLineSegment(sketch, "E31.15.4.1", {"start": v(-47, -392) * mm, "end": v(-37, -392) * mm});
            skLineSegment(sketch, "E31.15.4.2", {"start": v(-47, -382) * mm, "end": v(-47, -392) * mm});
            skLineSegment(sketch, "E31.15.4.3", {"start": v(-37, -382) * mm, "end": v(-37, -392) * mm});
            skLineSegment(sketch, "E31.15.5.0", {"start": v(-47, -368) * mm, "end": v(-37, -368) * mm});
            skLineSegment(sketch, "E31.15.5.1", {"start": v(-47, -378) * mm, "end": v(-37, -378) * mm});
            skLineSegment(sketch, "E31.15.5.2", {"start": v(-47, -368) * mm, "end": v(-47, -378) * mm});
            skLineSegment(sketch, "E31.15.5.3", {"start": v(-37, -368) * mm, "end": v(-37, -378) * mm});
            skLineSegment(sketch, "E31.15.6.0", {"start": v(-47, -354) * mm, "end": v(-37, -354) * mm});
            skLineSegment(sketch, "E31.15.6.1", {"start": v(-47, -364) * mm, "end": v(-37, -364) * mm});
            skLineSegment(sketch, "E31.15.6.2", {"start": v(-47, -354) * mm, "end": v(-47, -364) * mm});
            skLineSegment(sketch, "E31.15.6.3", {"start": v(-37, -354) * mm, "end": v(-37, -364) * mm});
            skLineSegment(sketch, "E31.15.7.0", {"start": v(-47, -340) * mm, "end": v(-37, -340) * mm});
            skLineSegment(sketch, "E31.15.7.1", {"start": v(-47, -350) * mm, "end": v(-37, -350) * mm});
            skLineSegment(sketch, "E31.15.7.2", {"start": v(-47, -340) * mm, "end": v(-47, -350) * mm});
            skLineSegment(sketch, "E31.15.7.3", {"start": v(-37, -340) * mm, "end": v(-37, -350) * mm});
            skLineSegment(sketch, "E31.15.8.0", {"start": v(-47, -326) * mm, "end": v(-37, -326) * mm});
            skLineSegment(sketch, "E31.15.8.1", {"start": v(-47, -336) * mm, "end": v(-37, -336) * mm});
            skLineSegment(sketch, "E31.15.8.2", {"start": v(-47, -326) * mm, "end": v(-47, -336) * mm});
            skLineSegment(sketch, "E31.15.8.3", {"start": v(-37, -326) * mm, "end": v(-37, -336) * mm});
            skLineSegment(sketch, "E31.15.9.0", {"start": v(-47, -312) * mm, "end": v(-37, -312) * mm});
            skLineSegment(sketch, "E31.15.9.1", {"start": v(-47, -322) * mm, "end": v(-37, -322) * mm});
            skLineSegment(sketch, "E31.15.9.2", {"start": v(-47, -312) * mm, "end": v(-47, -322) * mm});
            skLineSegment(sketch, "E31.15.9.3", {"start": v(-37, -312) * mm, "end": v(-37, -322) * mm});
            skLineSegment(sketch, "E31.15.10.0", {"start": v(-47, -298) * mm, "end": v(-37, -298) * mm});
            skLineSegment(sketch, "E31.15.10.1", {"start": v(-47, -308) * mm, "end": v(-37, -308) * mm});
            skLineSegment(sketch, "E31.15.10.2", {"start": v(-47, -298) * mm, "end": v(-47, -308) * mm});
            skLineSegment(sketch, "E31.15.10.3", {"start": v(-37, -298) * mm, "end": v(-37, -308) * mm});
            skLineSegment(sketch, "E31.15.11.0", {"start": v(-47, -284) * mm, "end": v(-37, -284) * mm});
            skLineSegment(sketch, "E31.15.11.1", {"start": v(-47, -294) * mm, "end": v(-37, -294) * mm});
            skLineSegment(sketch, "E31.15.11.2", {"start": v(-47, -284) * mm, "end": v(-47, -294) * mm});
            skLineSegment(sketch, "E31.15.11.3", {"start": v(-37, -284) * mm, "end": v(-37, -294) * mm});
            skLineSegment(sketch, "E31.15.12.0", {"start": v(-47, -270) * mm, "end": v(-37, -270) * mm});
            skLineSegment(sketch, "E31.15.12.1", {"start": v(-47, -280) * mm, "end": v(-37, -280) * mm});
            skLineSegment(sketch, "E31.15.12.2", {"start": v(-47, -270) * mm, "end": v(-47, -280) * mm});
            skLineSegment(sketch, "E31.15.12.3", {"start": v(-37, -270) * mm, "end": v(-37, -280) * mm});
            skLineSegment(sketch, "E31.15.13.0", {"start": v(-47, -256) * mm, "end": v(-37, -256) * mm});
            skLineSegment(sketch, "E31.15.13.1", {"start": v(-47, -266) * mm, "end": v(-37, -266) * mm});
            skLineSegment(sketch, "E31.15.13.2", {"start": v(-47, -256) * mm, "end": v(-47, -266) * mm});
            skLineSegment(sketch, "E31.15.13.3", {"start": v(-37, -256) * mm, "end": v(-37, -266) * mm});
            skLineSegment(sketch, "E31.15.14.0", {"start": v(-47, -242) * mm, "end": v(-37, -242) * mm});
            skLineSegment(sketch, "E31.15.14.1", {"start": v(-47, -252) * mm, "end": v(-37, -252) * mm});
            skLineSegment(sketch, "E31.15.14.2", {"start": v(-47, -242) * mm, "end": v(-47, -252) * mm});
            skLineSegment(sketch, "E31.15.14.3", {"start": v(-37, -242) * mm, "end": v(-37, -252) * mm});
            skLineSegment(sketch, "E31.15.15.0", {"start": v(-47, -228) * mm, "end": v(-37, -228) * mm});
            skLineSegment(sketch, "E31.15.15.1", {"start": v(-47, -238) * mm, "end": v(-37, -238) * mm});
            skLineSegment(sketch, "E31.15.15.2", {"start": v(-47, -228) * mm, "end": v(-47, -238) * mm});
            skLineSegment(sketch, "E31.15.15.3", {"start": v(-37, -228) * mm, "end": v(-37, -238) * mm});
            skLineSegment(sketch, "E31.15.16.0", {"start": v(-47, -214) * mm, "end": v(-37, -214) * mm});
            skLineSegment(sketch, "E31.15.16.1", {"start": v(-47, -224) * mm, "end": v(-37, -224) * mm});
            skLineSegment(sketch, "E31.15.16.2", {"start": v(-47, -214) * mm, "end": v(-47, -224) * mm});
            skLineSegment(sketch, "E31.15.16.3", {"start": v(-37, -214) * mm, "end": v(-37, -224) * mm});
            skLineSegment(sketch, "E31.15.17.0", {"start": v(-47, -200) * mm, "end": v(-37, -200) * mm});
            skLineSegment(sketch, "E31.15.17.1", {"start": v(-47, -210) * mm, "end": v(-37, -210) * mm});
            skLineSegment(sketch, "E31.15.17.2", {"start": v(-47, -200) * mm, "end": v(-47, -210) * mm});
            skLineSegment(sketch, "E31.15.17.3", {"start": v(-37, -200) * mm, "end": v(-37, -210) * mm});
            skLineSegment(sketch, "E31.15.18.0", {"start": v(-47, -186) * mm, "end": v(-37, -186) * mm});
            skLineSegment(sketch, "E31.15.18.1", {"start": v(-47, -196) * mm, "end": v(-37, -196) * mm});
            skLineSegment(sketch, "E31.15.18.2", {"start": v(-47, -186) * mm, "end": v(-47, -196) * mm});
            skLineSegment(sketch, "E31.15.18.3", {"start": v(-37, -186) * mm, "end": v(-37, -196) * mm});
            skLineSegment(sketch, "E31.15.19.0", {"start": v(-47, -172) * mm, "end": v(-37, -172) * mm});
            skLineSegment(sketch, "E31.15.19.1", {"start": v(-47, -182) * mm, "end": v(-37, -182) * mm});
            skLineSegment(sketch, "E31.15.19.2", {"start": v(-47, -172) * mm, "end": v(-47, -182) * mm});
            skLineSegment(sketch, "E31.15.19.3", {"start": v(-37, -172) * mm, "end": v(-37, -182) * mm});
            skLineSegment(sketch, "E31.15.20.0", {"start": v(-47, -158) * mm, "end": v(-37, -158) * mm});
            skLineSegment(sketch, "E31.15.20.1", {"start": v(-47, -168) * mm, "end": v(-37, -168) * mm});
            skLineSegment(sketch, "E31.15.20.2", {"start": v(-47, -158) * mm, "end": v(-47, -168) * mm});
            skLineSegment(sketch, "E31.15.20.3", {"start": v(-37, -158) * mm, "end": v(-37, -168) * mm});
            skLineSegment(sketch, "E31.15.21.0", {"start": v(-47, -144) * mm, "end": v(-37, -144) * mm});
            skLineSegment(sketch, "E31.15.21.1", {"start": v(-47, -154) * mm, "end": v(-37, -154) * mm});
            skLineSegment(sketch, "E31.15.21.2", {"start": v(-47, -144) * mm, "end": v(-47, -154) * mm});
            skLineSegment(sketch, "E31.15.21.3", {"start": v(-37, -144) * mm, "end": v(-37, -154) * mm});
            skLineSegment(sketch, "E31.15.22.0", {"start": v(-47, -130) * mm, "end": v(-37, -130) * mm});
            skLineSegment(sketch, "E31.15.22.1", {"start": v(-47, -140) * mm, "end": v(-37, -140) * mm});
            skLineSegment(sketch, "E31.15.22.2", {"start": v(-47, -130) * mm, "end": v(-47, -140) * mm});
            skLineSegment(sketch, "E31.15.22.3", {"start": v(-37, -130) * mm, "end": v(-37, -140) * mm});
            skLineSegment(sketch, "E31.15.23.0", {"start": v(-47, -116) * mm, "end": v(-37, -116) * mm});
            skLineSegment(sketch, "E31.15.23.1", {"start": v(-47, -126) * mm, "end": v(-37, -126) * mm});
            skLineSegment(sketch, "E31.15.23.2", {"start": v(-47, -116) * mm, "end": v(-47, -126) * mm});
            skLineSegment(sketch, "E31.15.23.3", {"start": v(-37, -116) * mm, "end": v(-37, -126) * mm});
            skLineSegment(sketch, "E31.15.24.0", {"start": v(-47, -102) * mm, "end": v(-37, -102) * mm});
            skLineSegment(sketch, "E31.15.24.1", {"start": v(-47, -112) * mm, "end": v(-37, -112) * mm});
            skLineSegment(sketch, "E31.15.24.2", {"start": v(-47, -102) * mm, "end": v(-47, -112) * mm});
            skLineSegment(sketch, "E31.15.24.3", {"start": v(-37, -102) * mm, "end": v(-37, -112) * mm});
            skLineSegment(sketch, "E31.15.25.0", {"start": v(-47, -88) * mm, "end": v(-37, -88) * mm});
            skLineSegment(sketch, "E31.15.25.1", {"start": v(-47, -98) * mm, "end": v(-37, -98) * mm});
            skLineSegment(sketch, "E31.15.25.2", {"start": v(-47, -88) * mm, "end": v(-47, -98) * mm});
            skLineSegment(sketch, "E31.15.25.3", {"start": v(-37, -88) * mm, "end": v(-37, -98) * mm});
            skLineSegment(sketch, "E31.15.26.0", {"start": v(-47, -74) * mm, "end": v(-37, -74) * mm});
            skLineSegment(sketch, "E31.15.26.1", {"start": v(-47, -84) * mm, "end": v(-37, -84) * mm});
            skLineSegment(sketch, "E31.15.26.2", {"start": v(-47, -74) * mm, "end": v(-47, -84) * mm});
            skLineSegment(sketch, "E31.15.26.3", {"start": v(-37, -74) * mm, "end": v(-37, -84) * mm});
            skLineSegment(sketch, "E31.15.27.0", {"start": v(-47, -60) * mm, "end": v(-37, -60) * mm});
            skLineSegment(sketch, "E31.15.27.1", {"start": v(-47, -70) * mm, "end": v(-37, -70) * mm});
            skLineSegment(sketch, "E31.15.27.2", {"start": v(-47, -60) * mm, "end": v(-47, -70) * mm});
            skLineSegment(sketch, "E31.15.27.3", {"start": v(-37, -60) * mm, "end": v(-37, -70) * mm});
            skLineSegment(sketch, "E31.15.28.0", {"start": v(-47, -46) * mm, "end": v(-37, -46) * mm});
            skLineSegment(sketch, "E31.15.28.1", {"start": v(-47, -56) * mm, "end": v(-37, -56) * mm});
            skLineSegment(sketch, "E31.15.28.2", {"start": v(-47, -46) * mm, "end": v(-47, -56) * mm});
            skLineSegment(sketch, "E31.15.28.3", {"start": v(-37, -46) * mm, "end": v(-37, -56) * mm});
            skLineSegment(sketch, "E31.15.29.0", {"start": v(-47, -32) * mm, "end": v(-37, -32) * mm});
            skLineSegment(sketch, "E31.15.29.1", {"start": v(-47, -42) * mm, "end": v(-37, -42) * mm});
            skLineSegment(sketch, "E31.15.29.2", {"start": v(-47, -32) * mm, "end": v(-47, -42) * mm});
            skLineSegment(sketch, "E31.15.29.3", {"start": v(-37, -32) * mm, "end": v(-37, -42) * mm});
            skLineSegment(sketch, "E31.15.30.0", {"start": v(-47, -18) * mm, "end": v(-37, -18) * mm});
            skLineSegment(sketch, "E31.15.30.1", {"start": v(-47, -28) * mm, "end": v(-37, -28) * mm});
            skLineSegment(sketch, "E31.15.30.2", {"start": v(-47, -18) * mm, "end": v(-47, -28) * mm});
            skLineSegment(sketch, "E31.15.30.3", {"start": v(-37, -18) * mm, "end": v(-37, -28) * mm});
            skLineSegment(sketch, "E31.15.31.0", {"start": v(-47, -4) * mm, "end": v(-37, -4) * mm});
            skLineSegment(sketch, "E31.15.31.1", {"start": v(-47, -14) * mm, "end": v(-37, -14) * mm});
            skLineSegment(sketch, "E31.15.31.2", {"start": v(-47, -4) * mm, "end": v(-47, -14) * mm});
            skLineSegment(sketch, "E31.15.31.3", {"start": v(-37, -4) * mm, "end": v(-37, -14) * mm});
            skLineSegment(sketch, "E31.16.0.0", {"start": v(-33, -438) * mm, "end": v(-23, -438) * mm});
            skLineSegment(sketch, "E31.16.0.1", {"start": v(-33, -448) * mm, "end": v(-23, -448) * mm});
            skLineSegment(sketch, "E31.16.0.2", {"start": v(-33, -438) * mm, "end": v(-33, -448) * mm});
            skLineSegment(sketch, "E31.16.0.3", {"start": v(-23, -438) * mm, "end": v(-23, -448) * mm});
            skLineSegment(sketch, "E31.16.1.0", {"start": v(-33, -424) * mm, "end": v(-23, -424) * mm});
            skLineSegment(sketch, "E31.16.1.1", {"start": v(-33, -434) * mm, "end": v(-23, -434) * mm});
            skLineSegment(sketch, "E31.16.1.2", {"start": v(-33, -424) * mm, "end": v(-33, -434) * mm});
            skLineSegment(sketch, "E31.16.1.3", {"start": v(-23, -424) * mm, "end": v(-23, -434) * mm});
            skLineSegment(sketch, "E31.16.2.0", {"start": v(-33, -410) * mm, "end": v(-23, -410) * mm});
            skLineSegment(sketch, "E31.16.2.1", {"start": v(-33, -420) * mm, "end": v(-23, -420) * mm});
            skLineSegment(sketch, "E31.16.2.2", {"start": v(-33, -410) * mm, "end": v(-33, -420) * mm});
            skLineSegment(sketch, "E31.16.2.3", {"start": v(-23, -410) * mm, "end": v(-23, -420) * mm});
            skLineSegment(sketch, "E31.16.3.0", {"start": v(-33, -396) * mm, "end": v(-23, -396) * mm});
            skLineSegment(sketch, "E31.16.3.1", {"start": v(-33, -406) * mm, "end": v(-23, -406) * mm});
            skLineSegment(sketch, "E31.16.3.2", {"start": v(-33, -396) * mm, "end": v(-33, -406) * mm});
            skLineSegment(sketch, "E31.16.3.3", {"start": v(-23, -396) * mm, "end": v(-23, -406) * mm});
            skLineSegment(sketch, "E31.16.4.0", {"start": v(-33, -382) * mm, "end": v(-23, -382) * mm});
            skLineSegment(sketch, "E31.16.4.1", {"start": v(-33, -392) * mm, "end": v(-23, -392) * mm});
            skLineSegment(sketch, "E31.16.4.2", {"start": v(-33, -382) * mm, "end": v(-33, -392) * mm});
            skLineSegment(sketch, "E31.16.4.3", {"start": v(-23, -382) * mm, "end": v(-23, -392) * mm});
            skLineSegment(sketch, "E31.16.5.0", {"start": v(-33, -368) * mm, "end": v(-23, -368) * mm});
            skLineSegment(sketch, "E31.16.5.1", {"start": v(-33, -378) * mm, "end": v(-23, -378) * mm});
            skLineSegment(sketch, "E31.16.5.2", {"start": v(-33, -368) * mm, "end": v(-33, -378) * mm});
            skLineSegment(sketch, "E31.16.5.3", {"start": v(-23, -368) * mm, "end": v(-23, -378) * mm});
            skLineSegment(sketch, "E31.16.6.0", {"start": v(-33, -354) * mm, "end": v(-23, -354) * mm});
            skLineSegment(sketch, "E31.16.6.1", {"start": v(-33, -364) * mm, "end": v(-23, -364) * mm});
            skLineSegment(sketch, "E31.16.6.2", {"start": v(-33, -354) * mm, "end": v(-33, -364) * mm});
            skLineSegment(sketch, "E31.16.6.3", {"start": v(-23, -354) * mm, "end": v(-23, -364) * mm});
            skLineSegment(sketch, "E31.16.7.0", {"start": v(-33, -340) * mm, "end": v(-23, -340) * mm});
            skLineSegment(sketch, "E31.16.7.1", {"start": v(-33, -350) * mm, "end": v(-23, -350) * mm});
            skLineSegment(sketch, "E31.16.7.2", {"start": v(-33, -340) * mm, "end": v(-33, -350) * mm});
            skLineSegment(sketch, "E31.16.7.3", {"start": v(-23, -340) * mm, "end": v(-23, -350) * mm});
            skLineSegment(sketch, "E31.16.8.0", {"start": v(-33, -326) * mm, "end": v(-23, -326) * mm});
            skLineSegment(sketch, "E31.16.8.1", {"start": v(-33, -336) * mm, "end": v(-23, -336) * mm});
            skLineSegment(sketch, "E31.16.8.2", {"start": v(-33, -326) * mm, "end": v(-33, -336) * mm});
            skLineSegment(sketch, "E31.16.8.3", {"start": v(-23, -326) * mm, "end": v(-23, -336) * mm});
            skLineSegment(sketch, "E31.16.9.0", {"start": v(-33, -312) * mm, "end": v(-23, -312) * mm});
            skLineSegment(sketch, "E31.16.9.1", {"start": v(-33, -322) * mm, "end": v(-23, -322) * mm});
            skLineSegment(sketch, "E31.16.9.2", {"start": v(-33, -312) * mm, "end": v(-33, -322) * mm});
            skLineSegment(sketch, "E31.16.9.3", {"start": v(-23, -312) * mm, "end": v(-23, -322) * mm});
            skLineSegment(sketch, "E31.16.10.0", {"start": v(-33, -298) * mm, "end": v(-23, -298) * mm});
            skLineSegment(sketch, "E31.16.10.1", {"start": v(-33, -308) * mm, "end": v(-23, -308) * mm});
            skLineSegment(sketch, "E31.16.10.2", {"start": v(-33, -298) * mm, "end": v(-33, -308) * mm});
            skLineSegment(sketch, "E31.16.10.3", {"start": v(-23, -298) * mm, "end": v(-23, -308) * mm});
            skLineSegment(sketch, "E31.16.11.0", {"start": v(-33, -284) * mm, "end": v(-23, -284) * mm});
            skLineSegment(sketch, "E31.16.11.1", {"start": v(-33, -294) * mm, "end": v(-23, -294) * mm});
            skLineSegment(sketch, "E31.16.11.2", {"start": v(-33, -284) * mm, "end": v(-33, -294) * mm});
            skLineSegment(sketch, "E31.16.11.3", {"start": v(-23, -284) * mm, "end": v(-23, -294) * mm});
            skLineSegment(sketch, "E31.16.12.0", {"start": v(-33, -270) * mm, "end": v(-23, -270) * mm});
            skLineSegment(sketch, "E31.16.12.1", {"start": v(-33, -280) * mm, "end": v(-23, -280) * mm});
            skLineSegment(sketch, "E31.16.12.2", {"start": v(-33, -270) * mm, "end": v(-33, -280) * mm});
            skLineSegment(sketch, "E31.16.12.3", {"start": v(-23, -270) * mm, "end": v(-23, -280) * mm});
            skLineSegment(sketch, "E31.16.13.0", {"start": v(-33, -256) * mm, "end": v(-23, -256) * mm});
            skLineSegment(sketch, "E31.16.13.1", {"start": v(-33, -266) * mm, "end": v(-23, -266) * mm});
            skLineSegment(sketch, "E31.16.13.2", {"start": v(-33, -256) * mm, "end": v(-33, -266) * mm});
            skLineSegment(sketch, "E31.16.13.3", {"start": v(-23, -256) * mm, "end": v(-23, -266) * mm});
            skLineSegment(sketch, "E31.16.14.0", {"start": v(-33, -242) * mm, "end": v(-23, -242) * mm});
            skLineSegment(sketch, "E31.16.14.1", {"start": v(-33, -252) * mm, "end": v(-23, -252) * mm});
            skLineSegment(sketch, "E31.16.14.2", {"start": v(-33, -242) * mm, "end": v(-33, -252) * mm});
            skLineSegment(sketch, "E31.16.14.3", {"start": v(-23, -242) * mm, "end": v(-23, -252) * mm});
            skLineSegment(sketch, "E31.16.15.0", {"start": v(-33, -228) * mm, "end": v(-23, -228) * mm});
            skLineSegment(sketch, "E31.16.15.1", {"start": v(-33, -238) * mm, "end": v(-23, -238) * mm});
            skLineSegment(sketch, "E31.16.15.2", {"start": v(-33, -228) * mm, "end": v(-33, -238) * mm});
            skLineSegment(sketch, "E31.16.15.3", {"start": v(-23, -228) * mm, "end": v(-23, -238) * mm});
            skLineSegment(sketch, "E31.16.16.0", {"start": v(-33, -214) * mm, "end": v(-23, -214) * mm});
            skLineSegment(sketch, "E31.16.16.1", {"start": v(-33, -224) * mm, "end": v(-23, -224) * mm});
            skLineSegment(sketch, "E31.16.16.2", {"start": v(-33, -214) * mm, "end": v(-33, -224) * mm});
            skLineSegment(sketch, "E31.16.16.3", {"start": v(-23, -214) * mm, "end": v(-23, -224) * mm});
            skLineSegment(sketch, "E31.16.17.0", {"start": v(-33, -200) * mm, "end": v(-23, -200) * mm});
            skLineSegment(sketch, "E31.16.17.1", {"start": v(-33, -210) * mm, "end": v(-23, -210) * mm});
            skLineSegment(sketch, "E31.16.17.2", {"start": v(-33, -200) * mm, "end": v(-33, -210) * mm});
            skLineSegment(sketch, "E31.16.17.3", {"start": v(-23, -200) * mm, "end": v(-23, -210) * mm});
            skLineSegment(sketch, "E31.16.18.0", {"start": v(-33, -186) * mm, "end": v(-23, -186) * mm});
            skLineSegment(sketch, "E31.16.18.1", {"start": v(-33, -196) * mm, "end": v(-23, -196) * mm});
            skLineSegment(sketch, "E31.16.18.2", {"start": v(-33, -186) * mm, "end": v(-33, -196) * mm});
            skLineSegment(sketch, "E31.16.18.3", {"start": v(-23, -186) * mm, "end": v(-23, -196) * mm});
            skLineSegment(sketch, "E31.16.19.0", {"start": v(-33, -172) * mm, "end": v(-23, -172) * mm});
            skLineSegment(sketch, "E31.16.19.1", {"start": v(-33, -182) * mm, "end": v(-23, -182) * mm});
            skLineSegment(sketch, "E31.16.19.2", {"start": v(-33, -172) * mm, "end": v(-33, -182) * mm});
            skLineSegment(sketch, "E31.16.19.3", {"start": v(-23, -172) * mm, "end": v(-23, -182) * mm});
            skLineSegment(sketch, "E31.16.20.0", {"start": v(-33, -158) * mm, "end": v(-23, -158) * mm});
            skLineSegment(sketch, "E31.16.20.1", {"start": v(-33, -168) * mm, "end": v(-23, -168) * mm});
            skLineSegment(sketch, "E31.16.20.2", {"start": v(-33, -158) * mm, "end": v(-33, -168) * mm});
            skLineSegment(sketch, "E31.16.20.3", {"start": v(-23, -158) * mm, "end": v(-23, -168) * mm});
            skLineSegment(sketch, "E31.16.21.0", {"start": v(-33, -144) * mm, "end": v(-23, -144) * mm});
            skLineSegment(sketch, "E31.16.21.1", {"start": v(-33, -154) * mm, "end": v(-23, -154) * mm});
            skLineSegment(sketch, "E31.16.21.2", {"start": v(-33, -144) * mm, "end": v(-33, -154) * mm});
            skLineSegment(sketch, "E31.16.21.3", {"start": v(-23, -144) * mm, "end": v(-23, -154) * mm});
            skLineSegment(sketch, "E31.16.22.0", {"start": v(-33, -130) * mm, "end": v(-23, -130) * mm});
            skLineSegment(sketch, "E31.16.22.1", {"start": v(-33, -140) * mm, "end": v(-23, -140) * mm});
            skLineSegment(sketch, "E31.16.22.2", {"start": v(-33, -130) * mm, "end": v(-33, -140) * mm});
            skLineSegment(sketch, "E31.16.22.3", {"start": v(-23, -130) * mm, "end": v(-23, -140) * mm});
            skLineSegment(sketch, "E31.16.23.0", {"start": v(-33, -116) * mm, "end": v(-23, -116) * mm});
            skLineSegment(sketch, "E31.16.23.1", {"start": v(-33, -126) * mm, "end": v(-23, -126) * mm});
            skLineSegment(sketch, "E31.16.23.2", {"start": v(-33, -116) * mm, "end": v(-33, -126) * mm});
            skLineSegment(sketch, "E31.16.23.3", {"start": v(-23, -116) * mm, "end": v(-23, -126) * mm});
            skLineSegment(sketch, "E31.16.24.0", {"start": v(-33, -102) * mm, "end": v(-23, -102) * mm});
            skLineSegment(sketch, "E31.16.24.1", {"start": v(-33, -112) * mm, "end": v(-23, -112) * mm});
            skLineSegment(sketch, "E31.16.24.2", {"start": v(-33, -102) * mm, "end": v(-33, -112) * mm});
            skLineSegment(sketch, "E31.16.24.3", {"start": v(-23, -102) * mm, "end": v(-23, -112) * mm});
            skLineSegment(sketch, "E31.16.25.0", {"start": v(-33, -88) * mm, "end": v(-23, -88) * mm});
            skLineSegment(sketch, "E31.16.25.1", {"start": v(-33, -98) * mm, "end": v(-23, -98) * mm});
            skLineSegment(sketch, "E31.16.25.2", {"start": v(-33, -88) * mm, "end": v(-33, -98) * mm});
            skLineSegment(sketch, "E31.16.25.3", {"start": v(-23, -88) * mm, "end": v(-23, -98) * mm});
            skLineSegment(sketch, "E31.16.26.0", {"start": v(-33, -74) * mm, "end": v(-23, -74) * mm});
            skLineSegment(sketch, "E31.16.26.1", {"start": v(-33, -84) * mm, "end": v(-23, -84) * mm});
            skLineSegment(sketch, "E31.16.26.2", {"start": v(-33, -74) * mm, "end": v(-33, -84) * mm});
            skLineSegment(sketch, "E31.16.26.3", {"start": v(-23, -74) * mm, "end": v(-23, -84) * mm});
            skLineSegment(sketch, "E31.16.27.0", {"start": v(-33, -60) * mm, "end": v(-23, -60) * mm});
            skLineSegment(sketch, "E31.16.27.1", {"start": v(-33, -70) * mm, "end": v(-23, -70) * mm});
            skLineSegment(sketch, "E31.16.27.2", {"start": v(-33, -60) * mm, "end": v(-33, -70) * mm});
            skLineSegment(sketch, "E31.16.27.3", {"start": v(-23, -60) * mm, "end": v(-23, -70) * mm});
            skLineSegment(sketch, "E31.16.28.0", {"start": v(-33, -46) * mm, "end": v(-23, -46) * mm});
            skLineSegment(sketch, "E31.16.28.1", {"start": v(-33, -56) * mm, "end": v(-23, -56) * mm});
            skLineSegment(sketch, "E31.16.28.2", {"start": v(-33, -46) * mm, "end": v(-33, -56) * mm});
            skLineSegment(sketch, "E31.16.28.3", {"start": v(-23, -46) * mm, "end": v(-23, -56) * mm});
            skLineSegment(sketch, "E31.16.29.0", {"start": v(-33, -32) * mm, "end": v(-23, -32) * mm});
            skLineSegment(sketch, "E31.16.29.1", {"start": v(-33, -42) * mm, "end": v(-23, -42) * mm});
            skLineSegment(sketch, "E31.16.29.2", {"start": v(-33, -32) * mm, "end": v(-33, -42) * mm});
            skLineSegment(sketch, "E31.16.29.3", {"start": v(-23, -32) * mm, "end": v(-23, -42) * mm});
            skLineSegment(sketch, "E31.16.30.0", {"start": v(-33, -18) * mm, "end": v(-23, -18) * mm});
            skLineSegment(sketch, "E31.16.30.1", {"start": v(-33, -28) * mm, "end": v(-23, -28) * mm});
            skLineSegment(sketch, "E31.16.30.2", {"start": v(-33, -18) * mm, "end": v(-33, -28) * mm});
            skLineSegment(sketch, "E31.16.30.3", {"start": v(-23, -18) * mm, "end": v(-23, -28) * mm});
            skLineSegment(sketch, "E31.16.31.0", {"start": v(-33, -4) * mm, "end": v(-23, -4) * mm});
            skLineSegment(sketch, "E31.16.31.1", {"start": v(-33, -14) * mm, "end": v(-23, -14) * mm});
            skLineSegment(sketch, "E31.16.31.2", {"start": v(-33, -4) * mm, "end": v(-33, -14) * mm});
            skLineSegment(sketch, "E31.16.31.3", {"start": v(-23, -4) * mm, "end": v(-23, -14) * mm});
            skLineSegment(sketch, "E31.17.0.0", {"start": v(-19, -438) * mm, "end": v(-9, -438) * mm});
            skLineSegment(sketch, "E31.17.0.1", {"start": v(-19, -448) * mm, "end": v(-9, -448) * mm});
            skLineSegment(sketch, "E31.17.0.2", {"start": v(-19, -438) * mm, "end": v(-19, -448) * mm});
            skLineSegment(sketch, "E31.17.0.3", {"start": v(-9, -438) * mm, "end": v(-9, -448) * mm});
            skLineSegment(sketch, "E31.17.1.0", {"start": v(-19, -424) * mm, "end": v(-9, -424) * mm});
            skLineSegment(sketch, "E31.17.1.1", {"start": v(-19, -434) * mm, "end": v(-9, -434) * mm});
            skLineSegment(sketch, "E31.17.1.2", {"start": v(-19, -424) * mm, "end": v(-19, -434) * mm});
            skLineSegment(sketch, "E31.17.1.3", {"start": v(-9, -424) * mm, "end": v(-9, -434) * mm});
            skLineSegment(sketch, "E31.17.2.0", {"start": v(-19, -410) * mm, "end": v(-9, -410) * mm});
            skLineSegment(sketch, "E31.17.2.1", {"start": v(-19, -420) * mm, "end": v(-9, -420) * mm});
            skLineSegment(sketch, "E31.17.2.2", {"start": v(-19, -410) * mm, "end": v(-19, -420) * mm});
            skLineSegment(sketch, "E31.17.2.3", {"start": v(-9, -410) * mm, "end": v(-9, -420) * mm});
            skLineSegment(sketch, "E31.17.3.0", {"start": v(-19, -396) * mm, "end": v(-9, -396) * mm});
            skLineSegment(sketch, "E31.17.3.1", {"start": v(-19, -406) * mm, "end": v(-9, -406) * mm});
            skLineSegment(sketch, "E31.17.3.2", {"start": v(-19, -396) * mm, "end": v(-19, -406) * mm});
            skLineSegment(sketch, "E31.17.3.3", {"start": v(-9, -396) * mm, "end": v(-9, -406) * mm});
            skLineSegment(sketch, "E31.17.4.0", {"start": v(-19, -382) * mm, "end": v(-9, -382) * mm});
            skLineSegment(sketch, "E31.17.4.1", {"start": v(-19, -392) * mm, "end": v(-9, -392) * mm});
            skLineSegment(sketch, "E31.17.4.2", {"start": v(-19, -382) * mm, "end": v(-19, -392) * mm});
            skLineSegment(sketch, "E31.17.4.3", {"start": v(-9, -382) * mm, "end": v(-9, -392) * mm});
            skLineSegment(sketch, "E31.17.5.0", {"start": v(-19, -368) * mm, "end": v(-9, -368) * mm});
            skLineSegment(sketch, "E31.17.5.1", {"start": v(-19, -378) * mm, "end": v(-9, -378) * mm});
            skLineSegment(sketch, "E31.17.5.2", {"start": v(-19, -368) * mm, "end": v(-19, -378) * mm});
            skLineSegment(sketch, "E31.17.5.3", {"start": v(-9, -368) * mm, "end": v(-9, -378) * mm});
            skLineSegment(sketch, "E31.17.6.0", {"start": v(-19, -354) * mm, "end": v(-9, -354) * mm});
            skLineSegment(sketch, "E31.17.6.1", {"start": v(-19, -364) * mm, "end": v(-9, -364) * mm});
            skLineSegment(sketch, "E31.17.6.2", {"start": v(-19, -354) * mm, "end": v(-19, -364) * mm});
            skLineSegment(sketch, "E31.17.6.3", {"start": v(-9, -354) * mm, "end": v(-9, -364) * mm});
            skLineSegment(sketch, "E31.17.7.0", {"start": v(-19, -340) * mm, "end": v(-9, -340) * mm});
            skLineSegment(sketch, "E31.17.7.1", {"start": v(-19, -350) * mm, "end": v(-9, -350) * mm});
            skLineSegment(sketch, "E31.17.7.2", {"start": v(-19, -340) * mm, "end": v(-19, -350) * mm});
            skLineSegment(sketch, "E31.17.7.3", {"start": v(-9, -340) * mm, "end": v(-9, -350) * mm});
            skLineSegment(sketch, "E31.17.8.0", {"start": v(-19, -326) * mm, "end": v(-9, -326) * mm});
            skLineSegment(sketch, "E31.17.8.1", {"start": v(-19, -336) * mm, "end": v(-9, -336) * mm});
            skLineSegment(sketch, "E31.17.8.2", {"start": v(-19, -326) * mm, "end": v(-19, -336) * mm});
            skLineSegment(sketch, "E31.17.8.3", {"start": v(-9, -326) * mm, "end": v(-9, -336) * mm});
            skLineSegment(sketch, "E31.17.9.0", {"start": v(-19, -312) * mm, "end": v(-9, -312) * mm});
            skLineSegment(sketch, "E31.17.9.1", {"start": v(-19, -322) * mm, "end": v(-9, -322) * mm});
            skLineSegment(sketch, "E31.17.9.2", {"start": v(-19, -312) * mm, "end": v(-19, -322) * mm});
            skLineSegment(sketch, "E31.17.9.3", {"start": v(-9, -312) * mm, "end": v(-9, -322) * mm});
            skLineSegment(sketch, "E31.17.10.0", {"start": v(-19, -298) * mm, "end": v(-9, -298) * mm});
            skLineSegment(sketch, "E31.17.10.1", {"start": v(-19, -308) * mm, "end": v(-9, -308) * mm});
            skLineSegment(sketch, "E31.17.10.2", {"start": v(-19, -298) * mm, "end": v(-19, -308) * mm});
            skLineSegment(sketch, "E31.17.10.3", {"start": v(-9, -298) * mm, "end": v(-9, -308) * mm});
            skLineSegment(sketch, "E31.17.11.0", {"start": v(-19, -284) * mm, "end": v(-9, -284) * mm});
            skLineSegment(sketch, "E31.17.11.1", {"start": v(-19, -294) * mm, "end": v(-9, -294) * mm});
            skLineSegment(sketch, "E31.17.11.2", {"start": v(-19, -284) * mm, "end": v(-19, -294) * mm});
            skLineSegment(sketch, "E31.17.11.3", {"start": v(-9, -284) * mm, "end": v(-9, -294) * mm});
            skLineSegment(sketch, "E31.17.12.0", {"start": v(-19, -270) * mm, "end": v(-9, -270) * mm});
            skLineSegment(sketch, "E31.17.12.1", {"start": v(-19, -280) * mm, "end": v(-9, -280) * mm});
            skLineSegment(sketch, "E31.17.12.2", {"start": v(-19, -270) * mm, "end": v(-19, -280) * mm});
            skLineSegment(sketch, "E31.17.12.3", {"start": v(-9, -270) * mm, "end": v(-9, -280) * mm});
            skLineSegment(sketch, "E31.17.13.0", {"start": v(-19, -256) * mm, "end": v(-9, -256) * mm});
            skLineSegment(sketch, "E31.17.13.1", {"start": v(-19, -266) * mm, "end": v(-9, -266) * mm});
            skLineSegment(sketch, "E31.17.13.2", {"start": v(-19, -256) * mm, "end": v(-19, -266) * mm});
            skLineSegment(sketch, "E31.17.13.3", {"start": v(-9, -256) * mm, "end": v(-9, -266) * mm});
            skLineSegment(sketch, "E31.17.14.0", {"start": v(-19, -242) * mm, "end": v(-9, -242) * mm});
            skLineSegment(sketch, "E31.17.14.1", {"start": v(-19, -252) * mm, "end": v(-9, -252) * mm});
            skLineSegment(sketch, "E31.17.14.2", {"start": v(-19, -242) * mm, "end": v(-19, -252) * mm});
            skLineSegment(sketch, "E31.17.14.3", {"start": v(-9, -242) * mm, "end": v(-9, -252) * mm});
            skLineSegment(sketch, "E31.17.15.0", {"start": v(-19, -228) * mm, "end": v(-9, -228) * mm});
            skLineSegment(sketch, "E31.17.15.1", {"start": v(-19, -238) * mm, "end": v(-9, -238) * mm});
            skLineSegment(sketch, "E31.17.15.2", {"start": v(-19, -228) * mm, "end": v(-19, -238) * mm});
            skLineSegment(sketch, "E31.17.15.3", {"start": v(-9, -228) * mm, "end": v(-9, -238) * mm});
            skLineSegment(sketch, "E31.17.16.0", {"start": v(-19, -214) * mm, "end": v(-9, -214) * mm});
            skLineSegment(sketch, "E31.17.16.1", {"start": v(-19, -224) * mm, "end": v(-9, -224) * mm});
            skLineSegment(sketch, "E31.17.16.2", {"start": v(-19, -214) * mm, "end": v(-19, -224) * mm});
            skLineSegment(sketch, "E31.17.16.3", {"start": v(-9, -214) * mm, "end": v(-9, -224) * mm});
            skLineSegment(sketch, "E31.17.17.0", {"start": v(-19, -200) * mm, "end": v(-9, -200) * mm});
            skLineSegment(sketch, "E31.17.17.1", {"start": v(-19, -210) * mm, "end": v(-9, -210) * mm});
            skLineSegment(sketch, "E31.17.17.2", {"start": v(-19, -200) * mm, "end": v(-19, -210) * mm});
            skLineSegment(sketch, "E31.17.17.3", {"start": v(-9, -200) * mm, "end": v(-9, -210) * mm});
            skLineSegment(sketch, "E31.17.18.0", {"start": v(-19, -186) * mm, "end": v(-9, -186) * mm});
            skLineSegment(sketch, "E31.17.18.1", {"start": v(-19, -196) * mm, "end": v(-9, -196) * mm});
            skLineSegment(sketch, "E31.17.18.2", {"start": v(-19, -186) * mm, "end": v(-19, -196) * mm});
            skLineSegment(sketch, "E31.17.18.3", {"start": v(-9, -186) * mm, "end": v(-9, -196) * mm});
            skLineSegment(sketch, "E31.17.19.0", {"start": v(-19, -172) * mm, "end": v(-9, -172) * mm});
            skLineSegment(sketch, "E31.17.19.1", {"start": v(-19, -182) * mm, "end": v(-9, -182) * mm});
            skLineSegment(sketch, "E31.17.19.2", {"start": v(-19, -172) * mm, "end": v(-19, -182) * mm});
            skLineSegment(sketch, "E31.17.19.3", {"start": v(-9, -172) * mm, "end": v(-9, -182) * mm});
            skLineSegment(sketch, "E31.17.20.0", {"start": v(-19, -158) * mm, "end": v(-9, -158) * mm});
            skLineSegment(sketch, "E31.17.20.1", {"start": v(-19, -168) * mm, "end": v(-9, -168) * mm});
            skLineSegment(sketch, "E31.17.20.2", {"start": v(-19, -158) * mm, "end": v(-19, -168) * mm});
            skLineSegment(sketch, "E31.17.20.3", {"start": v(-9, -158) * mm, "end": v(-9, -168) * mm});
            skLineSegment(sketch, "E31.17.21.0", {"start": v(-19, -144) * mm, "end": v(-9, -144) * mm});
            skLineSegment(sketch, "E31.17.21.1", {"start": v(-19, -154) * mm, "end": v(-9, -154) * mm});
            skLineSegment(sketch, "E31.17.21.2", {"start": v(-19, -144) * mm, "end": v(-19, -154) * mm});
            skLineSegment(sketch, "E31.17.21.3", {"start": v(-9, -144) * mm, "end": v(-9, -154) * mm});
            skLineSegment(sketch, "E31.17.22.0", {"start": v(-19, -130) * mm, "end": v(-9, -130) * mm});
            skLineSegment(sketch, "E31.17.22.1", {"start": v(-19, -140) * mm, "end": v(-9, -140) * mm});
            skLineSegment(sketch, "E31.17.22.2", {"start": v(-19, -130) * mm, "end": v(-19, -140) * mm});
            skLineSegment(sketch, "E31.17.22.3", {"start": v(-9, -130) * mm, "end": v(-9, -140) * mm});
            skLineSegment(sketch, "E31.17.23.0", {"start": v(-19, -116) * mm, "end": v(-9, -116) * mm});
            skLineSegment(sketch, "E31.17.23.1", {"start": v(-19, -126) * mm, "end": v(-9, -126) * mm});
            skLineSegment(sketch, "E31.17.23.2", {"start": v(-19, -116) * mm, "end": v(-19, -126) * mm});
            skLineSegment(sketch, "E31.17.23.3", {"start": v(-9, -116) * mm, "end": v(-9, -126) * mm});
            skLineSegment(sketch, "E31.17.24.0", {"start": v(-19, -102) * mm, "end": v(-9, -102) * mm});
            skLineSegment(sketch, "E31.17.24.1", {"start": v(-19, -112) * mm, "end": v(-9, -112) * mm});
            skLineSegment(sketch, "E31.17.24.2", {"start": v(-19, -102) * mm, "end": v(-19, -112) * mm});
            skLineSegment(sketch, "E31.17.24.3", {"start": v(-9, -102) * mm, "end": v(-9, -112) * mm});
            skLineSegment(sketch, "E31.17.25.0", {"start": v(-19, -88) * mm, "end": v(-9, -88) * mm});
            skLineSegment(sketch, "E31.17.25.1", {"start": v(-19, -98) * mm, "end": v(-9, -98) * mm});
            skLineSegment(sketch, "E31.17.25.2", {"start": v(-19, -88) * mm, "end": v(-19, -98) * mm});
            skLineSegment(sketch, "E31.17.25.3", {"start": v(-9, -88) * mm, "end": v(-9, -98) * mm});
            skLineSegment(sketch, "E31.17.26.0", {"start": v(-19, -74) * mm, "end": v(-9, -74) * mm});
            skLineSegment(sketch, "E31.17.26.1", {"start": v(-19, -84) * mm, "end": v(-9, -84) * mm});
            skLineSegment(sketch, "E31.17.26.2", {"start": v(-19, -74) * mm, "end": v(-19, -84) * mm});
            skLineSegment(sketch, "E31.17.26.3", {"start": v(-9, -74) * mm, "end": v(-9, -84) * mm});
            skLineSegment(sketch, "E31.17.27.0", {"start": v(-19, -60) * mm, "end": v(-9, -60) * mm});
            skLineSegment(sketch, "E31.17.27.1", {"start": v(-19, -70) * mm, "end": v(-9, -70) * mm});
            skLineSegment(sketch, "E31.17.27.2", {"start": v(-19, -60) * mm, "end": v(-19, -70) * mm});
            skLineSegment(sketch, "E31.17.27.3", {"start": v(-9, -60) * mm, "end": v(-9, -70) * mm});
            skLineSegment(sketch, "E31.17.28.0", {"start": v(-19, -46) * mm, "end": v(-9, -46) * mm});
            skLineSegment(sketch, "E31.17.28.1", {"start": v(-19, -56) * mm, "end": v(-9, -56) * mm});
            skLineSegment(sketch, "E31.17.28.2", {"start": v(-19, -46) * mm, "end": v(-19, -56) * mm});
            skLineSegment(sketch, "E31.17.28.3", {"start": v(-9, -46) * mm, "end": v(-9, -56) * mm});
            skLineSegment(sketch, "E31.17.29.0", {"start": v(-19, -32) * mm, "end": v(-9, -32) * mm});
            skLineSegment(sketch, "E31.17.29.1", {"start": v(-19, -42) * mm, "end": v(-9, -42) * mm});
            skLineSegment(sketch, "E31.17.29.2", {"start": v(-19, -32) * mm, "end": v(-19, -42) * mm});
            skLineSegment(sketch, "E31.17.29.3", {"start": v(-9, -32) * mm, "end": v(-9, -42) * mm});
            skLineSegment(sketch, "E31.17.30.0", {"start": v(-19, -18) * mm, "end": v(-9, -18) * mm});
            skLineSegment(sketch, "E31.17.30.1", {"start": v(-19, -28) * mm, "end": v(-9, -28) * mm});
            skLineSegment(sketch, "E31.17.30.2", {"start": v(-19, -18) * mm, "end": v(-19, -28) * mm});
            skLineSegment(sketch, "E31.17.30.3", {"start": v(-9, -18) * mm, "end": v(-9, -28) * mm});
            skLineSegment(sketch, "E31.17.31.0", {"start": v(-19, -4) * mm, "end": v(-9, -4) * mm});
            skLineSegment(sketch, "E31.17.31.1", {"start": v(-19, -14) * mm, "end": v(-9, -14) * mm});
            skLineSegment(sketch, "E31.17.31.2", {"start": v(-19, -4) * mm, "end": v(-19, -14) * mm});
            skLineSegment(sketch, "E31.17.31.3", {"start": v(-9, -4) * mm, "end": v(-9, -14) * mm});
            skLineSegment(sketch, "E31.18.0.0", {"start": v(-5, -438) * mm, "end": v(5, -438) * mm});
            skLineSegment(sketch, "E31.18.0.1", {"start": v(-5, -448) * mm, "end": v(5, -448) * mm});
            skLineSegment(sketch, "E31.18.0.2", {"start": v(-5, -438) * mm, "end": v(-5, -448) * mm});
            skLineSegment(sketch, "E31.18.0.3", {"start": v(5, -438) * mm, "end": v(5, -448) * mm});
            skLineSegment(sketch, "E31.18.1.0", {"start": v(-5, -424) * mm, "end": v(5, -424) * mm});
            skLineSegment(sketch, "E31.18.1.1", {"start": v(-5, -434) * mm, "end": v(5, -434) * mm});
            skLineSegment(sketch, "E31.18.1.2", {"start": v(-5, -424) * mm, "end": v(-5, -434) * mm});
            skLineSegment(sketch, "E31.18.1.3", {"start": v(5, -424) * mm, "end": v(5, -434) * mm});
            skLineSegment(sketch, "E31.18.2.0", {"start": v(-5, -410) * mm, "end": v(5, -410) * mm});
            skLineSegment(sketch, "E31.18.2.1", {"start": v(-5, -420) * mm, "end": v(5, -420) * mm});
            skLineSegment(sketch, "E31.18.2.2", {"start": v(-5, -410) * mm, "end": v(-5, -420) * mm});
            skLineSegment(sketch, "E31.18.2.3", {"start": v(5, -410) * mm, "end": v(5, -420) * mm});
            skLineSegment(sketch, "E31.18.3.0", {"start": v(-5, -396) * mm, "end": v(5, -396) * mm});
            skLineSegment(sketch, "E31.18.3.1", {"start": v(-5, -406) * mm, "end": v(5, -406) * mm});
            skLineSegment(sketch, "E31.18.3.2", {"start": v(-5, -396) * mm, "end": v(-5, -406) * mm});
            skLineSegment(sketch, "E31.18.3.3", {"start": v(5, -396) * mm, "end": v(5, -406) * mm});
            skLineSegment(sketch, "E31.18.4.0", {"start": v(-5, -382) * mm, "end": v(5, -382) * mm});
            skLineSegment(sketch, "E31.18.4.1", {"start": v(-5, -392) * mm, "end": v(5, -392) * mm});
            skLineSegment(sketch, "E31.18.4.2", {"start": v(-5, -382) * mm, "end": v(-5, -392) * mm});
            skLineSegment(sketch, "E31.18.4.3", {"start": v(5, -382) * mm, "end": v(5, -392) * mm});
            skLineSegment(sketch, "E31.18.5.0", {"start": v(-5, -368) * mm, "end": v(5, -368) * mm});
            skLineSegment(sketch, "E31.18.5.1", {"start": v(-5, -378) * mm, "end": v(5, -378) * mm});
            skLineSegment(sketch, "E31.18.5.2", {"start": v(-5, -368) * mm, "end": v(-5, -378) * mm});
            skLineSegment(sketch, "E31.18.5.3", {"start": v(5, -368) * mm, "end": v(5, -378) * mm});
            skLineSegment(sketch, "E31.18.6.0", {"start": v(-5, -354) * mm, "end": v(5, -354) * mm});
            skLineSegment(sketch, "E31.18.6.1", {"start": v(-5, -364) * mm, "end": v(5, -364) * mm});
            skLineSegment(sketch, "E31.18.6.2", {"start": v(-5, -354) * mm, "end": v(-5, -364) * mm});
            skLineSegment(sketch, "E31.18.6.3", {"start": v(5, -354) * mm, "end": v(5, -364) * mm});
            skLineSegment(sketch, "E31.18.7.0", {"start": v(-5, -340) * mm, "end": v(5, -340) * mm});
            skLineSegment(sketch, "E31.18.7.1", {"start": v(-5, -350) * mm, "end": v(5, -350) * mm});
            skLineSegment(sketch, "E31.18.7.2", {"start": v(-5, -340) * mm, "end": v(-5, -350) * mm});
            skLineSegment(sketch, "E31.18.7.3", {"start": v(5, -340) * mm, "end": v(5, -350) * mm});
            skLineSegment(sketch, "E31.18.8.0", {"start": v(-5, -326) * mm, "end": v(5, -326) * mm});
            skLineSegment(sketch, "E31.18.8.1", {"start": v(-5, -336) * mm, "end": v(5, -336) * mm});
            skLineSegment(sketch, "E31.18.8.2", {"start": v(-5, -326) * mm, "end": v(-5, -336) * mm});
            skLineSegment(sketch, "E31.18.8.3", {"start": v(5, -326) * mm, "end": v(5, -336) * mm});
            skLineSegment(sketch, "E31.18.9.0", {"start": v(-5, -312) * mm, "end": v(5, -312) * mm});
            skLineSegment(sketch, "E31.18.9.1", {"start": v(-5, -322) * mm, "end": v(5, -322) * mm});
            skLineSegment(sketch, "E31.18.9.2", {"start": v(-5, -312) * mm, "end": v(-5, -322) * mm});
            skLineSegment(sketch, "E31.18.9.3", {"start": v(5, -312) * mm, "end": v(5, -322) * mm});
            skLineSegment(sketch, "E31.18.10.0", {"start": v(-5, -298) * mm, "end": v(5, -298) * mm});
            skLineSegment(sketch, "E31.18.10.1", {"start": v(-5, -308) * mm, "end": v(5, -308) * mm});
            skLineSegment(sketch, "E31.18.10.2", {"start": v(-5, -298) * mm, "end": v(-5, -308) * mm});
            skLineSegment(sketch, "E31.18.10.3", {"start": v(5, -298) * mm, "end": v(5, -308) * mm});
            skLineSegment(sketch, "E31.18.11.0", {"start": v(-5, -284) * mm, "end": v(5, -284) * mm});
            skLineSegment(sketch, "E31.18.11.1", {"start": v(-5, -294) * mm, "end": v(5, -294) * mm});
            skLineSegment(sketch, "E31.18.11.2", {"start": v(-5, -284) * mm, "end": v(-5, -294) * mm});
            skLineSegment(sketch, "E31.18.11.3", {"start": v(5, -284) * mm, "end": v(5, -294) * mm});
            skLineSegment(sketch, "E31.18.12.0", {"start": v(-5, -270) * mm, "end": v(5, -270) * mm});
            skLineSegment(sketch, "E31.18.12.1", {"start": v(-5, -280) * mm, "end": v(5, -280) * mm});
            skLineSegment(sketch, "E31.18.12.2", {"start": v(-5, -270) * mm, "end": v(-5, -280) * mm});
            skLineSegment(sketch, "E31.18.12.3", {"start": v(5, -270) * mm, "end": v(5, -280) * mm});
            skLineSegment(sketch, "E31.18.13.0", {"start": v(-5, -256) * mm, "end": v(5, -256) * mm});
            skLineSegment(sketch, "E31.18.13.1", {"start": v(-5, -266) * mm, "end": v(5, -266) * mm});
            skLineSegment(sketch, "E31.18.13.2", {"start": v(-5, -256) * mm, "end": v(-5, -266) * mm});
            skLineSegment(sketch, "E31.18.13.3", {"start": v(5, -256) * mm, "end": v(5, -266) * mm});
            skLineSegment(sketch, "E31.18.14.0", {"start": v(-5, -242) * mm, "end": v(5, -242) * mm});
            skLineSegment(sketch, "E31.18.14.1", {"start": v(-5, -252) * mm, "end": v(5, -252) * mm});
            skLineSegment(sketch, "E31.18.14.2", {"start": v(-5, -242) * mm, "end": v(-5, -252) * mm});
            skLineSegment(sketch, "E31.18.14.3", {"start": v(5, -242) * mm, "end": v(5, -252) * mm});
            skLineSegment(sketch, "E31.18.15.0", {"start": v(-5, -228) * mm, "end": v(5, -228) * mm});
            skLineSegment(sketch, "E31.18.15.1", {"start": v(-5, -238) * mm, "end": v(5, -238) * mm});
            skLineSegment(sketch, "E31.18.15.2", {"start": v(-5, -228) * mm, "end": v(-5, -238) * mm});
            skLineSegment(sketch, "E31.18.15.3", {"start": v(5, -228) * mm, "end": v(5, -238) * mm});
            skLineSegment(sketch, "E31.18.16.0", {"start": v(-5, -214) * mm, "end": v(5, -214) * mm});
            skLineSegment(sketch, "E31.18.16.1", {"start": v(-5, -224) * mm, "end": v(5, -224) * mm});
            skLineSegment(sketch, "E31.18.16.2", {"start": v(-5, -214) * mm, "end": v(-5, -224) * mm});
            skLineSegment(sketch, "E31.18.16.3", {"start": v(5, -214) * mm, "end": v(5, -224) * mm});
            skLineSegment(sketch, "E31.18.17.0", {"start": v(-5, -200) * mm, "end": v(5, -200) * mm});
            skLineSegment(sketch, "E31.18.17.1", {"start": v(-5, -210) * mm, "end": v(5, -210) * mm});
            skLineSegment(sketch, "E31.18.17.2", {"start": v(-5, -200) * mm, "end": v(-5, -210) * mm});
            skLineSegment(sketch, "E31.18.17.3", {"start": v(5, -200) * mm, "end": v(5, -210) * mm});
            skLineSegment(sketch, "E31.18.18.0", {"start": v(-5, -186) * mm, "end": v(5, -186) * mm});
            skLineSegment(sketch, "E31.18.18.1", {"start": v(-5, -196) * mm, "end": v(5, -196) * mm});
            skLineSegment(sketch, "E31.18.18.2", {"start": v(-5, -186) * mm, "end": v(-5, -196) * mm});
            skLineSegment(sketch, "E31.18.18.3", {"start": v(5, -186) * mm, "end": v(5, -196) * mm});
            skLineSegment(sketch, "E31.18.19.0", {"start": v(-5, -172) * mm, "end": v(5, -172) * mm});
            skLineSegment(sketch, "E31.18.19.1", {"start": v(-5, -182) * mm, "end": v(5, -182) * mm});
            skLineSegment(sketch, "E31.18.19.2", {"start": v(-5, -172) * mm, "end": v(-5, -182) * mm});
            skLineSegment(sketch, "E31.18.19.3", {"start": v(5, -172) * mm, "end": v(5, -182) * mm});
            skLineSegment(sketch, "E31.18.20.0", {"start": v(-5, -158) * mm, "end": v(5, -158) * mm});
            skLineSegment(sketch, "E31.18.20.1", {"start": v(-5, -168) * mm, "end": v(5, -168) * mm});
            skLineSegment(sketch, "E31.18.20.2", {"start": v(-5, -158) * mm, "end": v(-5, -168) * mm});
            skLineSegment(sketch, "E31.18.20.3", {"start": v(5, -158) * mm, "end": v(5, -168) * mm});
            skLineSegment(sketch, "E31.18.21.0", {"start": v(-5, -144) * mm, "end": v(5, -144) * mm});
            skLineSegment(sketch, "E31.18.21.1", {"start": v(-5, -154) * mm, "end": v(5, -154) * mm});
            skLineSegment(sketch, "E31.18.21.2", {"start": v(-5, -144) * mm, "end": v(-5, -154) * mm});
            skLineSegment(sketch, "E31.18.21.3", {"start": v(5, -144) * mm, "end": v(5, -154) * mm});
            skLineSegment(sketch, "E31.18.22.0", {"start": v(-5, -130) * mm, "end": v(5, -130) * mm});
            skLineSegment(sketch, "E31.18.22.1", {"start": v(-5, -140) * mm, "end": v(5, -140) * mm});
            skLineSegment(sketch, "E31.18.22.2", {"start": v(-5, -130) * mm, "end": v(-5, -140) * mm});
            skLineSegment(sketch, "E31.18.22.3", {"start": v(5, -130) * mm, "end": v(5, -140) * mm});
            skLineSegment(sketch, "E31.18.23.0", {"start": v(-5, -116) * mm, "end": v(5, -116) * mm});
            skLineSegment(sketch, "E31.18.23.1", {"start": v(-5, -126) * mm, "end": v(5, -126) * mm});
            skLineSegment(sketch, "E31.18.23.2", {"start": v(-5, -116) * mm, "end": v(-5, -126) * mm});
            skLineSegment(sketch, "E31.18.23.3", {"start": v(5, -116) * mm, "end": v(5, -126) * mm});
            skLineSegment(sketch, "E31.18.24.0", {"start": v(-5, -102) * mm, "end": v(5, -102) * mm});
            skLineSegment(sketch, "E31.18.24.1", {"start": v(-5, -112) * mm, "end": v(5, -112) * mm});
            skLineSegment(sketch, "E31.18.24.2", {"start": v(-5, -102) * mm, "end": v(-5, -112) * mm});
            skLineSegment(sketch, "E31.18.24.3", {"start": v(5, -102) * mm, "end": v(5, -112) * mm});
            skLineSegment(sketch, "E31.18.25.0", {"start": v(-5, -88) * mm, "end": v(5, -88) * mm});
            skLineSegment(sketch, "E31.18.25.1", {"start": v(-5, -98) * mm, "end": v(5, -98) * mm});
            skLineSegment(sketch, "E31.18.25.2", {"start": v(-5, -88) * mm, "end": v(-5, -98) * mm});
            skLineSegment(sketch, "E31.18.25.3", {"start": v(5, -88) * mm, "end": v(5, -98) * mm});
            skLineSegment(sketch, "E31.18.26.0", {"start": v(-5, -74) * mm, "end": v(5, -74) * mm});
            skLineSegment(sketch, "E31.18.26.1", {"start": v(-5, -84) * mm, "end": v(5, -84) * mm});
            skLineSegment(sketch, "E31.18.26.2", {"start": v(-5, -74) * mm, "end": v(-5, -84) * mm});
            skLineSegment(sketch, "E31.18.26.3", {"start": v(5, -74) * mm, "end": v(5, -84) * mm});
            skLineSegment(sketch, "E31.18.27.0", {"start": v(-5, -60) * mm, "end": v(5, -60) * mm});
            skLineSegment(sketch, "E31.18.27.1", {"start": v(-5, -70) * mm, "end": v(5, -70) * mm});
            skLineSegment(sketch, "E31.18.27.2", {"start": v(-5, -60) * mm, "end": v(-5, -70) * mm});
            skLineSegment(sketch, "E31.18.27.3", {"start": v(5, -60) * mm, "end": v(5, -70) * mm});
            skLineSegment(sketch, "E31.18.28.0", {"start": v(-5, -46) * mm, "end": v(5, -46) * mm});
            skLineSegment(sketch, "E31.18.28.1", {"start": v(-5, -56) * mm, "end": v(5, -56) * mm});
            skLineSegment(sketch, "E31.18.28.2", {"start": v(-5, -46) * mm, "end": v(-5, -56) * mm});
            skLineSegment(sketch, "E31.18.28.3", {"start": v(5, -46) * mm, "end": v(5, -56) * mm});
            skLineSegment(sketch, "E31.18.29.0", {"start": v(-5, -32) * mm, "end": v(5, -32) * mm});
            skLineSegment(sketch, "E31.18.29.1", {"start": v(-5, -42) * mm, "end": v(5, -42) * mm});
            skLineSegment(sketch, "E31.18.29.2", {"start": v(-5, -32) * mm, "end": v(-5, -42) * mm});
            skLineSegment(sketch, "E31.18.29.3", {"start": v(5, -32) * mm, "end": v(5, -42) * mm});
            skLineSegment(sketch, "E31.18.30.0", {"start": v(-5, -18) * mm, "end": v(5, -18) * mm});
            skLineSegment(sketch, "E31.18.30.1", {"start": v(-5, -28) * mm, "end": v(5, -28) * mm});
            skLineSegment(sketch, "E31.18.30.2", {"start": v(-5, -18) * mm, "end": v(-5, -28) * mm});
            skLineSegment(sketch, "E31.18.30.3", {"start": v(5, -18) * mm, "end": v(5, -28) * mm});
            skLineSegment(sketch, "E31.18.31.0", {"start": v(-5, -4) * mm, "end": v(5, -4) * mm});
            skLineSegment(sketch, "E31.18.31.1", {"start": v(-5, -14) * mm, "end": v(5, -14) * mm});
            skLineSegment(sketch, "E31.18.31.2", {"start": v(-5, -4) * mm, "end": v(-5, -14) * mm});
            skLineSegment(sketch, "E31.18.31.3", {"start": v(5, -4) * mm, "end": v(5, -14) * mm});
            skLineSegment(sketch, "E31.direction1", {"start": v(-257, -448) * mm, "end": v(-243, -448) * mm, "construction": true});
            skLineSegment(sketch, "E31.direction2", {"start": v(-257, -448) * mm, "end": v(-257, -434) * mm, "construction": true});
            skLineSegment(sketch, "E32.bottom", {"start": v(247, -438) * mm, "end": v(257, -438) * mm});
            skLineSegment(sketch, "E32.top", {"start": v(247, -448) * mm, "end": v(257, -448) * mm});
            skLineSegment(sketch, "E32.left", {"start": v(247, -438) * mm, "end": v(247, -448) * mm});
            skLineSegment(sketch, "E32.right", {"start": v(257, -438) * mm, "end": v(257, -448) * mm});
            skLineSegment(sketch, "E33.0.1.0", {"start": v(247, -424) * mm, "end": v(257, -424) * mm});
            skLineSegment(sketch, "E33.0.1.1", {"start": v(247, -434) * mm, "end": v(257, -434) * mm});
            skLineSegment(sketch, "E33.0.1.2", {"start": v(247, -424) * mm, "end": v(247, -434) * mm});
            skLineSegment(sketch, "E33.0.1.3", {"start": v(257, -424) * mm, "end": v(257, -434) * mm});
            skLineSegment(sketch, "E33.0.2.0", {"start": v(247, -410) * mm, "end": v(257, -410) * mm});
            skLineSegment(sketch, "E33.0.2.1", {"start": v(247, -420) * mm, "end": v(257, -420) * mm});
            skLineSegment(sketch, "E33.0.2.2", {"start": v(247, -410) * mm, "end": v(247, -420) * mm});
            skLineSegment(sketch, "E33.0.2.3", {"start": v(257, -410) * mm, "end": v(257, -420) * mm});
            skLineSegment(sketch, "E33.0.3.0", {"start": v(247, -396) * mm, "end": v(257, -396) * mm});
            skLineSegment(sketch, "E33.0.3.1", {"start": v(247, -406) * mm, "end": v(257, -406) * mm});
            skLineSegment(sketch, "E33.0.3.2", {"start": v(247, -396) * mm, "end": v(247, -406) * mm});
            skLineSegment(sketch, "E33.0.3.3", {"start": v(257, -396) * mm, "end": v(257, -406) * mm});
            skLineSegment(sketch, "E33.0.4.0", {"start": v(247, -382) * mm, "end": v(257, -382) * mm});
            skLineSegment(sketch, "E33.0.4.1", {"start": v(247, -392) * mm, "end": v(257, -392) * mm});
            skLineSegment(sketch, "E33.0.4.2", {"start": v(247, -382) * mm, "end": v(247, -392) * mm});
            skLineSegment(sketch, "E33.0.4.3", {"start": v(257, -382) * mm, "end": v(257, -392) * mm});
            skLineSegment(sketch, "E33.0.5.0", {"start": v(247, -368) * mm, "end": v(257, -368) * mm});
            skLineSegment(sketch, "E33.0.5.1", {"start": v(247, -378) * mm, "end": v(257, -378) * mm});
            skLineSegment(sketch, "E33.0.5.2", {"start": v(247, -368) * mm, "end": v(247, -378) * mm});
            skLineSegment(sketch, "E33.0.5.3", {"start": v(257, -368) * mm, "end": v(257, -378) * mm});
            skLineSegment(sketch, "E33.0.6.0", {"start": v(247, -354) * mm, "end": v(257, -354) * mm});
            skLineSegment(sketch, "E33.0.6.1", {"start": v(247, -364) * mm, "end": v(257, -364) * mm});
            skLineSegment(sketch, "E33.0.6.2", {"start": v(247, -354) * mm, "end": v(247, -364) * mm});
            skLineSegment(sketch, "E33.0.6.3", {"start": v(257, -354) * mm, "end": v(257, -364) * mm});
            skLineSegment(sketch, "E33.0.7.0", {"start": v(247, -340) * mm, "end": v(257, -340) * mm});
            skLineSegment(sketch, "E33.0.7.1", {"start": v(247, -350) * mm, "end": v(257, -350) * mm});
            skLineSegment(sketch, "E33.0.7.2", {"start": v(247, -340) * mm, "end": v(247, -350) * mm});
            skLineSegment(sketch, "E33.0.7.3", {"start": v(257, -340) * mm, "end": v(257, -350) * mm});
            skLineSegment(sketch, "E33.0.8.0", {"start": v(247, -326) * mm, "end": v(257, -326) * mm});
            skLineSegment(sketch, "E33.0.8.1", {"start": v(247, -336) * mm, "end": v(257, -336) * mm});
            skLineSegment(sketch, "E33.0.8.2", {"start": v(247, -326) * mm, "end": v(247, -336) * mm});
            skLineSegment(sketch, "E33.0.8.3", {"start": v(257, -326) * mm, "end": v(257, -336) * mm});
            skLineSegment(sketch, "E33.0.9.0", {"start": v(247, -312) * mm, "end": v(257, -312) * mm});
            skLineSegment(sketch, "E33.0.9.1", {"start": v(247, -322) * mm, "end": v(257, -322) * mm});
            skLineSegment(sketch, "E33.0.9.2", {"start": v(247, -312) * mm, "end": v(247, -322) * mm});
            skLineSegment(sketch, "E33.0.9.3", {"start": v(257, -312) * mm, "end": v(257, -322) * mm});
            skLineSegment(sketch, "E33.0.10.0", {"start": v(247, -298) * mm, "end": v(257, -298) * mm});
            skLineSegment(sketch, "E33.0.10.1", {"start": v(247, -308) * mm, "end": v(257, -308) * mm});
            skLineSegment(sketch, "E33.0.10.2", {"start": v(247, -298) * mm, "end": v(247, -308) * mm});
            skLineSegment(sketch, "E33.0.10.3", {"start": v(257, -298) * mm, "end": v(257, -308) * mm});
            skLineSegment(sketch, "E33.0.11.0", {"start": v(247, -284) * mm, "end": v(257, -284) * mm});
            skLineSegment(sketch, "E33.0.11.1", {"start": v(247, -294) * mm, "end": v(257, -294) * mm});
            skLineSegment(sketch, "E33.0.11.2", {"start": v(247, -284) * mm, "end": v(247, -294) * mm});
            skLineSegment(sketch, "E33.0.11.3", {"start": v(257, -284) * mm, "end": v(257, -294) * mm});
            skLineSegment(sketch, "E33.0.12.0", {"start": v(247, -270) * mm, "end": v(257, -270) * mm});
            skLineSegment(sketch, "E33.0.12.1", {"start": v(247, -280) * mm, "end": v(257, -280) * mm});
            skLineSegment(sketch, "E33.0.12.2", {"start": v(247, -270) * mm, "end": v(247, -280) * mm});
            skLineSegment(sketch, "E33.0.12.3", {"start": v(257, -270) * mm, "end": v(257, -280) * mm});
            skLineSegment(sketch, "E33.0.13.0", {"start": v(247, -256) * mm, "end": v(257, -256) * mm});
            skLineSegment(sketch, "E33.0.13.1", {"start": v(247, -266) * mm, "end": v(257, -266) * mm});
            skLineSegment(sketch, "E33.0.13.2", {"start": v(247, -256) * mm, "end": v(247, -266) * mm});
            skLineSegment(sketch, "E33.0.13.3", {"start": v(257, -256) * mm, "end": v(257, -266) * mm});
            skLineSegment(sketch, "E33.0.14.0", {"start": v(247, -242) * mm, "end": v(257, -242) * mm});
            skLineSegment(sketch, "E33.0.14.1", {"start": v(247, -252) * mm, "end": v(257, -252) * mm});
            skLineSegment(sketch, "E33.0.14.2", {"start": v(247, -242) * mm, "end": v(247, -252) * mm});
            skLineSegment(sketch, "E33.0.14.3", {"start": v(257, -242) * mm, "end": v(257, -252) * mm});
            skLineSegment(sketch, "E33.0.15.0", {"start": v(247, -228) * mm, "end": v(257, -228) * mm});
            skLineSegment(sketch, "E33.0.15.1", {"start": v(247, -238) * mm, "end": v(257, -238) * mm});
            skLineSegment(sketch, "E33.0.15.2", {"start": v(247, -228) * mm, "end": v(247, -238) * mm});
            skLineSegment(sketch, "E33.0.15.3", {"start": v(257, -228) * mm, "end": v(257, -238) * mm});
            skLineSegment(sketch, "E33.0.16.0", {"start": v(247, -214) * mm, "end": v(257, -214) * mm});
            skLineSegment(sketch, "E33.0.16.1", {"start": v(247, -224) * mm, "end": v(257, -224) * mm});
            skLineSegment(sketch, "E33.0.16.2", {"start": v(247, -214) * mm, "end": v(247, -224) * mm});
            skLineSegment(sketch, "E33.0.16.3", {"start": v(257, -214) * mm, "end": v(257, -224) * mm});
            skLineSegment(sketch, "E33.0.17.0", {"start": v(247, -200) * mm, "end": v(257, -200) * mm});
            skLineSegment(sketch, "E33.0.17.1", {"start": v(247, -210) * mm, "end": v(257, -210) * mm});
            skLineSegment(sketch, "E33.0.17.2", {"start": v(247, -200) * mm, "end": v(247, -210) * mm});
            skLineSegment(sketch, "E33.0.17.3", {"start": v(257, -200) * mm, "end": v(257, -210) * mm});
            skLineSegment(sketch, "E33.0.18.0", {"start": v(247, -186) * mm, "end": v(257, -186) * mm});
            skLineSegment(sketch, "E33.0.18.1", {"start": v(247, -196) * mm, "end": v(257, -196) * mm});
            skLineSegment(sketch, "E33.0.18.2", {"start": v(247, -186) * mm, "end": v(247, -196) * mm});
            skLineSegment(sketch, "E33.0.18.3", {"start": v(257, -186) * mm, "end": v(257, -196) * mm});
            skLineSegment(sketch, "E33.0.19.0", {"start": v(247, -172) * mm, "end": v(257, -172) * mm});
            skLineSegment(sketch, "E33.0.19.1", {"start": v(247, -182) * mm, "end": v(257, -182) * mm});
            skLineSegment(sketch, "E33.0.19.2", {"start": v(247, -172) * mm, "end": v(247, -182) * mm});
            skLineSegment(sketch, "E33.0.19.3", {"start": v(257, -172) * mm, "end": v(257, -182) * mm});
            skLineSegment(sketch, "E33.0.20.0", {"start": v(247, -158) * mm, "end": v(257, -158) * mm});
            skLineSegment(sketch, "E33.0.20.1", {"start": v(247, -168) * mm, "end": v(257, -168) * mm});
            skLineSegment(sketch, "E33.0.20.2", {"start": v(247, -158) * mm, "end": v(247, -168) * mm});
            skLineSegment(sketch, "E33.0.20.3", {"start": v(257, -158) * mm, "end": v(257, -168) * mm});
            skLineSegment(sketch, "E33.0.21.0", {"start": v(247, -144) * mm, "end": v(257, -144) * mm});
            skLineSegment(sketch, "E33.0.21.1", {"start": v(247, -154) * mm, "end": v(257, -154) * mm});
            skLineSegment(sketch, "E33.0.21.2", {"start": v(247, -144) * mm, "end": v(247, -154) * mm});
            skLineSegment(sketch, "E33.0.21.3", {"start": v(257, -144) * mm, "end": v(257, -154) * mm});
            skLineSegment(sketch, "E33.0.22.0", {"start": v(247, -130) * mm, "end": v(257, -130) * mm});
            skLineSegment(sketch, "E33.0.22.1", {"start": v(247, -140) * mm, "end": v(257, -140) * mm});
            skLineSegment(sketch, "E33.0.22.2", {"start": v(247, -130) * mm, "end": v(247, -140) * mm});
            skLineSegment(sketch, "E33.0.22.3", {"start": v(257, -130) * mm, "end": v(257, -140) * mm});
            skLineSegment(sketch, "E33.0.23.0", {"start": v(247, -116) * mm, "end": v(257, -116) * mm});
            skLineSegment(sketch, "E33.0.23.1", {"start": v(247, -126) * mm, "end": v(257, -126) * mm});
            skLineSegment(sketch, "E33.0.23.2", {"start": v(247, -116) * mm, "end": v(247, -126) * mm});
            skLineSegment(sketch, "E33.0.23.3", {"start": v(257, -116) * mm, "end": v(257, -126) * mm});
            skLineSegment(sketch, "E33.0.24.0", {"start": v(247, -102) * mm, "end": v(257, -102) * mm});
            skLineSegment(sketch, "E33.0.24.1", {"start": v(247, -112) * mm, "end": v(257, -112) * mm});
            skLineSegment(sketch, "E33.0.24.2", {"start": v(247, -102) * mm, "end": v(247, -112) * mm});
            skLineSegment(sketch, "E33.0.24.3", {"start": v(257, -102) * mm, "end": v(257, -112) * mm});
            skLineSegment(sketch, "E33.0.25.0", {"start": v(247, -88) * mm, "end": v(257, -88) * mm});
            skLineSegment(sketch, "E33.0.25.1", {"start": v(247, -98) * mm, "end": v(257, -98) * mm});
            skLineSegment(sketch, "E33.0.25.2", {"start": v(247, -88) * mm, "end": v(247, -98) * mm});
            skLineSegment(sketch, "E33.0.25.3", {"start": v(257, -88) * mm, "end": v(257, -98) * mm});
            skLineSegment(sketch, "E33.0.26.0", {"start": v(247, -74) * mm, "end": v(257, -74) * mm});
            skLineSegment(sketch, "E33.0.26.1", {"start": v(247, -84) * mm, "end": v(257, -84) * mm});
            skLineSegment(sketch, "E33.0.26.2", {"start": v(247, -74) * mm, "end": v(247, -84) * mm});
            skLineSegment(sketch, "E33.0.26.3", {"start": v(257, -74) * mm, "end": v(257, -84) * mm});
            skLineSegment(sketch, "E33.0.27.0", {"start": v(247, -60) * mm, "end": v(257, -60) * mm});
            skLineSegment(sketch, "E33.0.27.1", {"start": v(247, -70) * mm, "end": v(257, -70) * mm});
            skLineSegment(sketch, "E33.0.27.2", {"start": v(247, -60) * mm, "end": v(247, -70) * mm});
            skLineSegment(sketch, "E33.0.27.3", {"start": v(257, -60) * mm, "end": v(257, -70) * mm});
            skLineSegment(sketch, "E33.0.28.0", {"start": v(247, -46) * mm, "end": v(257, -46) * mm});
            skLineSegment(sketch, "E33.0.28.1", {"start": v(247, -56) * mm, "end": v(257, -56) * mm});
            skLineSegment(sketch, "E33.0.28.2", {"start": v(247, -46) * mm, "end": v(247, -56) * mm});
            skLineSegment(sketch, "E33.0.28.3", {"start": v(257, -46) * mm, "end": v(257, -56) * mm});
            skLineSegment(sketch, "E33.0.29.0", {"start": v(247, -32) * mm, "end": v(257, -32) * mm});
            skLineSegment(sketch, "E33.0.29.1", {"start": v(247, -42) * mm, "end": v(257, -42) * mm});
            skLineSegment(sketch, "E33.0.29.2", {"start": v(247, -32) * mm, "end": v(247, -42) * mm});
            skLineSegment(sketch, "E33.0.29.3", {"start": v(257, -32) * mm, "end": v(257, -42) * mm});
            skLineSegment(sketch, "E33.0.30.0", {"start": v(247, -18) * mm, "end": v(257, -18) * mm});
            skLineSegment(sketch, "E33.0.30.1", {"start": v(247, -28) * mm, "end": v(257, -28) * mm});
            skLineSegment(sketch, "E33.0.30.2", {"start": v(247, -18) * mm, "end": v(247, -28) * mm});
            skLineSegment(sketch, "E33.0.30.3", {"start": v(257, -18) * mm, "end": v(257, -28) * mm});
            skLineSegment(sketch, "E33.0.31.0", {"start": v(247, -4) * mm, "end": v(257, -4) * mm});
            skLineSegment(sketch, "E33.0.31.1", {"start": v(247, -14) * mm, "end": v(257, -14) * mm});
            skLineSegment(sketch, "E33.0.31.2", {"start": v(247, -4) * mm, "end": v(247, -14) * mm});
            skLineSegment(sketch, "E33.0.31.3", {"start": v(257, -4) * mm, "end": v(257, -14) * mm});
            skLineSegment(sketch, "E33.1.0.0", {"start": v(233, -438) * mm, "end": v(243, -438) * mm});
            skLineSegment(sketch, "E33.1.0.1", {"start": v(233, -448) * mm, "end": v(243, -448) * mm});
            skLineSegment(sketch, "E33.1.0.2", {"start": v(233, -438) * mm, "end": v(233, -448) * mm});
            skLineSegment(sketch, "E33.1.0.3", {"start": v(243, -438) * mm, "end": v(243, -448) * mm});
            skLineSegment(sketch, "E33.1.1.0", {"start": v(233, -424) * mm, "end": v(243, -424) * mm});
            skLineSegment(sketch, "E33.1.1.1", {"start": v(233, -434) * mm, "end": v(243, -434) * mm});
            skLineSegment(sketch, "E33.1.1.2", {"start": v(233, -424) * mm, "end": v(233, -434) * mm});
            skLineSegment(sketch, "E33.1.1.3", {"start": v(243, -424) * mm, "end": v(243, -434) * mm});
            skLineSegment(sketch, "E33.1.2.0", {"start": v(233, -410) * mm, "end": v(243, -410) * mm});
            skLineSegment(sketch, "E33.1.2.1", {"start": v(233, -420) * mm, "end": v(243, -420) * mm});
            skLineSegment(sketch, "E33.1.2.2", {"start": v(233, -410) * mm, "end": v(233, -420) * mm});
            skLineSegment(sketch, "E33.1.2.3", {"start": v(243, -410) * mm, "end": v(243, -420) * mm});
            skLineSegment(sketch, "E33.1.3.0", {"start": v(233, -396) * mm, "end": v(243, -396) * mm});
            skLineSegment(sketch, "E33.1.3.1", {"start": v(233, -406) * mm, "end": v(243, -406) * mm});
            skLineSegment(sketch, "E33.1.3.2", {"start": v(233, -396) * mm, "end": v(233, -406) * mm});
            skLineSegment(sketch, "E33.1.3.3", {"start": v(243, -396) * mm, "end": v(243, -406) * mm});
            skLineSegment(sketch, "E33.1.4.0", {"start": v(233, -382) * mm, "end": v(243, -382) * mm});
            skLineSegment(sketch, "E33.1.4.1", {"start": v(233, -392) * mm, "end": v(243, -392) * mm});
            skLineSegment(sketch, "E33.1.4.2", {"start": v(233, -382) * mm, "end": v(233, -392) * mm});
            skLineSegment(sketch, "E33.1.4.3", {"start": v(243, -382) * mm, "end": v(243, -392) * mm});
            skLineSegment(sketch, "E33.1.5.0", {"start": v(233, -368) * mm, "end": v(243, -368) * mm});
            skLineSegment(sketch, "E33.1.5.1", {"start": v(233, -378) * mm, "end": v(243, -378) * mm});
            skLineSegment(sketch, "E33.1.5.2", {"start": v(233, -368) * mm, "end": v(233, -378) * mm});
            skLineSegment(sketch, "E33.1.5.3", {"start": v(243, -368) * mm, "end": v(243, -378) * mm});
            skLineSegment(sketch, "E33.1.6.0", {"start": v(233, -354) * mm, "end": v(243, -354) * mm});
            skLineSegment(sketch, "E33.1.6.1", {"start": v(233, -364) * mm, "end": v(243, -364) * mm});
            skLineSegment(sketch, "E33.1.6.2", {"start": v(233, -354) * mm, "end": v(233, -364) * mm});
            skLineSegment(sketch, "E33.1.6.3", {"start": v(243, -354) * mm, "end": v(243, -364) * mm});
            skLineSegment(sketch, "E33.1.7.0", {"start": v(233, -340) * mm, "end": v(243, -340) * mm});
            skLineSegment(sketch, "E33.1.7.1", {"start": v(233, -350) * mm, "end": v(243, -350) * mm});
            skLineSegment(sketch, "E33.1.7.2", {"start": v(233, -340) * mm, "end": v(233, -350) * mm});
            skLineSegment(sketch, "E33.1.7.3", {"start": v(243, -340) * mm, "end": v(243, -350) * mm});
            skLineSegment(sketch, "E33.1.8.0", {"start": v(233, -326) * mm, "end": v(243, -326) * mm});
            skLineSegment(sketch, "E33.1.8.1", {"start": v(233, -336) * mm, "end": v(243, -336) * mm});
            skLineSegment(sketch, "E33.1.8.2", {"start": v(233, -326) * mm, "end": v(233, -336) * mm});
            skLineSegment(sketch, "E33.1.8.3", {"start": v(243, -326) * mm, "end": v(243, -336) * mm});
            skLineSegment(sketch, "E33.1.9.0", {"start": v(233, -312) * mm, "end": v(243, -312) * mm});
            skLineSegment(sketch, "E33.1.9.1", {"start": v(233, -322) * mm, "end": v(243, -322) * mm});
            skLineSegment(sketch, "E33.1.9.2", {"start": v(233, -312) * mm, "end": v(233, -322) * mm});
            skLineSegment(sketch, "E33.1.9.3", {"start": v(243, -312) * mm, "end": v(243, -322) * mm});
            skLineSegment(sketch, "E33.1.10.0", {"start": v(233, -298) * mm, "end": v(243, -298) * mm});
            skLineSegment(sketch, "E33.1.10.1", {"start": v(233, -308) * mm, "end": v(243, -308) * mm});
            skLineSegment(sketch, "E33.1.10.2", {"start": v(233, -298) * mm, "end": v(233, -308) * mm});
            skLineSegment(sketch, "E33.1.10.3", {"start": v(243, -298) * mm, "end": v(243, -308) * mm});
            skLineSegment(sketch, "E33.1.11.0", {"start": v(233, -284) * mm, "end": v(243, -284) * mm});
            skLineSegment(sketch, "E33.1.11.1", {"start": v(233, -294) * mm, "end": v(243, -294) * mm});
            skLineSegment(sketch, "E33.1.11.2", {"start": v(233, -284) * mm, "end": v(233, -294) * mm});
            skLineSegment(sketch, "E33.1.11.3", {"start": v(243, -284) * mm, "end": v(243, -294) * mm});
            skLineSegment(sketch, "E33.1.12.0", {"start": v(233, -270) * mm, "end": v(243, -270) * mm});
            skLineSegment(sketch, "E33.1.12.1", {"start": v(233, -280) * mm, "end": v(243, -280) * mm});
            skLineSegment(sketch, "E33.1.12.2", {"start": v(233, -270) * mm, "end": v(233, -280) * mm});
            skLineSegment(sketch, "E33.1.12.3", {"start": v(243, -270) * mm, "end": v(243, -280) * mm});
            skLineSegment(sketch, "E33.1.13.0", {"start": v(233, -256) * mm, "end": v(243, -256) * mm});
            skLineSegment(sketch, "E33.1.13.1", {"start": v(233, -266) * mm, "end": v(243, -266) * mm});
            skLineSegment(sketch, "E33.1.13.2", {"start": v(233, -256) * mm, "end": v(233, -266) * mm});
            skLineSegment(sketch, "E33.1.13.3", {"start": v(243, -256) * mm, "end": v(243, -266) * mm});
            skLineSegment(sketch, "E33.1.14.0", {"start": v(233, -242) * mm, "end": v(243, -242) * mm});
            skLineSegment(sketch, "E33.1.14.1", {"start": v(233, -252) * mm, "end": v(243, -252) * mm});
            skLineSegment(sketch, "E33.1.14.2", {"start": v(233, -242) * mm, "end": v(233, -252) * mm});
            skLineSegment(sketch, "E33.1.14.3", {"start": v(243, -242) * mm, "end": v(243, -252) * mm});
            skLineSegment(sketch, "E33.1.15.0", {"start": v(233, -228) * mm, "end": v(243, -228) * mm});
            skLineSegment(sketch, "E33.1.15.1", {"start": v(233, -238) * mm, "end": v(243, -238) * mm});
            skLineSegment(sketch, "E33.1.15.2", {"start": v(233, -228) * mm, "end": v(233, -238) * mm});
            skLineSegment(sketch, "E33.1.15.3", {"start": v(243, -228) * mm, "end": v(243, -238) * mm});
            skLineSegment(sketch, "E33.1.16.0", {"start": v(233, -214) * mm, "end": v(243, -214) * mm});
            skLineSegment(sketch, "E33.1.16.1", {"start": v(233, -224) * mm, "end": v(243, -224) * mm});
            skLineSegment(sketch, "E33.1.16.2", {"start": v(233, -214) * mm, "end": v(233, -224) * mm});
            skLineSegment(sketch, "E33.1.16.3", {"start": v(243, -214) * mm, "end": v(243, -224) * mm});
            skLineSegment(sketch, "E33.1.17.0", {"start": v(233, -200) * mm, "end": v(243, -200) * mm});
            skLineSegment(sketch, "E33.1.17.1", {"start": v(233, -210) * mm, "end": v(243, -210) * mm});
            skLineSegment(sketch, "E33.1.17.2", {"start": v(233, -200) * mm, "end": v(233, -210) * mm});
            skLineSegment(sketch, "E33.1.17.3", {"start": v(243, -200) * mm, "end": v(243, -210) * mm});
            skLineSegment(sketch, "E33.1.18.0", {"start": v(233, -186) * mm, "end": v(243, -186) * mm});
            skLineSegment(sketch, "E33.1.18.1", {"start": v(233, -196) * mm, "end": v(243, -196) * mm});
            skLineSegment(sketch, "E33.1.18.2", {"start": v(233, -186) * mm, "end": v(233, -196) * mm});
            skLineSegment(sketch, "E33.1.18.3", {"start": v(243, -186) * mm, "end": v(243, -196) * mm});
            skLineSegment(sketch, "E33.1.19.0", {"start": v(233, -172) * mm, "end": v(243, -172) * mm});
            skLineSegment(sketch, "E33.1.19.1", {"start": v(233, -182) * mm, "end": v(243, -182) * mm});
            skLineSegment(sketch, "E33.1.19.2", {"start": v(233, -172) * mm, "end": v(233, -182) * mm});
            skLineSegment(sketch, "E33.1.19.3", {"start": v(243, -172) * mm, "end": v(243, -182) * mm});
            skLineSegment(sketch, "E33.1.20.0", {"start": v(233, -158) * mm, "end": v(243, -158) * mm});
            skLineSegment(sketch, "E33.1.20.1", {"start": v(233, -168) * mm, "end": v(243, -168) * mm});
            skLineSegment(sketch, "E33.1.20.2", {"start": v(233, -158) * mm, "end": v(233, -168) * mm});
            skLineSegment(sketch, "E33.1.20.3", {"start": v(243, -158) * mm, "end": v(243, -168) * mm});
            skLineSegment(sketch, "E33.1.21.0", {"start": v(233, -144) * mm, "end": v(243, -144) * mm});
            skLineSegment(sketch, "E33.1.21.1", {"start": v(233, -154) * mm, "end": v(243, -154) * mm});
            skLineSegment(sketch, "E33.1.21.2", {"start": v(233, -144) * mm, "end": v(233, -154) * mm});
            skLineSegment(sketch, "E33.1.21.3", {"start": v(243, -144) * mm, "end": v(243, -154) * mm});
            skLineSegment(sketch, "E33.1.22.0", {"start": v(233, -130) * mm, "end": v(243, -130) * mm});
            skLineSegment(sketch, "E33.1.22.1", {"start": v(233, -140) * mm, "end": v(243, -140) * mm});
            skLineSegment(sketch, "E33.1.22.2", {"start": v(233, -130) * mm, "end": v(233, -140) * mm});
            skLineSegment(sketch, "E33.1.22.3", {"start": v(243, -130) * mm, "end": v(243, -140) * mm});
            skLineSegment(sketch, "E33.1.23.0", {"start": v(233, -116) * mm, "end": v(243, -116) * mm});
            skLineSegment(sketch, "E33.1.23.1", {"start": v(233, -126) * mm, "end": v(243, -126) * mm});
            skLineSegment(sketch, "E33.1.23.2", {"start": v(233, -116) * mm, "end": v(233, -126) * mm});
            skLineSegment(sketch, "E33.1.23.3", {"start": v(243, -116) * mm, "end": v(243, -126) * mm});
            skLineSegment(sketch, "E33.1.24.0", {"start": v(233, -102) * mm, "end": v(243, -102) * mm});
            skLineSegment(sketch, "E33.1.24.1", {"start": v(233, -112) * mm, "end": v(243, -112) * mm});
            skLineSegment(sketch, "E33.1.24.2", {"start": v(233, -102) * mm, "end": v(233, -112) * mm});
            skLineSegment(sketch, "E33.1.24.3", {"start": v(243, -102) * mm, "end": v(243, -112) * mm});
            skLineSegment(sketch, "E33.1.25.0", {"start": v(233, -88) * mm, "end": v(243, -88) * mm});
            skLineSegment(sketch, "E33.1.25.1", {"start": v(233, -98) * mm, "end": v(243, -98) * mm});
            skLineSegment(sketch, "E33.1.25.2", {"start": v(233, -88) * mm, "end": v(233, -98) * mm});
            skLineSegment(sketch, "E33.1.25.3", {"start": v(243, -88) * mm, "end": v(243, -98) * mm});
            skLineSegment(sketch, "E33.1.26.0", {"start": v(233, -74) * mm, "end": v(243, -74) * mm});
            skLineSegment(sketch, "E33.1.26.1", {"start": v(233, -84) * mm, "end": v(243, -84) * mm});
            skLineSegment(sketch, "E33.1.26.2", {"start": v(233, -74) * mm, "end": v(233, -84) * mm});
            skLineSegment(sketch, "E33.1.26.3", {"start": v(243, -74) * mm, "end": v(243, -84) * mm});
            skLineSegment(sketch, "E33.1.27.0", {"start": v(233, -60) * mm, "end": v(243, -60) * mm});
            skLineSegment(sketch, "E33.1.27.1", {"start": v(233, -70) * mm, "end": v(243, -70) * mm});
            skLineSegment(sketch, "E33.1.27.2", {"start": v(233, -60) * mm, "end": v(233, -70) * mm});
            skLineSegment(sketch, "E33.1.27.3", {"start": v(243, -60) * mm, "end": v(243, -70) * mm});
            skLineSegment(sketch, "E33.1.28.0", {"start": v(233, -46) * mm, "end": v(243, -46) * mm});
            skLineSegment(sketch, "E33.1.28.1", {"start": v(233, -56) * mm, "end": v(243, -56) * mm});
            skLineSegment(sketch, "E33.1.28.2", {"start": v(233, -46) * mm, "end": v(233, -56) * mm});
            skLineSegment(sketch, "E33.1.28.3", {"start": v(243, -46) * mm, "end": v(243, -56) * mm});
            skLineSegment(sketch, "E33.1.29.0", {"start": v(233, -32) * mm, "end": v(243, -32) * mm});
            skLineSegment(sketch, "E33.1.29.1", {"start": v(233, -42) * mm, "end": v(243, -42) * mm});
            skLineSegment(sketch, "E33.1.29.2", {"start": v(233, -32) * mm, "end": v(233, -42) * mm});
            skLineSegment(sketch, "E33.1.29.3", {"start": v(243, -32) * mm, "end": v(243, -42) * mm});
            skLineSegment(sketch, "E33.1.30.0", {"start": v(233, -18) * mm, "end": v(243, -18) * mm});
            skLineSegment(sketch, "E33.1.30.1", {"start": v(233, -28) * mm, "end": v(243, -28) * mm});
            skLineSegment(sketch, "E33.1.30.2", {"start": v(233, -18) * mm, "end": v(233, -28) * mm});
            skLineSegment(sketch, "E33.1.30.3", {"start": v(243, -18) * mm, "end": v(243, -28) * mm});
            skLineSegment(sketch, "E33.1.31.0", {"start": v(233, -4) * mm, "end": v(243, -4) * mm});
            skLineSegment(sketch, "E33.1.31.1", {"start": v(233, -14) * mm, "end": v(243, -14) * mm});
            skLineSegment(sketch, "E33.1.31.2", {"start": v(233, -4) * mm, "end": v(233, -14) * mm});
            skLineSegment(sketch, "E33.1.31.3", {"start": v(243, -4) * mm, "end": v(243, -14) * mm});
            skLineSegment(sketch, "E33.2.0.0", {"start": v(219, -438) * mm, "end": v(229, -438) * mm});
            skLineSegment(sketch, "E33.2.0.1", {"start": v(219, -448) * mm, "end": v(229, -448) * mm});
            skLineSegment(sketch, "E33.2.0.2", {"start": v(219, -438) * mm, "end": v(219, -448) * mm});
            skLineSegment(sketch, "E33.2.0.3", {"start": v(229, -438) * mm, "end": v(229, -448) * mm});
            skLineSegment(sketch, "E33.2.1.0", {"start": v(219, -424) * mm, "end": v(229, -424) * mm});
            skLineSegment(sketch, "E33.2.1.1", {"start": v(219, -434) * mm, "end": v(229, -434) * mm});
            skLineSegment(sketch, "E33.2.1.2", {"start": v(219, -424) * mm, "end": v(219, -434) * mm});
            skLineSegment(sketch, "E33.2.1.3", {"start": v(229, -424) * mm, "end": v(229, -434) * mm});
            skLineSegment(sketch, "E33.2.2.0", {"start": v(219, -410) * mm, "end": v(229, -410) * mm});
            skLineSegment(sketch, "E33.2.2.1", {"start": v(219, -420) * mm, "end": v(229, -420) * mm});
            skLineSegment(sketch, "E33.2.2.2", {"start": v(219, -410) * mm, "end": v(219, -420) * mm});
            skLineSegment(sketch, "E33.2.2.3", {"start": v(229, -410) * mm, "end": v(229, -420) * mm});
            skLineSegment(sketch, "E33.2.3.0", {"start": v(219, -396) * mm, "end": v(229, -396) * mm});
            skLineSegment(sketch, "E33.2.3.1", {"start": v(219, -406) * mm, "end": v(229, -406) * mm});
            skLineSegment(sketch, "E33.2.3.2", {"start": v(219, -396) * mm, "end": v(219, -406) * mm});
            skLineSegment(sketch, "E33.2.3.3", {"start": v(229, -396) * mm, "end": v(229, -406) * mm});
            skLineSegment(sketch, "E33.2.4.0", {"start": v(219, -382) * mm, "end": v(229, -382) * mm});
            skLineSegment(sketch, "E33.2.4.1", {"start": v(219, -392) * mm, "end": v(229, -392) * mm});
            skLineSegment(sketch, "E33.2.4.2", {"start": v(219, -382) * mm, "end": v(219, -392) * mm});
            skLineSegment(sketch, "E33.2.4.3", {"start": v(229, -382) * mm, "end": v(229, -392) * mm});
            skLineSegment(sketch, "E33.2.5.0", {"start": v(219, -368) * mm, "end": v(229, -368) * mm});
            skLineSegment(sketch, "E33.2.5.1", {"start": v(219, -378) * mm, "end": v(229, -378) * mm});
            skLineSegment(sketch, "E33.2.5.2", {"start": v(219, -368) * mm, "end": v(219, -378) * mm});
            skLineSegment(sketch, "E33.2.5.3", {"start": v(229, -368) * mm, "end": v(229, -378) * mm});
            skLineSegment(sketch, "E33.2.6.0", {"start": v(219, -354) * mm, "end": v(229, -354) * mm});
            skLineSegment(sketch, "E33.2.6.1", {"start": v(219, -364) * mm, "end": v(229, -364) * mm});
            skLineSegment(sketch, "E33.2.6.2", {"start": v(219, -354) * mm, "end": v(219, -364) * mm});
            skLineSegment(sketch, "E33.2.6.3", {"start": v(229, -354) * mm, "end": v(229, -364) * mm});
            skLineSegment(sketch, "E33.2.7.0", {"start": v(219, -340) * mm, "end": v(229, -340) * mm});
            skLineSegment(sketch, "E33.2.7.1", {"start": v(219, -350) * mm, "end": v(229, -350) * mm});
            skLineSegment(sketch, "E33.2.7.2", {"start": v(219, -340) * mm, "end": v(219, -350) * mm});
            skLineSegment(sketch, "E33.2.7.3", {"start": v(229, -340) * mm, "end": v(229, -350) * mm});
            skLineSegment(sketch, "E33.2.8.0", {"start": v(219, -326) * mm, "end": v(229, -326) * mm});
            skLineSegment(sketch, "E33.2.8.1", {"start": v(219, -336) * mm, "end": v(229, -336) * mm});
            skLineSegment(sketch, "E33.2.8.2", {"start": v(219, -326) * mm, "end": v(219, -336) * mm});
            skLineSegment(sketch, "E33.2.8.3", {"start": v(229, -326) * mm, "end": v(229, -336) * mm});
            skLineSegment(sketch, "E33.2.9.0", {"start": v(219, -312) * mm, "end": v(229, -312) * mm});
            skLineSegment(sketch, "E33.2.9.1", {"start": v(219, -322) * mm, "end": v(229, -322) * mm});
            skLineSegment(sketch, "E33.2.9.2", {"start": v(219, -312) * mm, "end": v(219, -322) * mm});
            skLineSegment(sketch, "E33.2.9.3", {"start": v(229, -312) * mm, "end": v(229, -322) * mm});
            skLineSegment(sketch, "E33.2.10.0", {"start": v(219, -298) * mm, "end": v(229, -298) * mm});
            skLineSegment(sketch, "E33.2.10.1", {"start": v(219, -308) * mm, "end": v(229, -308) * mm});
            skLineSegment(sketch, "E33.2.10.2", {"start": v(219, -298) * mm, "end": v(219, -308) * mm});
            skLineSegment(sketch, "E33.2.10.3", {"start": v(229, -298) * mm, "end": v(229, -308) * mm});
            skLineSegment(sketch, "E33.2.11.0", {"start": v(219, -284) * mm, "end": v(229, -284) * mm});
            skLineSegment(sketch, "E33.2.11.1", {"start": v(219, -294) * mm, "end": v(229, -294) * mm});
            skLineSegment(sketch, "E33.2.11.2", {"start": v(219, -284) * mm, "end": v(219, -294) * mm});
            skLineSegment(sketch, "E33.2.11.3", {"start": v(229, -284) * mm, "end": v(229, -294) * mm});
            skLineSegment(sketch, "E33.2.12.0", {"start": v(219, -270) * mm, "end": v(229, -270) * mm});
            skLineSegment(sketch, "E33.2.12.1", {"start": v(219, -280) * mm, "end": v(229, -280) * mm});
            skLineSegment(sketch, "E33.2.12.2", {"start": v(219, -270) * mm, "end": v(219, -280) * mm});
            skLineSegment(sketch, "E33.2.12.3", {"start": v(229, -270) * mm, "end": v(229, -280) * mm});
            skLineSegment(sketch, "E33.2.13.0", {"start": v(219, -256) * mm, "end": v(229, -256) * mm});
            skLineSegment(sketch, "E33.2.13.1", {"start": v(219, -266) * mm, "end": v(229, -266) * mm});
            skLineSegment(sketch, "E33.2.13.2", {"start": v(219, -256) * mm, "end": v(219, -266) * mm});
            skLineSegment(sketch, "E33.2.13.3", {"start": v(229, -256) * mm, "end": v(229, -266) * mm});
            skLineSegment(sketch, "E33.2.14.0", {"start": v(219, -242) * mm, "end": v(229, -242) * mm});
            skLineSegment(sketch, "E33.2.14.1", {"start": v(219, -252) * mm, "end": v(229, -252) * mm});
            skLineSegment(sketch, "E33.2.14.2", {"start": v(219, -242) * mm, "end": v(219, -252) * mm});
            skLineSegment(sketch, "E33.2.14.3", {"start": v(229, -242) * mm, "end": v(229, -252) * mm});
            skLineSegment(sketch, "E33.2.15.0", {"start": v(219, -228) * mm, "end": v(229, -228) * mm});
            skLineSegment(sketch, "E33.2.15.1", {"start": v(219, -238) * mm, "end": v(229, -238) * mm});
            skLineSegment(sketch, "E33.2.15.2", {"start": v(219, -228) * mm, "end": v(219, -238) * mm});
            skLineSegment(sketch, "E33.2.15.3", {"start": v(229, -228) * mm, "end": v(229, -238) * mm});
            skLineSegment(sketch, "E33.2.16.0", {"start": v(219, -214) * mm, "end": v(229, -214) * mm});
            skLineSegment(sketch, "E33.2.16.1", {"start": v(219, -224) * mm, "end": v(229, -224) * mm});
            skLineSegment(sketch, "E33.2.16.2", {"start": v(219, -214) * mm, "end": v(219, -224) * mm});
            skLineSegment(sketch, "E33.2.16.3", {"start": v(229, -214) * mm, "end": v(229, -224) * mm});
            skLineSegment(sketch, "E33.2.17.0", {"start": v(219, -200) * mm, "end": v(229, -200) * mm});
            skLineSegment(sketch, "E33.2.17.1", {"start": v(219, -210) * mm, "end": v(229, -210) * mm});
            skLineSegment(sketch, "E33.2.17.2", {"start": v(219, -200) * mm, "end": v(219, -210) * mm});
            skLineSegment(sketch, "E33.2.17.3", {"start": v(229, -200) * mm, "end": v(229, -210) * mm});
            skLineSegment(sketch, "E33.2.18.0", {"start": v(219, -186) * mm, "end": v(229, -186) * mm});
            skLineSegment(sketch, "E33.2.18.1", {"start": v(219, -196) * mm, "end": v(229, -196) * mm});
            skLineSegment(sketch, "E33.2.18.2", {"start": v(219, -186) * mm, "end": v(219, -196) * mm});
            skLineSegment(sketch, "E33.2.18.3", {"start": v(229, -186) * mm, "end": v(229, -196) * mm});
            skLineSegment(sketch, "E33.2.19.0", {"start": v(219, -172) * mm, "end": v(229, -172) * mm});
            skLineSegment(sketch, "E33.2.19.1", {"start": v(219, -182) * mm, "end": v(229, -182) * mm});
            skLineSegment(sketch, "E33.2.19.2", {"start": v(219, -172) * mm, "end": v(219, -182) * mm});
            skLineSegment(sketch, "E33.2.19.3", {"start": v(229, -172) * mm, "end": v(229, -182) * mm});
            skLineSegment(sketch, "E33.2.20.0", {"start": v(219, -158) * mm, "end": v(229, -158) * mm});
            skLineSegment(sketch, "E33.2.20.1", {"start": v(219, -168) * mm, "end": v(229, -168) * mm});
            skLineSegment(sketch, "E33.2.20.2", {"start": v(219, -158) * mm, "end": v(219, -168) * mm});
            skLineSegment(sketch, "E33.2.20.3", {"start": v(229, -158) * mm, "end": v(229, -168) * mm});
            skLineSegment(sketch, "E33.2.21.0", {"start": v(219, -144) * mm, "end": v(229, -144) * mm});
            skLineSegment(sketch, "E33.2.21.1", {"start": v(219, -154) * mm, "end": v(229, -154) * mm});
            skLineSegment(sketch, "E33.2.21.2", {"start": v(219, -144) * mm, "end": v(219, -154) * mm});
            skLineSegment(sketch, "E33.2.21.3", {"start": v(229, -144) * mm, "end": v(229, -154) * mm});
            skLineSegment(sketch, "E33.2.22.0", {"start": v(219, -130) * mm, "end": v(229, -130) * mm});
            skLineSegment(sketch, "E33.2.22.1", {"start": v(219, -140) * mm, "end": v(229, -140) * mm});
            skLineSegment(sketch, "E33.2.22.2", {"start": v(219, -130) * mm, "end": v(219, -140) * mm});
            skLineSegment(sketch, "E33.2.22.3", {"start": v(229, -130) * mm, "end": v(229, -140) * mm});
            skLineSegment(sketch, "E33.2.23.0", {"start": v(219, -116) * mm, "end": v(229, -116) * mm});
            skLineSegment(sketch, "E33.2.23.1", {"start": v(219, -126) * mm, "end": v(229, -126) * mm});
            skLineSegment(sketch, "E33.2.23.2", {"start": v(219, -116) * mm, "end": v(219, -126) * mm});
            skLineSegment(sketch, "E33.2.23.3", {"start": v(229, -116) * mm, "end": v(229, -126) * mm});
            skLineSegment(sketch, "E33.2.24.0", {"start": v(219, -102) * mm, "end": v(229, -102) * mm});
            skLineSegment(sketch, "E33.2.24.1", {"start": v(219, -112) * mm, "end": v(229, -112) * mm});
            skLineSegment(sketch, "E33.2.24.2", {"start": v(219, -102) * mm, "end": v(219, -112) * mm});
            skLineSegment(sketch, "E33.2.24.3", {"start": v(229, -102) * mm, "end": v(229, -112) * mm});
            skLineSegment(sketch, "E33.2.25.0", {"start": v(219, -88) * mm, "end": v(229, -88) * mm});
            skLineSegment(sketch, "E33.2.25.1", {"start": v(219, -98) * mm, "end": v(229, -98) * mm});
            skLineSegment(sketch, "E33.2.25.2", {"start": v(219, -88) * mm, "end": v(219, -98) * mm});
            skLineSegment(sketch, "E33.2.25.3", {"start": v(229, -88) * mm, "end": v(229, -98) * mm});
            skLineSegment(sketch, "E33.2.26.0", {"start": v(219, -74) * mm, "end": v(229, -74) * mm});
            skLineSegment(sketch, "E33.2.26.1", {"start": v(219, -84) * mm, "end": v(229, -84) * mm});
            skLineSegment(sketch, "E33.2.26.2", {"start": v(219, -74) * mm, "end": v(219, -84) * mm});
            skLineSegment(sketch, "E33.2.26.3", {"start": v(229, -74) * mm, "end": v(229, -84) * mm});
            skLineSegment(sketch, "E33.2.27.0", {"start": v(219, -60) * mm, "end": v(229, -60) * mm});
            skLineSegment(sketch, "E33.2.27.1", {"start": v(219, -70) * mm, "end": v(229, -70) * mm});
            skLineSegment(sketch, "E33.2.27.2", {"start": v(219, -60) * mm, "end": v(219, -70) * mm});
            skLineSegment(sketch, "E33.2.27.3", {"start": v(229, -60) * mm, "end": v(229, -70) * mm});
            skLineSegment(sketch, "E33.2.28.0", {"start": v(219, -46) * mm, "end": v(229, -46) * mm});
            skLineSegment(sketch, "E33.2.28.1", {"start": v(219, -56) * mm, "end": v(229, -56) * mm});
            skLineSegment(sketch, "E33.2.28.2", {"start": v(219, -46) * mm, "end": v(219, -56) * mm});
            skLineSegment(sketch, "E33.2.28.3", {"start": v(229, -46) * mm, "end": v(229, -56) * mm});
            skLineSegment(sketch, "E33.2.29.0", {"start": v(219, -32) * mm, "end": v(229, -32) * mm});
            skLineSegment(sketch, "E33.2.29.1", {"start": v(219, -42) * mm, "end": v(229, -42) * mm});
            skLineSegment(sketch, "E33.2.29.2", {"start": v(219, -32) * mm, "end": v(219, -42) * mm});
            skLineSegment(sketch, "E33.2.29.3", {"start": v(229, -32) * mm, "end": v(229, -42) * mm});
            skLineSegment(sketch, "E33.2.30.0", {"start": v(219, -18) * mm, "end": v(229, -18) * mm});
            skLineSegment(sketch, "E33.2.30.1", {"start": v(219, -28) * mm, "end": v(229, -28) * mm});
            skLineSegment(sketch, "E33.2.30.2", {"start": v(219, -18) * mm, "end": v(219, -28) * mm});
            skLineSegment(sketch, "E33.2.30.3", {"start": v(229, -18) * mm, "end": v(229, -28) * mm});
            skLineSegment(sketch, "E33.2.31.0", {"start": v(219, -4) * mm, "end": v(229, -4) * mm});
            skLineSegment(sketch, "E33.2.31.1", {"start": v(219, -14) * mm, "end": v(229, -14) * mm});
            skLineSegment(sketch, "E33.2.31.2", {"start": v(219, -4) * mm, "end": v(219, -14) * mm});
            skLineSegment(sketch, "E33.2.31.3", {"start": v(229, -4) * mm, "end": v(229, -14) * mm});
            skLineSegment(sketch, "E33.3.0.0", {"start": v(205, -438) * mm, "end": v(215, -438) * mm});
            skLineSegment(sketch, "E33.3.0.1", {"start": v(205, -448) * mm, "end": v(215, -448) * mm});
            skLineSegment(sketch, "E33.3.0.2", {"start": v(205, -438) * mm, "end": v(205, -448) * mm});
            skLineSegment(sketch, "E33.3.0.3", {"start": v(215, -438) * mm, "end": v(215, -448) * mm});
            skLineSegment(sketch, "E33.3.1.0", {"start": v(205, -424) * mm, "end": v(215, -424) * mm});
            skLineSegment(sketch, "E33.3.1.1", {"start": v(205, -434) * mm, "end": v(215, -434) * mm});
            skLineSegment(sketch, "E33.3.1.2", {"start": v(205, -424) * mm, "end": v(205, -434) * mm});
            skLineSegment(sketch, "E33.3.1.3", {"start": v(215, -424) * mm, "end": v(215, -434) * mm});
            skLineSegment(sketch, "E33.3.2.0", {"start": v(205, -410) * mm, "end": v(215, -410) * mm});
            skLineSegment(sketch, "E33.3.2.1", {"start": v(205, -420) * mm, "end": v(215, -420) * mm});
            skLineSegment(sketch, "E33.3.2.2", {"start": v(205, -410) * mm, "end": v(205, -420) * mm});
            skLineSegment(sketch, "E33.3.2.3", {"start": v(215, -410) * mm, "end": v(215, -420) * mm});
            skLineSegment(sketch, "E33.3.3.0", {"start": v(205, -396) * mm, "end": v(215, -396) * mm});
            skLineSegment(sketch, "E33.3.3.1", {"start": v(205, -406) * mm, "end": v(215, -406) * mm});
            skLineSegment(sketch, "E33.3.3.2", {"start": v(205, -396) * mm, "end": v(205, -406) * mm});
            skLineSegment(sketch, "E33.3.3.3", {"start": v(215, -396) * mm, "end": v(215, -406) * mm});
            skLineSegment(sketch, "E33.3.4.0", {"start": v(205, -382) * mm, "end": v(215, -382) * mm});
            skLineSegment(sketch, "E33.3.4.1", {"start": v(205, -392) * mm, "end": v(215, -392) * mm});
            skLineSegment(sketch, "E33.3.4.2", {"start": v(205, -382) * mm, "end": v(205, -392) * mm});
            skLineSegment(sketch, "E33.3.4.3", {"start": v(215, -382) * mm, "end": v(215, -392) * mm});
            skLineSegment(sketch, "E33.3.5.0", {"start": v(205, -368) * mm, "end": v(215, -368) * mm});
            skLineSegment(sketch, "E33.3.5.1", {"start": v(205, -378) * mm, "end": v(215, -378) * mm});
            skLineSegment(sketch, "E33.3.5.2", {"start": v(205, -368) * mm, "end": v(205, -378) * mm});
            skLineSegment(sketch, "E33.3.5.3", {"start": v(215, -368) * mm, "end": v(215, -378) * mm});
            skLineSegment(sketch, "E33.3.6.0", {"start": v(205, -354) * mm, "end": v(215, -354) * mm});
            skLineSegment(sketch, "E33.3.6.1", {"start": v(205, -364) * mm, "end": v(215, -364) * mm});
            skLineSegment(sketch, "E33.3.6.2", {"start": v(205, -354) * mm, "end": v(205, -364) * mm});
            skLineSegment(sketch, "E33.3.6.3", {"start": v(215, -354) * mm, "end": v(215, -364) * mm});
            skLineSegment(sketch, "E33.3.7.0", {"start": v(205, -340) * mm, "end": v(215, -340) * mm});
            skLineSegment(sketch, "E33.3.7.1", {"start": v(205, -350) * mm, "end": v(215, -350) * mm});
            skLineSegment(sketch, "E33.3.7.2", {"start": v(205, -340) * mm, "end": v(205, -350) * mm});
            skLineSegment(sketch, "E33.3.7.3", {"start": v(215, -340) * mm, "end": v(215, -350) * mm});
            skLineSegment(sketch, "E33.3.8.0", {"start": v(205, -326) * mm, "end": v(215, -326) * mm});
            skLineSegment(sketch, "E33.3.8.1", {"start": v(205, -336) * mm, "end": v(215, -336) * mm});
            skLineSegment(sketch, "E33.3.8.2", {"start": v(205, -326) * mm, "end": v(205, -336) * mm});
            skLineSegment(sketch, "E33.3.8.3", {"start": v(215, -326) * mm, "end": v(215, -336) * mm});
            skLineSegment(sketch, "E33.3.9.0", {"start": v(205, -312) * mm, "end": v(215, -312) * mm});
            skLineSegment(sketch, "E33.3.9.1", {"start": v(205, -322) * mm, "end": v(215, -322) * mm});
            skLineSegment(sketch, "E33.3.9.2", {"start": v(205, -312) * mm, "end": v(205, -322) * mm});
            skLineSegment(sketch, "E33.3.9.3", {"start": v(215, -312) * mm, "end": v(215, -322) * mm});
            skLineSegment(sketch, "E33.3.10.0", {"start": v(205, -298) * mm, "end": v(215, -298) * mm});
            skLineSegment(sketch, "E33.3.10.1", {"start": v(205, -308) * mm, "end": v(215, -308) * mm});
            skLineSegment(sketch, "E33.3.10.2", {"start": v(205, -298) * mm, "end": v(205, -308) * mm});
            skLineSegment(sketch, "E33.3.10.3", {"start": v(215, -298) * mm, "end": v(215, -308) * mm});
            skLineSegment(sketch, "E33.3.11.0", {"start": v(205, -284) * mm, "end": v(215, -284) * mm});
            skLineSegment(sketch, "E33.3.11.1", {"start": v(205, -294) * mm, "end": v(215, -294) * mm});
            skLineSegment(sketch, "E33.3.11.2", {"start": v(205, -284) * mm, "end": v(205, -294) * mm});
            skLineSegment(sketch, "E33.3.11.3", {"start": v(215, -284) * mm, "end": v(215, -294) * mm});
            skLineSegment(sketch, "E33.3.12.0", {"start": v(205, -270) * mm, "end": v(215, -270) * mm});
            skLineSegment(sketch, "E33.3.12.1", {"start": v(205, -280) * mm, "end": v(215, -280) * mm});
            skLineSegment(sketch, "E33.3.12.2", {"start": v(205, -270) * mm, "end": v(205, -280) * mm});
            skLineSegment(sketch, "E33.3.12.3", {"start": v(215, -270) * mm, "end": v(215, -280) * mm});
            skLineSegment(sketch, "E33.3.13.0", {"start": v(205, -256) * mm, "end": v(215, -256) * mm});
            skLineSegment(sketch, "E33.3.13.1", {"start": v(205, -266) * mm, "end": v(215, -266) * mm});
            skLineSegment(sketch, "E33.3.13.2", {"start": v(205, -256) * mm, "end": v(205, -266) * mm});
            skLineSegment(sketch, "E33.3.13.3", {"start": v(215, -256) * mm, "end": v(215, -266) * mm});
            skLineSegment(sketch, "E33.3.14.0", {"start": v(205, -242) * mm, "end": v(215, -242) * mm});
            skLineSegment(sketch, "E33.3.14.1", {"start": v(205, -252) * mm, "end": v(215, -252) * mm});
            skLineSegment(sketch, "E33.3.14.2", {"start": v(205, -242) * mm, "end": v(205, -252) * mm});
            skLineSegment(sketch, "E33.3.14.3", {"start": v(215, -242) * mm, "end": v(215, -252) * mm});
            skLineSegment(sketch, "E33.3.15.0", {"start": v(205, -228) * mm, "end": v(215, -228) * mm});
            skLineSegment(sketch, "E33.3.15.1", {"start": v(205, -238) * mm, "end": v(215, -238) * mm});
            skLineSegment(sketch, "E33.3.15.2", {"start": v(205, -228) * mm, "end": v(205, -238) * mm});
            skLineSegment(sketch, "E33.3.15.3", {"start": v(215, -228) * mm, "end": v(215, -238) * mm});
            skLineSegment(sketch, "E33.3.16.0", {"start": v(205, -214) * mm, "end": v(215, -214) * mm});
            skLineSegment(sketch, "E33.3.16.1", {"start": v(205, -224) * mm, "end": v(215, -224) * mm});
            skLineSegment(sketch, "E33.3.16.2", {"start": v(205, -214) * mm, "end": v(205, -224) * mm});
            skLineSegment(sketch, "E33.3.16.3", {"start": v(215, -214) * mm, "end": v(215, -224) * mm});
            skLineSegment(sketch, "E33.3.17.0", {"start": v(205, -200) * mm, "end": v(215, -200) * mm});
            skLineSegment(sketch, "E33.3.17.1", {"start": v(205, -210) * mm, "end": v(215, -210) * mm});
            skLineSegment(sketch, "E33.3.17.2", {"start": v(205, -200) * mm, "end": v(205, -210) * mm});
            skLineSegment(sketch, "E33.3.17.3", {"start": v(215, -200) * mm, "end": v(215, -210) * mm});
            skLineSegment(sketch, "E33.3.18.0", {"start": v(205, -186) * mm, "end": v(215, -186) * mm});
            skLineSegment(sketch, "E33.3.18.1", {"start": v(205, -196) * mm, "end": v(215, -196) * mm});
            skLineSegment(sketch, "E33.3.18.2", {"start": v(205, -186) * mm, "end": v(205, -196) * mm});
            skLineSegment(sketch, "E33.3.18.3", {"start": v(215, -186) * mm, "end": v(215, -196) * mm});
            skLineSegment(sketch, "E33.3.19.0", {"start": v(205, -172) * mm, "end": v(215, -172) * mm});
            skLineSegment(sketch, "E33.3.19.1", {"start": v(205, -182) * mm, "end": v(215, -182) * mm});
            skLineSegment(sketch, "E33.3.19.2", {"start": v(205, -172) * mm, "end": v(205, -182) * mm});
            skLineSegment(sketch, "E33.3.19.3", {"start": v(215, -172) * mm, "end": v(215, -182) * mm});
            skLineSegment(sketch, "E33.3.20.0", {"start": v(205, -158) * mm, "end": v(215, -158) * mm});
            skLineSegment(sketch, "E33.3.20.1", {"start": v(205, -168) * mm, "end": v(215, -168) * mm});
            skLineSegment(sketch, "E33.3.20.2", {"start": v(205, -158) * mm, "end": v(205, -168) * mm});
            skLineSegment(sketch, "E33.3.20.3", {"start": v(215, -158) * mm, "end": v(215, -168) * mm});
            skLineSegment(sketch, "E33.3.21.0", {"start": v(205, -144) * mm, "end": v(215, -144) * mm});
            skLineSegment(sketch, "E33.3.21.1", {"start": v(205, -154) * mm, "end": v(215, -154) * mm});
            skLineSegment(sketch, "E33.3.21.2", {"start": v(205, -144) * mm, "end": v(205, -154) * mm});
            skLineSegment(sketch, "E33.3.21.3", {"start": v(215, -144) * mm, "end": v(215, -154) * mm});
            skLineSegment(sketch, "E33.3.22.0", {"start": v(205, -130) * mm, "end": v(215, -130) * mm});
            skLineSegment(sketch, "E33.3.22.1", {"start": v(205, -140) * mm, "end": v(215, -140) * mm});
            skLineSegment(sketch, "E33.3.22.2", {"start": v(205, -130) * mm, "end": v(205, -140) * mm});
            skLineSegment(sketch, "E33.3.22.3", {"start": v(215, -130) * mm, "end": v(215, -140) * mm});
            skLineSegment(sketch, "E33.3.23.0", {"start": v(205, -116) * mm, "end": v(215, -116) * mm});
            skLineSegment(sketch, "E33.3.23.1", {"start": v(205, -126) * mm, "end": v(215, -126) * mm});
            skLineSegment(sketch, "E33.3.23.2", {"start": v(205, -116) * mm, "end": v(205, -126) * mm});
            skLineSegment(sketch, "E33.3.23.3", {"start": v(215, -116) * mm, "end": v(215, -126) * mm});
            skLineSegment(sketch, "E33.3.24.0", {"start": v(205, -102) * mm, "end": v(215, -102) * mm});
            skLineSegment(sketch, "E33.3.24.1", {"start": v(205, -112) * mm, "end": v(215, -112) * mm});
            skLineSegment(sketch, "E33.3.24.2", {"start": v(205, -102) * mm, "end": v(205, -112) * mm});
            skLineSegment(sketch, "E33.3.24.3", {"start": v(215, -102) * mm, "end": v(215, -112) * mm});
            skLineSegment(sketch, "E33.3.25.0", {"start": v(205, -88) * mm, "end": v(215, -88) * mm});
            skLineSegment(sketch, "E33.3.25.1", {"start": v(205, -98) * mm, "end": v(215, -98) * mm});
            skLineSegment(sketch, "E33.3.25.2", {"start": v(205, -88) * mm, "end": v(205, -98) * mm});
            skLineSegment(sketch, "E33.3.25.3", {"start": v(215, -88) * mm, "end": v(215, -98) * mm});
            skLineSegment(sketch, "E33.3.26.0", {"start": v(205, -74) * mm, "end": v(215, -74) * mm});
            skLineSegment(sketch, "E33.3.26.1", {"start": v(205, -84) * mm, "end": v(215, -84) * mm});
            skLineSegment(sketch, "E33.3.26.2", {"start": v(205, -74) * mm, "end": v(205, -84) * mm});
            skLineSegment(sketch, "E33.3.26.3", {"start": v(215, -74) * mm, "end": v(215, -84) * mm});
            skLineSegment(sketch, "E33.3.27.0", {"start": v(205, -60) * mm, "end": v(215, -60) * mm});
            skLineSegment(sketch, "E33.3.27.1", {"start": v(205, -70) * mm, "end": v(215, -70) * mm});
            skLineSegment(sketch, "E33.3.27.2", {"start": v(205, -60) * mm, "end": v(205, -70) * mm});
            skLineSegment(sketch, "E33.3.27.3", {"start": v(215, -60) * mm, "end": v(215, -70) * mm});
            skLineSegment(sketch, "E33.3.28.0", {"start": v(205, -46) * mm, "end": v(215, -46) * mm});
            skLineSegment(sketch, "E33.3.28.1", {"start": v(205, -56) * mm, "end": v(215, -56) * mm});
            skLineSegment(sketch, "E33.3.28.2", {"start": v(205, -46) * mm, "end": v(205, -56) * mm});
            skLineSegment(sketch, "E33.3.28.3", {"start": v(215, -46) * mm, "end": v(215, -56) * mm});
            skLineSegment(sketch, "E33.3.29.0", {"start": v(205, -32) * mm, "end": v(215, -32) * mm});
            skLineSegment(sketch, "E33.3.29.1", {"start": v(205, -42) * mm, "end": v(215, -42) * mm});
            skLineSegment(sketch, "E33.3.29.2", {"start": v(205, -32) * mm, "end": v(205, -42) * mm});
            skLineSegment(sketch, "E33.3.29.3", {"start": v(215, -32) * mm, "end": v(215, -42) * mm});
            skLineSegment(sketch, "E33.3.30.0", {"start": v(205, -18) * mm, "end": v(215, -18) * mm});
            skLineSegment(sketch, "E33.3.30.1", {"start": v(205, -28) * mm, "end": v(215, -28) * mm});
            skLineSegment(sketch, "E33.3.30.2", {"start": v(205, -18) * mm, "end": v(205, -28) * mm});
            skLineSegment(sketch, "E33.3.30.3", {"start": v(215, -18) * mm, "end": v(215, -28) * mm});
            skLineSegment(sketch, "E33.3.31.0", {"start": v(205, -4) * mm, "end": v(215, -4) * mm});
            skLineSegment(sketch, "E33.3.31.1", {"start": v(205, -14) * mm, "end": v(215, -14) * mm});
            skLineSegment(sketch, "E33.3.31.2", {"start": v(205, -4) * mm, "end": v(205, -14) * mm});
            skLineSegment(sketch, "E33.3.31.3", {"start": v(215, -4) * mm, "end": v(215, -14) * mm});
            skLineSegment(sketch, "E33.4.0.0", {"start": v(191, -438) * mm, "end": v(201, -438) * mm});
            skLineSegment(sketch, "E33.4.0.1", {"start": v(191, -448) * mm, "end": v(201, -448) * mm});
            skLineSegment(sketch, "E33.4.0.2", {"start": v(191, -438) * mm, "end": v(191, -448) * mm});
            skLineSegment(sketch, "E33.4.0.3", {"start": v(201, -438) * mm, "end": v(201, -448) * mm});
            skLineSegment(sketch, "E33.4.1.0", {"start": v(191, -424) * mm, "end": v(201, -424) * mm});
            skLineSegment(sketch, "E33.4.1.1", {"start": v(191, -434) * mm, "end": v(201, -434) * mm});
            skLineSegment(sketch, "E33.4.1.2", {"start": v(191, -424) * mm, "end": v(191, -434) * mm});
            skLineSegment(sketch, "E33.4.1.3", {"start": v(201, -424) * mm, "end": v(201, -434) * mm});
            skLineSegment(sketch, "E33.4.2.0", {"start": v(191, -410) * mm, "end": v(201, -410) * mm});
            skLineSegment(sketch, "E33.4.2.1", {"start": v(191, -420) * mm, "end": v(201, -420) * mm});
            skLineSegment(sketch, "E33.4.2.2", {"start": v(191, -410) * mm, "end": v(191, -420) * mm});
            skLineSegment(sketch, "E33.4.2.3", {"start": v(201, -410) * mm, "end": v(201, -420) * mm});
            skLineSegment(sketch, "E33.4.3.0", {"start": v(191, -396) * mm, "end": v(201, -396) * mm});
            skLineSegment(sketch, "E33.4.3.1", {"start": v(191, -406) * mm, "end": v(201, -406) * mm});
            skLineSegment(sketch, "E33.4.3.2", {"start": v(191, -396) * mm, "end": v(191, -406) * mm});
            skLineSegment(sketch, "E33.4.3.3", {"start": v(201, -396) * mm, "end": v(201, -406) * mm});
            skLineSegment(sketch, "E33.4.4.0", {"start": v(191, -382) * mm, "end": v(201, -382) * mm});
            skLineSegment(sketch, "E33.4.4.1", {"start": v(191, -392) * mm, "end": v(201, -392) * mm});
            skLineSegment(sketch, "E33.4.4.2", {"start": v(191, -382) * mm, "end": v(191, -392) * mm});
            skLineSegment(sketch, "E33.4.4.3", {"start": v(201, -382) * mm, "end": v(201, -392) * mm});
            skLineSegment(sketch, "E33.4.5.0", {"start": v(191, -368) * mm, "end": v(201, -368) * mm});
            skLineSegment(sketch, "E33.4.5.1", {"start": v(191, -378) * mm, "end": v(201, -378) * mm});
            skLineSegment(sketch, "E33.4.5.2", {"start": v(191, -368) * mm, "end": v(191, -378) * mm});
            skLineSegment(sketch, "E33.4.5.3", {"start": v(201, -368) * mm, "end": v(201, -378) * mm});
            skLineSegment(sketch, "E33.4.6.0", {"start": v(191, -354) * mm, "end": v(201, -354) * mm});
            skLineSegment(sketch, "E33.4.6.1", {"start": v(191, -364) * mm, "end": v(201, -364) * mm});
            skLineSegment(sketch, "E33.4.6.2", {"start": v(191, -354) * mm, "end": v(191, -364) * mm});
            skLineSegment(sketch, "E33.4.6.3", {"start": v(201, -354) * mm, "end": v(201, -364) * mm});
            skLineSegment(sketch, "E33.4.7.0", {"start": v(191, -340) * mm, "end": v(201, -340) * mm});
            skLineSegment(sketch, "E33.4.7.1", {"start": v(191, -350) * mm, "end": v(201, -350) * mm});
            skLineSegment(sketch, "E33.4.7.2", {"start": v(191, -340) * mm, "end": v(191, -350) * mm});
            skLineSegment(sketch, "E33.4.7.3", {"start": v(201, -340) * mm, "end": v(201, -350) * mm});
            skLineSegment(sketch, "E33.4.8.0", {"start": v(191, -326) * mm, "end": v(201, -326) * mm});
            skLineSegment(sketch, "E33.4.8.1", {"start": v(191, -336) * mm, "end": v(201, -336) * mm});
            skLineSegment(sketch, "E33.4.8.2", {"start": v(191, -326) * mm, "end": v(191, -336) * mm});
            skLineSegment(sketch, "E33.4.8.3", {"start": v(201, -326) * mm, "end": v(201, -336) * mm});
            skLineSegment(sketch, "E33.4.9.0", {"start": v(191, -312) * mm, "end": v(201, -312) * mm});
            skLineSegment(sketch, "E33.4.9.1", {"start": v(191, -322) * mm, "end": v(201, -322) * mm});
            skLineSegment(sketch, "E33.4.9.2", {"start": v(191, -312) * mm, "end": v(191, -322) * mm});
            skLineSegment(sketch, "E33.4.9.3", {"start": v(201, -312) * mm, "end": v(201, -322) * mm});
            skLineSegment(sketch, "E33.4.10.0", {"start": v(191, -298) * mm, "end": v(201, -298) * mm});
            skLineSegment(sketch, "E33.4.10.1", {"start": v(191, -308) * mm, "end": v(201, -308) * mm});
            skLineSegment(sketch, "E33.4.10.2", {"start": v(191, -298) * mm, "end": v(191, -308) * mm});
            skLineSegment(sketch, "E33.4.10.3", {"start": v(201, -298) * mm, "end": v(201, -308) * mm});
            skLineSegment(sketch, "E33.4.11.0", {"start": v(191, -284) * mm, "end": v(201, -284) * mm});
            skLineSegment(sketch, "E33.4.11.1", {"start": v(191, -294) * mm, "end": v(201, -294) * mm});
            skLineSegment(sketch, "E33.4.11.2", {"start": v(191, -284) * mm, "end": v(191, -294) * mm});
            skLineSegment(sketch, "E33.4.11.3", {"start": v(201, -284) * mm, "end": v(201, -294) * mm});
            skLineSegment(sketch, "E33.4.12.0", {"start": v(191, -270) * mm, "end": v(201, -270) * mm});
            skLineSegment(sketch, "E33.4.12.1", {"start": v(191, -280) * mm, "end": v(201, -280) * mm});
            skLineSegment(sketch, "E33.4.12.2", {"start": v(191, -270) * mm, "end": v(191, -280) * mm});
            skLineSegment(sketch, "E33.4.12.3", {"start": v(201, -270) * mm, "end": v(201, -280) * mm});
            skLineSegment(sketch, "E33.4.13.0", {"start": v(191, -256) * mm, "end": v(201, -256) * mm});
            skLineSegment(sketch, "E33.4.13.1", {"start": v(191, -266) * mm, "end": v(201, -266) * mm});
            skLineSegment(sketch, "E33.4.13.2", {"start": v(191, -256) * mm, "end": v(191, -266) * mm});
            skLineSegment(sketch, "E33.4.13.3", {"start": v(201, -256) * mm, "end": v(201, -266) * mm});
            skLineSegment(sketch, "E33.4.14.0", {"start": v(191, -242) * mm, "end": v(201, -242) * mm});
            skLineSegment(sketch, "E33.4.14.1", {"start": v(191, -252) * mm, "end": v(201, -252) * mm});
            skLineSegment(sketch, "E33.4.14.2", {"start": v(191, -242) * mm, "end": v(191, -252) * mm});
            skLineSegment(sketch, "E33.4.14.3", {"start": v(201, -242) * mm, "end": v(201, -252) * mm});
            skLineSegment(sketch, "E33.4.15.0", {"start": v(191, -228) * mm, "end": v(201, -228) * mm});
            skLineSegment(sketch, "E33.4.15.1", {"start": v(191, -238) * mm, "end": v(201, -238) * mm});
            skLineSegment(sketch, "E33.4.15.2", {"start": v(191, -228) * mm, "end": v(191, -238) * mm});
            skLineSegment(sketch, "E33.4.15.3", {"start": v(201, -228) * mm, "end": v(201, -238) * mm});
            skLineSegment(sketch, "E33.4.16.0", {"start": v(191, -214) * mm, "end": v(201, -214) * mm});
            skLineSegment(sketch, "E33.4.16.1", {"start": v(191, -224) * mm, "end": v(201, -224) * mm});
            skLineSegment(sketch, "E33.4.16.2", {"start": v(191, -214) * mm, "end": v(191, -224) * mm});
            skLineSegment(sketch, "E33.4.16.3", {"start": v(201, -214) * mm, "end": v(201, -224) * mm});
            skLineSegment(sketch, "E33.4.17.0", {"start": v(191, -200) * mm, "end": v(201, -200) * mm});
            skLineSegment(sketch, "E33.4.17.1", {"start": v(191, -210) * mm, "end": v(201, -210) * mm});
            skLineSegment(sketch, "E33.4.17.2", {"start": v(191, -200) * mm, "end": v(191, -210) * mm});
            skLineSegment(sketch, "E33.4.17.3", {"start": v(201, -200) * mm, "end": v(201, -210) * mm});
            skLineSegment(sketch, "E33.4.18.0", {"start": v(191, -186) * mm, "end": v(201, -186) * mm});
            skLineSegment(sketch, "E33.4.18.1", {"start": v(191, -196) * mm, "end": v(201, -196) * mm});
            skLineSegment(sketch, "E33.4.18.2", {"start": v(191, -186) * mm, "end": v(191, -196) * mm});
            skLineSegment(sketch, "E33.4.18.3", {"start": v(201, -186) * mm, "end": v(201, -196) * mm});
            skLineSegment(sketch, "E33.4.19.0", {"start": v(191, -172) * mm, "end": v(201, -172) * mm});
            skLineSegment(sketch, "E33.4.19.1", {"start": v(191, -182) * mm, "end": v(201, -182) * mm});
            skLineSegment(sketch, "E33.4.19.2", {"start": v(191, -172) * mm, "end": v(191, -182) * mm});
            skLineSegment(sketch, "E33.4.19.3", {"start": v(201, -172) * mm, "end": v(201, -182) * mm});
            skLineSegment(sketch, "E33.4.20.0", {"start": v(191, -158) * mm, "end": v(201, -158) * mm});
            skLineSegment(sketch, "E33.4.20.1", {"start": v(191, -168) * mm, "end": v(201, -168) * mm});
            skLineSegment(sketch, "E33.4.20.2", {"start": v(191, -158) * mm, "end": v(191, -168) * mm});
            skLineSegment(sketch, "E33.4.20.3", {"start": v(201, -158) * mm, "end": v(201, -168) * mm});
            skLineSegment(sketch, "E33.4.21.0", {"start": v(191, -144) * mm, "end": v(201, -144) * mm});
            skLineSegment(sketch, "E33.4.21.1", {"start": v(191, -154) * mm, "end": v(201, -154) * mm});
            skLineSegment(sketch, "E33.4.21.2", {"start": v(191, -144) * mm, "end": v(191, -154) * mm});
            skLineSegment(sketch, "E33.4.21.3", {"start": v(201, -144) * mm, "end": v(201, -154) * mm});
            skLineSegment(sketch, "E33.4.22.0", {"start": v(191, -130) * mm, "end": v(201, -130) * mm});
            skLineSegment(sketch, "E33.4.22.1", {"start": v(191, -140) * mm, "end": v(201, -140) * mm});
            skLineSegment(sketch, "E33.4.22.2", {"start": v(191, -130) * mm, "end": v(191, -140) * mm});
            skLineSegment(sketch, "E33.4.22.3", {"start": v(201, -130) * mm, "end": v(201, -140) * mm});
            skLineSegment(sketch, "E33.4.23.0", {"start": v(191, -116) * mm, "end": v(201, -116) * mm});
            skLineSegment(sketch, "E33.4.23.1", {"start": v(191, -126) * mm, "end": v(201, -126) * mm});
            skLineSegment(sketch, "E33.4.23.2", {"start": v(191, -116) * mm, "end": v(191, -126) * mm});
            skLineSegment(sketch, "E33.4.23.3", {"start": v(201, -116) * mm, "end": v(201, -126) * mm});
            skLineSegment(sketch, "E33.4.24.0", {"start": v(191, -102) * mm, "end": v(201, -102) * mm});
            skLineSegment(sketch, "E33.4.24.1", {"start": v(191, -112) * mm, "end": v(201, -112) * mm});
            skLineSegment(sketch, "E33.4.24.2", {"start": v(191, -102) * mm, "end": v(191, -112) * mm});
            skLineSegment(sketch, "E33.4.24.3", {"start": v(201, -102) * mm, "end": v(201, -112) * mm});
            skLineSegment(sketch, "E33.4.25.0", {"start": v(191, -88) * mm, "end": v(201, -88) * mm});
            skLineSegment(sketch, "E33.4.25.1", {"start": v(191, -98) * mm, "end": v(201, -98) * mm});
            skLineSegment(sketch, "E33.4.25.2", {"start": v(191, -88) * mm, "end": v(191, -98) * mm});
            skLineSegment(sketch, "E33.4.25.3", {"start": v(201, -88) * mm, "end": v(201, -98) * mm});
            skLineSegment(sketch, "E33.4.26.0", {"start": v(191, -74) * mm, "end": v(201, -74) * mm});
            skLineSegment(sketch, "E33.4.26.1", {"start": v(191, -84) * mm, "end": v(201, -84) * mm});
            skLineSegment(sketch, "E33.4.26.2", {"start": v(191, -74) * mm, "end": v(191, -84) * mm});
            skLineSegment(sketch, "E33.4.26.3", {"start": v(201, -74) * mm, "end": v(201, -84) * mm});
            skLineSegment(sketch, "E33.4.27.0", {"start": v(191, -60) * mm, "end": v(201, -60) * mm});
            skLineSegment(sketch, "E33.4.27.1", {"start": v(191, -70) * mm, "end": v(201, -70) * mm});
            skLineSegment(sketch, "E33.4.27.2", {"start": v(191, -60) * mm, "end": v(191, -70) * mm});
            skLineSegment(sketch, "E33.4.27.3", {"start": v(201, -60) * mm, "end": v(201, -70) * mm});
            skLineSegment(sketch, "E33.4.28.0", {"start": v(191, -46) * mm, "end": v(201, -46) * mm});
            skLineSegment(sketch, "E33.4.28.1", {"start": v(191, -56) * mm, "end": v(201, -56) * mm});
            skLineSegment(sketch, "E33.4.28.2", {"start": v(191, -46) * mm, "end": v(191, -56) * mm});
            skLineSegment(sketch, "E33.4.28.3", {"start": v(201, -46) * mm, "end": v(201, -56) * mm});
            skLineSegment(sketch, "E33.4.29.0", {"start": v(191, -32) * mm, "end": v(201, -32) * mm});
            skLineSegment(sketch, "E33.4.29.1", {"start": v(191, -42) * mm, "end": v(201, -42) * mm});
            skLineSegment(sketch, "E33.4.29.2", {"start": v(191, -32) * mm, "end": v(191, -42) * mm});
            skLineSegment(sketch, "E33.4.29.3", {"start": v(201, -32) * mm, "end": v(201, -42) * mm});
            skLineSegment(sketch, "E33.4.30.0", {"start": v(191, -18) * mm, "end": v(201, -18) * mm});
            skLineSegment(sketch, "E33.4.30.1", {"start": v(191, -28) * mm, "end": v(201, -28) * mm});
            skLineSegment(sketch, "E33.4.30.2", {"start": v(191, -18) * mm, "end": v(191, -28) * mm});
            skLineSegment(sketch, "E33.4.30.3", {"start": v(201, -18) * mm, "end": v(201, -28) * mm});
            skLineSegment(sketch, "E33.4.31.0", {"start": v(191, -4) * mm, "end": v(201, -4) * mm});
            skLineSegment(sketch, "E33.4.31.1", {"start": v(191, -14) * mm, "end": v(201, -14) * mm});
            skLineSegment(sketch, "E33.4.31.2", {"start": v(191, -4) * mm, "end": v(191, -14) * mm});
            skLineSegment(sketch, "E33.4.31.3", {"start": v(201, -4) * mm, "end": v(201, -14) * mm});
            skLineSegment(sketch, "E33.5.0.0", {"start": v(177, -438) * mm, "end": v(187, -438) * mm});
            skLineSegment(sketch, "E33.5.0.1", {"start": v(177, -448) * mm, "end": v(187, -448) * mm});
            skLineSegment(sketch, "E33.5.0.2", {"start": v(177, -438) * mm, "end": v(177, -448) * mm});
            skLineSegment(sketch, "E33.5.0.3", {"start": v(187, -438) * mm, "end": v(187, -448) * mm});
            skLineSegment(sketch, "E33.5.1.0", {"start": v(177, -424) * mm, "end": v(187, -424) * mm});
            skLineSegment(sketch, "E33.5.1.1", {"start": v(177, -434) * mm, "end": v(187, -434) * mm});
            skLineSegment(sketch, "E33.5.1.2", {"start": v(177, -424) * mm, "end": v(177, -434) * mm});
            skLineSegment(sketch, "E33.5.1.3", {"start": v(187, -424) * mm, "end": v(187, -434) * mm});
            skLineSegment(sketch, "E33.5.2.0", {"start": v(177, -410) * mm, "end": v(187, -410) * mm});
            skLineSegment(sketch, "E33.5.2.1", {"start": v(177, -420) * mm, "end": v(187, -420) * mm});
            skLineSegment(sketch, "E33.5.2.2", {"start": v(177, -410) * mm, "end": v(177, -420) * mm});
            skLineSegment(sketch, "E33.5.2.3", {"start": v(187, -410) * mm, "end": v(187, -420) * mm});
            skLineSegment(sketch, "E33.5.3.0", {"start": v(177, -396) * mm, "end": v(187, -396) * mm});
            skLineSegment(sketch, "E33.5.3.1", {"start": v(177, -406) * mm, "end": v(187, -406) * mm});
            skLineSegment(sketch, "E33.5.3.2", {"start": v(177, -396) * mm, "end": v(177, -406) * mm});
            skLineSegment(sketch, "E33.5.3.3", {"start": v(187, -396) * mm, "end": v(187, -406) * mm});
            skLineSegment(sketch, "E33.5.4.0", {"start": v(177, -382) * mm, "end": v(187, -382) * mm});
            skLineSegment(sketch, "E33.5.4.1", {"start": v(177, -392) * mm, "end": v(187, -392) * mm});
            skLineSegment(sketch, "E33.5.4.2", {"start": v(177, -382) * mm, "end": v(177, -392) * mm});
            skLineSegment(sketch, "E33.5.4.3", {"start": v(187, -382) * mm, "end": v(187, -392) * mm});
            skLineSegment(sketch, "E33.5.5.0", {"start": v(177, -368) * mm, "end": v(187, -368) * mm});
            skLineSegment(sketch, "E33.5.5.1", {"start": v(177, -378) * mm, "end": v(187, -378) * mm});
            skLineSegment(sketch, "E33.5.5.2", {"start": v(177, -368) * mm, "end": v(177, -378) * mm});
            skLineSegment(sketch, "E33.5.5.3", {"start": v(187, -368) * mm, "end": v(187, -378) * mm});
            skLineSegment(sketch, "E33.5.6.0", {"start": v(177, -354) * mm, "end": v(187, -354) * mm});
            skLineSegment(sketch, "E33.5.6.1", {"start": v(177, -364) * mm, "end": v(187, -364) * mm});
            skLineSegment(sketch, "E33.5.6.2", {"start": v(177, -354) * mm, "end": v(177, -364) * mm});
            skLineSegment(sketch, "E33.5.6.3", {"start": v(187, -354) * mm, "end": v(187, -364) * mm});
            skLineSegment(sketch, "E33.5.7.0", {"start": v(177, -340) * mm, "end": v(187, -340) * mm});
            skLineSegment(sketch, "E33.5.7.1", {"start": v(177, -350) * mm, "end": v(187, -350) * mm});
            skLineSegment(sketch, "E33.5.7.2", {"start": v(177, -340) * mm, "end": v(177, -350) * mm});
            skLineSegment(sketch, "E33.5.7.3", {"start": v(187, -340) * mm, "end": v(187, -350) * mm});
            skLineSegment(sketch, "E33.5.8.0", {"start": v(177, -326) * mm, "end": v(187, -326) * mm});
            skLineSegment(sketch, "E33.5.8.1", {"start": v(177, -336) * mm, "end": v(187, -336) * mm});
            skLineSegment(sketch, "E33.5.8.2", {"start": v(177, -326) * mm, "end": v(177, -336) * mm});
            skLineSegment(sketch, "E33.5.8.3", {"start": v(187, -326) * mm, "end": v(187, -336) * mm});
            skLineSegment(sketch, "E33.5.9.0", {"start": v(177, -312) * mm, "end": v(187, -312) * mm});
            skLineSegment(sketch, "E33.5.9.1", {"start": v(177, -322) * mm, "end": v(187, -322) * mm});
            skLineSegment(sketch, "E33.5.9.2", {"start": v(177, -312) * mm, "end": v(177, -322) * mm});
            skLineSegment(sketch, "E33.5.9.3", {"start": v(187, -312) * mm, "end": v(187, -322) * mm});
            skLineSegment(sketch, "E33.5.10.0", {"start": v(177, -298) * mm, "end": v(187, -298) * mm});
            skLineSegment(sketch, "E33.5.10.1", {"start": v(177, -308) * mm, "end": v(187, -308) * mm});
            skLineSegment(sketch, "E33.5.10.2", {"start": v(177, -298) * mm, "end": v(177, -308) * mm});
            skLineSegment(sketch, "E33.5.10.3", {"start": v(187, -298) * mm, "end": v(187, -308) * mm});
            skLineSegment(sketch, "E33.5.11.0", {"start": v(177, -284) * mm, "end": v(187, -284) * mm});
            skLineSegment(sketch, "E33.5.11.1", {"start": v(177, -294) * mm, "end": v(187, -294) * mm});
            skLineSegment(sketch, "E33.5.11.2", {"start": v(177, -284) * mm, "end": v(177, -294) * mm});
            skLineSegment(sketch, "E33.5.11.3", {"start": v(187, -284) * mm, "end": v(187, -294) * mm});
            skLineSegment(sketch, "E33.5.12.0", {"start": v(177, -270) * mm, "end": v(187, -270) * mm});
            skLineSegment(sketch, "E33.5.12.1", {"start": v(177, -280) * mm, "end": v(187, -280) * mm});
            skLineSegment(sketch, "E33.5.12.2", {"start": v(177, -270) * mm, "end": v(177, -280) * mm});
            skLineSegment(sketch, "E33.5.12.3", {"start": v(187, -270) * mm, "end": v(187, -280) * mm});
            skLineSegment(sketch, "E33.5.13.0", {"start": v(177, -256) * mm, "end": v(187, -256) * mm});
            skLineSegment(sketch, "E33.5.13.1", {"start": v(177, -266) * mm, "end": v(187, -266) * mm});
            skLineSegment(sketch, "E33.5.13.2", {"start": v(177, -256) * mm, "end": v(177, -266) * mm});
            skLineSegment(sketch, "E33.5.13.3", {"start": v(187, -256) * mm, "end": v(187, -266) * mm});
            skLineSegment(sketch, "E33.5.14.0", {"start": v(177, -242) * mm, "end": v(187, -242) * mm});
            skLineSegment(sketch, "E33.5.14.1", {"start": v(177, -252) * mm, "end": v(187, -252) * mm});
            skLineSegment(sketch, "E33.5.14.2", {"start": v(177, -242) * mm, "end": v(177, -252) * mm});
            skLineSegment(sketch, "E33.5.14.3", {"start": v(187, -242) * mm, "end": v(187, -252) * mm});
            skLineSegment(sketch, "E33.5.15.0", {"start": v(177, -228) * mm, "end": v(187, -228) * mm});
            skLineSegment(sketch, "E33.5.15.1", {"start": v(177, -238) * mm, "end": v(187, -238) * mm});
            skLineSegment(sketch, "E33.5.15.2", {"start": v(177, -228) * mm, "end": v(177, -238) * mm});
            skLineSegment(sketch, "E33.5.15.3", {"start": v(187, -228) * mm, "end": v(187, -238) * mm});
            skLineSegment(sketch, "E33.5.16.0", {"start": v(177, -214) * mm, "end": v(187, -214) * mm});
            skLineSegment(sketch, "E33.5.16.1", {"start": v(177, -224) * mm, "end": v(187, -224) * mm});
            skLineSegment(sketch, "E33.5.16.2", {"start": v(177, -214) * mm, "end": v(177, -224) * mm});
            skLineSegment(sketch, "E33.5.16.3", {"start": v(187, -214) * mm, "end": v(187, -224) * mm});
            skLineSegment(sketch, "E33.5.17.0", {"start": v(177, -200) * mm, "end": v(187, -200) * mm});
            skLineSegment(sketch, "E33.5.17.1", {"start": v(177, -210) * mm, "end": v(187, -210) * mm});
            skLineSegment(sketch, "E33.5.17.2", {"start": v(177, -200) * mm, "end": v(177, -210) * mm});
            skLineSegment(sketch, "E33.5.17.3", {"start": v(187, -200) * mm, "end": v(187, -210) * mm});
            skLineSegment(sketch, "E33.5.18.0", {"start": v(177, -186) * mm, "end": v(187, -186) * mm});
            skLineSegment(sketch, "E33.5.18.1", {"start": v(177, -196) * mm, "end": v(187, -196) * mm});
            skLineSegment(sketch, "E33.5.18.2", {"start": v(177, -186) * mm, "end": v(177, -196) * mm});
            skLineSegment(sketch, "E33.5.18.3", {"start": v(187, -186) * mm, "end": v(187, -196) * mm});
            skLineSegment(sketch, "E33.5.19.0", {"start": v(177, -172) * mm, "end": v(187, -172) * mm});
            skLineSegment(sketch, "E33.5.19.1", {"start": v(177, -182) * mm, "end": v(187, -182) * mm});
            skLineSegment(sketch, "E33.5.19.2", {"start": v(177, -172) * mm, "end": v(177, -182) * mm});
            skLineSegment(sketch, "E33.5.19.3", {"start": v(187, -172) * mm, "end": v(187, -182) * mm});
            skLineSegment(sketch, "E33.5.20.0", {"start": v(177, -158) * mm, "end": v(187, -158) * mm});
            skLineSegment(sketch, "E33.5.20.1", {"start": v(177, -168) * mm, "end": v(187, -168) * mm});
            skLineSegment(sketch, "E33.5.20.2", {"start": v(177, -158) * mm, "end": v(177, -168) * mm});
            skLineSegment(sketch, "E33.5.20.3", {"start": v(187, -158) * mm, "end": v(187, -168) * mm});
            skLineSegment(sketch, "E33.5.21.0", {"start": v(177, -144) * mm, "end": v(187, -144) * mm});
            skLineSegment(sketch, "E33.5.21.1", {"start": v(177, -154) * mm, "end": v(187, -154) * mm});
            skLineSegment(sketch, "E33.5.21.2", {"start": v(177, -144) * mm, "end": v(177, -154) * mm});
            skLineSegment(sketch, "E33.5.21.3", {"start": v(187, -144) * mm, "end": v(187, -154) * mm});
            skLineSegment(sketch, "E33.5.22.0", {"start": v(177, -130) * mm, "end": v(187, -130) * mm});
            skLineSegment(sketch, "E33.5.22.1", {"start": v(177, -140) * mm, "end": v(187, -140) * mm});
            skLineSegment(sketch, "E33.5.22.2", {"start": v(177, -130) * mm, "end": v(177, -140) * mm});
            skLineSegment(sketch, "E33.5.22.3", {"start": v(187, -130) * mm, "end": v(187, -140) * mm});
            skLineSegment(sketch, "E33.5.23.0", {"start": v(177, -116) * mm, "end": v(187, -116) * mm});
            skLineSegment(sketch, "E33.5.23.1", {"start": v(177, -126) * mm, "end": v(187, -126) * mm});
            skLineSegment(sketch, "E33.5.23.2", {"start": v(177, -116) * mm, "end": v(177, -126) * mm});
            skLineSegment(sketch, "E33.5.23.3", {"start": v(187, -116) * mm, "end": v(187, -126) * mm});
            skLineSegment(sketch, "E33.5.24.0", {"start": v(177, -102) * mm, "end": v(187, -102) * mm});
            skLineSegment(sketch, "E33.5.24.1", {"start": v(177, -112) * mm, "end": v(187, -112) * mm});
            skLineSegment(sketch, "E33.5.24.2", {"start": v(177, -102) * mm, "end": v(177, -112) * mm});
            skLineSegment(sketch, "E33.5.24.3", {"start": v(187, -102) * mm, "end": v(187, -112) * mm});
            skLineSegment(sketch, "E33.5.25.0", {"start": v(177, -88) * mm, "end": v(187, -88) * mm});
            skLineSegment(sketch, "E33.5.25.1", {"start": v(177, -98) * mm, "end": v(187, -98) * mm});
            skLineSegment(sketch, "E33.5.25.2", {"start": v(177, -88) * mm, "end": v(177, -98) * mm});
            skLineSegment(sketch, "E33.5.25.3", {"start": v(187, -88) * mm, "end": v(187, -98) * mm});
            skLineSegment(sketch, "E33.5.26.0", {"start": v(177, -74) * mm, "end": v(187, -74) * mm});
            skLineSegment(sketch, "E33.5.26.1", {"start": v(177, -84) * mm, "end": v(187, -84) * mm});
            skLineSegment(sketch, "E33.5.26.2", {"start": v(177, -74) * mm, "end": v(177, -84) * mm});
            skLineSegment(sketch, "E33.5.26.3", {"start": v(187, -74) * mm, "end": v(187, -84) * mm});
            skLineSegment(sketch, "E33.5.27.0", {"start": v(177, -60) * mm, "end": v(187, -60) * mm});
            skLineSegment(sketch, "E33.5.27.1", {"start": v(177, -70) * mm, "end": v(187, -70) * mm});
            skLineSegment(sketch, "E33.5.27.2", {"start": v(177, -60) * mm, "end": v(177, -70) * mm});
            skLineSegment(sketch, "E33.5.27.3", {"start": v(187, -60) * mm, "end": v(187, -70) * mm});
            skLineSegment(sketch, "E33.5.28.0", {"start": v(177, -46) * mm, "end": v(187, -46) * mm});
            skLineSegment(sketch, "E33.5.28.1", {"start": v(177, -56) * mm, "end": v(187, -56) * mm});
            skLineSegment(sketch, "E33.5.28.2", {"start": v(177, -46) * mm, "end": v(177, -56) * mm});
            skLineSegment(sketch, "E33.5.28.3", {"start": v(187, -46) * mm, "end": v(187, -56) * mm});
            skLineSegment(sketch, "E33.5.29.0", {"start": v(177, -32) * mm, "end": v(187, -32) * mm});
            skLineSegment(sketch, "E33.5.29.1", {"start": v(177, -42) * mm, "end": v(187, -42) * mm});
            skLineSegment(sketch, "E33.5.29.2", {"start": v(177, -32) * mm, "end": v(177, -42) * mm});
            skLineSegment(sketch, "E33.5.29.3", {"start": v(187, -32) * mm, "end": v(187, -42) * mm});
            skLineSegment(sketch, "E33.5.30.0", {"start": v(177, -18) * mm, "end": v(187, -18) * mm});
            skLineSegment(sketch, "E33.5.30.1", {"start": v(177, -28) * mm, "end": v(187, -28) * mm});
            skLineSegment(sketch, "E33.5.30.2", {"start": v(177, -18) * mm, "end": v(177, -28) * mm});
            skLineSegment(sketch, "E33.5.30.3", {"start": v(187, -18) * mm, "end": v(187, -28) * mm});
            skLineSegment(sketch, "E33.5.31.0", {"start": v(177, -4) * mm, "end": v(187, -4) * mm});
            skLineSegment(sketch, "E33.5.31.1", {"start": v(177, -14) * mm, "end": v(187, -14) * mm});
            skLineSegment(sketch, "E33.5.31.2", {"start": v(177, -4) * mm, "end": v(177, -14) * mm});
            skLineSegment(sketch, "E33.5.31.3", {"start": v(187, -4) * mm, "end": v(187, -14) * mm});
            skLineSegment(sketch, "E33.6.0.0", {"start": v(163, -438) * mm, "end": v(173, -438) * mm});
            skLineSegment(sketch, "E33.6.0.1", {"start": v(163, -448) * mm, "end": v(173, -448) * mm});
            skLineSegment(sketch, "E33.6.0.2", {"start": v(163, -438) * mm, "end": v(163, -448) * mm});
            skLineSegment(sketch, "E33.6.0.3", {"start": v(173, -438) * mm, "end": v(173, -448) * mm});
            skLineSegment(sketch, "E33.6.1.0", {"start": v(163, -424) * mm, "end": v(173, -424) * mm});
            skLineSegment(sketch, "E33.6.1.1", {"start": v(163, -434) * mm, "end": v(173, -434) * mm});
            skLineSegment(sketch, "E33.6.1.2", {"start": v(163, -424) * mm, "end": v(163, -434) * mm});
            skLineSegment(sketch, "E33.6.1.3", {"start": v(173, -424) * mm, "end": v(173, -434) * mm});
            skLineSegment(sketch, "E33.6.2.0", {"start": v(163, -410) * mm, "end": v(173, -410) * mm});
            skLineSegment(sketch, "E33.6.2.1", {"start": v(163, -420) * mm, "end": v(173, -420) * mm});
            skLineSegment(sketch, "E33.6.2.2", {"start": v(163, -410) * mm, "end": v(163, -420) * mm});
            skLineSegment(sketch, "E33.6.2.3", {"start": v(173, -410) * mm, "end": v(173, -420) * mm});
            skLineSegment(sketch, "E33.6.3.0", {"start": v(163, -396) * mm, "end": v(173, -396) * mm});
            skLineSegment(sketch, "E33.6.3.1", {"start": v(163, -406) * mm, "end": v(173, -406) * mm});
            skLineSegment(sketch, "E33.6.3.2", {"start": v(163, -396) * mm, "end": v(163, -406) * mm});
            skLineSegment(sketch, "E33.6.3.3", {"start": v(173, -396) * mm, "end": v(173, -406) * mm});
            skLineSegment(sketch, "E33.6.4.0", {"start": v(163, -382) * mm, "end": v(173, -382) * mm});
            skLineSegment(sketch, "E33.6.4.1", {"start": v(163, -392) * mm, "end": v(173, -392) * mm});
            skLineSegment(sketch, "E33.6.4.2", {"start": v(163, -382) * mm, "end": v(163, -392) * mm});
            skLineSegment(sketch, "E33.6.4.3", {"start": v(173, -382) * mm, "end": v(173, -392) * mm});
            skLineSegment(sketch, "E33.6.5.0", {"start": v(163, -368) * mm, "end": v(173, -368) * mm});
            skLineSegment(sketch, "E33.6.5.1", {"start": v(163, -378) * mm, "end": v(173, -378) * mm});
            skLineSegment(sketch, "E33.6.5.2", {"start": v(163, -368) * mm, "end": v(163, -378) * mm});
            skLineSegment(sketch, "E33.6.5.3", {"start": v(173, -368) * mm, "end": v(173, -378) * mm});
            skLineSegment(sketch, "E33.6.6.0", {"start": v(163, -354) * mm, "end": v(173, -354) * mm});
            skLineSegment(sketch, "E33.6.6.1", {"start": v(163, -364) * mm, "end": v(173, -364) * mm});
            skLineSegment(sketch, "E33.6.6.2", {"start": v(163, -354) * mm, "end": v(163, -364) * mm});
            skLineSegment(sketch, "E33.6.6.3", {"start": v(173, -354) * mm, "end": v(173, -364) * mm});
            skLineSegment(sketch, "E33.6.7.0", {"start": v(163, -340) * mm, "end": v(173, -340) * mm});
            skLineSegment(sketch, "E33.6.7.1", {"start": v(163, -350) * mm, "end": v(173, -350) * mm});
            skLineSegment(sketch, "E33.6.7.2", {"start": v(163, -340) * mm, "end": v(163, -350) * mm});
            skLineSegment(sketch, "E33.6.7.3", {"start": v(173, -340) * mm, "end": v(173, -350) * mm});
            skLineSegment(sketch, "E33.6.8.0", {"start": v(163, -326) * mm, "end": v(173, -326) * mm});
            skLineSegment(sketch, "E33.6.8.1", {"start": v(163, -336) * mm, "end": v(173, -336) * mm});
            skLineSegment(sketch, "E33.6.8.2", {"start": v(163, -326) * mm, "end": v(163, -336) * mm});
            skLineSegment(sketch, "E33.6.8.3", {"start": v(173, -326) * mm, "end": v(173, -336) * mm});
            skLineSegment(sketch, "E33.6.9.0", {"start": v(163, -312) * mm, "end": v(173, -312) * mm});
            skLineSegment(sketch, "E33.6.9.1", {"start": v(163, -322) * mm, "end": v(173, -322) * mm});
            skLineSegment(sketch, "E33.6.9.2", {"start": v(163, -312) * mm, "end": v(163, -322) * mm});
            skLineSegment(sketch, "E33.6.9.3", {"start": v(173, -312) * mm, "end": v(173, -322) * mm});
            skLineSegment(sketch, "E33.6.10.0", {"start": v(163, -298) * mm, "end": v(173, -298) * mm});
            skLineSegment(sketch, "E33.6.10.1", {"start": v(163, -308) * mm, "end": v(173, -308) * mm});
            skLineSegment(sketch, "E33.6.10.2", {"start": v(163, -298) * mm, "end": v(163, -308) * mm});
            skLineSegment(sketch, "E33.6.10.3", {"start": v(173, -298) * mm, "end": v(173, -308) * mm});
            skLineSegment(sketch, "E33.6.11.0", {"start": v(163, -284) * mm, "end": v(173, -284) * mm});
            skLineSegment(sketch, "E33.6.11.1", {"start": v(163, -294) * mm, "end": v(173, -294) * mm});
            skLineSegment(sketch, "E33.6.11.2", {"start": v(163, -284) * mm, "end": v(163, -294) * mm});
            skLineSegment(sketch, "E33.6.11.3", {"start": v(173, -284) * mm, "end": v(173, -294) * mm});
            skLineSegment(sketch, "E33.6.12.0", {"start": v(163, -270) * mm, "end": v(173, -270) * mm});
            skLineSegment(sketch, "E33.6.12.1", {"start": v(163, -280) * mm, "end": v(173, -280) * mm});
            skLineSegment(sketch, "E33.6.12.2", {"start": v(163, -270) * mm, "end": v(163, -280) * mm});
            skLineSegment(sketch, "E33.6.12.3", {"start": v(173, -270) * mm, "end": v(173, -280) * mm});
            skLineSegment(sketch, "E33.6.13.0", {"start": v(163, -256) * mm, "end": v(173, -256) * mm});
            skLineSegment(sketch, "E33.6.13.1", {"start": v(163, -266) * mm, "end": v(173, -266) * mm});
            skLineSegment(sketch, "E33.6.13.2", {"start": v(163, -256) * mm, "end": v(163, -266) * mm});
            skLineSegment(sketch, "E33.6.13.3", {"start": v(173, -256) * mm, "end": v(173, -266) * mm});
            skLineSegment(sketch, "E33.6.14.0", {"start": v(163, -242) * mm, "end": v(173, -242) * mm});
            skLineSegment(sketch, "E33.6.14.1", {"start": v(163, -252) * mm, "end": v(173, -252) * mm});
            skLineSegment(sketch, "E33.6.14.2", {"start": v(163, -242) * mm, "end": v(163, -252) * mm});
            skLineSegment(sketch, "E33.6.14.3", {"start": v(173, -242) * mm, "end": v(173, -252) * mm});
            skLineSegment(sketch, "E33.6.15.0", {"start": v(163, -228) * mm, "end": v(173, -228) * mm});
            skLineSegment(sketch, "E33.6.15.1", {"start": v(163, -238) * mm, "end": v(173, -238) * mm});
            skLineSegment(sketch, "E33.6.15.2", {"start": v(163, -228) * mm, "end": v(163, -238) * mm});
            skLineSegment(sketch, "E33.6.15.3", {"start": v(173, -228) * mm, "end": v(173, -238) * mm});
            skLineSegment(sketch, "E33.6.16.0", {"start": v(163, -214) * mm, "end": v(173, -214) * mm});
            skLineSegment(sketch, "E33.6.16.1", {"start": v(163, -224) * mm, "end": v(173, -224) * mm});
            skLineSegment(sketch, "E33.6.16.2", {"start": v(163, -214) * mm, "end": v(163, -224) * mm});
            skLineSegment(sketch, "E33.6.16.3", {"start": v(173, -214) * mm, "end": v(173, -224) * mm});
            skLineSegment(sketch, "E33.6.17.0", {"start": v(163, -200) * mm, "end": v(173, -200) * mm});
            skLineSegment(sketch, "E33.6.17.1", {"start": v(163, -210) * mm, "end": v(173, -210) * mm});
            skLineSegment(sketch, "E33.6.17.2", {"start": v(163, -200) * mm, "end": v(163, -210) * mm});
            skLineSegment(sketch, "E33.6.17.3", {"start": v(173, -200) * mm, "end": v(173, -210) * mm});
            skLineSegment(sketch, "E33.6.18.0", {"start": v(163, -186) * mm, "end": v(173, -186) * mm});
            skLineSegment(sketch, "E33.6.18.1", {"start": v(163, -196) * mm, "end": v(173, -196) * mm});
            skLineSegment(sketch, "E33.6.18.2", {"start": v(163, -186) * mm, "end": v(163, -196) * mm});
            skLineSegment(sketch, "E33.6.18.3", {"start": v(173, -186) * mm, "end": v(173, -196) * mm});
            skLineSegment(sketch, "E33.6.19.0", {"start": v(163, -172) * mm, "end": v(173, -172) * mm});
            skLineSegment(sketch, "E33.6.19.1", {"start": v(163, -182) * mm, "end": v(173, -182) * mm});
            skLineSegment(sketch, "E33.6.19.2", {"start": v(163, -172) * mm, "end": v(163, -182) * mm});
            skLineSegment(sketch, "E33.6.19.3", {"start": v(173, -172) * mm, "end": v(173, -182) * mm});
            skLineSegment(sketch, "E33.6.20.0", {"start": v(163, -158) * mm, "end": v(173, -158) * mm});
            skLineSegment(sketch, "E33.6.20.1", {"start": v(163, -168) * mm, "end": v(173, -168) * mm});
            skLineSegment(sketch, "E33.6.20.2", {"start": v(163, -158) * mm, "end": v(163, -168) * mm});
            skLineSegment(sketch, "E33.6.20.3", {"start": v(173, -158) * mm, "end": v(173, -168) * mm});
            skLineSegment(sketch, "E33.6.21.0", {"start": v(163, -144) * mm, "end": v(173, -144) * mm});
            skLineSegment(sketch, "E33.6.21.1", {"start": v(163, -154) * mm, "end": v(173, -154) * mm});
            skLineSegment(sketch, "E33.6.21.2", {"start": v(163, -144) * mm, "end": v(163, -154) * mm});
            skLineSegment(sketch, "E33.6.21.3", {"start": v(173, -144) * mm, "end": v(173, -154) * mm});
            skLineSegment(sketch, "E33.6.22.0", {"start": v(163, -130) * mm, "end": v(173, -130) * mm});
            skLineSegment(sketch, "E33.6.22.1", {"start": v(163, -140) * mm, "end": v(173, -140) * mm});
            skLineSegment(sketch, "E33.6.22.2", {"start": v(163, -130) * mm, "end": v(163, -140) * mm});
            skLineSegment(sketch, "E33.6.22.3", {"start": v(173, -130) * mm, "end": v(173, -140) * mm});
            skLineSegment(sketch, "E33.6.23.0", {"start": v(163, -116) * mm, "end": v(173, -116) * mm});
            skLineSegment(sketch, "E33.6.23.1", {"start": v(163, -126) * mm, "end": v(173, -126) * mm});
            skLineSegment(sketch, "E33.6.23.2", {"start": v(163, -116) * mm, "end": v(163, -126) * mm});
            skLineSegment(sketch, "E33.6.23.3", {"start": v(173, -116) * mm, "end": v(173, -126) * mm});
            skLineSegment(sketch, "E33.6.24.0", {"start": v(163, -102) * mm, "end": v(173, -102) * mm});
            skLineSegment(sketch, "E33.6.24.1", {"start": v(163, -112) * mm, "end": v(173, -112) * mm});
            skLineSegment(sketch, "E33.6.24.2", {"start": v(163, -102) * mm, "end": v(163, -112) * mm});
            skLineSegment(sketch, "E33.6.24.3", {"start": v(173, -102) * mm, "end": v(173, -112) * mm});
            skLineSegment(sketch, "E33.6.25.0", {"start": v(163, -88) * mm, "end": v(173, -88) * mm});
            skLineSegment(sketch, "E33.6.25.1", {"start": v(163, -98) * mm, "end": v(173, -98) * mm});
            skLineSegment(sketch, "E33.6.25.2", {"start": v(163, -88) * mm, "end": v(163, -98) * mm});
            skLineSegment(sketch, "E33.6.25.3", {"start": v(173, -88) * mm, "end": v(173, -98) * mm});
            skLineSegment(sketch, "E33.6.26.0", {"start": v(163, -74) * mm, "end": v(173, -74) * mm});
            skLineSegment(sketch, "E33.6.26.1", {"start": v(163, -84) * mm, "end": v(173, -84) * mm});
            skLineSegment(sketch, "E33.6.26.2", {"start": v(163, -74) * mm, "end": v(163, -84) * mm});
            skLineSegment(sketch, "E33.6.26.3", {"start": v(173, -74) * mm, "end": v(173, -84) * mm});
            skLineSegment(sketch, "E33.6.27.0", {"start": v(163, -60) * mm, "end": v(173, -60) * mm});
            skLineSegment(sketch, "E33.6.27.1", {"start": v(163, -70) * mm, "end": v(173, -70) * mm});
            skLineSegment(sketch, "E33.6.27.2", {"start": v(163, -60) * mm, "end": v(163, -70) * mm});
            skLineSegment(sketch, "E33.6.27.3", {"start": v(173, -60) * mm, "end": v(173, -70) * mm});
            skLineSegment(sketch, "E33.6.28.0", {"start": v(163, -46) * mm, "end": v(173, -46) * mm});
            skLineSegment(sketch, "E33.6.28.1", {"start": v(163, -56) * mm, "end": v(173, -56) * mm});
            skLineSegment(sketch, "E33.6.28.2", {"start": v(163, -46) * mm, "end": v(163, -56) * mm});
            skLineSegment(sketch, "E33.6.28.3", {"start": v(173, -46) * mm, "end": v(173, -56) * mm});
            skLineSegment(sketch, "E33.6.29.0", {"start": v(163, -32) * mm, "end": v(173, -32) * mm});
            skLineSegment(sketch, "E33.6.29.1", {"start": v(163, -42) * mm, "end": v(173, -42) * mm});
            skLineSegment(sketch, "E33.6.29.2", {"start": v(163, -32) * mm, "end": v(163, -42) * mm});
            skLineSegment(sketch, "E33.6.29.3", {"start": v(173, -32) * mm, "end": v(173, -42) * mm});
            skLineSegment(sketch, "E33.6.30.0", {"start": v(163, -18) * mm, "end": v(173, -18) * mm});
            skLineSegment(sketch, "E33.6.30.1", {"start": v(163, -28) * mm, "end": v(173, -28) * mm});
            skLineSegment(sketch, "E33.6.30.2", {"start": v(163, -18) * mm, "end": v(163, -28) * mm});
            skLineSegment(sketch, "E33.6.30.3", {"start": v(173, -18) * mm, "end": v(173, -28) * mm});
            skLineSegment(sketch, "E33.6.31.0", {"start": v(163, -4) * mm, "end": v(173, -4) * mm});
            skLineSegment(sketch, "E33.6.31.1", {"start": v(163, -14) * mm, "end": v(173, -14) * mm});
            skLineSegment(sketch, "E33.6.31.2", {"start": v(163, -4) * mm, "end": v(163, -14) * mm});
            skLineSegment(sketch, "E33.6.31.3", {"start": v(173, -4) * mm, "end": v(173, -14) * mm});
            skLineSegment(sketch, "E33.7.0.0", {"start": v(149, -438) * mm, "end": v(159, -438) * mm});
            skLineSegment(sketch, "E33.7.0.1", {"start": v(149, -448) * mm, "end": v(159, -448) * mm});
            skLineSegment(sketch, "E33.7.0.2", {"start": v(149, -438) * mm, "end": v(149, -448) * mm});
            skLineSegment(sketch, "E33.7.0.3", {"start": v(159, -438) * mm, "end": v(159, -448) * mm});
            skLineSegment(sketch, "E33.7.1.0", {"start": v(149, -424) * mm, "end": v(159, -424) * mm});
            skLineSegment(sketch, "E33.7.1.1", {"start": v(149, -434) * mm, "end": v(159, -434) * mm});
            skLineSegment(sketch, "E33.7.1.2", {"start": v(149, -424) * mm, "end": v(149, -434) * mm});
            skLineSegment(sketch, "E33.7.1.3", {"start": v(159, -424) * mm, "end": v(159, -434) * mm});
            skLineSegment(sketch, "E33.7.2.0", {"start": v(149, -410) * mm, "end": v(159, -410) * mm});
            skLineSegment(sketch, "E33.7.2.1", {"start": v(149, -420) * mm, "end": v(159, -420) * mm});
            skLineSegment(sketch, "E33.7.2.2", {"start": v(149, -410) * mm, "end": v(149, -420) * mm});
            skLineSegment(sketch, "E33.7.2.3", {"start": v(159, -410) * mm, "end": v(159, -420) * mm});
            skLineSegment(sketch, "E33.7.3.0", {"start": v(149, -396) * mm, "end": v(159, -396) * mm});
            skLineSegment(sketch, "E33.7.3.1", {"start": v(149, -406) * mm, "end": v(159, -406) * mm});
            skLineSegment(sketch, "E33.7.3.2", {"start": v(149, -396) * mm, "end": v(149, -406) * mm});
            skLineSegment(sketch, "E33.7.3.3", {"start": v(159, -396) * mm, "end": v(159, -406) * mm});
            skLineSegment(sketch, "E33.7.4.0", {"start": v(149, -382) * mm, "end": v(159, -382) * mm});
            skLineSegment(sketch, "E33.7.4.1", {"start": v(149, -392) * mm, "end": v(159, -392) * mm});
            skLineSegment(sketch, "E33.7.4.2", {"start": v(149, -382) * mm, "end": v(149, -392) * mm});
            skLineSegment(sketch, "E33.7.4.3", {"start": v(159, -382) * mm, "end": v(159, -392) * mm});
            skLineSegment(sketch, "E33.7.5.0", {"start": v(149, -368) * mm, "end": v(159, -368) * mm});
            skLineSegment(sketch, "E33.7.5.1", {"start": v(149, -378) * mm, "end": v(159, -378) * mm});
            skLineSegment(sketch, "E33.7.5.2", {"start": v(149, -368) * mm, "end": v(149, -378) * mm});
            skLineSegment(sketch, "E33.7.5.3", {"start": v(159, -368) * mm, "end": v(159, -378) * mm});
            skLineSegment(sketch, "E33.7.6.0", {"start": v(149, -354) * mm, "end": v(159, -354) * mm});
            skLineSegment(sketch, "E33.7.6.1", {"start": v(149, -364) * mm, "end": v(159, -364) * mm});
            skLineSegment(sketch, "E33.7.6.2", {"start": v(149, -354) * mm, "end": v(149, -364) * mm});
            skLineSegment(sketch, "E33.7.6.3", {"start": v(159, -354) * mm, "end": v(159, -364) * mm});
            skLineSegment(sketch, "E33.7.7.0", {"start": v(149, -340) * mm, "end": v(159, -340) * mm});
            skLineSegment(sketch, "E33.7.7.1", {"start": v(149, -350) * mm, "end": v(159, -350) * mm});
            skLineSegment(sketch, "E33.7.7.2", {"start": v(149, -340) * mm, "end": v(149, -350) * mm});
            skLineSegment(sketch, "E33.7.7.3", {"start": v(159, -340) * mm, "end": v(159, -350) * mm});
            skLineSegment(sketch, "E33.7.8.0", {"start": v(149, -326) * mm, "end": v(159, -326) * mm});
            skLineSegment(sketch, "E33.7.8.1", {"start": v(149, -336) * mm, "end": v(159, -336) * mm});
            skLineSegment(sketch, "E33.7.8.2", {"start": v(149, -326) * mm, "end": v(149, -336) * mm});
            skLineSegment(sketch, "E33.7.8.3", {"start": v(159, -326) * mm, "end": v(159, -336) * mm});
            skLineSegment(sketch, "E33.7.9.0", {"start": v(149, -312) * mm, "end": v(159, -312) * mm});
            skLineSegment(sketch, "E33.7.9.1", {"start": v(149, -322) * mm, "end": v(159, -322) * mm});
            skLineSegment(sketch, "E33.7.9.2", {"start": v(149, -312) * mm, "end": v(149, -322) * mm});
            skLineSegment(sketch, "E33.7.9.3", {"start": v(159, -312) * mm, "end": v(159, -322) * mm});
            skLineSegment(sketch, "E33.7.10.0", {"start": v(149, -298) * mm, "end": v(159, -298) * mm});
            skLineSegment(sketch, "E33.7.10.1", {"start": v(149, -308) * mm, "end": v(159, -308) * mm});
            skLineSegment(sketch, "E33.7.10.2", {"start": v(149, -298) * mm, "end": v(149, -308) * mm});
            skLineSegment(sketch, "E33.7.10.3", {"start": v(159, -298) * mm, "end": v(159, -308) * mm});
            skLineSegment(sketch, "E33.7.11.0", {"start": v(149, -284) * mm, "end": v(159, -284) * mm});
            skLineSegment(sketch, "E33.7.11.1", {"start": v(149, -294) * mm, "end": v(159, -294) * mm});
            skLineSegment(sketch, "E33.7.11.2", {"start": v(149, -284) * mm, "end": v(149, -294) * mm});
            skLineSegment(sketch, "E33.7.11.3", {"start": v(159, -284) * mm, "end": v(159, -294) * mm});
            skLineSegment(sketch, "E33.7.12.0", {"start": v(149, -270) * mm, "end": v(159, -270) * mm});
            skLineSegment(sketch, "E33.7.12.1", {"start": v(149, -280) * mm, "end": v(159, -280) * mm});
            skLineSegment(sketch, "E33.7.12.2", {"start": v(149, -270) * mm, "end": v(149, -280) * mm});
            skLineSegment(sketch, "E33.7.12.3", {"start": v(159, -270) * mm, "end": v(159, -280) * mm});
            skLineSegment(sketch, "E33.7.13.0", {"start": v(149, -256) * mm, "end": v(159, -256) * mm});
            skLineSegment(sketch, "E33.7.13.1", {"start": v(149, -266) * mm, "end": v(159, -266) * mm});
            skLineSegment(sketch, "E33.7.13.2", {"start": v(149, -256) * mm, "end": v(149, -266) * mm});
            skLineSegment(sketch, "E33.7.13.3", {"start": v(159, -256) * mm, "end": v(159, -266) * mm});
            skLineSegment(sketch, "E33.7.14.0", {"start": v(149, -242) * mm, "end": v(159, -242) * mm});
            skLineSegment(sketch, "E33.7.14.1", {"start": v(149, -252) * mm, "end": v(159, -252) * mm});
            skLineSegment(sketch, "E33.7.14.2", {"start": v(149, -242) * mm, "end": v(149, -252) * mm});
            skLineSegment(sketch, "E33.7.14.3", {"start": v(159, -242) * mm, "end": v(159, -252) * mm});
            skLineSegment(sketch, "E33.7.15.0", {"start": v(149, -228) * mm, "end": v(159, -228) * mm});
            skLineSegment(sketch, "E33.7.15.1", {"start": v(149, -238) * mm, "end": v(159, -238) * mm});
            skLineSegment(sketch, "E33.7.15.2", {"start": v(149, -228) * mm, "end": v(149, -238) * mm});
            skLineSegment(sketch, "E33.7.15.3", {"start": v(159, -228) * mm, "end": v(159, -238) * mm});
            skLineSegment(sketch, "E33.7.16.0", {"start": v(149, -214) * mm, "end": v(159, -214) * mm});
            skLineSegment(sketch, "E33.7.16.1", {"start": v(149, -224) * mm, "end": v(159, -224) * mm});
            skLineSegment(sketch, "E33.7.16.2", {"start": v(149, -214) * mm, "end": v(149, -224) * mm});
            skLineSegment(sketch, "E33.7.16.3", {"start": v(159, -214) * mm, "end": v(159, -224) * mm});
            skLineSegment(sketch, "E33.7.17.0", {"start": v(149, -200) * mm, "end": v(159, -200) * mm});
            skLineSegment(sketch, "E33.7.17.1", {"start": v(149, -210) * mm, "end": v(159, -210) * mm});
            skLineSegment(sketch, "E33.7.17.2", {"start": v(149, -200) * mm, "end": v(149, -210) * mm});
            skLineSegment(sketch, "E33.7.17.3", {"start": v(159, -200) * mm, "end": v(159, -210) * mm});
            skLineSegment(sketch, "E33.7.18.0", {"start": v(149, -186) * mm, "end": v(159, -186) * mm});
            skLineSegment(sketch, "E33.7.18.1", {"start": v(149, -196) * mm, "end": v(159, -196) * mm});
            skLineSegment(sketch, "E33.7.18.2", {"start": v(149, -186) * mm, "end": v(149, -196) * mm});
            skLineSegment(sketch, "E33.7.18.3", {"start": v(159, -186) * mm, "end": v(159, -196) * mm});
            skLineSegment(sketch, "E33.7.19.0", {"start": v(149, -172) * mm, "end": v(159, -172) * mm});
            skLineSegment(sketch, "E33.7.19.1", {"start": v(149, -182) * mm, "end": v(159, -182) * mm});
            skLineSegment(sketch, "E33.7.19.2", {"start": v(149, -172) * mm, "end": v(149, -182) * mm});
            skLineSegment(sketch, "E33.7.19.3", {"start": v(159, -172) * mm, "end": v(159, -182) * mm});
            skLineSegment(sketch, "E33.7.20.0", {"start": v(149, -158) * mm, "end": v(159, -158) * mm});
            skLineSegment(sketch, "E33.7.20.1", {"start": v(149, -168) * mm, "end": v(159, -168) * mm});
            skLineSegment(sketch, "E33.7.20.2", {"start": v(149, -158) * mm, "end": v(149, -168) * mm});
            skLineSegment(sketch, "E33.7.20.3", {"start": v(159, -158) * mm, "end": v(159, -168) * mm});
            skLineSegment(sketch, "E33.7.21.0", {"start": v(149, -144) * mm, "end": v(159, -144) * mm});
            skLineSegment(sketch, "E33.7.21.1", {"start": v(149, -154) * mm, "end": v(159, -154) * mm});
            skLineSegment(sketch, "E33.7.21.2", {"start": v(149, -144) * mm, "end": v(149, -154) * mm});
            skLineSegment(sketch, "E33.7.21.3", {"start": v(159, -144) * mm, "end": v(159, -154) * mm});
            skLineSegment(sketch, "E33.7.22.0", {"start": v(149, -130) * mm, "end": v(159, -130) * mm});
            skLineSegment(sketch, "E33.7.22.1", {"start": v(149, -140) * mm, "end": v(159, -140) * mm});
            skLineSegment(sketch, "E33.7.22.2", {"start": v(149, -130) * mm, "end": v(149, -140) * mm});
            skLineSegment(sketch, "E33.7.22.3", {"start": v(159, -130) * mm, "end": v(159, -140) * mm});
            skLineSegment(sketch, "E33.7.23.0", {"start": v(149, -116) * mm, "end": v(159, -116) * mm});
            skLineSegment(sketch, "E33.7.23.1", {"start": v(149, -126) * mm, "end": v(159, -126) * mm});
            skLineSegment(sketch, "E33.7.23.2", {"start": v(149, -116) * mm, "end": v(149, -126) * mm});
            skLineSegment(sketch, "E33.7.23.3", {"start": v(159, -116) * mm, "end": v(159, -126) * mm});
            skLineSegment(sketch, "E33.7.24.0", {"start": v(149, -102) * mm, "end": v(159, -102) * mm});
            skLineSegment(sketch, "E33.7.24.1", {"start": v(149, -112) * mm, "end": v(159, -112) * mm});
            skLineSegment(sketch, "E33.7.24.2", {"start": v(149, -102) * mm, "end": v(149, -112) * mm});
            skLineSegment(sketch, "E33.7.24.3", {"start": v(159, -102) * mm, "end": v(159, -112) * mm});
            skLineSegment(sketch, "E33.7.25.0", {"start": v(149, -88) * mm, "end": v(159, -88) * mm});
            skLineSegment(sketch, "E33.7.25.1", {"start": v(149, -98) * mm, "end": v(159, -98) * mm});
            skLineSegment(sketch, "E33.7.25.2", {"start": v(149, -88) * mm, "end": v(149, -98) * mm});
            skLineSegment(sketch, "E33.7.25.3", {"start": v(159, -88) * mm, "end": v(159, -98) * mm});
            skLineSegment(sketch, "E33.7.26.0", {"start": v(149, -74) * mm, "end": v(159, -74) * mm});
            skLineSegment(sketch, "E33.7.26.1", {"start": v(149, -84) * mm, "end": v(159, -84) * mm});
            skLineSegment(sketch, "E33.7.26.2", {"start": v(149, -74) * mm, "end": v(149, -84) * mm});
            skLineSegment(sketch, "E33.7.26.3", {"start": v(159, -74) * mm, "end": v(159, -84) * mm});
            skLineSegment(sketch, "E33.7.27.0", {"start": v(149, -60) * mm, "end": v(159, -60) * mm});
            skLineSegment(sketch, "E33.7.27.1", {"start": v(149, -70) * mm, "end": v(159, -70) * mm});
            skLineSegment(sketch, "E33.7.27.2", {"start": v(149, -60) * mm, "end": v(149, -70) * mm});
            skLineSegment(sketch, "E33.7.27.3", {"start": v(159, -60) * mm, "end": v(159, -70) * mm});
            skLineSegment(sketch, "E33.7.28.0", {"start": v(149, -46) * mm, "end": v(159, -46) * mm});
            skLineSegment(sketch, "E33.7.28.1", {"start": v(149, -56) * mm, "end": v(159, -56) * mm});
            skLineSegment(sketch, "E33.7.28.2", {"start": v(149, -46) * mm, "end": v(149, -56) * mm});
            skLineSegment(sketch, "E33.7.28.3", {"start": v(159, -46) * mm, "end": v(159, -56) * mm});
            skLineSegment(sketch, "E33.7.29.0", {"start": v(149, -32) * mm, "end": v(159, -32) * mm});
            skLineSegment(sketch, "E33.7.29.1", {"start": v(149, -42) * mm, "end": v(159, -42) * mm});
            skLineSegment(sketch, "E33.7.29.2", {"start": v(149, -32) * mm, "end": v(149, -42) * mm});
            skLineSegment(sketch, "E33.7.29.3", {"start": v(159, -32) * mm, "end": v(159, -42) * mm});
            skLineSegment(sketch, "E33.7.30.0", {"start": v(149, -18) * mm, "end": v(159, -18) * mm});
            skLineSegment(sketch, "E33.7.30.1", {"start": v(149, -28) * mm, "end": v(159, -28) * mm});
            skLineSegment(sketch, "E33.7.30.2", {"start": v(149, -18) * mm, "end": v(149, -28) * mm});
            skLineSegment(sketch, "E33.7.30.3", {"start": v(159, -18) * mm, "end": v(159, -28) * mm});
            skLineSegment(sketch, "E33.7.31.0", {"start": v(149, -4) * mm, "end": v(159, -4) * mm});
            skLineSegment(sketch, "E33.7.31.1", {"start": v(149, -14) * mm, "end": v(159, -14) * mm});
            skLineSegment(sketch, "E33.7.31.2", {"start": v(149, -4) * mm, "end": v(149, -14) * mm});
            skLineSegment(sketch, "E33.7.31.3", {"start": v(159, -4) * mm, "end": v(159, -14) * mm});
            skLineSegment(sketch, "E33.8.0.0", {"start": v(135, -438) * mm, "end": v(145, -438) * mm});
            skLineSegment(sketch, "E33.8.0.1", {"start": v(135, -448) * mm, "end": v(145, -448) * mm});
            skLineSegment(sketch, "E33.8.0.2", {"start": v(135, -438) * mm, "end": v(135, -448) * mm});
            skLineSegment(sketch, "E33.8.0.3", {"start": v(145, -438) * mm, "end": v(145, -448) * mm});
            skLineSegment(sketch, "E33.8.1.0", {"start": v(135, -424) * mm, "end": v(145, -424) * mm});
            skLineSegment(sketch, "E33.8.1.1", {"start": v(135, -434) * mm, "end": v(145, -434) * mm});
            skLineSegment(sketch, "E33.8.1.2", {"start": v(135, -424) * mm, "end": v(135, -434) * mm});
            skLineSegment(sketch, "E33.8.1.3", {"start": v(145, -424) * mm, "end": v(145, -434) * mm});
            skLineSegment(sketch, "E33.8.2.0", {"start": v(135, -410) * mm, "end": v(145, -410) * mm});
            skLineSegment(sketch, "E33.8.2.1", {"start": v(135, -420) * mm, "end": v(145, -420) * mm});
            skLineSegment(sketch, "E33.8.2.2", {"start": v(135, -410) * mm, "end": v(135, -420) * mm});
            skLineSegment(sketch, "E33.8.2.3", {"start": v(145, -410) * mm, "end": v(145, -420) * mm});
            skLineSegment(sketch, "E33.8.3.0", {"start": v(135, -396) * mm, "end": v(145, -396) * mm});
            skLineSegment(sketch, "E33.8.3.1", {"start": v(135, -406) * mm, "end": v(145, -406) * mm});
            skLineSegment(sketch, "E33.8.3.2", {"start": v(135, -396) * mm, "end": v(135, -406) * mm});
            skLineSegment(sketch, "E33.8.3.3", {"start": v(145, -396) * mm, "end": v(145, -406) * mm});
            skLineSegment(sketch, "E33.8.4.0", {"start": v(135, -382) * mm, "end": v(145, -382) * mm});
            skLineSegment(sketch, "E33.8.4.1", {"start": v(135, -392) * mm, "end": v(145, -392) * mm});
            skLineSegment(sketch, "E33.8.4.2", {"start": v(135, -382) * mm, "end": v(135, -392) * mm});
            skLineSegment(sketch, "E33.8.4.3", {"start": v(145, -382) * mm, "end": v(145, -392) * mm});
            skLineSegment(sketch, "E33.8.5.0", {"start": v(135, -368) * mm, "end": v(145, -368) * mm});
            skLineSegment(sketch, "E33.8.5.1", {"start": v(135, -378) * mm, "end": v(145, -378) * mm});
            skLineSegment(sketch, "E33.8.5.2", {"start": v(135, -368) * mm, "end": v(135, -378) * mm});
            skLineSegment(sketch, "E33.8.5.3", {"start": v(145, -368) * mm, "end": v(145, -378) * mm});
            skLineSegment(sketch, "E33.8.6.0", {"start": v(135, -354) * mm, "end": v(145, -354) * mm});
            skLineSegment(sketch, "E33.8.6.1", {"start": v(135, -364) * mm, "end": v(145, -364) * mm});
            skLineSegment(sketch, "E33.8.6.2", {"start": v(135, -354) * mm, "end": v(135, -364) * mm});
            skLineSegment(sketch, "E33.8.6.3", {"start": v(145, -354) * mm, "end": v(145, -364) * mm});
            skLineSegment(sketch, "E33.8.7.0", {"start": v(135, -340) * mm, "end": v(145, -340) * mm});
            skLineSegment(sketch, "E33.8.7.1", {"start": v(135, -350) * mm, "end": v(145, -350) * mm});
            skLineSegment(sketch, "E33.8.7.2", {"start": v(135, -340) * mm, "end": v(135, -350) * mm});
            skLineSegment(sketch, "E33.8.7.3", {"start": v(145, -340) * mm, "end": v(145, -350) * mm});
            skLineSegment(sketch, "E33.8.8.0", {"start": v(135, -326) * mm, "end": v(145, -326) * mm});
            skLineSegment(sketch, "E33.8.8.1", {"start": v(135, -336) * mm, "end": v(145, -336) * mm});
            skLineSegment(sketch, "E33.8.8.2", {"start": v(135, -326) * mm, "end": v(135, -336) * mm});
            skLineSegment(sketch, "E33.8.8.3", {"start": v(145, -326) * mm, "end": v(145, -336) * mm});
            skLineSegment(sketch, "E33.8.9.0", {"start": v(135, -312) * mm, "end": v(145, -312) * mm});
            skLineSegment(sketch, "E33.8.9.1", {"start": v(135, -322) * mm, "end": v(145, -322) * mm});
            skLineSegment(sketch, "E33.8.9.2", {"start": v(135, -312) * mm, "end": v(135, -322) * mm});
            skLineSegment(sketch, "E33.8.9.3", {"start": v(145, -312) * mm, "end": v(145, -322) * mm});
            skLineSegment(sketch, "E33.8.10.0", {"start": v(135, -298) * mm, "end": v(145, -298) * mm});
            skLineSegment(sketch, "E33.8.10.1", {"start": v(135, -308) * mm, "end": v(145, -308) * mm});
            skLineSegment(sketch, "E33.8.10.2", {"start": v(135, -298) * mm, "end": v(135, -308) * mm});
            skLineSegment(sketch, "E33.8.10.3", {"start": v(145, -298) * mm, "end": v(145, -308) * mm});
            skLineSegment(sketch, "E33.8.11.0", {"start": v(135, -284) * mm, "end": v(145, -284) * mm});
            skLineSegment(sketch, "E33.8.11.1", {"start": v(135, -294) * mm, "end": v(145, -294) * mm});
            skLineSegment(sketch, "E33.8.11.2", {"start": v(135, -284) * mm, "end": v(135, -294) * mm});
            skLineSegment(sketch, "E33.8.11.3", {"start": v(145, -284) * mm, "end": v(145, -294) * mm});
            skLineSegment(sketch, "E33.8.12.0", {"start": v(135, -270) * mm, "end": v(145, -270) * mm});
            skLineSegment(sketch, "E33.8.12.1", {"start": v(135, -280) * mm, "end": v(145, -280) * mm});
            skLineSegment(sketch, "E33.8.12.2", {"start": v(135, -270) * mm, "end": v(135, -280) * mm});
            skLineSegment(sketch, "E33.8.12.3", {"start": v(145, -270) * mm, "end": v(145, -280) * mm});
            skLineSegment(sketch, "E33.8.13.0", {"start": v(135, -256) * mm, "end": v(145, -256) * mm});
            skLineSegment(sketch, "E33.8.13.1", {"start": v(135, -266) * mm, "end": v(145, -266) * mm});
            skLineSegment(sketch, "E33.8.13.2", {"start": v(135, -256) * mm, "end": v(135, -266) * mm});
            skLineSegment(sketch, "E33.8.13.3", {"start": v(145, -256) * mm, "end": v(145, -266) * mm});
            skLineSegment(sketch, "E33.8.14.0", {"start": v(135, -242) * mm, "end": v(145, -242) * mm});
            skLineSegment(sketch, "E33.8.14.1", {"start": v(135, -252) * mm, "end": v(145, -252) * mm});
            skLineSegment(sketch, "E33.8.14.2", {"start": v(135, -242) * mm, "end": v(135, -252) * mm});
            skLineSegment(sketch, "E33.8.14.3", {"start": v(145, -242) * mm, "end": v(145, -252) * mm});
            skLineSegment(sketch, "E33.8.15.0", {"start": v(135, -228) * mm, "end": v(145, -228) * mm});
            skLineSegment(sketch, "E33.8.15.1", {"start": v(135, -238) * mm, "end": v(145, -238) * mm});
            skLineSegment(sketch, "E33.8.15.2", {"start": v(135, -228) * mm, "end": v(135, -238) * mm});
            skLineSegment(sketch, "E33.8.15.3", {"start": v(145, -228) * mm, "end": v(145, -238) * mm});
            skLineSegment(sketch, "E33.8.16.0", {"start": v(135, -214) * mm, "end": v(145, -214) * mm});
            skLineSegment(sketch, "E33.8.16.1", {"start": v(135, -224) * mm, "end": v(145, -224) * mm});
            skLineSegment(sketch, "E33.8.16.2", {"start": v(135, -214) * mm, "end": v(135, -224) * mm});
            skLineSegment(sketch, "E33.8.16.3", {"start": v(145, -214) * mm, "end": v(145, -224) * mm});
            skLineSegment(sketch, "E33.8.17.0", {"start": v(135, -200) * mm, "end": v(145, -200) * mm});
            skLineSegment(sketch, "E33.8.17.1", {"start": v(135, -210) * mm, "end": v(145, -210) * mm});
            skLineSegment(sketch, "E33.8.17.2", {"start": v(135, -200) * mm, "end": v(135, -210) * mm});
            skLineSegment(sketch, "E33.8.17.3", {"start": v(145, -200) * mm, "end": v(145, -210) * mm});
            skLineSegment(sketch, "E33.8.18.0", {"start": v(135, -186) * mm, "end": v(145, -186) * mm});
            skLineSegment(sketch, "E33.8.18.1", {"start": v(135, -196) * mm, "end": v(145, -196) * mm});
            skLineSegment(sketch, "E33.8.18.2", {"start": v(135, -186) * mm, "end": v(135, -196) * mm});
            skLineSegment(sketch, "E33.8.18.3", {"start": v(145, -186) * mm, "end": v(145, -196) * mm});
            skLineSegment(sketch, "E33.8.19.0", {"start": v(135, -172) * mm, "end": v(145, -172) * mm});
            skLineSegment(sketch, "E33.8.19.1", {"start": v(135, -182) * mm, "end": v(145, -182) * mm});
            skLineSegment(sketch, "E33.8.19.2", {"start": v(135, -172) * mm, "end": v(135, -182) * mm});
            skLineSegment(sketch, "E33.8.19.3", {"start": v(145, -172) * mm, "end": v(145, -182) * mm});
            skLineSegment(sketch, "E33.8.20.0", {"start": v(135, -158) * mm, "end": v(145, -158) * mm});
            skLineSegment(sketch, "E33.8.20.1", {"start": v(135, -168) * mm, "end": v(145, -168) * mm});
            skLineSegment(sketch, "E33.8.20.2", {"start": v(135, -158) * mm, "end": v(135, -168) * mm});
            skLineSegment(sketch, "E33.8.20.3", {"start": v(145, -158) * mm, "end": v(145, -168) * mm});
            skLineSegment(sketch, "E33.8.21.0", {"start": v(135, -144) * mm, "end": v(145, -144) * mm});
            skLineSegment(sketch, "E33.8.21.1", {"start": v(135, -154) * mm, "end": v(145, -154) * mm});
            skLineSegment(sketch, "E33.8.21.2", {"start": v(135, -144) * mm, "end": v(135, -154) * mm});
            skLineSegment(sketch, "E33.8.21.3", {"start": v(145, -144) * mm, "end": v(145, -154) * mm});
            skLineSegment(sketch, "E33.8.22.0", {"start": v(135, -130) * mm, "end": v(145, -130) * mm});
            skLineSegment(sketch, "E33.8.22.1", {"start": v(135, -140) * mm, "end": v(145, -140) * mm});
            skLineSegment(sketch, "E33.8.22.2", {"start": v(135, -130) * mm, "end": v(135, -140) * mm});
            skLineSegment(sketch, "E33.8.22.3", {"start": v(145, -130) * mm, "end": v(145, -140) * mm});
            skLineSegment(sketch, "E33.8.23.0", {"start": v(135, -116) * mm, "end": v(145, -116) * mm});
            skLineSegment(sketch, "E33.8.23.1", {"start": v(135, -126) * mm, "end": v(145, -126) * mm});
            skLineSegment(sketch, "E33.8.23.2", {"start": v(135, -116) * mm, "end": v(135, -126) * mm});
            skLineSegment(sketch, "E33.8.23.3", {"start": v(145, -116) * mm, "end": v(145, -126) * mm});
            skLineSegment(sketch, "E33.8.24.0", {"start": v(135, -102) * mm, "end": v(145, -102) * mm});
            skLineSegment(sketch, "E33.8.24.1", {"start": v(135, -112) * mm, "end": v(145, -112) * mm});
            skLineSegment(sketch, "E33.8.24.2", {"start": v(135, -102) * mm, "end": v(135, -112) * mm});
            skLineSegment(sketch, "E33.8.24.3", {"start": v(145, -102) * mm, "end": v(145, -112) * mm});
            skLineSegment(sketch, "E33.8.25.0", {"start": v(135, -88) * mm, "end": v(145, -88) * mm});
            skLineSegment(sketch, "E33.8.25.1", {"start": v(135, -98) * mm, "end": v(145, -98) * mm});
            skLineSegment(sketch, "E33.8.25.2", {"start": v(135, -88) * mm, "end": v(135, -98) * mm});
            skLineSegment(sketch, "E33.8.25.3", {"start": v(145, -88) * mm, "end": v(145, -98) * mm});
            skLineSegment(sketch, "E33.8.26.0", {"start": v(135, -74) * mm, "end": v(145, -74) * mm});
            skLineSegment(sketch, "E33.8.26.1", {"start": v(135, -84) * mm, "end": v(145, -84) * mm});
            skLineSegment(sketch, "E33.8.26.2", {"start": v(135, -74) * mm, "end": v(135, -84) * mm});
            skLineSegment(sketch, "E33.8.26.3", {"start": v(145, -74) * mm, "end": v(145, -84) * mm});
            skLineSegment(sketch, "E33.8.27.0", {"start": v(135, -60) * mm, "end": v(145, -60) * mm});
            skLineSegment(sketch, "E33.8.27.1", {"start": v(135, -70) * mm, "end": v(145, -70) * mm});
            skLineSegment(sketch, "E33.8.27.2", {"start": v(135, -60) * mm, "end": v(135, -70) * mm});
            skLineSegment(sketch, "E33.8.27.3", {"start": v(145, -60) * mm, "end": v(145, -70) * mm});
            skLineSegment(sketch, "E33.8.28.0", {"start": v(135, -46) * mm, "end": v(145, -46) * mm});
            skLineSegment(sketch, "E33.8.28.1", {"start": v(135, -56) * mm, "end": v(145, -56) * mm});
            skLineSegment(sketch, "E33.8.28.2", {"start": v(135, -46) * mm, "end": v(135, -56) * mm});
            skLineSegment(sketch, "E33.8.28.3", {"start": v(145, -46) * mm, "end": v(145, -56) * mm});
            skLineSegment(sketch, "E33.8.29.0", {"start": v(135, -32) * mm, "end": v(145, -32) * mm});
            skLineSegment(sketch, "E33.8.29.1", {"start": v(135, -42) * mm, "end": v(145, -42) * mm});
            skLineSegment(sketch, "E33.8.29.2", {"start": v(135, -32) * mm, "end": v(135, -42) * mm});
            skLineSegment(sketch, "E33.8.29.3", {"start": v(145, -32) * mm, "end": v(145, -42) * mm});
            skLineSegment(sketch, "E33.8.30.0", {"start": v(135, -18) * mm, "end": v(145, -18) * mm});
            skLineSegment(sketch, "E33.8.30.1", {"start": v(135, -28) * mm, "end": v(145, -28) * mm});
            skLineSegment(sketch, "E33.8.30.2", {"start": v(135, -18) * mm, "end": v(135, -28) * mm});
            skLineSegment(sketch, "E33.8.30.3", {"start": v(145, -18) * mm, "end": v(145, -28) * mm});
            skLineSegment(sketch, "E33.8.31.0", {"start": v(135, -4) * mm, "end": v(145, -4) * mm});
            skLineSegment(sketch, "E33.8.31.1", {"start": v(135, -14) * mm, "end": v(145, -14) * mm});
            skLineSegment(sketch, "E33.8.31.2", {"start": v(135, -4) * mm, "end": v(135, -14) * mm});
            skLineSegment(sketch, "E33.8.31.3", {"start": v(145, -4) * mm, "end": v(145, -14) * mm});
            skLineSegment(sketch, "E33.9.0.0", {"start": v(121, -438) * mm, "end": v(131, -438) * mm});
            skLineSegment(sketch, "E33.9.0.1", {"start": v(121, -448) * mm, "end": v(131, -448) * mm});
            skLineSegment(sketch, "E33.9.0.2", {"start": v(121, -438) * mm, "end": v(121, -448) * mm});
            skLineSegment(sketch, "E33.9.0.3", {"start": v(131, -438) * mm, "end": v(131, -448) * mm});
            skLineSegment(sketch, "E33.9.1.0", {"start": v(121, -424) * mm, "end": v(131, -424) * mm});
            skLineSegment(sketch, "E33.9.1.1", {"start": v(121, -434) * mm, "end": v(131, -434) * mm});
            skLineSegment(sketch, "E33.9.1.2", {"start": v(121, -424) * mm, "end": v(121, -434) * mm});
            skLineSegment(sketch, "E33.9.1.3", {"start": v(131, -424) * mm, "end": v(131, -434) * mm});
            skLineSegment(sketch, "E33.9.2.0", {"start": v(121, -410) * mm, "end": v(131, -410) * mm});
            skLineSegment(sketch, "E33.9.2.1", {"start": v(121, -420) * mm, "end": v(131, -420) * mm});
            skLineSegment(sketch, "E33.9.2.2", {"start": v(121, -410) * mm, "end": v(121, -420) * mm});
            skLineSegment(sketch, "E33.9.2.3", {"start": v(131, -410) * mm, "end": v(131, -420) * mm});
            skLineSegment(sketch, "E33.9.3.0", {"start": v(121, -396) * mm, "end": v(131, -396) * mm});
            skLineSegment(sketch, "E33.9.3.1", {"start": v(121, -406) * mm, "end": v(131, -406) * mm});
            skLineSegment(sketch, "E33.9.3.2", {"start": v(121, -396) * mm, "end": v(121, -406) * mm});
            skLineSegment(sketch, "E33.9.3.3", {"start": v(131, -396) * mm, "end": v(131, -406) * mm});
            skLineSegment(sketch, "E33.9.4.0", {"start": v(121, -382) * mm, "end": v(131, -382) * mm});
            skLineSegment(sketch, "E33.9.4.1", {"start": v(121, -392) * mm, "end": v(131, -392) * mm});
            skLineSegment(sketch, "E33.9.4.2", {"start": v(121, -382) * mm, "end": v(121, -392) * mm});
            skLineSegment(sketch, "E33.9.4.3", {"start": v(131, -382) * mm, "end": v(131, -392) * mm});
            skLineSegment(sketch, "E33.9.5.0", {"start": v(121, -368) * mm, "end": v(131, -368) * mm});
            skLineSegment(sketch, "E33.9.5.1", {"start": v(121, -378) * mm, "end": v(131, -378) * mm});
            skLineSegment(sketch, "E33.9.5.2", {"start": v(121, -368) * mm, "end": v(121, -378) * mm});
            skLineSegment(sketch, "E33.9.5.3", {"start": v(131, -368) * mm, "end": v(131, -378) * mm});
            skLineSegment(sketch, "E33.9.6.0", {"start": v(121, -354) * mm, "end": v(131, -354) * mm});
            skLineSegment(sketch, "E33.9.6.1", {"start": v(121, -364) * mm, "end": v(131, -364) * mm});
            skLineSegment(sketch, "E33.9.6.2", {"start": v(121, -354) * mm, "end": v(121, -364) * mm});
            skLineSegment(sketch, "E33.9.6.3", {"start": v(131, -354) * mm, "end": v(131, -364) * mm});
            skLineSegment(sketch, "E33.9.7.0", {"start": v(121, -340) * mm, "end": v(131, -340) * mm});
            skLineSegment(sketch, "E33.9.7.1", {"start": v(121, -350) * mm, "end": v(131, -350) * mm});
            skLineSegment(sketch, "E33.9.7.2", {"start": v(121, -340) * mm, "end": v(121, -350) * mm});
            skLineSegment(sketch, "E33.9.7.3", {"start": v(131, -340) * mm, "end": v(131, -350) * mm});
            skLineSegment(sketch, "E33.9.8.0", {"start": v(121, -326) * mm, "end": v(131, -326) * mm});
            skLineSegment(sketch, "E33.9.8.1", {"start": v(121, -336) * mm, "end": v(131, -336) * mm});
            skLineSegment(sketch, "E33.9.8.2", {"start": v(121, -326) * mm, "end": v(121, -336) * mm});
            skLineSegment(sketch, "E33.9.8.3", {"start": v(131, -326) * mm, "end": v(131, -336) * mm});
            skLineSegment(sketch, "E33.9.9.0", {"start": v(121, -312) * mm, "end": v(131, -312) * mm});
            skLineSegment(sketch, "E33.9.9.1", {"start": v(121, -322) * mm, "end": v(131, -322) * mm});
            skLineSegment(sketch, "E33.9.9.2", {"start": v(121, -312) * mm, "end": v(121, -322) * mm});
            skLineSegment(sketch, "E33.9.9.3", {"start": v(131, -312) * mm, "end": v(131, -322) * mm});
            skLineSegment(sketch, "E33.9.10.0", {"start": v(121, -298) * mm, "end": v(131, -298) * mm});
            skLineSegment(sketch, "E33.9.10.1", {"start": v(121, -308) * mm, "end": v(131, -308) * mm});
            skLineSegment(sketch, "E33.9.10.2", {"start": v(121, -298) * mm, "end": v(121, -308) * mm});
            skLineSegment(sketch, "E33.9.10.3", {"start": v(131, -298) * mm, "end": v(131, -308) * mm});
            skLineSegment(sketch, "E33.9.11.0", {"start": v(121, -284) * mm, "end": v(131, -284) * mm});
            skLineSegment(sketch, "E33.9.11.1", {"start": v(121, -294) * mm, "end": v(131, -294) * mm});
            skLineSegment(sketch, "E33.9.11.2", {"start": v(121, -284) * mm, "end": v(121, -294) * mm});
            skLineSegment(sketch, "E33.9.11.3", {"start": v(131, -284) * mm, "end": v(131, -294) * mm});
            skLineSegment(sketch, "E33.9.12.0", {"start": v(121, -270) * mm, "end": v(131, -270) * mm});
            skLineSegment(sketch, "E33.9.12.1", {"start": v(121, -280) * mm, "end": v(131, -280) * mm});
            skLineSegment(sketch, "E33.9.12.2", {"start": v(121, -270) * mm, "end": v(121, -280) * mm});
            skLineSegment(sketch, "E33.9.12.3", {"start": v(131, -270) * mm, "end": v(131, -280) * mm});
            skLineSegment(sketch, "E33.9.13.0", {"start": v(121, -256) * mm, "end": v(131, -256) * mm});
            skLineSegment(sketch, "E33.9.13.1", {"start": v(121, -266) * mm, "end": v(131, -266) * mm});
            skLineSegment(sketch, "E33.9.13.2", {"start": v(121, -256) * mm, "end": v(121, -266) * mm});
            skLineSegment(sketch, "E33.9.13.3", {"start": v(131, -256) * mm, "end": v(131, -266) * mm});
            skLineSegment(sketch, "E33.9.14.0", {"start": v(121, -242) * mm, "end": v(131, -242) * mm});
            skLineSegment(sketch, "E33.9.14.1", {"start": v(121, -252) * mm, "end": v(131, -252) * mm});
            skLineSegment(sketch, "E33.9.14.2", {"start": v(121, -242) * mm, "end": v(121, -252) * mm});
            skLineSegment(sketch, "E33.9.14.3", {"start": v(131, -242) * mm, "end": v(131, -252) * mm});
            skLineSegment(sketch, "E33.9.15.0", {"start": v(121, -228) * mm, "end": v(131, -228) * mm});
            skLineSegment(sketch, "E33.9.15.1", {"start": v(121, -238) * mm, "end": v(131, -238) * mm});
            skLineSegment(sketch, "E33.9.15.2", {"start": v(121, -228) * mm, "end": v(121, -238) * mm});
            skLineSegment(sketch, "E33.9.15.3", {"start": v(131, -228) * mm, "end": v(131, -238) * mm});
            skLineSegment(sketch, "E33.9.16.0", {"start": v(121, -214) * mm, "end": v(131, -214) * mm});
            skLineSegment(sketch, "E33.9.16.1", {"start": v(121, -224) * mm, "end": v(131, -224) * mm});
            skLineSegment(sketch, "E33.9.16.2", {"start": v(121, -214) * mm, "end": v(121, -224) * mm});
            skLineSegment(sketch, "E33.9.16.3", {"start": v(131, -214) * mm, "end": v(131, -224) * mm});
            skLineSegment(sketch, "E33.9.17.0", {"start": v(121, -200) * mm, "end": v(131, -200) * mm});
            skLineSegment(sketch, "E33.9.17.1", {"start": v(121, -210) * mm, "end": v(131, -210) * mm});
            skLineSegment(sketch, "E33.9.17.2", {"start": v(121, -200) * mm, "end": v(121, -210) * mm});
            skLineSegment(sketch, "E33.9.17.3", {"start": v(131, -200) * mm, "end": v(131, -210) * mm});
            skLineSegment(sketch, "E33.9.18.0", {"start": v(121, -186) * mm, "end": v(131, -186) * mm});
            skLineSegment(sketch, "E33.9.18.1", {"start": v(121, -196) * mm, "end": v(131, -196) * mm});
            skLineSegment(sketch, "E33.9.18.2", {"start": v(121, -186) * mm, "end": v(121, -196) * mm});
            skLineSegment(sketch, "E33.9.18.3", {"start": v(131, -186) * mm, "end": v(131, -196) * mm});
            skLineSegment(sketch, "E33.9.19.0", {"start": v(121, -172) * mm, "end": v(131, -172) * mm});
            skLineSegment(sketch, "E33.9.19.1", {"start": v(121, -182) * mm, "end": v(131, -182) * mm});
            skLineSegment(sketch, "E33.9.19.2", {"start": v(121, -172) * mm, "end": v(121, -182) * mm});
            skLineSegment(sketch, "E33.9.19.3", {"start": v(131, -172) * mm, "end": v(131, -182) * mm});
            skLineSegment(sketch, "E33.9.20.0", {"start": v(121, -158) * mm, "end": v(131, -158) * mm});
            skLineSegment(sketch, "E33.9.20.1", {"start": v(121, -168) * mm, "end": v(131, -168) * mm});
            skLineSegment(sketch, "E33.9.20.2", {"start": v(121, -158) * mm, "end": v(121, -168) * mm});
            skLineSegment(sketch, "E33.9.20.3", {"start": v(131, -158) * mm, "end": v(131, -168) * mm});
            skLineSegment(sketch, "E33.9.21.0", {"start": v(121, -144) * mm, "end": v(131, -144) * mm});
            skLineSegment(sketch, "E33.9.21.1", {"start": v(121, -154) * mm, "end": v(131, -154) * mm});
            skLineSegment(sketch, "E33.9.21.2", {"start": v(121, -144) * mm, "end": v(121, -154) * mm});
            skLineSegment(sketch, "E33.9.21.3", {"start": v(131, -144) * mm, "end": v(131, -154) * mm});
            skLineSegment(sketch, "E33.9.22.0", {"start": v(121, -130) * mm, "end": v(131, -130) * mm});
            skLineSegment(sketch, "E33.9.22.1", {"start": v(121, -140) * mm, "end": v(131, -140) * mm});
            skLineSegment(sketch, "E33.9.22.2", {"start": v(121, -130) * mm, "end": v(121, -140) * mm});
            skLineSegment(sketch, "E33.9.22.3", {"start": v(131, -130) * mm, "end": v(131, -140) * mm});
            skLineSegment(sketch, "E33.9.23.0", {"start": v(121, -116) * mm, "end": v(131, -116) * mm});
            skLineSegment(sketch, "E33.9.23.1", {"start": v(121, -126) * mm, "end": v(131, -126) * mm});
            skLineSegment(sketch, "E33.9.23.2", {"start": v(121, -116) * mm, "end": v(121, -126) * mm});
            skLineSegment(sketch, "E33.9.23.3", {"start": v(131, -116) * mm, "end": v(131, -126) * mm});
            skLineSegment(sketch, "E33.9.24.0", {"start": v(121, -102) * mm, "end": v(131, -102) * mm});
            skLineSegment(sketch, "E33.9.24.1", {"start": v(121, -112) * mm, "end": v(131, -112) * mm});
            skLineSegment(sketch, "E33.9.24.2", {"start": v(121, -102) * mm, "end": v(121, -112) * mm});
            skLineSegment(sketch, "E33.9.24.3", {"start": v(131, -102) * mm, "end": v(131, -112) * mm});
            skLineSegment(sketch, "E33.9.25.0", {"start": v(121, -88) * mm, "end": v(131, -88) * mm});
            skLineSegment(sketch, "E33.9.25.1", {"start": v(121, -98) * mm, "end": v(131, -98) * mm});
            skLineSegment(sketch, "E33.9.25.2", {"start": v(121, -88) * mm, "end": v(121, -98) * mm});
            skLineSegment(sketch, "E33.9.25.3", {"start": v(131, -88) * mm, "end": v(131, -98) * mm});
            skLineSegment(sketch, "E33.9.26.0", {"start": v(121, -74) * mm, "end": v(131, -74) * mm});
            skLineSegment(sketch, "E33.9.26.1", {"start": v(121, -84) * mm, "end": v(131, -84) * mm});
            skLineSegment(sketch, "E33.9.26.2", {"start": v(121, -74) * mm, "end": v(121, -84) * mm});
            skLineSegment(sketch, "E33.9.26.3", {"start": v(131, -74) * mm, "end": v(131, -84) * mm});
            skLineSegment(sketch, "E33.9.27.0", {"start": v(121, -60) * mm, "end": v(131, -60) * mm});
            skLineSegment(sketch, "E33.9.27.1", {"start": v(121, -70) * mm, "end": v(131, -70) * mm});
            skLineSegment(sketch, "E33.9.27.2", {"start": v(121, -60) * mm, "end": v(121, -70) * mm});
            skLineSegment(sketch, "E33.9.27.3", {"start": v(131, -60) * mm, "end": v(131, -70) * mm});
            skLineSegment(sketch, "E33.9.28.0", {"start": v(121, -46) * mm, "end": v(131, -46) * mm});
            skLineSegment(sketch, "E33.9.28.1", {"start": v(121, -56) * mm, "end": v(131, -56) * mm});
            skLineSegment(sketch, "E33.9.28.2", {"start": v(121, -46) * mm, "end": v(121, -56) * mm});
            skLineSegment(sketch, "E33.9.28.3", {"start": v(131, -46) * mm, "end": v(131, -56) * mm});
            skLineSegment(sketch, "E33.9.29.0", {"start": v(121, -32) * mm, "end": v(131, -32) * mm});
            skLineSegment(sketch, "E33.9.29.1", {"start": v(121, -42) * mm, "end": v(131, -42) * mm});
            skLineSegment(sketch, "E33.9.29.2", {"start": v(121, -32) * mm, "end": v(121, -42) * mm});
            skLineSegment(sketch, "E33.9.29.3", {"start": v(131, -32) * mm, "end": v(131, -42) * mm});
            skLineSegment(sketch, "E33.9.30.0", {"start": v(121, -18) * mm, "end": v(131, -18) * mm});
            skLineSegment(sketch, "E33.9.30.1", {"start": v(121, -28) * mm, "end": v(131, -28) * mm});
            skLineSegment(sketch, "E33.9.30.2", {"start": v(121, -18) * mm, "end": v(121, -28) * mm});
            skLineSegment(sketch, "E33.9.30.3", {"start": v(131, -18) * mm, "end": v(131, -28) * mm});
            skLineSegment(sketch, "E33.9.31.0", {"start": v(121, -4) * mm, "end": v(131, -4) * mm});
            skLineSegment(sketch, "E33.9.31.1", {"start": v(121, -14) * mm, "end": v(131, -14) * mm});
            skLineSegment(sketch, "E33.9.31.2", {"start": v(121, -4) * mm, "end": v(121, -14) * mm});
            skLineSegment(sketch, "E33.9.31.3", {"start": v(131, -4) * mm, "end": v(131, -14) * mm});
            skLineSegment(sketch, "E33.10.0.0", {"start": v(107, -438) * mm, "end": v(117, -438) * mm});
            skLineSegment(sketch, "E33.10.0.1", {"start": v(107, -448) * mm, "end": v(117, -448) * mm});
            skLineSegment(sketch, "E33.10.0.2", {"start": v(107, -438) * mm, "end": v(107, -448) * mm});
            skLineSegment(sketch, "E33.10.0.3", {"start": v(117, -438) * mm, "end": v(117, -448) * mm});
            skLineSegment(sketch, "E33.10.1.0", {"start": v(107, -424) * mm, "end": v(117, -424) * mm});
            skLineSegment(sketch, "E33.10.1.1", {"start": v(107, -434) * mm, "end": v(117, -434) * mm});
            skLineSegment(sketch, "E33.10.1.2", {"start": v(107, -424) * mm, "end": v(107, -434) * mm});
            skLineSegment(sketch, "E33.10.1.3", {"start": v(117, -424) * mm, "end": v(117, -434) * mm});
            skLineSegment(sketch, "E33.10.2.0", {"start": v(107, -410) * mm, "end": v(117, -410) * mm});
            skLineSegment(sketch, "E33.10.2.1", {"start": v(107, -420) * mm, "end": v(117, -420) * mm});
            skLineSegment(sketch, "E33.10.2.2", {"start": v(107, -410) * mm, "end": v(107, -420) * mm});
            skLineSegment(sketch, "E33.10.2.3", {"start": v(117, -410) * mm, "end": v(117, -420) * mm});
            skLineSegment(sketch, "E33.10.3.0", {"start": v(107, -396) * mm, "end": v(117, -396) * mm});
            skLineSegment(sketch, "E33.10.3.1", {"start": v(107, -406) * mm, "end": v(117, -406) * mm});
            skLineSegment(sketch, "E33.10.3.2", {"start": v(107, -396) * mm, "end": v(107, -406) * mm});
            skLineSegment(sketch, "E33.10.3.3", {"start": v(117, -396) * mm, "end": v(117, -406) * mm});
            skLineSegment(sketch, "E33.10.4.0", {"start": v(107, -382) * mm, "end": v(117, -382) * mm});
            skLineSegment(sketch, "E33.10.4.1", {"start": v(107, -392) * mm, "end": v(117, -392) * mm});
            skLineSegment(sketch, "E33.10.4.2", {"start": v(107, -382) * mm, "end": v(107, -392) * mm});
            skLineSegment(sketch, "E33.10.4.3", {"start": v(117, -382) * mm, "end": v(117, -392) * mm});
            skLineSegment(sketch, "E33.10.5.0", {"start": v(107, -368) * mm, "end": v(117, -368) * mm});
            skLineSegment(sketch, "E33.10.5.1", {"start": v(107, -378) * mm, "end": v(117, -378) * mm});
            skLineSegment(sketch, "E33.10.5.2", {"start": v(107, -368) * mm, "end": v(107, -378) * mm});
            skLineSegment(sketch, "E33.10.5.3", {"start": v(117, -368) * mm, "end": v(117, -378) * mm});
            skLineSegment(sketch, "E33.10.6.0", {"start": v(107, -354) * mm, "end": v(117, -354) * mm});
            skLineSegment(sketch, "E33.10.6.1", {"start": v(107, -364) * mm, "end": v(117, -364) * mm});
            skLineSegment(sketch, "E33.10.6.2", {"start": v(107, -354) * mm, "end": v(107, -364) * mm});
            skLineSegment(sketch, "E33.10.6.3", {"start": v(117, -354) * mm, "end": v(117, -364) * mm});
            skLineSegment(sketch, "E33.10.7.0", {"start": v(107, -340) * mm, "end": v(117, -340) * mm});
            skLineSegment(sketch, "E33.10.7.1", {"start": v(107, -350) * mm, "end": v(117, -350) * mm});
            skLineSegment(sketch, "E33.10.7.2", {"start": v(107, -340) * mm, "end": v(107, -350) * mm});
            skLineSegment(sketch, "E33.10.7.3", {"start": v(117, -340) * mm, "end": v(117, -350) * mm});
            skLineSegment(sketch, "E33.10.8.0", {"start": v(107, -326) * mm, "end": v(117, -326) * mm});
            skLineSegment(sketch, "E33.10.8.1", {"start": v(107, -336) * mm, "end": v(117, -336) * mm});
            skLineSegment(sketch, "E33.10.8.2", {"start": v(107, -326) * mm, "end": v(107, -336) * mm});
            skLineSegment(sketch, "E33.10.8.3", {"start": v(117, -326) * mm, "end": v(117, -336) * mm});
            skLineSegment(sketch, "E33.10.9.0", {"start": v(107, -312) * mm, "end": v(117, -312) * mm});
            skLineSegment(sketch, "E33.10.9.1", {"start": v(107, -322) * mm, "end": v(117, -322) * mm});
            skLineSegment(sketch, "E33.10.9.2", {"start": v(107, -312) * mm, "end": v(107, -322) * mm});
            skLineSegment(sketch, "E33.10.9.3", {"start": v(117, -312) * mm, "end": v(117, -322) * mm});
            skLineSegment(sketch, "E33.10.10.0", {"start": v(107, -298) * mm, "end": v(117, -298) * mm});
            skLineSegment(sketch, "E33.10.10.1", {"start": v(107, -308) * mm, "end": v(117, -308) * mm});
            skLineSegment(sketch, "E33.10.10.2", {"start": v(107, -298) * mm, "end": v(107, -308) * mm});
            skLineSegment(sketch, "E33.10.10.3", {"start": v(117, -298) * mm, "end": v(117, -308) * mm});
            skLineSegment(sketch, "E33.10.11.0", {"start": v(107, -284) * mm, "end": v(117, -284) * mm});
            skLineSegment(sketch, "E33.10.11.1", {"start": v(107, -294) * mm, "end": v(117, -294) * mm});
            skLineSegment(sketch, "E33.10.11.2", {"start": v(107, -284) * mm, "end": v(107, -294) * mm});
            skLineSegment(sketch, "E33.10.11.3", {"start": v(117, -284) * mm, "end": v(117, -294) * mm});
            skLineSegment(sketch, "E33.10.12.0", {"start": v(107, -270) * mm, "end": v(117, -270) * mm});
            skLineSegment(sketch, "E33.10.12.1", {"start": v(107, -280) * mm, "end": v(117, -280) * mm});
            skLineSegment(sketch, "E33.10.12.2", {"start": v(107, -270) * mm, "end": v(107, -280) * mm});
            skLineSegment(sketch, "E33.10.12.3", {"start": v(117, -270) * mm, "end": v(117, -280) * mm});
            skLineSegment(sketch, "E33.10.13.0", {"start": v(107, -256) * mm, "end": v(117, -256) * mm});
            skLineSegment(sketch, "E33.10.13.1", {"start": v(107, -266) * mm, "end": v(117, -266) * mm});
            skLineSegment(sketch, "E33.10.13.2", {"start": v(107, -256) * mm, "end": v(107, -266) * mm});
            skLineSegment(sketch, "E33.10.13.3", {"start": v(117, -256) * mm, "end": v(117, -266) * mm});
            skLineSegment(sketch, "E33.10.14.0", {"start": v(107, -242) * mm, "end": v(117, -242) * mm});
            skLineSegment(sketch, "E33.10.14.1", {"start": v(107, -252) * mm, "end": v(117, -252) * mm});
            skLineSegment(sketch, "E33.10.14.2", {"start": v(107, -242) * mm, "end": v(107, -252) * mm});
            skLineSegment(sketch, "E33.10.14.3", {"start": v(117, -242) * mm, "end": v(117, -252) * mm});
            skLineSegment(sketch, "E33.10.15.0", {"start": v(107, -228) * mm, "end": v(117, -228) * mm});
            skLineSegment(sketch, "E33.10.15.1", {"start": v(107, -238) * mm, "end": v(117, -238) * mm});
            skLineSegment(sketch, "E33.10.15.2", {"start": v(107, -228) * mm, "end": v(107, -238) * mm});
            skLineSegment(sketch, "E33.10.15.3", {"start": v(117, -228) * mm, "end": v(117, -238) * mm});
            skLineSegment(sketch, "E33.10.16.0", {"start": v(107, -214) * mm, "end": v(117, -214) * mm});
            skLineSegment(sketch, "E33.10.16.1", {"start": v(107, -224) * mm, "end": v(117, -224) * mm});
            skLineSegment(sketch, "E33.10.16.2", {"start": v(107, -214) * mm, "end": v(107, -224) * mm});
            skLineSegment(sketch, "E33.10.16.3", {"start": v(117, -214) * mm, "end": v(117, -224) * mm});
            skLineSegment(sketch, "E33.10.17.0", {"start": v(107, -200) * mm, "end": v(117, -200) * mm});
            skLineSegment(sketch, "E33.10.17.1", {"start": v(107, -210) * mm, "end": v(117, -210) * mm});
            skLineSegment(sketch, "E33.10.17.2", {"start": v(107, -200) * mm, "end": v(107, -210) * mm});
            skLineSegment(sketch, "E33.10.17.3", {"start": v(117, -200) * mm, "end": v(117, -210) * mm});
            skLineSegment(sketch, "E33.10.18.0", {"start": v(107, -186) * mm, "end": v(117, -186) * mm});
            skLineSegment(sketch, "E33.10.18.1", {"start": v(107, -196) * mm, "end": v(117, -196) * mm});
            skLineSegment(sketch, "E33.10.18.2", {"start": v(107, -186) * mm, "end": v(107, -196) * mm});
            skLineSegment(sketch, "E33.10.18.3", {"start": v(117, -186) * mm, "end": v(117, -196) * mm});
            skLineSegment(sketch, "E33.10.19.0", {"start": v(107, -172) * mm, "end": v(117, -172) * mm});
            skLineSegment(sketch, "E33.10.19.1", {"start": v(107, -182) * mm, "end": v(117, -182) * mm});
            skLineSegment(sketch, "E33.10.19.2", {"start": v(107, -172) * mm, "end": v(107, -182) * mm});
            skLineSegment(sketch, "E33.10.19.3", {"start": v(117, -172) * mm, "end": v(117, -182) * mm});
            skLineSegment(sketch, "E33.10.20.0", {"start": v(107, -158) * mm, "end": v(117, -158) * mm});
            skLineSegment(sketch, "E33.10.20.1", {"start": v(107, -168) * mm, "end": v(117, -168) * mm});
            skLineSegment(sketch, "E33.10.20.2", {"start": v(107, -158) * mm, "end": v(107, -168) * mm});
            skLineSegment(sketch, "E33.10.20.3", {"start": v(117, -158) * mm, "end": v(117, -168) * mm});
            skLineSegment(sketch, "E33.10.21.0", {"start": v(107, -144) * mm, "end": v(117, -144) * mm});
            skLineSegment(sketch, "E33.10.21.1", {"start": v(107, -154) * mm, "end": v(117, -154) * mm});
            skLineSegment(sketch, "E33.10.21.2", {"start": v(107, -144) * mm, "end": v(107, -154) * mm});
            skLineSegment(sketch, "E33.10.21.3", {"start": v(117, -144) * mm, "end": v(117, -154) * mm});
            skLineSegment(sketch, "E33.10.22.0", {"start": v(107, -130) * mm, "end": v(117, -130) * mm});
            skLineSegment(sketch, "E33.10.22.1", {"start": v(107, -140) * mm, "end": v(117, -140) * mm});
            skLineSegment(sketch, "E33.10.22.2", {"start": v(107, -130) * mm, "end": v(107, -140) * mm});
            skLineSegment(sketch, "E33.10.22.3", {"start": v(117, -130) * mm, "end": v(117, -140) * mm});
            skLineSegment(sketch, "E33.10.23.0", {"start": v(107, -116) * mm, "end": v(117, -116) * mm});
            skLineSegment(sketch, "E33.10.23.1", {"start": v(107, -126) * mm, "end": v(117, -126) * mm});
            skLineSegment(sketch, "E33.10.23.2", {"start": v(107, -116) * mm, "end": v(107, -126) * mm});
            skLineSegment(sketch, "E33.10.23.3", {"start": v(117, -116) * mm, "end": v(117, -126) * mm});
            skLineSegment(sketch, "E33.10.24.0", {"start": v(107, -102) * mm, "end": v(117, -102) * mm});
            skLineSegment(sketch, "E33.10.24.1", {"start": v(107, -112) * mm, "end": v(117, -112) * mm});
            skLineSegment(sketch, "E33.10.24.2", {"start": v(107, -102) * mm, "end": v(107, -112) * mm});
            skLineSegment(sketch, "E33.10.24.3", {"start": v(117, -102) * mm, "end": v(117, -112) * mm});
            skLineSegment(sketch, "E33.10.25.0", {"start": v(107, -88) * mm, "end": v(117, -88) * mm});
            skLineSegment(sketch, "E33.10.25.1", {"start": v(107, -98) * mm, "end": v(117, -98) * mm});
            skLineSegment(sketch, "E33.10.25.2", {"start": v(107, -88) * mm, "end": v(107, -98) * mm});
            skLineSegment(sketch, "E33.10.25.3", {"start": v(117, -88) * mm, "end": v(117, -98) * mm});
            skLineSegment(sketch, "E33.10.26.0", {"start": v(107, -74) * mm, "end": v(117, -74) * mm});
            skLineSegment(sketch, "E33.10.26.1", {"start": v(107, -84) * mm, "end": v(117, -84) * mm});
            skLineSegment(sketch, "E33.10.26.2", {"start": v(107, -74) * mm, "end": v(107, -84) * mm});
            skLineSegment(sketch, "E33.10.26.3", {"start": v(117, -74) * mm, "end": v(117, -84) * mm});
            skLineSegment(sketch, "E33.10.27.0", {"start": v(107, -60) * mm, "end": v(117, -60) * mm});
            skLineSegment(sketch, "E33.10.27.1", {"start": v(107, -70) * mm, "end": v(117, -70) * mm});
            skLineSegment(sketch, "E33.10.27.2", {"start": v(107, -60) * mm, "end": v(107, -70) * mm});
            skLineSegment(sketch, "E33.10.27.3", {"start": v(117, -60) * mm, "end": v(117, -70) * mm});
            skLineSegment(sketch, "E33.10.28.0", {"start": v(107, -46) * mm, "end": v(117, -46) * mm});
            skLineSegment(sketch, "E33.10.28.1", {"start": v(107, -56) * mm, "end": v(117, -56) * mm});
            skLineSegment(sketch, "E33.10.28.2", {"start": v(107, -46) * mm, "end": v(107, -56) * mm});
            skLineSegment(sketch, "E33.10.28.3", {"start": v(117, -46) * mm, "end": v(117, -56) * mm});
            skLineSegment(sketch, "E33.10.29.0", {"start": v(107, -32) * mm, "end": v(117, -32) * mm});
            skLineSegment(sketch, "E33.10.29.1", {"start": v(107, -42) * mm, "end": v(117, -42) * mm});
            skLineSegment(sketch, "E33.10.29.2", {"start": v(107, -32) * mm, "end": v(107, -42) * mm});
            skLineSegment(sketch, "E33.10.29.3", {"start": v(117, -32) * mm, "end": v(117, -42) * mm});
            skLineSegment(sketch, "E33.10.30.0", {"start": v(107, -18) * mm, "end": v(117, -18) * mm});
            skLineSegment(sketch, "E33.10.30.1", {"start": v(107, -28) * mm, "end": v(117, -28) * mm});
            skLineSegment(sketch, "E33.10.30.2", {"start": v(107, -18) * mm, "end": v(107, -28) * mm});
            skLineSegment(sketch, "E33.10.30.3", {"start": v(117, -18) * mm, "end": v(117, -28) * mm});
            skLineSegment(sketch, "E33.10.31.0", {"start": v(107, -4) * mm, "end": v(117, -4) * mm});
            skLineSegment(sketch, "E33.10.31.1", {"start": v(107, -14) * mm, "end": v(117, -14) * mm});
            skLineSegment(sketch, "E33.10.31.2", {"start": v(107, -4) * mm, "end": v(107, -14) * mm});
            skLineSegment(sketch, "E33.10.31.3", {"start": v(117, -4) * mm, "end": v(117, -14) * mm});
            skLineSegment(sketch, "E33.11.0.0", {"start": v(93, -438) * mm, "end": v(103, -438) * mm});
            skLineSegment(sketch, "E33.11.0.1", {"start": v(93, -448) * mm, "end": v(103, -448) * mm});
            skLineSegment(sketch, "E33.11.0.2", {"start": v(93, -438) * mm, "end": v(93, -448) * mm});
            skLineSegment(sketch, "E33.11.0.3", {"start": v(103, -438) * mm, "end": v(103, -448) * mm});
            skLineSegment(sketch, "E33.11.1.0", {"start": v(93, -424) * mm, "end": v(103, -424) * mm});
            skLineSegment(sketch, "E33.11.1.1", {"start": v(93, -434) * mm, "end": v(103, -434) * mm});
            skLineSegment(sketch, "E33.11.1.2", {"start": v(93, -424) * mm, "end": v(93, -434) * mm});
            skLineSegment(sketch, "E33.11.1.3", {"start": v(103, -424) * mm, "end": v(103, -434) * mm});
            skLineSegment(sketch, "E33.11.2.0", {"start": v(93, -410) * mm, "end": v(103, -410) * mm});
            skLineSegment(sketch, "E33.11.2.1", {"start": v(93, -420) * mm, "end": v(103, -420) * mm});
            skLineSegment(sketch, "E33.11.2.2", {"start": v(93, -410) * mm, "end": v(93, -420) * mm});
            skLineSegment(sketch, "E33.11.2.3", {"start": v(103, -410) * mm, "end": v(103, -420) * mm});
            skLineSegment(sketch, "E33.11.3.0", {"start": v(93, -396) * mm, "end": v(103, -396) * mm});
            skLineSegment(sketch, "E33.11.3.1", {"start": v(93, -406) * mm, "end": v(103, -406) * mm});
            skLineSegment(sketch, "E33.11.3.2", {"start": v(93, -396) * mm, "end": v(93, -406) * mm});
            skLineSegment(sketch, "E33.11.3.3", {"start": v(103, -396) * mm, "end": v(103, -406) * mm});
            skLineSegment(sketch, "E33.11.4.0", {"start": v(93, -382) * mm, "end": v(103, -382) * mm});
            skLineSegment(sketch, "E33.11.4.1", {"start": v(93, -392) * mm, "end": v(103, -392) * mm});
            skLineSegment(sketch, "E33.11.4.2", {"start": v(93, -382) * mm, "end": v(93, -392) * mm});
            skLineSegment(sketch, "E33.11.4.3", {"start": v(103, -382) * mm, "end": v(103, -392) * mm});
            skLineSegment(sketch, "E33.11.5.0", {"start": v(93, -368) * mm, "end": v(103, -368) * mm});
            skLineSegment(sketch, "E33.11.5.1", {"start": v(93, -378) * mm, "end": v(103, -378) * mm});
            skLineSegment(sketch, "E33.11.5.2", {"start": v(93, -368) * mm, "end": v(93, -378) * mm});
            skLineSegment(sketch, "E33.11.5.3", {"start": v(103, -368) * mm, "end": v(103, -378) * mm});
            skLineSegment(sketch, "E33.11.6.0", {"start": v(93, -354) * mm, "end": v(103, -354) * mm});
            skLineSegment(sketch, "E33.11.6.1", {"start": v(93, -364) * mm, "end": v(103, -364) * mm});
            skLineSegment(sketch, "E33.11.6.2", {"start": v(93, -354) * mm, "end": v(93, -364) * mm});
            skLineSegment(sketch, "E33.11.6.3", {"start": v(103, -354) * mm, "end": v(103, -364) * mm});
            skLineSegment(sketch, "E33.11.7.0", {"start": v(93, -340) * mm, "end": v(103, -340) * mm});
            skLineSegment(sketch, "E33.11.7.1", {"start": v(93, -350) * mm, "end": v(103, -350) * mm});
            skLineSegment(sketch, "E33.11.7.2", {"start": v(93, -340) * mm, "end": v(93, -350) * mm});
            skLineSegment(sketch, "E33.11.7.3", {"start": v(103, -340) * mm, "end": v(103, -350) * mm});
            skLineSegment(sketch, "E33.11.8.0", {"start": v(93, -326) * mm, "end": v(103, -326) * mm});
            skLineSegment(sketch, "E33.11.8.1", {"start": v(93, -336) * mm, "end": v(103, -336) * mm});
            skLineSegment(sketch, "E33.11.8.2", {"start": v(93, -326) * mm, "end": v(93, -336) * mm});
            skLineSegment(sketch, "E33.11.8.3", {"start": v(103, -326) * mm, "end": v(103, -336) * mm});
            skLineSegment(sketch, "E33.11.9.0", {"start": v(93, -312) * mm, "end": v(103, -312) * mm});
            skLineSegment(sketch, "E33.11.9.1", {"start": v(93, -322) * mm, "end": v(103, -322) * mm});
            skLineSegment(sketch, "E33.11.9.2", {"start": v(93, -312) * mm, "end": v(93, -322) * mm});
            skLineSegment(sketch, "E33.11.9.3", {"start": v(103, -312) * mm, "end": v(103, -322) * mm});
            skLineSegment(sketch, "E33.11.10.0", {"start": v(93, -298) * mm, "end": v(103, -298) * mm});
            skLineSegment(sketch, "E33.11.10.1", {"start": v(93, -308) * mm, "end": v(103, -308) * mm});
            skLineSegment(sketch, "E33.11.10.2", {"start": v(93, -298) * mm, "end": v(93, -308) * mm});
            skLineSegment(sketch, "E33.11.10.3", {"start": v(103, -298) * mm, "end": v(103, -308) * mm});
            skLineSegment(sketch, "E33.11.11.0", {"start": v(93, -284) * mm, "end": v(103, -284) * mm});
            skLineSegment(sketch, "E33.11.11.1", {"start": v(93, -294) * mm, "end": v(103, -294) * mm});
            skLineSegment(sketch, "E33.11.11.2", {"start": v(93, -284) * mm, "end": v(93, -294) * mm});
            skLineSegment(sketch, "E33.11.11.3", {"start": v(103, -284) * mm, "end": v(103, -294) * mm});
            skLineSegment(sketch, "E33.11.12.0", {"start": v(93, -270) * mm, "end": v(103, -270) * mm});
            skLineSegment(sketch, "E33.11.12.1", {"start": v(93, -280) * mm, "end": v(103, -280) * mm});
            skLineSegment(sketch, "E33.11.12.2", {"start": v(93, -270) * mm, "end": v(93, -280) * mm});
            skLineSegment(sketch, "E33.11.12.3", {"start": v(103, -270) * mm, "end": v(103, -280) * mm});
            skLineSegment(sketch, "E33.11.13.0", {"start": v(93, -256) * mm, "end": v(103, -256) * mm});
            skLineSegment(sketch, "E33.11.13.1", {"start": v(93, -266) * mm, "end": v(103, -266) * mm});
            skLineSegment(sketch, "E33.11.13.2", {"start": v(93, -256) * mm, "end": v(93, -266) * mm});
            skLineSegment(sketch, "E33.11.13.3", {"start": v(103, -256) * mm, "end": v(103, -266) * mm});
            skLineSegment(sketch, "E33.11.14.0", {"start": v(93, -242) * mm, "end": v(103, -242) * mm});
            skLineSegment(sketch, "E33.11.14.1", {"start": v(93, -252) * mm, "end": v(103, -252) * mm});
            skLineSegment(sketch, "E33.11.14.2", {"start": v(93, -242) * mm, "end": v(93, -252) * mm});
            skLineSegment(sketch, "E33.11.14.3", {"start": v(103, -242) * mm, "end": v(103, -252) * mm});
            skLineSegment(sketch, "E33.11.15.0", {"start": v(93, -228) * mm, "end": v(103, -228) * mm});
            skLineSegment(sketch, "E33.11.15.1", {"start": v(93, -238) * mm, "end": v(103, -238) * mm});
            skLineSegment(sketch, "E33.11.15.2", {"start": v(93, -228) * mm, "end": v(93, -238) * mm});
            skLineSegment(sketch, "E33.11.15.3", {"start": v(103, -228) * mm, "end": v(103, -238) * mm});
            skLineSegment(sketch, "E33.11.16.0", {"start": v(93, -214) * mm, "end": v(103, -214) * mm});
            skLineSegment(sketch, "E33.11.16.1", {"start": v(93, -224) * mm, "end": v(103, -224) * mm});
            skLineSegment(sketch, "E33.11.16.2", {"start": v(93, -214) * mm, "end": v(93, -224) * mm});
            skLineSegment(sketch, "E33.11.16.3", {"start": v(103, -214) * mm, "end": v(103, -224) * mm});
            skLineSegment(sketch, "E33.11.17.0", {"start": v(93, -200) * mm, "end": v(103, -200) * mm});
            skLineSegment(sketch, "E33.11.17.1", {"start": v(93, -210) * mm, "end": v(103, -210) * mm});
            skLineSegment(sketch, "E33.11.17.2", {"start": v(93, -200) * mm, "end": v(93, -210) * mm});
            skLineSegment(sketch, "E33.11.17.3", {"start": v(103, -200) * mm, "end": v(103, -210) * mm});
            skLineSegment(sketch, "E33.11.18.0", {"start": v(93, -186) * mm, "end": v(103, -186) * mm});
            skLineSegment(sketch, "E33.11.18.1", {"start": v(93, -196) * mm, "end": v(103, -196) * mm});
            skLineSegment(sketch, "E33.11.18.2", {"start": v(93, -186) * mm, "end": v(93, -196) * mm});
            skLineSegment(sketch, "E33.11.18.3", {"start": v(103, -186) * mm, "end": v(103, -196) * mm});
            skLineSegment(sketch, "E33.11.19.0", {"start": v(93, -172) * mm, "end": v(103, -172) * mm});
            skLineSegment(sketch, "E33.11.19.1", {"start": v(93, -182) * mm, "end": v(103, -182) * mm});
            skLineSegment(sketch, "E33.11.19.2", {"start": v(93, -172) * mm, "end": v(93, -182) * mm});
            skLineSegment(sketch, "E33.11.19.3", {"start": v(103, -172) * mm, "end": v(103, -182) * mm});
            skLineSegment(sketch, "E33.11.20.0", {"start": v(93, -158) * mm, "end": v(103, -158) * mm});
            skLineSegment(sketch, "E33.11.20.1", {"start": v(93, -168) * mm, "end": v(103, -168) * mm});
            skLineSegment(sketch, "E33.11.20.2", {"start": v(93, -158) * mm, "end": v(93, -168) * mm});
            skLineSegment(sketch, "E33.11.20.3", {"start": v(103, -158) * mm, "end": v(103, -168) * mm});
            skLineSegment(sketch, "E33.11.21.0", {"start": v(93, -144) * mm, "end": v(103, -144) * mm});
            skLineSegment(sketch, "E33.11.21.1", {"start": v(93, -154) * mm, "end": v(103, -154) * mm});
            skLineSegment(sketch, "E33.11.21.2", {"start": v(93, -144) * mm, "end": v(93, -154) * mm});
            skLineSegment(sketch, "E33.11.21.3", {"start": v(103, -144) * mm, "end": v(103, -154) * mm});
            skLineSegment(sketch, "E33.11.22.0", {"start": v(93, -130) * mm, "end": v(103, -130) * mm});
            skLineSegment(sketch, "E33.11.22.1", {"start": v(93, -140) * mm, "end": v(103, -140) * mm});
            skLineSegment(sketch, "E33.11.22.2", {"start": v(93, -130) * mm, "end": v(93, -140) * mm});
            skLineSegment(sketch, "E33.11.22.3", {"start": v(103, -130) * mm, "end": v(103, -140) * mm});
            skLineSegment(sketch, "E33.11.23.0", {"start": v(93, -116) * mm, "end": v(103, -116) * mm});
            skLineSegment(sketch, "E33.11.23.1", {"start": v(93, -126) * mm, "end": v(103, -126) * mm});
            skLineSegment(sketch, "E33.11.23.2", {"start": v(93, -116) * mm, "end": v(93, -126) * mm});
            skLineSegment(sketch, "E33.11.23.3", {"start": v(103, -116) * mm, "end": v(103, -126) * mm});
            skLineSegment(sketch, "E33.11.24.0", {"start": v(93, -102) * mm, "end": v(103, -102) * mm});
            skLineSegment(sketch, "E33.11.24.1", {"start": v(93, -112) * mm, "end": v(103, -112) * mm});
            skLineSegment(sketch, "E33.11.24.2", {"start": v(93, -102) * mm, "end": v(93, -112) * mm});
            skLineSegment(sketch, "E33.11.24.3", {"start": v(103, -102) * mm, "end": v(103, -112) * mm});
            skLineSegment(sketch, "E33.11.25.0", {"start": v(93, -88) * mm, "end": v(103, -88) * mm});
            skLineSegment(sketch, "E33.11.25.1", {"start": v(93, -98) * mm, "end": v(103, -98) * mm});
            skLineSegment(sketch, "E33.11.25.2", {"start": v(93, -88) * mm, "end": v(93, -98) * mm});
            skLineSegment(sketch, "E33.11.25.3", {"start": v(103, -88) * mm, "end": v(103, -98) * mm});
            skLineSegment(sketch, "E33.11.26.0", {"start": v(93, -74) * mm, "end": v(103, -74) * mm});
            skLineSegment(sketch, "E33.11.26.1", {"start": v(93, -84) * mm, "end": v(103, -84) * mm});
            skLineSegment(sketch, "E33.11.26.2", {"start": v(93, -74) * mm, "end": v(93, -84) * mm});
            skLineSegment(sketch, "E33.11.26.3", {"start": v(103, -74) * mm, "end": v(103, -84) * mm});
            skLineSegment(sketch, "E33.11.27.0", {"start": v(93, -60) * mm, "end": v(103, -60) * mm});
            skLineSegment(sketch, "E33.11.27.1", {"start": v(93, -70) * mm, "end": v(103, -70) * mm});
            skLineSegment(sketch, "E33.11.27.2", {"start": v(93, -60) * mm, "end": v(93, -70) * mm});
            skLineSegment(sketch, "E33.11.27.3", {"start": v(103, -60) * mm, "end": v(103, -70) * mm});
            skLineSegment(sketch, "E33.11.28.0", {"start": v(93, -46) * mm, "end": v(103, -46) * mm});
            skLineSegment(sketch, "E33.11.28.1", {"start": v(93, -56) * mm, "end": v(103, -56) * mm});
            skLineSegment(sketch, "E33.11.28.2", {"start": v(93, -46) * mm, "end": v(93, -56) * mm});
            skLineSegment(sketch, "E33.11.28.3", {"start": v(103, -46) * mm, "end": v(103, -56) * mm});
            skLineSegment(sketch, "E33.11.29.0", {"start": v(93, -32) * mm, "end": v(103, -32) * mm});
            skLineSegment(sketch, "E33.11.29.1", {"start": v(93, -42) * mm, "end": v(103, -42) * mm});
            skLineSegment(sketch, "E33.11.29.2", {"start": v(93, -32) * mm, "end": v(93, -42) * mm});
            skLineSegment(sketch, "E33.11.29.3", {"start": v(103, -32) * mm, "end": v(103, -42) * mm});
            skLineSegment(sketch, "E33.11.30.0", {"start": v(93, -18) * mm, "end": v(103, -18) * mm});
            skLineSegment(sketch, "E33.11.30.1", {"start": v(93, -28) * mm, "end": v(103, -28) * mm});
            skLineSegment(sketch, "E33.11.30.2", {"start": v(93, -18) * mm, "end": v(93, -28) * mm});
            skLineSegment(sketch, "E33.11.30.3", {"start": v(103, -18) * mm, "end": v(103, -28) * mm});
            skLineSegment(sketch, "E33.11.31.0", {"start": v(93, -4) * mm, "end": v(103, -4) * mm});
            skLineSegment(sketch, "E33.11.31.1", {"start": v(93, -14) * mm, "end": v(103, -14) * mm});
            skLineSegment(sketch, "E33.11.31.2", {"start": v(93, -4) * mm, "end": v(93, -14) * mm});
            skLineSegment(sketch, "E33.11.31.3", {"start": v(103, -4) * mm, "end": v(103, -14) * mm});
            skLineSegment(sketch, "E33.12.0.0", {"start": v(79, -438) * mm, "end": v(89, -438) * mm});
            skLineSegment(sketch, "E33.12.0.1", {"start": v(79, -448) * mm, "end": v(89, -448) * mm});
            skLineSegment(sketch, "E33.12.0.2", {"start": v(79, -438) * mm, "end": v(79, -448) * mm});
            skLineSegment(sketch, "E33.12.0.3", {"start": v(89, -438) * mm, "end": v(89, -448) * mm});
            skLineSegment(sketch, "E33.12.1.0", {"start": v(79, -424) * mm, "end": v(89, -424) * mm});
            skLineSegment(sketch, "E33.12.1.1", {"start": v(79, -434) * mm, "end": v(89, -434) * mm});
            skLineSegment(sketch, "E33.12.1.2", {"start": v(79, -424) * mm, "end": v(79, -434) * mm});
            skLineSegment(sketch, "E33.12.1.3", {"start": v(89, -424) * mm, "end": v(89, -434) * mm});
            skLineSegment(sketch, "E33.12.2.0", {"start": v(79, -410) * mm, "end": v(89, -410) * mm});
            skLineSegment(sketch, "E33.12.2.1", {"start": v(79, -420) * mm, "end": v(89, -420) * mm});
            skLineSegment(sketch, "E33.12.2.2", {"start": v(79, -410) * mm, "end": v(79, -420) * mm});
            skLineSegment(sketch, "E33.12.2.3", {"start": v(89, -410) * mm, "end": v(89, -420) * mm});
            skLineSegment(sketch, "E33.12.3.0", {"start": v(79, -396) * mm, "end": v(89, -396) * mm});
            skLineSegment(sketch, "E33.12.3.1", {"start": v(79, -406) * mm, "end": v(89, -406) * mm});
            skLineSegment(sketch, "E33.12.3.2", {"start": v(79, -396) * mm, "end": v(79, -406) * mm});
            skLineSegment(sketch, "E33.12.3.3", {"start": v(89, -396) * mm, "end": v(89, -406) * mm});
            skLineSegment(sketch, "E33.12.4.0", {"start": v(79, -382) * mm, "end": v(89, -382) * mm});
            skLineSegment(sketch, "E33.12.4.1", {"start": v(79, -392) * mm, "end": v(89, -392) * mm});
            skLineSegment(sketch, "E33.12.4.2", {"start": v(79, -382) * mm, "end": v(79, -392) * mm});
            skLineSegment(sketch, "E33.12.4.3", {"start": v(89, -382) * mm, "end": v(89, -392) * mm});
            skLineSegment(sketch, "E33.12.5.0", {"start": v(79, -368) * mm, "end": v(89, -368) * mm});
            skLineSegment(sketch, "E33.12.5.1", {"start": v(79, -378) * mm, "end": v(89, -378) * mm});
            skLineSegment(sketch, "E33.12.5.2", {"start": v(79, -368) * mm, "end": v(79, -378) * mm});
            skLineSegment(sketch, "E33.12.5.3", {"start": v(89, -368) * mm, "end": v(89, -378) * mm});
            skLineSegment(sketch, "E33.12.6.0", {"start": v(79, -354) * mm, "end": v(89, -354) * mm});
            skLineSegment(sketch, "E33.12.6.1", {"start": v(79, -364) * mm, "end": v(89, -364) * mm});
            skLineSegment(sketch, "E33.12.6.2", {"start": v(79, -354) * mm, "end": v(79, -364) * mm});
            skLineSegment(sketch, "E33.12.6.3", {"start": v(89, -354) * mm, "end": v(89, -364) * mm});
            skLineSegment(sketch, "E33.12.7.0", {"start": v(79, -340) * mm, "end": v(89, -340) * mm});
            skLineSegment(sketch, "E33.12.7.1", {"start": v(79, -350) * mm, "end": v(89, -350) * mm});
            skLineSegment(sketch, "E33.12.7.2", {"start": v(79, -340) * mm, "end": v(79, -350) * mm});
            skLineSegment(sketch, "E33.12.7.3", {"start": v(89, -340) * mm, "end": v(89, -350) * mm});
            skLineSegment(sketch, "E33.12.8.0", {"start": v(79, -326) * mm, "end": v(89, -326) * mm});
            skLineSegment(sketch, "E33.12.8.1", {"start": v(79, -336) * mm, "end": v(89, -336) * mm});
            skLineSegment(sketch, "E33.12.8.2", {"start": v(79, -326) * mm, "end": v(79, -336) * mm});
            skLineSegment(sketch, "E33.12.8.3", {"start": v(89, -326) * mm, "end": v(89, -336) * mm});
            skLineSegment(sketch, "E33.12.9.0", {"start": v(79, -312) * mm, "end": v(89, -312) * mm});
            skLineSegment(sketch, "E33.12.9.1", {"start": v(79, -322) * mm, "end": v(89, -322) * mm});
            skLineSegment(sketch, "E33.12.9.2", {"start": v(79, -312) * mm, "end": v(79, -322) * mm});
            skLineSegment(sketch, "E33.12.9.3", {"start": v(89, -312) * mm, "end": v(89, -322) * mm});
            skLineSegment(sketch, "E33.12.10.0", {"start": v(79, -298) * mm, "end": v(89, -298) * mm});
            skLineSegment(sketch, "E33.12.10.1", {"start": v(79, -308) * mm, "end": v(89, -308) * mm});
            skLineSegment(sketch, "E33.12.10.2", {"start": v(79, -298) * mm, "end": v(79, -308) * mm});
            skLineSegment(sketch, "E33.12.10.3", {"start": v(89, -298) * mm, "end": v(89, -308) * mm});
            skLineSegment(sketch, "E33.12.11.0", {"start": v(79, -284) * mm, "end": v(89, -284) * mm});
            skLineSegment(sketch, "E33.12.11.1", {"start": v(79, -294) * mm, "end": v(89, -294) * mm});
            skLineSegment(sketch, "E33.12.11.2", {"start": v(79, -284) * mm, "end": v(79, -294) * mm});
            skLineSegment(sketch, "E33.12.11.3", {"start": v(89, -284) * mm, "end": v(89, -294) * mm});
            skLineSegment(sketch, "E33.12.12.0", {"start": v(79, -270) * mm, "end": v(89, -270) * mm});
            skLineSegment(sketch, "E33.12.12.1", {"start": v(79, -280) * mm, "end": v(89, -280) * mm});
            skLineSegment(sketch, "E33.12.12.2", {"start": v(79, -270) * mm, "end": v(79, -280) * mm});
            skLineSegment(sketch, "E33.12.12.3", {"start": v(89, -270) * mm, "end": v(89, -280) * mm});
            skLineSegment(sketch, "E33.12.13.0", {"start": v(79, -256) * mm, "end": v(89, -256) * mm});
            skLineSegment(sketch, "E33.12.13.1", {"start": v(79, -266) * mm, "end": v(89, -266) * mm});
            skLineSegment(sketch, "E33.12.13.2", {"start": v(79, -256) * mm, "end": v(79, -266) * mm});
            skLineSegment(sketch, "E33.12.13.3", {"start": v(89, -256) * mm, "end": v(89, -266) * mm});
            skLineSegment(sketch, "E33.12.14.0", {"start": v(79, -242) * mm, "end": v(89, -242) * mm});
            skLineSegment(sketch, "E33.12.14.1", {"start": v(79, -252) * mm, "end": v(89, -252) * mm});
            skLineSegment(sketch, "E33.12.14.2", {"start": v(79, -242) * mm, "end": v(79, -252) * mm});
            skLineSegment(sketch, "E33.12.14.3", {"start": v(89, -242) * mm, "end": v(89, -252) * mm});
            skLineSegment(sketch, "E33.12.15.0", {"start": v(79, -228) * mm, "end": v(89, -228) * mm});
            skLineSegment(sketch, "E33.12.15.1", {"start": v(79, -238) * mm, "end": v(89, -238) * mm});
            skLineSegment(sketch, "E33.12.15.2", {"start": v(79, -228) * mm, "end": v(79, -238) * mm});
            skLineSegment(sketch, "E33.12.15.3", {"start": v(89, -228) * mm, "end": v(89, -238) * mm});
            skLineSegment(sketch, "E33.12.16.0", {"start": v(79, -214) * mm, "end": v(89, -214) * mm});
            skLineSegment(sketch, "E33.12.16.1", {"start": v(79, -224) * mm, "end": v(89, -224) * mm});
            skLineSegment(sketch, "E33.12.16.2", {"start": v(79, -214) * mm, "end": v(79, -224) * mm});
            skLineSegment(sketch, "E33.12.16.3", {"start": v(89, -214) * mm, "end": v(89, -224) * mm});
            skLineSegment(sketch, "E33.12.17.0", {"start": v(79, -200) * mm, "end": v(89, -200) * mm});
            skLineSegment(sketch, "E33.12.17.1", {"start": v(79, -210) * mm, "end": v(89, -210) * mm});
            skLineSegment(sketch, "E33.12.17.2", {"start": v(79, -200) * mm, "end": v(79, -210) * mm});
            skLineSegment(sketch, "E33.12.17.3", {"start": v(89, -200) * mm, "end": v(89, -210) * mm});
            skLineSegment(sketch, "E33.12.18.0", {"start": v(79, -186) * mm, "end": v(89, -186) * mm});
            skLineSegment(sketch, "E33.12.18.1", {"start": v(79, -196) * mm, "end": v(89, -196) * mm});
            skLineSegment(sketch, "E33.12.18.2", {"start": v(79, -186) * mm, "end": v(79, -196) * mm});
            skLineSegment(sketch, "E33.12.18.3", {"start": v(89, -186) * mm, "end": v(89, -196) * mm});
            skLineSegment(sketch, "E33.12.19.0", {"start": v(79, -172) * mm, "end": v(89, -172) * mm});
            skLineSegment(sketch, "E33.12.19.1", {"start": v(79, -182) * mm, "end": v(89, -182) * mm});
            skLineSegment(sketch, "E33.12.19.2", {"start": v(79, -172) * mm, "end": v(79, -182) * mm});
            skLineSegment(sketch, "E33.12.19.3", {"start": v(89, -172) * mm, "end": v(89, -182) * mm});
            skLineSegment(sketch, "E33.12.20.0", {"start": v(79, -158) * mm, "end": v(89, -158) * mm});
            skLineSegment(sketch, "E33.12.20.1", {"start": v(79, -168) * mm, "end": v(89, -168) * mm});
            skLineSegment(sketch, "E33.12.20.2", {"start": v(79, -158) * mm, "end": v(79, -168) * mm});
            skLineSegment(sketch, "E33.12.20.3", {"start": v(89, -158) * mm, "end": v(89, -168) * mm});
            skLineSegment(sketch, "E33.12.21.0", {"start": v(79, -144) * mm, "end": v(89, -144) * mm});
            skLineSegment(sketch, "E33.12.21.1", {"start": v(79, -154) * mm, "end": v(89, -154) * mm});
            skLineSegment(sketch, "E33.12.21.2", {"start": v(79, -144) * mm, "end": v(79, -154) * mm});
            skLineSegment(sketch, "E33.12.21.3", {"start": v(89, -144) * mm, "end": v(89, -154) * mm});
            skLineSegment(sketch, "E33.12.22.0", {"start": v(79, -130) * mm, "end": v(89, -130) * mm});
            skLineSegment(sketch, "E33.12.22.1", {"start": v(79, -140) * mm, "end": v(89, -140) * mm});
            skLineSegment(sketch, "E33.12.22.2", {"start": v(79, -130) * mm, "end": v(79, -140) * mm});
            skLineSegment(sketch, "E33.12.22.3", {"start": v(89, -130) * mm, "end": v(89, -140) * mm});
            skLineSegment(sketch, "E33.12.23.0", {"start": v(79, -116) * mm, "end": v(89, -116) * mm});
            skLineSegment(sketch, "E33.12.23.1", {"start": v(79, -126) * mm, "end": v(89, -126) * mm});
            skLineSegment(sketch, "E33.12.23.2", {"start": v(79, -116) * mm, "end": v(79, -126) * mm});
            skLineSegment(sketch, "E33.12.23.3", {"start": v(89, -116) * mm, "end": v(89, -126) * mm});
            skLineSegment(sketch, "E33.12.24.0", {"start": v(79, -102) * mm, "end": v(89, -102) * mm});
            skLineSegment(sketch, "E33.12.24.1", {"start": v(79, -112) * mm, "end": v(89, -112) * mm});
            skLineSegment(sketch, "E33.12.24.2", {"start": v(79, -102) * mm, "end": v(79, -112) * mm});
            skLineSegment(sketch, "E33.12.24.3", {"start": v(89, -102) * mm, "end": v(89, -112) * mm});
            skLineSegment(sketch, "E33.12.25.0", {"start": v(79, -88) * mm, "end": v(89, -88) * mm});
            skLineSegment(sketch, "E33.12.25.1", {"start": v(79, -98) * mm, "end": v(89, -98) * mm});
            skLineSegment(sketch, "E33.12.25.2", {"start": v(79, -88) * mm, "end": v(79, -98) * mm});
            skLineSegment(sketch, "E33.12.25.3", {"start": v(89, -88) * mm, "end": v(89, -98) * mm});
            skLineSegment(sketch, "E33.12.26.0", {"start": v(79, -74) * mm, "end": v(89, -74) * mm});
            skLineSegment(sketch, "E33.12.26.1", {"start": v(79, -84) * mm, "end": v(89, -84) * mm});
            skLineSegment(sketch, "E33.12.26.2", {"start": v(79, -74) * mm, "end": v(79, -84) * mm});
            skLineSegment(sketch, "E33.12.26.3", {"start": v(89, -74) * mm, "end": v(89, -84) * mm});
            skLineSegment(sketch, "E33.12.27.0", {"start": v(79, -60) * mm, "end": v(89, -60) * mm});
            skLineSegment(sketch, "E33.12.27.1", {"start": v(79, -70) * mm, "end": v(89, -70) * mm});
            skLineSegment(sketch, "E33.12.27.2", {"start": v(79, -60) * mm, "end": v(79, -70) * mm});
            skLineSegment(sketch, "E33.12.27.3", {"start": v(89, -60) * mm, "end": v(89, -70) * mm});
            skLineSegment(sketch, "E33.12.28.0", {"start": v(79, -46) * mm, "end": v(89, -46) * mm});
            skLineSegment(sketch, "E33.12.28.1", {"start": v(79, -56) * mm, "end": v(89, -56) * mm});
            skLineSegment(sketch, "E33.12.28.2", {"start": v(79, -46) * mm, "end": v(79, -56) * mm});
            skLineSegment(sketch, "E33.12.28.3", {"start": v(89, -46) * mm, "end": v(89, -56) * mm});
            skLineSegment(sketch, "E33.12.29.0", {"start": v(79, -32) * mm, "end": v(89, -32) * mm});
            skLineSegment(sketch, "E33.12.29.1", {"start": v(79, -42) * mm, "end": v(89, -42) * mm});
            skLineSegment(sketch, "E33.12.29.2", {"start": v(79, -32) * mm, "end": v(79, -42) * mm});
            skLineSegment(sketch, "E33.12.29.3", {"start": v(89, -32) * mm, "end": v(89, -42) * mm});
            skLineSegment(sketch, "E33.12.30.0", {"start": v(79, -18) * mm, "end": v(89, -18) * mm});
            skLineSegment(sketch, "E33.12.30.1", {"start": v(79, -28) * mm, "end": v(89, -28) * mm});
            skLineSegment(sketch, "E33.12.30.2", {"start": v(79, -18) * mm, "end": v(79, -28) * mm});
            skLineSegment(sketch, "E33.12.30.3", {"start": v(89, -18) * mm, "end": v(89, -28) * mm});
            skLineSegment(sketch, "E33.12.31.0", {"start": v(79, -4) * mm, "end": v(89, -4) * mm});
            skLineSegment(sketch, "E33.12.31.1", {"start": v(79, -14) * mm, "end": v(89, -14) * mm});
            skLineSegment(sketch, "E33.12.31.2", {"start": v(79, -4) * mm, "end": v(79, -14) * mm});
            skLineSegment(sketch, "E33.12.31.3", {"start": v(89, -4) * mm, "end": v(89, -14) * mm});
            skLineSegment(sketch, "E33.13.0.0", {"start": v(65, -438) * mm, "end": v(75, -438) * mm});
            skLineSegment(sketch, "E33.13.0.1", {"start": v(65, -448) * mm, "end": v(75, -448) * mm});
            skLineSegment(sketch, "E33.13.0.2", {"start": v(65, -438) * mm, "end": v(65, -448) * mm});
            skLineSegment(sketch, "E33.13.0.3", {"start": v(75, -438) * mm, "end": v(75, -448) * mm});
            skLineSegment(sketch, "E33.13.1.0", {"start": v(65, -424) * mm, "end": v(75, -424) * mm});
            skLineSegment(sketch, "E33.13.1.1", {"start": v(65, -434) * mm, "end": v(75, -434) * mm});
            skLineSegment(sketch, "E33.13.1.2", {"start": v(65, -424) * mm, "end": v(65, -434) * mm});
            skLineSegment(sketch, "E33.13.1.3", {"start": v(75, -424) * mm, "end": v(75, -434) * mm});
            skLineSegment(sketch, "E33.13.2.0", {"start": v(65, -410) * mm, "end": v(75, -410) * mm});
            skLineSegment(sketch, "E33.13.2.1", {"start": v(65, -420) * mm, "end": v(75, -420) * mm});
            skLineSegment(sketch, "E33.13.2.2", {"start": v(65, -410) * mm, "end": v(65, -420) * mm});
            skLineSegment(sketch, "E33.13.2.3", {"start": v(75, -410) * mm, "end": v(75, -420) * mm});
            skLineSegment(sketch, "E33.13.3.0", {"start": v(65, -396) * mm, "end": v(75, -396) * mm});
            skLineSegment(sketch, "E33.13.3.1", {"start": v(65, -406) * mm, "end": v(75, -406) * mm});
            skLineSegment(sketch, "E33.13.3.2", {"start": v(65, -396) * mm, "end": v(65, -406) * mm});
            skLineSegment(sketch, "E33.13.3.3", {"start": v(75, -396) * mm, "end": v(75, -406) * mm});
            skLineSegment(sketch, "E33.13.4.0", {"start": v(65, -382) * mm, "end": v(75, -382) * mm});
            skLineSegment(sketch, "E33.13.4.1", {"start": v(65, -392) * mm, "end": v(75, -392) * mm});
            skLineSegment(sketch, "E33.13.4.2", {"start": v(65, -382) * mm, "end": v(65, -392) * mm});
            skLineSegment(sketch, "E33.13.4.3", {"start": v(75, -382) * mm, "end": v(75, -392) * mm});
            skLineSegment(sketch, "E33.13.5.0", {"start": v(65, -368) * mm, "end": v(75, -368) * mm});
            skLineSegment(sketch, "E33.13.5.1", {"start": v(65, -378) * mm, "end": v(75, -378) * mm});
            skLineSegment(sketch, "E33.13.5.2", {"start": v(65, -368) * mm, "end": v(65, -378) * mm});
            skLineSegment(sketch, "E33.13.5.3", {"start": v(75, -368) * mm, "end": v(75, -378) * mm});
            skLineSegment(sketch, "E33.13.6.0", {"start": v(65, -354) * mm, "end": v(75, -354) * mm});
            skLineSegment(sketch, "E33.13.6.1", {"start": v(65, -364) * mm, "end": v(75, -364) * mm});
            skLineSegment(sketch, "E33.13.6.2", {"start": v(65, -354) * mm, "end": v(65, -364) * mm});
            skLineSegment(sketch, "E33.13.6.3", {"start": v(75, -354) * mm, "end": v(75, -364) * mm});
            skLineSegment(sketch, "E33.13.7.0", {"start": v(65, -340) * mm, "end": v(75, -340) * mm});
            skLineSegment(sketch, "E33.13.7.1", {"start": v(65, -350) * mm, "end": v(75, -350) * mm});
            skLineSegment(sketch, "E33.13.7.2", {"start": v(65, -340) * mm, "end": v(65, -350) * mm});
            skLineSegment(sketch, "E33.13.7.3", {"start": v(75, -340) * mm, "end": v(75, -350) * mm});
            skLineSegment(sketch, "E33.13.8.0", {"start": v(65, -326) * mm, "end": v(75, -326) * mm});
            skLineSegment(sketch, "E33.13.8.1", {"start": v(65, -336) * mm, "end": v(75, -336) * mm});
            skLineSegment(sketch, "E33.13.8.2", {"start": v(65, -326) * mm, "end": v(65, -336) * mm});
            skLineSegment(sketch, "E33.13.8.3", {"start": v(75, -326) * mm, "end": v(75, -336) * mm});
            skLineSegment(sketch, "E33.13.9.0", {"start": v(65, -312) * mm, "end": v(75, -312) * mm});
            skLineSegment(sketch, "E33.13.9.1", {"start": v(65, -322) * mm, "end": v(75, -322) * mm});
            skLineSegment(sketch, "E33.13.9.2", {"start": v(65, -312) * mm, "end": v(65, -322) * mm});
            skLineSegment(sketch, "E33.13.9.3", {"start": v(75, -312) * mm, "end": v(75, -322) * mm});
            skLineSegment(sketch, "E33.13.10.0", {"start": v(65, -298) * mm, "end": v(75, -298) * mm});
            skLineSegment(sketch, "E33.13.10.1", {"start": v(65, -308) * mm, "end": v(75, -308) * mm});
            skLineSegment(sketch, "E33.13.10.2", {"start": v(65, -298) * mm, "end": v(65, -308) * mm});
            skLineSegment(sketch, "E33.13.10.3", {"start": v(75, -298) * mm, "end": v(75, -308) * mm});
            skLineSegment(sketch, "E33.13.11.0", {"start": v(65, -284) * mm, "end": v(75, -284) * mm});
            skLineSegment(sketch, "E33.13.11.1", {"start": v(65, -294) * mm, "end": v(75, -294) * mm});
            skLineSegment(sketch, "E33.13.11.2", {"start": v(65, -284) * mm, "end": v(65, -294) * mm});
            skLineSegment(sketch, "E33.13.11.3", {"start": v(75, -284) * mm, "end": v(75, -294) * mm});
            skLineSegment(sketch, "E33.13.12.0", {"start": v(65, -270) * mm, "end": v(75, -270) * mm});
            skLineSegment(sketch, "E33.13.12.1", {"start": v(65, -280) * mm, "end": v(75, -280) * mm});
            skLineSegment(sketch, "E33.13.12.2", {"start": v(65, -270) * mm, "end": v(65, -280) * mm});
            skLineSegment(sketch, "E33.13.12.3", {"start": v(75, -270) * mm, "end": v(75, -280) * mm});
            skLineSegment(sketch, "E33.13.13.0", {"start": v(65, -256) * mm, "end": v(75, -256) * mm});
            skLineSegment(sketch, "E33.13.13.1", {"start": v(65, -266) * mm, "end": v(75, -266) * mm});
            skLineSegment(sketch, "E33.13.13.2", {"start": v(65, -256) * mm, "end": v(65, -266) * mm});
            skLineSegment(sketch, "E33.13.13.3", {"start": v(75, -256) * mm, "end": v(75, -266) * mm});
            skLineSegment(sketch, "E33.13.14.0", {"start": v(65, -242) * mm, "end": v(75, -242) * mm});
            skLineSegment(sketch, "E33.13.14.1", {"start": v(65, -252) * mm, "end": v(75, -252) * mm});
            skLineSegment(sketch, "E33.13.14.2", {"start": v(65, -242) * mm, "end": v(65, -252) * mm});
            skLineSegment(sketch, "E33.13.14.3", {"start": v(75, -242) * mm, "end": v(75, -252) * mm});
            skLineSegment(sketch, "E33.13.15.0", {"start": v(65, -228) * mm, "end": v(75, -228) * mm});
            skLineSegment(sketch, "E33.13.15.1", {"start": v(65, -238) * mm, "end": v(75, -238) * mm});
            skLineSegment(sketch, "E33.13.15.2", {"start": v(65, -228) * mm, "end": v(65, -238) * mm});
            skLineSegment(sketch, "E33.13.15.3", {"start": v(75, -228) * mm, "end": v(75, -238) * mm});
            skLineSegment(sketch, "E33.13.16.0", {"start": v(65, -214) * mm, "end": v(75, -214) * mm});
            skLineSegment(sketch, "E33.13.16.1", {"start": v(65, -224) * mm, "end": v(75, -224) * mm});
            skLineSegment(sketch, "E33.13.16.2", {"start": v(65, -214) * mm, "end": v(65, -224) * mm});
            skLineSegment(sketch, "E33.13.16.3", {"start": v(75, -214) * mm, "end": v(75, -224) * mm});
            skLineSegment(sketch, "E33.13.17.0", {"start": v(65, -200) * mm, "end": v(75, -200) * mm});
            skLineSegment(sketch, "E33.13.17.1", {"start": v(65, -210) * mm, "end": v(75, -210) * mm});
            skLineSegment(sketch, "E33.13.17.2", {"start": v(65, -200) * mm, "end": v(65, -210) * mm});
            skLineSegment(sketch, "E33.13.17.3", {"start": v(75, -200) * mm, "end": v(75, -210) * mm});
            skLineSegment(sketch, "E33.13.18.0", {"start": v(65, -186) * mm, "end": v(75, -186) * mm});
            skLineSegment(sketch, "E33.13.18.1", {"start": v(65, -196) * mm, "end": v(75, -196) * mm});
            skLineSegment(sketch, "E33.13.18.2", {"start": v(65, -186) * mm, "end": v(65, -196) * mm});
            skLineSegment(sketch, "E33.13.18.3", {"start": v(75, -186) * mm, "end": v(75, -196) * mm});
            skLineSegment(sketch, "E33.13.19.0", {"start": v(65, -172) * mm, "end": v(75, -172) * mm});
            skLineSegment(sketch, "E33.13.19.1", {"start": v(65, -182) * mm, "end": v(75, -182) * mm});
            skLineSegment(sketch, "E33.13.19.2", {"start": v(65, -172) * mm, "end": v(65, -182) * mm});
            skLineSegment(sketch, "E33.13.19.3", {"start": v(75, -172) * mm, "end": v(75, -182) * mm});
            skLineSegment(sketch, "E33.13.20.0", {"start": v(65, -158) * mm, "end": v(75, -158) * mm});
            skLineSegment(sketch, "E33.13.20.1", {"start": v(65, -168) * mm, "end": v(75, -168) * mm});
            skLineSegment(sketch, "E33.13.20.2", {"start": v(65, -158) * mm, "end": v(65, -168) * mm});
            skLineSegment(sketch, "E33.13.20.3", {"start": v(75, -158) * mm, "end": v(75, -168) * mm});
            skLineSegment(sketch, "E33.13.21.0", {"start": v(65, -144) * mm, "end": v(75, -144) * mm});
            skLineSegment(sketch, "E33.13.21.1", {"start": v(65, -154) * mm, "end": v(75, -154) * mm});
            skLineSegment(sketch, "E33.13.21.2", {"start": v(65, -144) * mm, "end": v(65, -154) * mm});
            skLineSegment(sketch, "E33.13.21.3", {"start": v(75, -144) * mm, "end": v(75, -154) * mm});
            skLineSegment(sketch, "E33.13.22.0", {"start": v(65, -130) * mm, "end": v(75, -130) * mm});
            skLineSegment(sketch, "E33.13.22.1", {"start": v(65, -140) * mm, "end": v(75, -140) * mm});
            skLineSegment(sketch, "E33.13.22.2", {"start": v(65, -130) * mm, "end": v(65, -140) * mm});
            skLineSegment(sketch, "E33.13.22.3", {"start": v(75, -130) * mm, "end": v(75, -140) * mm});
            skLineSegment(sketch, "E33.13.23.0", {"start": v(65, -116) * mm, "end": v(75, -116) * mm});
            skLineSegment(sketch, "E33.13.23.1", {"start": v(65, -126) * mm, "end": v(75, -126) * mm});
            skLineSegment(sketch, "E33.13.23.2", {"start": v(65, -116) * mm, "end": v(65, -126) * mm});
            skLineSegment(sketch, "E33.13.23.3", {"start": v(75, -116) * mm, "end": v(75, -126) * mm});
            skLineSegment(sketch, "E33.13.24.0", {"start": v(65, -102) * mm, "end": v(75, -102) * mm});
            skLineSegment(sketch, "E33.13.24.1", {"start": v(65, -112) * mm, "end": v(75, -112) * mm});
            skLineSegment(sketch, "E33.13.24.2", {"start": v(65, -102) * mm, "end": v(65, -112) * mm});
            skLineSegment(sketch, "E33.13.24.3", {"start": v(75, -102) * mm, "end": v(75, -112) * mm});
            skLineSegment(sketch, "E33.13.25.0", {"start": v(65, -88) * mm, "end": v(75, -88) * mm});
            skLineSegment(sketch, "E33.13.25.1", {"start": v(65, -98) * mm, "end": v(75, -98) * mm});
            skLineSegment(sketch, "E33.13.25.2", {"start": v(65, -88) * mm, "end": v(65, -98) * mm});
            skLineSegment(sketch, "E33.13.25.3", {"start": v(75, -88) * mm, "end": v(75, -98) * mm});
            skLineSegment(sketch, "E33.13.26.0", {"start": v(65, -74) * mm, "end": v(75, -74) * mm});
            skLineSegment(sketch, "E33.13.26.1", {"start": v(65, -84) * mm, "end": v(75, -84) * mm});
            skLineSegment(sketch, "E33.13.26.2", {"start": v(65, -74) * mm, "end": v(65, -84) * mm});
            skLineSegment(sketch, "E33.13.26.3", {"start": v(75, -74) * mm, "end": v(75, -84) * mm});
            skLineSegment(sketch, "E33.13.27.0", {"start": v(65, -60) * mm, "end": v(75, -60) * mm});
            skLineSegment(sketch, "E33.13.27.1", {"start": v(65, -70) * mm, "end": v(75, -70) * mm});
            skLineSegment(sketch, "E33.13.27.2", {"start": v(65, -60) * mm, "end": v(65, -70) * mm});
            skLineSegment(sketch, "E33.13.27.3", {"start": v(75, -60) * mm, "end": v(75, -70) * mm});
            skLineSegment(sketch, "E33.13.28.0", {"start": v(65, -46) * mm, "end": v(75, -46) * mm});
            skLineSegment(sketch, "E33.13.28.1", {"start": v(65, -56) * mm, "end": v(75, -56) * mm});
            skLineSegment(sketch, "E33.13.28.2", {"start": v(65, -46) * mm, "end": v(65, -56) * mm});
            skLineSegment(sketch, "E33.13.28.3", {"start": v(75, -46) * mm, "end": v(75, -56) * mm});
            skLineSegment(sketch, "E33.13.29.0", {"start": v(65, -32) * mm, "end": v(75, -32) * mm});
            skLineSegment(sketch, "E33.13.29.1", {"start": v(65, -42) * mm, "end": v(75, -42) * mm});
            skLineSegment(sketch, "E33.13.29.2", {"start": v(65, -32) * mm, "end": v(65, -42) * mm});
            skLineSegment(sketch, "E33.13.29.3", {"start": v(75, -32) * mm, "end": v(75, -42) * mm});
            skLineSegment(sketch, "E33.13.30.0", {"start": v(65, -18) * mm, "end": v(75, -18) * mm});
            skLineSegment(sketch, "E33.13.30.1", {"start": v(65, -28) * mm, "end": v(75, -28) * mm});
            skLineSegment(sketch, "E33.13.30.2", {"start": v(65, -18) * mm, "end": v(65, -28) * mm});
            skLineSegment(sketch, "E33.13.30.3", {"start": v(75, -18) * mm, "end": v(75, -28) * mm});
            skLineSegment(sketch, "E33.13.31.0", {"start": v(65, -4) * mm, "end": v(75, -4) * mm});
            skLineSegment(sketch, "E33.13.31.1", {"start": v(65, -14) * mm, "end": v(75, -14) * mm});
            skLineSegment(sketch, "E33.13.31.2", {"start": v(65, -4) * mm, "end": v(65, -14) * mm});
            skLineSegment(sketch, "E33.13.31.3", {"start": v(75, -4) * mm, "end": v(75, -14) * mm});
            skLineSegment(sketch, "E33.14.0.0", {"start": v(51, -438) * mm, "end": v(61, -438) * mm});
            skLineSegment(sketch, "E33.14.0.1", {"start": v(51, -448) * mm, "end": v(61, -448) * mm});
            skLineSegment(sketch, "E33.14.0.2", {"start": v(51, -438) * mm, "end": v(51, -448) * mm});
            skLineSegment(sketch, "E33.14.0.3", {"start": v(61, -438) * mm, "end": v(61, -448) * mm});
            skLineSegment(sketch, "E33.14.1.0", {"start": v(51, -424) * mm, "end": v(61, -424) * mm});
            skLineSegment(sketch, "E33.14.1.1", {"start": v(51, -434) * mm, "end": v(61, -434) * mm});
            skLineSegment(sketch, "E33.14.1.2", {"start": v(51, -424) * mm, "end": v(51, -434) * mm});
            skLineSegment(sketch, "E33.14.1.3", {"start": v(61, -424) * mm, "end": v(61, -434) * mm});
            skLineSegment(sketch, "E33.14.2.0", {"start": v(51, -410) * mm, "end": v(61, -410) * mm});
            skLineSegment(sketch, "E33.14.2.1", {"start": v(51, -420) * mm, "end": v(61, -420) * mm});
            skLineSegment(sketch, "E33.14.2.2", {"start": v(51, -410) * mm, "end": v(51, -420) * mm});
            skLineSegment(sketch, "E33.14.2.3", {"start": v(61, -410) * mm, "end": v(61, -420) * mm});
            skLineSegment(sketch, "E33.14.3.0", {"start": v(51, -396) * mm, "end": v(61, -396) * mm});
            skLineSegment(sketch, "E33.14.3.1", {"start": v(51, -406) * mm, "end": v(61, -406) * mm});
            skLineSegment(sketch, "E33.14.3.2", {"start": v(51, -396) * mm, "end": v(51, -406) * mm});
            skLineSegment(sketch, "E33.14.3.3", {"start": v(61, -396) * mm, "end": v(61, -406) * mm});
            skLineSegment(sketch, "E33.14.4.0", {"start": v(51, -382) * mm, "end": v(61, -382) * mm});
            skLineSegment(sketch, "E33.14.4.1", {"start": v(51, -392) * mm, "end": v(61, -392) * mm});
            skLineSegment(sketch, "E33.14.4.2", {"start": v(51, -382) * mm, "end": v(51, -392) * mm});
            skLineSegment(sketch, "E33.14.4.3", {"start": v(61, -382) * mm, "end": v(61, -392) * mm});
            skLineSegment(sketch, "E33.14.5.0", {"start": v(51, -368) * mm, "end": v(61, -368) * mm});
            skLineSegment(sketch, "E33.14.5.1", {"start": v(51, -378) * mm, "end": v(61, -378) * mm});
            skLineSegment(sketch, "E33.14.5.2", {"start": v(51, -368) * mm, "end": v(51, -378) * mm});
            skLineSegment(sketch, "E33.14.5.3", {"start": v(61, -368) * mm, "end": v(61, -378) * mm});
            skLineSegment(sketch, "E33.14.6.0", {"start": v(51, -354) * mm, "end": v(61, -354) * mm});
            skLineSegment(sketch, "E33.14.6.1", {"start": v(51, -364) * mm, "end": v(61, -364) * mm});
            skLineSegment(sketch, "E33.14.6.2", {"start": v(51, -354) * mm, "end": v(51, -364) * mm});
            skLineSegment(sketch, "E33.14.6.3", {"start": v(61, -354) * mm, "end": v(61, -364) * mm});
            skLineSegment(sketch, "E33.14.7.0", {"start": v(51, -340) * mm, "end": v(61, -340) * mm});
            skLineSegment(sketch, "E33.14.7.1", {"start": v(51, -350) * mm, "end": v(61, -350) * mm});
            skLineSegment(sketch, "E33.14.7.2", {"start": v(51, -340) * mm, "end": v(51, -350) * mm});
            skLineSegment(sketch, "E33.14.7.3", {"start": v(61, -340) * mm, "end": v(61, -350) * mm});
            skLineSegment(sketch, "E33.14.8.0", {"start": v(51, -326) * mm, "end": v(61, -326) * mm});
            skLineSegment(sketch, "E33.14.8.1", {"start": v(51, -336) * mm, "end": v(61, -336) * mm});
            skLineSegment(sketch, "E33.14.8.2", {"start": v(51, -326) * mm, "end": v(51, -336) * mm});
            skLineSegment(sketch, "E33.14.8.3", {"start": v(61, -326) * mm, "end": v(61, -336) * mm});
            skLineSegment(sketch, "E33.14.9.0", {"start": v(51, -312) * mm, "end": v(61, -312) * mm});
            skLineSegment(sketch, "E33.14.9.1", {"start": v(51, -322) * mm, "end": v(61, -322) * mm});
            skLineSegment(sketch, "E33.14.9.2", {"start": v(51, -312) * mm, "end": v(51, -322) * mm});
            skLineSegment(sketch, "E33.14.9.3", {"start": v(61, -312) * mm, "end": v(61, -322) * mm});
            skLineSegment(sketch, "E33.14.10.0", {"start": v(51, -298) * mm, "end": v(61, -298) * mm});
            skLineSegment(sketch, "E33.14.10.1", {"start": v(51, -308) * mm, "end": v(61, -308) * mm});
            skLineSegment(sketch, "E33.14.10.2", {"start": v(51, -298) * mm, "end": v(51, -308) * mm});
            skLineSegment(sketch, "E33.14.10.3", {"start": v(61, -298) * mm, "end": v(61, -308) * mm});
            skLineSegment(sketch, "E33.14.11.0", {"start": v(51, -284) * mm, "end": v(61, -284) * mm});
            skLineSegment(sketch, "E33.14.11.1", {"start": v(51, -294) * mm, "end": v(61, -294) * mm});
            skLineSegment(sketch, "E33.14.11.2", {"start": v(51, -284) * mm, "end": v(51, -294) * mm});
            skLineSegment(sketch, "E33.14.11.3", {"start": v(61, -284) * mm, "end": v(61, -294) * mm});
            skLineSegment(sketch, "E33.14.12.0", {"start": v(51, -270) * mm, "end": v(61, -270) * mm});
            skLineSegment(sketch, "E33.14.12.1", {"start": v(51, -280) * mm, "end": v(61, -280) * mm});
            skLineSegment(sketch, "E33.14.12.2", {"start": v(51, -270) * mm, "end": v(51, -280) * mm});
            skLineSegment(sketch, "E33.14.12.3", {"start": v(61, -270) * mm, "end": v(61, -280) * mm});
            skLineSegment(sketch, "E33.14.13.0", {"start": v(51, -256) * mm, "end": v(61, -256) * mm});
            skLineSegment(sketch, "E33.14.13.1", {"start": v(51, -266) * mm, "end": v(61, -266) * mm});
            skLineSegment(sketch, "E33.14.13.2", {"start": v(51, -256) * mm, "end": v(51, -266) * mm});
            skLineSegment(sketch, "E33.14.13.3", {"start": v(61, -256) * mm, "end": v(61, -266) * mm});
            skLineSegment(sketch, "E33.14.14.0", {"start": v(51, -242) * mm, "end": v(61, -242) * mm});
            skLineSegment(sketch, "E33.14.14.1", {"start": v(51, -252) * mm, "end": v(61, -252) * mm});
            skLineSegment(sketch, "E33.14.14.2", {"start": v(51, -242) * mm, "end": v(51, -252) * mm});
            skLineSegment(sketch, "E33.14.14.3", {"start": v(61, -242) * mm, "end": v(61, -252) * mm});
            skLineSegment(sketch, "E33.14.15.0", {"start": v(51, -228) * mm, "end": v(61, -228) * mm});
            skLineSegment(sketch, "E33.14.15.1", {"start": v(51, -238) * mm, "end": v(61, -238) * mm});
            skLineSegment(sketch, "E33.14.15.2", {"start": v(51, -228) * mm, "end": v(51, -238) * mm});
            skLineSegment(sketch, "E33.14.15.3", {"start": v(61, -228) * mm, "end": v(61, -238) * mm});
            skLineSegment(sketch, "E33.14.16.0", {"start": v(51, -214) * mm, "end": v(61, -214) * mm});
            skLineSegment(sketch, "E33.14.16.1", {"start": v(51, -224) * mm, "end": v(61, -224) * mm});
            skLineSegment(sketch, "E33.14.16.2", {"start": v(51, -214) * mm, "end": v(51, -224) * mm});
            skLineSegment(sketch, "E33.14.16.3", {"start": v(61, -214) * mm, "end": v(61, -224) * mm});
            skLineSegment(sketch, "E33.14.17.0", {"start": v(51, -200) * mm, "end": v(61, -200) * mm});
            skLineSegment(sketch, "E33.14.17.1", {"start": v(51, -210) * mm, "end": v(61, -210) * mm});
            skLineSegment(sketch, "E33.14.17.2", {"start": v(51, -200) * mm, "end": v(51, -210) * mm});
            skLineSegment(sketch, "E33.14.17.3", {"start": v(61, -200) * mm, "end": v(61, -210) * mm});
            skLineSegment(sketch, "E33.14.18.0", {"start": v(51, -186) * mm, "end": v(61, -186) * mm});
            skLineSegment(sketch, "E33.14.18.1", {"start": v(51, -196) * mm, "end": v(61, -196) * mm});
            skLineSegment(sketch, "E33.14.18.2", {"start": v(51, -186) * mm, "end": v(51, -196) * mm});
            skLineSegment(sketch, "E33.14.18.3", {"start": v(61, -186) * mm, "end": v(61, -196) * mm});
            skLineSegment(sketch, "E33.14.19.0", {"start": v(51, -172) * mm, "end": v(61, -172) * mm});
            skLineSegment(sketch, "E33.14.19.1", {"start": v(51, -182) * mm, "end": v(61, -182) * mm});
            skLineSegment(sketch, "E33.14.19.2", {"start": v(51, -172) * mm, "end": v(51, -182) * mm});
            skLineSegment(sketch, "E33.14.19.3", {"start": v(61, -172) * mm, "end": v(61, -182) * mm});
            skLineSegment(sketch, "E33.14.20.0", {"start": v(51, -158) * mm, "end": v(61, -158) * mm});
            skLineSegment(sketch, "E33.14.20.1", {"start": v(51, -168) * mm, "end": v(61, -168) * mm});
            skLineSegment(sketch, "E33.14.20.2", {"start": v(51, -158) * mm, "end": v(51, -168) * mm});
            skLineSegment(sketch, "E33.14.20.3", {"start": v(61, -158) * mm, "end": v(61, -168) * mm});
            skLineSegment(sketch, "E33.14.21.0", {"start": v(51, -144) * mm, "end": v(61, -144) * mm});
            skLineSegment(sketch, "E33.14.21.1", {"start": v(51, -154) * mm, "end": v(61, -154) * mm});
            skLineSegment(sketch, "E33.14.21.2", {"start": v(51, -144) * mm, "end": v(51, -154) * mm});
            skLineSegment(sketch, "E33.14.21.3", {"start": v(61, -144) * mm, "end": v(61, -154) * mm});
            skLineSegment(sketch, "E33.14.22.0", {"start": v(51, -130) * mm, "end": v(61, -130) * mm});
            skLineSegment(sketch, "E33.14.22.1", {"start": v(51, -140) * mm, "end": v(61, -140) * mm});
            skLineSegment(sketch, "E33.14.22.2", {"start": v(51, -130) * mm, "end": v(51, -140) * mm});
            skLineSegment(sketch, "E33.14.22.3", {"start": v(61, -130) * mm, "end": v(61, -140) * mm});
            skLineSegment(sketch, "E33.14.23.0", {"start": v(51, -116) * mm, "end": v(61, -116) * mm});
            skLineSegment(sketch, "E33.14.23.1", {"start": v(51, -126) * mm, "end": v(61, -126) * mm});
            skLineSegment(sketch, "E33.14.23.2", {"start": v(51, -116) * mm, "end": v(51, -126) * mm});
            skLineSegment(sketch, "E33.14.23.3", {"start": v(61, -116) * mm, "end": v(61, -126) * mm});
            skLineSegment(sketch, "E33.14.24.0", {"start": v(51, -102) * mm, "end": v(61, -102) * mm});
            skLineSegment(sketch, "E33.14.24.1", {"start": v(51, -112) * mm, "end": v(61, -112) * mm});
            skLineSegment(sketch, "E33.14.24.2", {"start": v(51, -102) * mm, "end": v(51, -112) * mm});
            skLineSegment(sketch, "E33.14.24.3", {"start": v(61, -102) * mm, "end": v(61, -112) * mm});
            skLineSegment(sketch, "E33.14.25.0", {"start": v(51, -88) * mm, "end": v(61, -88) * mm});
            skLineSegment(sketch, "E33.14.25.1", {"start": v(51, -98) * mm, "end": v(61, -98) * mm});
            skLineSegment(sketch, "E33.14.25.2", {"start": v(51, -88) * mm, "end": v(51, -98) * mm});
            skLineSegment(sketch, "E33.14.25.3", {"start": v(61, -88) * mm, "end": v(61, -98) * mm});
            skLineSegment(sketch, "E33.14.26.0", {"start": v(51, -74) * mm, "end": v(61, -74) * mm});
            skLineSegment(sketch, "E33.14.26.1", {"start": v(51, -84) * mm, "end": v(61, -84) * mm});
            skLineSegment(sketch, "E33.14.26.2", {"start": v(51, -74) * mm, "end": v(51, -84) * mm});
            skLineSegment(sketch, "E33.14.26.3", {"start": v(61, -74) * mm, "end": v(61, -84) * mm});
            skLineSegment(sketch, "E33.14.27.0", {"start": v(51, -60) * mm, "end": v(61, -60) * mm});
            skLineSegment(sketch, "E33.14.27.1", {"start": v(51, -70) * mm, "end": v(61, -70) * mm});
            skLineSegment(sketch, "E33.14.27.2", {"start": v(51, -60) * mm, "end": v(51, -70) * mm});
            skLineSegment(sketch, "E33.14.27.3", {"start": v(61, -60) * mm, "end": v(61, -70) * mm});
            skLineSegment(sketch, "E33.14.28.0", {"start": v(51, -46) * mm, "end": v(61, -46) * mm});
            skLineSegment(sketch, "E33.14.28.1", {"start": v(51, -56) * mm, "end": v(61, -56) * mm});
            skLineSegment(sketch, "E33.14.28.2", {"start": v(51, -46) * mm, "end": v(51, -56) * mm});
            skLineSegment(sketch, "E33.14.28.3", {"start": v(61, -46) * mm, "end": v(61, -56) * mm});
            skLineSegment(sketch, "E33.14.29.0", {"start": v(51, -32) * mm, "end": v(61, -32) * mm});
            skLineSegment(sketch, "E33.14.29.1", {"start": v(51, -42) * mm, "end": v(61, -42) * mm});
            skLineSegment(sketch, "E33.14.29.2", {"start": v(51, -32) * mm, "end": v(51, -42) * mm});
            skLineSegment(sketch, "E33.14.29.3", {"start": v(61, -32) * mm, "end": v(61, -42) * mm});
            skLineSegment(sketch, "E33.14.30.0", {"start": v(51, -18) * mm, "end": v(61, -18) * mm});
            skLineSegment(sketch, "E33.14.30.1", {"start": v(51, -28) * mm, "end": v(61, -28) * mm});
            skLineSegment(sketch, "E33.14.30.2", {"start": v(51, -18) * mm, "end": v(51, -28) * mm});
            skLineSegment(sketch, "E33.14.30.3", {"start": v(61, -18) * mm, "end": v(61, -28) * mm});
            skLineSegment(sketch, "E33.14.31.0", {"start": v(51, -4) * mm, "end": v(61, -4) * mm});
            skLineSegment(sketch, "E33.14.31.1", {"start": v(51, -14) * mm, "end": v(61, -14) * mm});
            skLineSegment(sketch, "E33.14.31.2", {"start": v(51, -4) * mm, "end": v(51, -14) * mm});
            skLineSegment(sketch, "E33.14.31.3", {"start": v(61, -4) * mm, "end": v(61, -14) * mm});
            skLineSegment(sketch, "E33.15.0.0", {"start": v(37, -438) * mm, "end": v(47, -438) * mm});
            skLineSegment(sketch, "E33.15.0.1", {"start": v(37, -448) * mm, "end": v(47, -448) * mm});
            skLineSegment(sketch, "E33.15.0.2", {"start": v(37, -438) * mm, "end": v(37, -448) * mm});
            skLineSegment(sketch, "E33.15.0.3", {"start": v(47, -438) * mm, "end": v(47, -448) * mm});
            skLineSegment(sketch, "E33.15.1.0", {"start": v(37, -424) * mm, "end": v(47, -424) * mm});
            skLineSegment(sketch, "E33.15.1.1", {"start": v(37, -434) * mm, "end": v(47, -434) * mm});
            skLineSegment(sketch, "E33.15.1.2", {"start": v(37, -424) * mm, "end": v(37, -434) * mm});
            skLineSegment(sketch, "E33.15.1.3", {"start": v(47, -424) * mm, "end": v(47, -434) * mm});
            skLineSegment(sketch, "E33.15.2.0", {"start": v(37, -410) * mm, "end": v(47, -410) * mm});
            skLineSegment(sketch, "E33.15.2.1", {"start": v(37, -420) * mm, "end": v(47, -420) * mm});
            skLineSegment(sketch, "E33.15.2.2", {"start": v(37, -410) * mm, "end": v(37, -420) * mm});
            skLineSegment(sketch, "E33.15.2.3", {"start": v(47, -410) * mm, "end": v(47, -420) * mm});
            skLineSegment(sketch, "E33.15.3.0", {"start": v(37, -396) * mm, "end": v(47, -396) * mm});
            skLineSegment(sketch, "E33.15.3.1", {"start": v(37, -406) * mm, "end": v(47, -406) * mm});
            skLineSegment(sketch, "E33.15.3.2", {"start": v(37, -396) * mm, "end": v(37, -406) * mm});
            skLineSegment(sketch, "E33.15.3.3", {"start": v(47, -396) * mm, "end": v(47, -406) * mm});
            skLineSegment(sketch, "E33.15.4.0", {"start": v(37, -382) * mm, "end": v(47, -382) * mm});
            skLineSegment(sketch, "E33.15.4.1", {"start": v(37, -392) * mm, "end": v(47, -392) * mm});
            skLineSegment(sketch, "E33.15.4.2", {"start": v(37, -382) * mm, "end": v(37, -392) * mm});
            skLineSegment(sketch, "E33.15.4.3", {"start": v(47, -382) * mm, "end": v(47, -392) * mm});
            skLineSegment(sketch, "E33.15.5.0", {"start": v(37, -368) * mm, "end": v(47, -368) * mm});
            skLineSegment(sketch, "E33.15.5.1", {"start": v(37, -378) * mm, "end": v(47, -378) * mm});
            skLineSegment(sketch, "E33.15.5.2", {"start": v(37, -368) * mm, "end": v(37, -378) * mm});
            skLineSegment(sketch, "E33.15.5.3", {"start": v(47, -368) * mm, "end": v(47, -378) * mm});
            skLineSegment(sketch, "E33.15.6.0", {"start": v(37, -354) * mm, "end": v(47, -354) * mm});
            skLineSegment(sketch, "E33.15.6.1", {"start": v(37, -364) * mm, "end": v(47, -364) * mm});
            skLineSegment(sketch, "E33.15.6.2", {"start": v(37, -354) * mm, "end": v(37, -364) * mm});
            skLineSegment(sketch, "E33.15.6.3", {"start": v(47, -354) * mm, "end": v(47, -364) * mm});
            skLineSegment(sketch, "E33.15.7.0", {"start": v(37, -340) * mm, "end": v(47, -340) * mm});
            skLineSegment(sketch, "E33.15.7.1", {"start": v(37, -350) * mm, "end": v(47, -350) * mm});
            skLineSegment(sketch, "E33.15.7.2", {"start": v(37, -340) * mm, "end": v(37, -350) * mm});
            skLineSegment(sketch, "E33.15.7.3", {"start": v(47, -340) * mm, "end": v(47, -350) * mm});
            skLineSegment(sketch, "E33.15.8.0", {"start": v(37, -326) * mm, "end": v(47, -326) * mm});
            skLineSegment(sketch, "E33.15.8.1", {"start": v(37, -336) * mm, "end": v(47, -336) * mm});
            skLineSegment(sketch, "E33.15.8.2", {"start": v(37, -326) * mm, "end": v(37, -336) * mm});
            skLineSegment(sketch, "E33.15.8.3", {"start": v(47, -326) * mm, "end": v(47, -336) * mm});
            skLineSegment(sketch, "E33.15.9.0", {"start": v(37, -312) * mm, "end": v(47, -312) * mm});
            skLineSegment(sketch, "E33.15.9.1", {"start": v(37, -322) * mm, "end": v(47, -322) * mm});
            skLineSegment(sketch, "E33.15.9.2", {"start": v(37, -312) * mm, "end": v(37, -322) * mm});
            skLineSegment(sketch, "E33.15.9.3", {"start": v(47, -312) * mm, "end": v(47, -322) * mm});
            skLineSegment(sketch, "E33.15.10.0", {"start": v(37, -298) * mm, "end": v(47, -298) * mm});
            skLineSegment(sketch, "E33.15.10.1", {"start": v(37, -308) * mm, "end": v(47, -308) * mm});
            skLineSegment(sketch, "E33.15.10.2", {"start": v(37, -298) * mm, "end": v(37, -308) * mm});
            skLineSegment(sketch, "E33.15.10.3", {"start": v(47, -298) * mm, "end": v(47, -308) * mm});
            skLineSegment(sketch, "E33.15.11.0", {"start": v(37, -284) * mm, "end": v(47, -284) * mm});
            skLineSegment(sketch, "E33.15.11.1", {"start": v(37, -294) * mm, "end": v(47, -294) * mm});
            skLineSegment(sketch, "E33.15.11.2", {"start": v(37, -284) * mm, "end": v(37, -294) * mm});
            skLineSegment(sketch, "E33.15.11.3", {"start": v(47, -284) * mm, "end": v(47, -294) * mm});
            skLineSegment(sketch, "E33.15.12.0", {"start": v(37, -270) * mm, "end": v(47, -270) * mm});
            skLineSegment(sketch, "E33.15.12.1", {"start": v(37, -280) * mm, "end": v(47, -280) * mm});
            skLineSegment(sketch, "E33.15.12.2", {"start": v(37, -270) * mm, "end": v(37, -280) * mm});
            skLineSegment(sketch, "E33.15.12.3", {"start": v(47, -270) * mm, "end": v(47, -280) * mm});
            skLineSegment(sketch, "E33.15.13.0", {"start": v(37, -256) * mm, "end": v(47, -256) * mm});
            skLineSegment(sketch, "E33.15.13.1", {"start": v(37, -266) * mm, "end": v(47, -266) * mm});
            skLineSegment(sketch, "E33.15.13.2", {"start": v(37, -256) * mm, "end": v(37, -266) * mm});
            skLineSegment(sketch, "E33.15.13.3", {"start": v(47, -256) * mm, "end": v(47, -266) * mm});
            skLineSegment(sketch, "E33.15.14.0", {"start": v(37, -242) * mm, "end": v(47, -242) * mm});
            skLineSegment(sketch, "E33.15.14.1", {"start": v(37, -252) * mm, "end": v(47, -252) * mm});
            skLineSegment(sketch, "E33.15.14.2", {"start": v(37, -242) * mm, "end": v(37, -252) * mm});
            skLineSegment(sketch, "E33.15.14.3", {"start": v(47, -242) * mm, "end": v(47, -252) * mm});
            skLineSegment(sketch, "E33.15.15.0", {"start": v(37, -228) * mm, "end": v(47, -228) * mm});
            skLineSegment(sketch, "E33.15.15.1", {"start": v(37, -238) * mm, "end": v(47, -238) * mm});
            skLineSegment(sketch, "E33.15.15.2", {"start": v(37, -228) * mm, "end": v(37, -238) * mm});
            skLineSegment(sketch, "E33.15.15.3", {"start": v(47, -228) * mm, "end": v(47, -238) * mm});
            skLineSegment(sketch, "E33.15.16.0", {"start": v(37, -214) * mm, "end": v(47, -214) * mm});
            skLineSegment(sketch, "E33.15.16.1", {"start": v(37, -224) * mm, "end": v(47, -224) * mm});
            skLineSegment(sketch, "E33.15.16.2", {"start": v(37, -214) * mm, "end": v(37, -224) * mm});
            skLineSegment(sketch, "E33.15.16.3", {"start": v(47, -214) * mm, "end": v(47, -224) * mm});
            skLineSegment(sketch, "E33.15.17.0", {"start": v(37, -200) * mm, "end": v(47, -200) * mm});
            skLineSegment(sketch, "E33.15.17.1", {"start": v(37, -210) * mm, "end": v(47, -210) * mm});
            skLineSegment(sketch, "E33.15.17.2", {"start": v(37, -200) * mm, "end": v(37, -210) * mm});
            skLineSegment(sketch, "E33.15.17.3", {"start": v(47, -200) * mm, "end": v(47, -210) * mm});
            skLineSegment(sketch, "E33.15.18.0", {"start": v(37, -186) * mm, "end": v(47, -186) * mm});
            skLineSegment(sketch, "E33.15.18.1", {"start": v(37, -196) * mm, "end": v(47, -196) * mm});
            skLineSegment(sketch, "E33.15.18.2", {"start": v(37, -186) * mm, "end": v(37, -196) * mm});
            skLineSegment(sketch, "E33.15.18.3", {"start": v(47, -186) * mm, "end": v(47, -196) * mm});
            skLineSegment(sketch, "E33.15.19.0", {"start": v(37, -172) * mm, "end": v(47, -172) * mm});
            skLineSegment(sketch, "E33.15.19.1", {"start": v(37, -182) * mm, "end": v(47, -182) * mm});
            skLineSegment(sketch, "E33.15.19.2", {"start": v(37, -172) * mm, "end": v(37, -182) * mm});
            skLineSegment(sketch, "E33.15.19.3", {"start": v(47, -172) * mm, "end": v(47, -182) * mm});
            skLineSegment(sketch, "E33.15.20.0", {"start": v(37, -158) * mm, "end": v(47, -158) * mm});
            skLineSegment(sketch, "E33.15.20.1", {"start": v(37, -168) * mm, "end": v(47, -168) * mm});
            skLineSegment(sketch, "E33.15.20.2", {"start": v(37, -158) * mm, "end": v(37, -168) * mm});
            skLineSegment(sketch, "E33.15.20.3", {"start": v(47, -158) * mm, "end": v(47, -168) * mm});
            skLineSegment(sketch, "E33.15.21.0", {"start": v(37, -144) * mm, "end": v(47, -144) * mm});
            skLineSegment(sketch, "E33.15.21.1", {"start": v(37, -154) * mm, "end": v(47, -154) * mm});
            skLineSegment(sketch, "E33.15.21.2", {"start": v(37, -144) * mm, "end": v(37, -154) * mm});
            skLineSegment(sketch, "E33.15.21.3", {"start": v(47, -144) * mm, "end": v(47, -154) * mm});
            skLineSegment(sketch, "E33.15.22.0", {"start": v(37, -130) * mm, "end": v(47, -130) * mm});
            skLineSegment(sketch, "E33.15.22.1", {"start": v(37, -140) * mm, "end": v(47, -140) * mm});
            skLineSegment(sketch, "E33.15.22.2", {"start": v(37, -130) * mm, "end": v(37, -140) * mm});
            skLineSegment(sketch, "E33.15.22.3", {"start": v(47, -130) * mm, "end": v(47, -140) * mm});
            skLineSegment(sketch, "E33.15.23.0", {"start": v(37, -116) * mm, "end": v(47, -116) * mm});
            skLineSegment(sketch, "E33.15.23.1", {"start": v(37, -126) * mm, "end": v(47, -126) * mm});
            skLineSegment(sketch, "E33.15.23.2", {"start": v(37, -116) * mm, "end": v(37, -126) * mm});
            skLineSegment(sketch, "E33.15.23.3", {"start": v(47, -116) * mm, "end": v(47, -126) * mm});
            skLineSegment(sketch, "E33.15.24.0", {"start": v(37, -102) * mm, "end": v(47, -102) * mm});
            skLineSegment(sketch, "E33.15.24.1", {"start": v(37, -112) * mm, "end": v(47, -112) * mm});
            skLineSegment(sketch, "E33.15.24.2", {"start": v(37, -102) * mm, "end": v(37, -112) * mm});
            skLineSegment(sketch, "E33.15.24.3", {"start": v(47, -102) * mm, "end": v(47, -112) * mm});
            skLineSegment(sketch, "E33.15.25.0", {"start": v(37, -88) * mm, "end": v(47, -88) * mm});
            skLineSegment(sketch, "E33.15.25.1", {"start": v(37, -98) * mm, "end": v(47, -98) * mm});
            skLineSegment(sketch, "E33.15.25.2", {"start": v(37, -88) * mm, "end": v(37, -98) * mm});
            skLineSegment(sketch, "E33.15.25.3", {"start": v(47, -88) * mm, "end": v(47, -98) * mm});
            skLineSegment(sketch, "E33.15.26.0", {"start": v(37, -74) * mm, "end": v(47, -74) * mm});
            skLineSegment(sketch, "E33.15.26.1", {"start": v(37, -84) * mm, "end": v(47, -84) * mm});
            skLineSegment(sketch, "E33.15.26.2", {"start": v(37, -74) * mm, "end": v(37, -84) * mm});
            skLineSegment(sketch, "E33.15.26.3", {"start": v(47, -74) * mm, "end": v(47, -84) * mm});
            skLineSegment(sketch, "E33.15.27.0", {"start": v(37, -60) * mm, "end": v(47, -60) * mm});
            skLineSegment(sketch, "E33.15.27.1", {"start": v(37, -70) * mm, "end": v(47, -70) * mm});
            skLineSegment(sketch, "E33.15.27.2", {"start": v(37, -60) * mm, "end": v(37, -70) * mm});
            skLineSegment(sketch, "E33.15.27.3", {"start": v(47, -60) * mm, "end": v(47, -70) * mm});
            skLineSegment(sketch, "E33.15.28.0", {"start": v(37, -46) * mm, "end": v(47, -46) * mm});
            skLineSegment(sketch, "E33.15.28.1", {"start": v(37, -56) * mm, "end": v(47, -56) * mm});
            skLineSegment(sketch, "E33.15.28.2", {"start": v(37, -46) * mm, "end": v(37, -56) * mm});
            skLineSegment(sketch, "E33.15.28.3", {"start": v(47, -46) * mm, "end": v(47, -56) * mm});
            skLineSegment(sketch, "E33.15.29.0", {"start": v(37, -32) * mm, "end": v(47, -32) * mm});
            skLineSegment(sketch, "E33.15.29.1", {"start": v(37, -42) * mm, "end": v(47, -42) * mm});
            skLineSegment(sketch, "E33.15.29.2", {"start": v(37, -32) * mm, "end": v(37, -42) * mm});
            skLineSegment(sketch, "E33.15.29.3", {"start": v(47, -32) * mm, "end": v(47, -42) * mm});
            skLineSegment(sketch, "E33.15.30.0", {"start": v(37, -18) * mm, "end": v(47, -18) * mm});
            skLineSegment(sketch, "E33.15.30.1", {"start": v(37, -28) * mm, "end": v(47, -28) * mm});
            skLineSegment(sketch, "E33.15.30.2", {"start": v(37, -18) * mm, "end": v(37, -28) * mm});
            skLineSegment(sketch, "E33.15.30.3", {"start": v(47, -18) * mm, "end": v(47, -28) * mm});
            skLineSegment(sketch, "E33.15.31.0", {"start": v(37, -4) * mm, "end": v(47, -4) * mm});
            skLineSegment(sketch, "E33.15.31.1", {"start": v(37, -14) * mm, "end": v(47, -14) * mm});
            skLineSegment(sketch, "E33.15.31.2", {"start": v(37, -4) * mm, "end": v(37, -14) * mm});
            skLineSegment(sketch, "E33.15.31.3", {"start": v(47, -4) * mm, "end": v(47, -14) * mm});
            skLineSegment(sketch, "E33.16.0.0", {"start": v(23, -438) * mm, "end": v(33, -438) * mm});
            skLineSegment(sketch, "E33.16.0.1", {"start": v(23, -448) * mm, "end": v(33, -448) * mm});
            skLineSegment(sketch, "E33.16.0.2", {"start": v(23, -438) * mm, "end": v(23, -448) * mm});
            skLineSegment(sketch, "E33.16.0.3", {"start": v(33, -438) * mm, "end": v(33, -448) * mm});
            skLineSegment(sketch, "E33.16.1.0", {"start": v(23, -424) * mm, "end": v(33, -424) * mm});
            skLineSegment(sketch, "E33.16.1.1", {"start": v(23, -434) * mm, "end": v(33, -434) * mm});
            skLineSegment(sketch, "E33.16.1.2", {"start": v(23, -424) * mm, "end": v(23, -434) * mm});
            skLineSegment(sketch, "E33.16.1.3", {"start": v(33, -424) * mm, "end": v(33, -434) * mm});
            skLineSegment(sketch, "E33.16.2.0", {"start": v(23, -410) * mm, "end": v(33, -410) * mm});
            skLineSegment(sketch, "E33.16.2.1", {"start": v(23, -420) * mm, "end": v(33, -420) * mm});
            skLineSegment(sketch, "E33.16.2.2", {"start": v(23, -410) * mm, "end": v(23, -420) * mm});
            skLineSegment(sketch, "E33.16.2.3", {"start": v(33, -410) * mm, "end": v(33, -420) * mm});
            skLineSegment(sketch, "E33.16.3.0", {"start": v(23, -396) * mm, "end": v(33, -396) * mm});
            skLineSegment(sketch, "E33.16.3.1", {"start": v(23, -406) * mm, "end": v(33, -406) * mm});
            skLineSegment(sketch, "E33.16.3.2", {"start": v(23, -396) * mm, "end": v(23, -406) * mm});
            skLineSegment(sketch, "E33.16.3.3", {"start": v(33, -396) * mm, "end": v(33, -406) * mm});
            skLineSegment(sketch, "E33.16.4.0", {"start": v(23, -382) * mm, "end": v(33, -382) * mm});
            skLineSegment(sketch, "E33.16.4.1", {"start": v(23, -392) * mm, "end": v(33, -392) * mm});
            skLineSegment(sketch, "E33.16.4.2", {"start": v(23, -382) * mm, "end": v(23, -392) * mm});
            skLineSegment(sketch, "E33.16.4.3", {"start": v(33, -382) * mm, "end": v(33, -392) * mm});
            skLineSegment(sketch, "E33.16.5.0", {"start": v(23, -368) * mm, "end": v(33, -368) * mm});
            skLineSegment(sketch, "E33.16.5.1", {"start": v(23, -378) * mm, "end": v(33, -378) * mm});
            skLineSegment(sketch, "E33.16.5.2", {"start": v(23, -368) * mm, "end": v(23, -378) * mm});
            skLineSegment(sketch, "E33.16.5.3", {"start": v(33, -368) * mm, "end": v(33, -378) * mm});
            skLineSegment(sketch, "E33.16.6.0", {"start": v(23, -354) * mm, "end": v(33, -354) * mm});
            skLineSegment(sketch, "E33.16.6.1", {"start": v(23, -364) * mm, "end": v(33, -364) * mm});
            skLineSegment(sketch, "E33.16.6.2", {"start": v(23, -354) * mm, "end": v(23, -364) * mm});
            skLineSegment(sketch, "E33.16.6.3", {"start": v(33, -354) * mm, "end": v(33, -364) * mm});
            skLineSegment(sketch, "E33.16.7.0", {"start": v(23, -340) * mm, "end": v(33, -340) * mm});
            skLineSegment(sketch, "E33.16.7.1", {"start": v(23, -350) * mm, "end": v(33, -350) * mm});
            skLineSegment(sketch, "E33.16.7.2", {"start": v(23, -340) * mm, "end": v(23, -350) * mm});
            skLineSegment(sketch, "E33.16.7.3", {"start": v(33, -340) * mm, "end": v(33, -350) * mm});
            skLineSegment(sketch, "E33.16.8.0", {"start": v(23, -326) * mm, "end": v(33, -326) * mm});
            skLineSegment(sketch, "E33.16.8.1", {"start": v(23, -336) * mm, "end": v(33, -336) * mm});
            skLineSegment(sketch, "E33.16.8.2", {"start": v(23, -326) * mm, "end": v(23, -336) * mm});
            skLineSegment(sketch, "E33.16.8.3", {"start": v(33, -326) * mm, "end": v(33, -336) * mm});
            skLineSegment(sketch, "E33.16.9.0", {"start": v(23, -312) * mm, "end": v(33, -312) * mm});
            skLineSegment(sketch, "E33.16.9.1", {"start": v(23, -322) * mm, "end": v(33, -322) * mm});
            skLineSegment(sketch, "E33.16.9.2", {"start": v(23, -312) * mm, "end": v(23, -322) * mm});
            skLineSegment(sketch, "E33.16.9.3", {"start": v(33, -312) * mm, "end": v(33, -322) * mm});
            skLineSegment(sketch, "E33.16.10.0", {"start": v(23, -298) * mm, "end": v(33, -298) * mm});
            skLineSegment(sketch, "E33.16.10.1", {"start": v(23, -308) * mm, "end": v(33, -308) * mm});
            skLineSegment(sketch, "E33.16.10.2", {"start": v(23, -298) * mm, "end": v(23, -308) * mm});
            skLineSegment(sketch, "E33.16.10.3", {"start": v(33, -298) * mm, "end": v(33, -308) * mm});
            skLineSegment(sketch, "E33.16.11.0", {"start": v(23, -284) * mm, "end": v(33, -284) * mm});
            skLineSegment(sketch, "E33.16.11.1", {"start": v(23, -294) * mm, "end": v(33, -294) * mm});
            skLineSegment(sketch, "E33.16.11.2", {"start": v(23, -284) * mm, "end": v(23, -294) * mm});
            skLineSegment(sketch, "E33.16.11.3", {"start": v(33, -284) * mm, "end": v(33, -294) * mm});
            skLineSegment(sketch, "E33.16.12.0", {"start": v(23, -270) * mm, "end": v(33, -270) * mm});
            skLineSegment(sketch, "E33.16.12.1", {"start": v(23, -280) * mm, "end": v(33, -280) * mm});
            skLineSegment(sketch, "E33.16.12.2", {"start": v(23, -270) * mm, "end": v(23, -280) * mm});
            skLineSegment(sketch, "E33.16.12.3", {"start": v(33, -270) * mm, "end": v(33, -280) * mm});
            skLineSegment(sketch, "E33.16.13.0", {"start": v(23, -256) * mm, "end": v(33, -256) * mm});
            skLineSegment(sketch, "E33.16.13.1", {"start": v(23, -266) * mm, "end": v(33, -266) * mm});
            skLineSegment(sketch, "E33.16.13.2", {"start": v(23, -256) * mm, "end": v(23, -266) * mm});
            skLineSegment(sketch, "E33.16.13.3", {"start": v(33, -256) * mm, "end": v(33, -266) * mm});
            skLineSegment(sketch, "E33.16.14.0", {"start": v(23, -242) * mm, "end": v(33, -242) * mm});
            skLineSegment(sketch, "E33.16.14.1", {"start": v(23, -252) * mm, "end": v(33, -252) * mm});
            skLineSegment(sketch, "E33.16.14.2", {"start": v(23, -242) * mm, "end": v(23, -252) * mm});
            skLineSegment(sketch, "E33.16.14.3", {"start": v(33, -242) * mm, "end": v(33, -252) * mm});
            skLineSegment(sketch, "E33.16.15.0", {"start": v(23, -228) * mm, "end": v(33, -228) * mm});
            skLineSegment(sketch, "E33.16.15.1", {"start": v(23, -238) * mm, "end": v(33, -238) * mm});
            skLineSegment(sketch, "E33.16.15.2", {"start": v(23, -228) * mm, "end": v(23, -238) * mm});
            skLineSegment(sketch, "E33.16.15.3", {"start": v(33, -228) * mm, "end": v(33, -238) * mm});
            skLineSegment(sketch, "E33.16.16.0", {"start": v(23, -214) * mm, "end": v(33, -214) * mm});
            skLineSegment(sketch, "E33.16.16.1", {"start": v(23, -224) * mm, "end": v(33, -224) * mm});
            skLineSegment(sketch, "E33.16.16.2", {"start": v(23, -214) * mm, "end": v(23, -224) * mm});
            skLineSegment(sketch, "E33.16.16.3", {"start": v(33, -214) * mm, "end": v(33, -224) * mm});
            skLineSegment(sketch, "E33.16.17.0", {"start": v(23, -200) * mm, "end": v(33, -200) * mm});
            skLineSegment(sketch, "E33.16.17.1", {"start": v(23, -210) * mm, "end": v(33, -210) * mm});
            skLineSegment(sketch, "E33.16.17.2", {"start": v(23, -200) * mm, "end": v(23, -210) * mm});
            skLineSegment(sketch, "E33.16.17.3", {"start": v(33, -200) * mm, "end": v(33, -210) * mm});
            skLineSegment(sketch, "E33.16.18.0", {"start": v(23, -186) * mm, "end": v(33, -186) * mm});
            skLineSegment(sketch, "E33.16.18.1", {"start": v(23, -196) * mm, "end": v(33, -196) * mm});
            skLineSegment(sketch, "E33.16.18.2", {"start": v(23, -186) * mm, "end": v(23, -196) * mm});
            skLineSegment(sketch, "E33.16.18.3", {"start": v(33, -186) * mm, "end": v(33, -196) * mm});
            skLineSegment(sketch, "E33.16.19.0", {"start": v(23, -172) * mm, "end": v(33, -172) * mm});
            skLineSegment(sketch, "E33.16.19.1", {"start": v(23, -182) * mm, "end": v(33, -182) * mm});
            skLineSegment(sketch, "E33.16.19.2", {"start": v(23, -172) * mm, "end": v(23, -182) * mm});
            skLineSegment(sketch, "E33.16.19.3", {"start": v(33, -172) * mm, "end": v(33, -182) * mm});
            skLineSegment(sketch, "E33.16.20.0", {"start": v(23, -158) * mm, "end": v(33, -158) * mm});
            skLineSegment(sketch, "E33.16.20.1", {"start": v(23, -168) * mm, "end": v(33, -168) * mm});
            skLineSegment(sketch, "E33.16.20.2", {"start": v(23, -158) * mm, "end": v(23, -168) * mm});
            skLineSegment(sketch, "E33.16.20.3", {"start": v(33, -158) * mm, "end": v(33, -168) * mm});
            skLineSegment(sketch, "E33.16.21.0", {"start": v(23, -144) * mm, "end": v(33, -144) * mm});
            skLineSegment(sketch, "E33.16.21.1", {"start": v(23, -154) * mm, "end": v(33, -154) * mm});
            skLineSegment(sketch, "E33.16.21.2", {"start": v(23, -144) * mm, "end": v(23, -154) * mm});
            skLineSegment(sketch, "E33.16.21.3", {"start": v(33, -144) * mm, "end": v(33, -154) * mm});
            skLineSegment(sketch, "E33.16.22.0", {"start": v(23, -130) * mm, "end": v(33, -130) * mm});
            skLineSegment(sketch, "E33.16.22.1", {"start": v(23, -140) * mm, "end": v(33, -140) * mm});
            skLineSegment(sketch, "E33.16.22.2", {"start": v(23, -130) * mm, "end": v(23, -140) * mm});
            skLineSegment(sketch, "E33.16.22.3", {"start": v(33, -130) * mm, "end": v(33, -140) * mm});
            skLineSegment(sketch, "E33.16.23.0", {"start": v(23, -116) * mm, "end": v(33, -116) * mm});
            skLineSegment(sketch, "E33.16.23.1", {"start": v(23, -126) * mm, "end": v(33, -126) * mm});
            skLineSegment(sketch, "E33.16.23.2", {"start": v(23, -116) * mm, "end": v(23, -126) * mm});
            skLineSegment(sketch, "E33.16.23.3", {"start": v(33, -116) * mm, "end": v(33, -126) * mm});
            skLineSegment(sketch, "E33.16.24.0", {"start": v(23, -102) * mm, "end": v(33, -102) * mm});
            skLineSegment(sketch, "E33.16.24.1", {"start": v(23, -112) * mm, "end": v(33, -112) * mm});
            skLineSegment(sketch, "E33.16.24.2", {"start": v(23, -102) * mm, "end": v(23, -112) * mm});
            skLineSegment(sketch, "E33.16.24.3", {"start": v(33, -102) * mm, "end": v(33, -112) * mm});
            skLineSegment(sketch, "E33.16.25.0", {"start": v(23, -88) * mm, "end": v(33, -88) * mm});
            skLineSegment(sketch, "E33.16.25.1", {"start": v(23, -98) * mm, "end": v(33, -98) * mm});
            skLineSegment(sketch, "E33.16.25.2", {"start": v(23, -88) * mm, "end": v(23, -98) * mm});
            skLineSegment(sketch, "E33.16.25.3", {"start": v(33, -88) * mm, "end": v(33, -98) * mm});
            skLineSegment(sketch, "E33.16.26.0", {"start": v(23, -74) * mm, "end": v(33, -74) * mm});
            skLineSegment(sketch, "E33.16.26.1", {"start": v(23, -84) * mm, "end": v(33, -84) * mm});
            skLineSegment(sketch, "E33.16.26.2", {"start": v(23, -74) * mm, "end": v(23, -84) * mm});
            skLineSegment(sketch, "E33.16.26.3", {"start": v(33, -74) * mm, "end": v(33, -84) * mm});
            skLineSegment(sketch, "E33.16.27.0", {"start": v(23, -60) * mm, "end": v(33, -60) * mm});
            skLineSegment(sketch, "E33.16.27.1", {"start": v(23, -70) * mm, "end": v(33, -70) * mm});
            skLineSegment(sketch, "E33.16.27.2", {"start": v(23, -60) * mm, "end": v(23, -70) * mm});
            skLineSegment(sketch, "E33.16.27.3", {"start": v(33, -60) * mm, "end": v(33, -70) * mm});
            skLineSegment(sketch, "E33.16.28.0", {"start": v(23, -46) * mm, "end": v(33, -46) * mm});
            skLineSegment(sketch, "E33.16.28.1", {"start": v(23, -56) * mm, "end": v(33, -56) * mm});
            skLineSegment(sketch, "E33.16.28.2", {"start": v(23, -46) * mm, "end": v(23, -56) * mm});
            skLineSegment(sketch, "E33.16.28.3", {"start": v(33, -46) * mm, "end": v(33, -56) * mm});
            skLineSegment(sketch, "E33.16.29.0", {"start": v(23, -32) * mm, "end": v(33, -32) * mm});
            skLineSegment(sketch, "E33.16.29.1", {"start": v(23, -42) * mm, "end": v(33, -42) * mm});
            skLineSegment(sketch, "E33.16.29.2", {"start": v(23, -32) * mm, "end": v(23, -42) * mm});
            skLineSegment(sketch, "E33.16.29.3", {"start": v(33, -32) * mm, "end": v(33, -42) * mm});
            skLineSegment(sketch, "E33.16.30.0", {"start": v(23, -18) * mm, "end": v(33, -18) * mm});
            skLineSegment(sketch, "E33.16.30.1", {"start": v(23, -28) * mm, "end": v(33, -28) * mm});
            skLineSegment(sketch, "E33.16.30.2", {"start": v(23, -18) * mm, "end": v(23, -28) * mm});
            skLineSegment(sketch, "E33.16.30.3", {"start": v(33, -18) * mm, "end": v(33, -28) * mm});
            skLineSegment(sketch, "E33.16.31.0", {"start": v(23, -4) * mm, "end": v(33, -4) * mm});
            skLineSegment(sketch, "E33.16.31.1", {"start": v(23, -14) * mm, "end": v(33, -14) * mm});
            skLineSegment(sketch, "E33.16.31.2", {"start": v(23, -4) * mm, "end": v(23, -14) * mm});
            skLineSegment(sketch, "E33.16.31.3", {"start": v(33, -4) * mm, "end": v(33, -14) * mm});
            skLineSegment(sketch, "E33.17.0.0", {"start": v(9, -438) * mm, "end": v(19, -438) * mm});
            skLineSegment(sketch, "E33.17.0.1", {"start": v(9, -448) * mm, "end": v(19, -448) * mm});
            skLineSegment(sketch, "E33.17.0.2", {"start": v(9, -438) * mm, "end": v(9, -448) * mm});
            skLineSegment(sketch, "E33.17.0.3", {"start": v(19, -438) * mm, "end": v(19, -448) * mm});
            skLineSegment(sketch, "E33.17.1.0", {"start": v(9, -424) * mm, "end": v(19, -424) * mm});
            skLineSegment(sketch, "E33.17.1.1", {"start": v(9, -434) * mm, "end": v(19, -434) * mm});
            skLineSegment(sketch, "E33.17.1.2", {"start": v(9, -424) * mm, "end": v(9, -434) * mm});
            skLineSegment(sketch, "E33.17.1.3", {"start": v(19, -424) * mm, "end": v(19, -434) * mm});
            skLineSegment(sketch, "E33.17.2.0", {"start": v(9, -410) * mm, "end": v(19, -410) * mm});
            skLineSegment(sketch, "E33.17.2.1", {"start": v(9, -420) * mm, "end": v(19, -420) * mm});
            skLineSegment(sketch, "E33.17.2.2", {"start": v(9, -410) * mm, "end": v(9, -420) * mm});
            skLineSegment(sketch, "E33.17.2.3", {"start": v(19, -410) * mm, "end": v(19, -420) * mm});
            skLineSegment(sketch, "E33.17.3.0", {"start": v(9, -396) * mm, "end": v(19, -396) * mm});
            skLineSegment(sketch, "E33.17.3.1", {"start": v(9, -406) * mm, "end": v(19, -406) * mm});
            skLineSegment(sketch, "E33.17.3.2", {"start": v(9, -396) * mm, "end": v(9, -406) * mm});
            skLineSegment(sketch, "E33.17.3.3", {"start": v(19, -396) * mm, "end": v(19, -406) * mm});
            skLineSegment(sketch, "E33.17.4.0", {"start": v(9, -382) * mm, "end": v(19, -382) * mm});
            skLineSegment(sketch, "E33.17.4.1", {"start": v(9, -392) * mm, "end": v(19, -392) * mm});
            skLineSegment(sketch, "E33.17.4.2", {"start": v(9, -382) * mm, "end": v(9, -392) * mm});
            skLineSegment(sketch, "E33.17.4.3", {"start": v(19, -382) * mm, "end": v(19, -392) * mm});
            skLineSegment(sketch, "E33.17.5.0", {"start": v(9, -368) * mm, "end": v(19, -368) * mm});
            skLineSegment(sketch, "E33.17.5.1", {"start": v(9, -378) * mm, "end": v(19, -378) * mm});
            skLineSegment(sketch, "E33.17.5.2", {"start": v(9, -368) * mm, "end": v(9, -378) * mm});
            skLineSegment(sketch, "E33.17.5.3", {"start": v(19, -368) * mm, "end": v(19, -378) * mm});
            skLineSegment(sketch, "E33.17.6.0", {"start": v(9, -354) * mm, "end": v(19, -354) * mm});
            skLineSegment(sketch, "E33.17.6.1", {"start": v(9, -364) * mm, "end": v(19, -364) * mm});
            skLineSegment(sketch, "E33.17.6.2", {"start": v(9, -354) * mm, "end": v(9, -364) * mm});
            skLineSegment(sketch, "E33.17.6.3", {"start": v(19, -354) * mm, "end": v(19, -364) * mm});
            skLineSegment(sketch, "E33.17.7.0", {"start": v(9, -340) * mm, "end": v(19, -340) * mm});
            skLineSegment(sketch, "E33.17.7.1", {"start": v(9, -350) * mm, "end": v(19, -350) * mm});
            skLineSegment(sketch, "E33.17.7.2", {"start": v(9, -340) * mm, "end": v(9, -350) * mm});
            skLineSegment(sketch, "E33.17.7.3", {"start": v(19, -340) * mm, "end": v(19, -350) * mm});
            skLineSegment(sketch, "E33.17.8.0", {"start": v(9, -326) * mm, "end": v(19, -326) * mm});
            skLineSegment(sketch, "E33.17.8.1", {"start": v(9, -336) * mm, "end": v(19, -336) * mm});
            skLineSegment(sketch, "E33.17.8.2", {"start": v(9, -326) * mm, "end": v(9, -336) * mm});
            skLineSegment(sketch, "E33.17.8.3", {"start": v(19, -326) * mm, "end": v(19, -336) * mm});
            skLineSegment(sketch, "E33.17.9.0", {"start": v(9, -312) * mm, "end": v(19, -312) * mm});
            skLineSegment(sketch, "E33.17.9.1", {"start": v(9, -322) * mm, "end": v(19, -322) * mm});
            skLineSegment(sketch, "E33.17.9.2", {"start": v(9, -312) * mm, "end": v(9, -322) * mm});
            skLineSegment(sketch, "E33.17.9.3", {"start": v(19, -312) * mm, "end": v(19, -322) * mm});
            skLineSegment(sketch, "E33.17.10.0", {"start": v(9, -298) * mm, "end": v(19, -298) * mm});
            skLineSegment(sketch, "E33.17.10.1", {"start": v(9, -308) * mm, "end": v(19, -308) * mm});
            skLineSegment(sketch, "E33.17.10.2", {"start": v(9, -298) * mm, "end": v(9, -308) * mm});
            skLineSegment(sketch, "E33.17.10.3", {"start": v(19, -298) * mm, "end": v(19, -308) * mm});
            skLineSegment(sketch, "E33.17.11.0", {"start": v(9, -284) * mm, "end": v(19, -284) * mm});
            skLineSegment(sketch, "E33.17.11.1", {"start": v(9, -294) * mm, "end": v(19, -294) * mm});
            skLineSegment(sketch, "E33.17.11.2", {"start": v(9, -284) * mm, "end": v(9, -294) * mm});
            skLineSegment(sketch, "E33.17.11.3", {"start": v(19, -284) * mm, "end": v(19, -294) * mm});
            skLineSegment(sketch, "E33.17.12.0", {"start": v(9, -270) * mm, "end": v(19, -270) * mm});
            skLineSegment(sketch, "E33.17.12.1", {"start": v(9, -280) * mm, "end": v(19, -280) * mm});
            skLineSegment(sketch, "E33.17.12.2", {"start": v(9, -270) * mm, "end": v(9, -280) * mm});
            skLineSegment(sketch, "E33.17.12.3", {"start": v(19, -270) * mm, "end": v(19, -280) * mm});
            skLineSegment(sketch, "E33.17.13.0", {"start": v(9, -256) * mm, "end": v(19, -256) * mm});
            skLineSegment(sketch, "E33.17.13.1", {"start": v(9, -266) * mm, "end": v(19, -266) * mm});
            skLineSegment(sketch, "E33.17.13.2", {"start": v(9, -256) * mm, "end": v(9, -266) * mm});
            skLineSegment(sketch, "E33.17.13.3", {"start": v(19, -256) * mm, "end": v(19, -266) * mm});
            skLineSegment(sketch, "E33.17.14.0", {"start": v(9, -242) * mm, "end": v(19, -242) * mm});
            skLineSegment(sketch, "E33.17.14.1", {"start": v(9, -252) * mm, "end": v(19, -252) * mm});
            skLineSegment(sketch, "E33.17.14.2", {"start": v(9, -242) * mm, "end": v(9, -252) * mm});
            skLineSegment(sketch, "E33.17.14.3", {"start": v(19, -242) * mm, "end": v(19, -252) * mm});
            skLineSegment(sketch, "E33.17.15.0", {"start": v(9, -228) * mm, "end": v(19, -228) * mm});
            skLineSegment(sketch, "E33.17.15.1", {"start": v(9, -238) * mm, "end": v(19, -238) * mm});
            skLineSegment(sketch, "E33.17.15.2", {"start": v(9, -228) * mm, "end": v(9, -238) * mm});
            skLineSegment(sketch, "E33.17.15.3", {"start": v(19, -228) * mm, "end": v(19, -238) * mm});
            skLineSegment(sketch, "E33.17.16.0", {"start": v(9, -214) * mm, "end": v(19, -214) * mm});
            skLineSegment(sketch, "E33.17.16.1", {"start": v(9, -224) * mm, "end": v(19, -224) * mm});
            skLineSegment(sketch, "E33.17.16.2", {"start": v(9, -214) * mm, "end": v(9, -224) * mm});
            skLineSegment(sketch, "E33.17.16.3", {"start": v(19, -214) * mm, "end": v(19, -224) * mm});
            skLineSegment(sketch, "E33.17.17.0", {"start": v(9, -200) * mm, "end": v(19, -200) * mm});
            skLineSegment(sketch, "E33.17.17.1", {"start": v(9, -210) * mm, "end": v(19, -210) * mm});
            skLineSegment(sketch, "E33.17.17.2", {"start": v(9, -200) * mm, "end": v(9, -210) * mm});
            skLineSegment(sketch, "E33.17.17.3", {"start": v(19, -200) * mm, "end": v(19, -210) * mm});
            skLineSegment(sketch, "E33.17.18.0", {"start": v(9, -186) * mm, "end": v(19, -186) * mm});
            skLineSegment(sketch, "E33.17.18.1", {"start": v(9, -196) * mm, "end": v(19, -196) * mm});
            skLineSegment(sketch, "E33.17.18.2", {"start": v(9, -186) * mm, "end": v(9, -196) * mm});
            skLineSegment(sketch, "E33.17.18.3", {"start": v(19, -186) * mm, "end": v(19, -196) * mm});
            skLineSegment(sketch, "E33.17.19.0", {"start": v(9, -172) * mm, "end": v(19, -172) * mm});
            skLineSegment(sketch, "E33.17.19.1", {"start": v(9, -182) * mm, "end": v(19, -182) * mm});
            skLineSegment(sketch, "E33.17.19.2", {"start": v(9, -172) * mm, "end": v(9, -182) * mm});
            skLineSegment(sketch, "E33.17.19.3", {"start": v(19, -172) * mm, "end": v(19, -182) * mm});
            skLineSegment(sketch, "E33.17.20.0", {"start": v(9, -158) * mm, "end": v(19, -158) * mm});
            skLineSegment(sketch, "E33.17.20.1", {"start": v(9, -168) * mm, "end": v(19, -168) * mm});
            skLineSegment(sketch, "E33.17.20.2", {"start": v(9, -158) * mm, "end": v(9, -168) * mm});
            skLineSegment(sketch, "E33.17.20.3", {"start": v(19, -158) * mm, "end": v(19, -168) * mm});
            skLineSegment(sketch, "E33.17.21.0", {"start": v(9, -144) * mm, "end": v(19, -144) * mm});
            skLineSegment(sketch, "E33.17.21.1", {"start": v(9, -154) * mm, "end": v(19, -154) * mm});
            skLineSegment(sketch, "E33.17.21.2", {"start": v(9, -144) * mm, "end": v(9, -154) * mm});
            skLineSegment(sketch, "E33.17.21.3", {"start": v(19, -144) * mm, "end": v(19, -154) * mm});
            skLineSegment(sketch, "E33.17.22.0", {"start": v(9, -130) * mm, "end": v(19, -130) * mm});
            skLineSegment(sketch, "E33.17.22.1", {"start": v(9, -140) * mm, "end": v(19, -140) * mm});
            skLineSegment(sketch, "E33.17.22.2", {"start": v(9, -130) * mm, "end": v(9, -140) * mm});
            skLineSegment(sketch, "E33.17.22.3", {"start": v(19, -130) * mm, "end": v(19, -140) * mm});
            skLineSegment(sketch, "E33.17.23.0", {"start": v(9, -116) * mm, "end": v(19, -116) * mm});
            skLineSegment(sketch, "E33.17.23.1", {"start": v(9, -126) * mm, "end": v(19, -126) * mm});
            skLineSegment(sketch, "E33.17.23.2", {"start": v(9, -116) * mm, "end": v(9, -126) * mm});
            skLineSegment(sketch, "E33.17.23.3", {"start": v(19, -116) * mm, "end": v(19, -126) * mm});
            skLineSegment(sketch, "E33.17.24.0", {"start": v(9, -102) * mm, "end": v(19, -102) * mm});
            skLineSegment(sketch, "E33.17.24.1", {"start": v(9, -112) * mm, "end": v(19, -112) * mm});
            skLineSegment(sketch, "E33.17.24.2", {"start": v(9, -102) * mm, "end": v(9, -112) * mm});
            skLineSegment(sketch, "E33.17.24.3", {"start": v(19, -102) * mm, "end": v(19, -112) * mm});
            skLineSegment(sketch, "E33.17.25.0", {"start": v(9, -88) * mm, "end": v(19, -88) * mm});
            skLineSegment(sketch, "E33.17.25.1", {"start": v(9, -98) * mm, "end": v(19, -98) * mm});
            skLineSegment(sketch, "E33.17.25.2", {"start": v(9, -88) * mm, "end": v(9, -98) * mm});
            skLineSegment(sketch, "E33.17.25.3", {"start": v(19, -88) * mm, "end": v(19, -98) * mm});
            skLineSegment(sketch, "E33.17.26.0", {"start": v(9, -74) * mm, "end": v(19, -74) * mm});
            skLineSegment(sketch, "E33.17.26.1", {"start": v(9, -84) * mm, "end": v(19, -84) * mm});
            skLineSegment(sketch, "E33.17.26.2", {"start": v(9, -74) * mm, "end": v(9, -84) * mm});
            skLineSegment(sketch, "E33.17.26.3", {"start": v(19, -74) * mm, "end": v(19, -84) * mm});
            skLineSegment(sketch, "E33.17.27.0", {"start": v(9, -60) * mm, "end": v(19, -60) * mm});
            skLineSegment(sketch, "E33.17.27.1", {"start": v(9, -70) * mm, "end": v(19, -70) * mm});
            skLineSegment(sketch, "E33.17.27.2", {"start": v(9, -60) * mm, "end": v(9, -70) * mm});
            skLineSegment(sketch, "E33.17.27.3", {"start": v(19, -60) * mm, "end": v(19, -70) * mm});
            skLineSegment(sketch, "E33.17.28.0", {"start": v(9, -46) * mm, "end": v(19, -46) * mm});
            skLineSegment(sketch, "E33.17.28.1", {"start": v(9, -56) * mm, "end": v(19, -56) * mm});
            skLineSegment(sketch, "E33.17.28.2", {"start": v(9, -46) * mm, "end": v(9, -56) * mm});
            skLineSegment(sketch, "E33.17.28.3", {"start": v(19, -46) * mm, "end": v(19, -56) * mm});
            skLineSegment(sketch, "E33.17.29.0", {"start": v(9, -32) * mm, "end": v(19, -32) * mm});
            skLineSegment(sketch, "E33.17.29.1", {"start": v(9, -42) * mm, "end": v(19, -42) * mm});
            skLineSegment(sketch, "E33.17.29.2", {"start": v(9, -32) * mm, "end": v(9, -42) * mm});
            skLineSegment(sketch, "E33.17.29.3", {"start": v(19, -32) * mm, "end": v(19, -42) * mm});
            skLineSegment(sketch, "E33.17.30.0", {"start": v(9, -18) * mm, "end": v(19, -18) * mm});
            skLineSegment(sketch, "E33.17.30.1", {"start": v(9, -28) * mm, "end": v(19, -28) * mm});
            skLineSegment(sketch, "E33.17.30.2", {"start": v(9, -18) * mm, "end": v(9, -28) * mm});
            skLineSegment(sketch, "E33.17.30.3", {"start": v(19, -18) * mm, "end": v(19, -28) * mm});
            skLineSegment(sketch, "E33.17.31.0", {"start": v(9, -4) * mm, "end": v(19, -4) * mm});
            skLineSegment(sketch, "E33.17.31.1", {"start": v(9, -14) * mm, "end": v(19, -14) * mm});
            skLineSegment(sketch, "E33.17.31.2", {"start": v(9, -4) * mm, "end": v(9, -14) * mm});
            skLineSegment(sketch, "E33.17.31.3", {"start": v(19, -4) * mm, "end": v(19, -14) * mm});
            skLineSegment(sketch, "E33.direction1", {"start": v(247, -448) * mm, "end": v(233, -448) * mm, "construction": true});
            skLineSegment(sketch, "E33.direction2", {"start": v(247, -448) * mm, "end": v(247, -434) * mm, "construction": true});
            skSolve(sketch);
        }
        {
            var Q0;
            Q0=qCreatedBy(makeId("Top.planeOp"),FACE);
            var sketch = newSketch(context, id + "F4", { "sketchPlane" : qUnion([Q0])});
            skLineSegment(sketch, "E34.bottom", {"start": v(0, -420) * mm, "end": v(-47, -420) * mm});
            skLineSegment(sketch, "E34.top", {"start": v(0, -396) * mm, "end": v(-47, -396) * mm});
            skLineSegment(sketch, "E34.left", {"start": v(0, -420) * mm, "end": v(0, -396) * mm});
            skLineSegment(sketch, "E34.right", {"start": v(-47, -420) * mm, "end": v(-47, -396) * mm});
            skLineSegment(sketch, "E35.bottom", {"start": v(-285, -396) * mm, "end": v(-191, -396) * mm});
            skLineSegment(sketch, "E35.top", {"start": v(-285, -420) * mm, "end": v(-191, -420) * mm});
            skLineSegment(sketch, "E35.left", {"start": v(-285, -396) * mm, "end": v(-285, -420) * mm});
            skLineSegment(sketch, "E35.right", {"start": v(-191, -396) * mm, "end": v(-191, -420) * mm});
            skLineSegment(sketch, "E36.bottom", {"start": v(-285, -340) * mm, "end": v(-191, -340) * mm});
            skLineSegment(sketch, "E36.top", {"start": v(-285, -364) * mm, "end": v(-191, -364) * mm});
            skLineSegment(sketch, "E36.left", {"start": v(-285, -340) * mm, "end": v(-285, -364) * mm});
            skLineSegment(sketch, "E36.right", {"start": v(-191, -340) * mm, "end": v(-191, -364) * mm});
            skLineSegment(sketch, "E37.bottom", {"start": v(-47, -340) * mm, "end": v(0, -340) * mm});
            skLineSegment(sketch, "E37.top", {"start": v(-47, -364) * mm, "end": v(0, -364) * mm});
            skLineSegment(sketch, "E37.left", {"start": v(-47, -340) * mm, "end": v(-47, -364) * mm});
            skLineSegment(sketch, "E37.right", {"start": v(0, -340) * mm, "end": v(0, -364) * mm});
            skLineSegment(sketch, "E38.bottom", {"start": v(-229, -102) * mm, "end": v(-135, -102) * mm});
            skLineSegment(sketch, "E38.top", {"start": v(-229, -126) * mm, "end": v(-135, -126) * mm});
            skLineSegment(sketch, "E38.left", {"start": v(-229, -102) * mm, "end": v(-229, -126) * mm});
            skLineSegment(sketch, "E38.right", {"start": v(-135, -102) * mm, "end": v(-135, -126) * mm});
            skLineSegment(sketch, "E39.bottom", {"start": v(-229, -228) * mm, "end": v(-135, -228) * mm});
            skLineSegment(sketch, "E39.top", {"start": v(-229, -252) * mm, "end": v(-135, -252) * mm});
            skLineSegment(sketch, "E39.left", {"start": v(-229, -228) * mm, "end": v(-229, -252) * mm});
            skLineSegment(sketch, "E39.right", {"start": v(-135, -228) * mm, "end": v(-135, -252) * mm});
            skLineSegment(sketch, "E40.bottom", {"start": v(-47, -102) * mm, "end": v(0, -102) * mm});
            skLineSegment(sketch, "E40.top", {"start": v(-47, -126) * mm, "end": v(0, -126) * mm});
            skLineSegment(sketch, "E40.left", {"start": v(-47, -102) * mm, "end": v(-47, -126) * mm});
            skLineSegment(sketch, "E40.right", {"start": v(0, -102) * mm, "end": v(0, -126) * mm});
            skLineSegment(sketch, "E41.bottom", {"start": v(-47, -158) * mm, "end": v(0, -158) * mm});
            skLineSegment(sketch, "E41.top", {"start": v(-47, -182) * mm, "end": v(0, -182) * mm});
            skLineSegment(sketch, "E41.left", {"start": v(-47, -158) * mm, "end": v(-47, -182) * mm});
            skLineSegment(sketch, "E41.right", {"start": v(0, -158) * mm, "end": v(0, -182) * mm});
            skLineSegment(sketch, "E42.MirrorCS", {"start": v(229, -252) * mm, "end": v(135, -252) * mm});
            skLineSegment(sketch, "E43.MirrorCS", {"start": v(47, -158) * mm, "end": v(47, -182) * mm});
            skLineSegment(sketch, "E44.MirrorCS", {"start": v(285, -396) * mm, "end": v(285, -420) * mm});
            skLineSegment(sketch, "E45.MirrorCS", {"start": v(229, -102) * mm, "end": v(229, -126) * mm});
            skLineSegment(sketch, "E46.MirrorCS", {"start": v(229, -126) * mm, "end": v(135, -126) * mm});
            skLineSegment(sketch, "E47.MirrorCS", {"start": v(135, -228) * mm, "end": v(135, -252) * mm});
            skLineSegment(sketch, "E48.MirrorCS", {"start": v(191, -396) * mm, "end": v(191, -420) * mm});
            skLineSegment(sketch, "E49.MirrorCS", {"start": v(229, -228) * mm, "end": v(229, -252) * mm});
            skLineSegment(sketch, "E50.MirrorCS", {"start": v(47, -340) * mm, "end": v(47, -364) * mm});
            skLineSegment(sketch, "E51.MirrorCS", {"start": v(285, -340) * mm, "end": v(285, -364) * mm});
            skLineSegment(sketch, "E52.MirrorCS", {"start": v(191, -340) * mm, "end": v(191, -364) * mm});
            skLineSegment(sketch, "E53.MirrorCS", {"start": v(47, -102) * mm, "end": v(47, -126) * mm});
            skLineSegment(sketch, "E54.MirrorCS", {"start": v(135, -102) * mm, "end": v(135, -126) * mm});
            skLineSegment(sketch, "E55.MirrorCS", {"start": v(229, -228) * mm, "end": v(135, -228) * mm});
            skLineSegment(sketch, "E56.MirrorCS", {"start": v(47, -420) * mm, "end": v(47, -396) * mm});
            skLineSegment(sketch, "E57.MirrorCS", {"start": v(229, -102) * mm, "end": v(135, -102) * mm});
            skLineSegment(sketch, "E58.MirrorCS", {"start": v(47, -102) * mm, "end": v(0, -102) * mm});
            skLineSegment(sketch, "E59.MirrorCS", {"start": v(47, -158) * mm, "end": v(0, -158) * mm});
            skLineSegment(sketch, "E60.MirrorCS", {"start": v(285, -420) * mm, "end": v(191, -420) * mm});
            skLineSegment(sketch, "E61.MirrorCS", {"start": v(47, -364) * mm, "end": v(0, -364) * mm});
            skLineSegment(sketch, "E62.MirrorCS", {"start": v(285, -340) * mm, "end": v(191, -340) * mm});
            skLineSegment(sketch, "E63.MirrorCS", {"start": v(0, -420) * mm, "end": v(47, -420) * mm});
            skLineSegment(sketch, "E64.MirrorCS", {"start": v(285, -364) * mm, "end": v(191, -364) * mm});
            skLineSegment(sketch, "E65.MirrorCS", {"start": v(47, -340) * mm, "end": v(0, -340) * mm});
            skLineSegment(sketch, "E66.MirrorCS", {"start": v(47, -126) * mm, "end": v(0, -126) * mm});
            skLineSegment(sketch, "E67.MirrorCS", {"start": v(0, -396) * mm, "end": v(47, -396) * mm});
            skLineSegment(sketch, "E68.MirrorCS", {"start": v(47, -182) * mm, "end": v(0, -182) * mm});
            skLineSegment(sketch, "E69.MirrorCS", {"start": v(285, -396) * mm, "end": v(191, -396) * mm});
            skSolve(sketch);
        }
        {
            var Q0;
            Q0=makeQuery(id+"F0.imprint","IMPRINT",FACE,{"disambiguationData":[TD([[makeQuery(id+"F0.imprint","IMPRINT",EDGE,{"derivedFrom":sQuery(id+"F0.wireOp",EDGE,"E0.bottom")}),-1.0]])]});
            extrude(context, id + "F5", {"entities" : qUnion([Q0]), "oppositeDirection" : true, "depth" : 1.5 * mm});
        }
        {
            var Q0;
            Q0 = qSketchRegion(id + "F2", true);
            extrude(context, id + "F6", {"entities" : qUnion([Q0]), "operationType" : NewBodyOperationType.REMOVE, "oppositeDirection" : true, "depth" : 1.5 * mm});
        }
        {
            var Q0;
            Q0 = qSketchRegion(id + "F4", true);
            extrude(context, id + "F7", {"entities" : qUnion([Q0]), "operationType" : NewBodyOperationType.REMOVE, "oppositeDirection" : true, "depth" : 1.5 * mm});
        }
        {
            var Q0;
            Q0 = qSketchRegion(id + "F1", true);
            extrude(context, id + "F8", {"entities" : qUnion([Q0]), "operationType" : NewBodyOperationType.REMOVE, "oppositeDirection" : true, "depth" : 1.5 * mm});
        }
        {
            var Q0;
            Q0 = qSketchRegion(id + "F3", true);
            extrude(context, id + "F9", {"entities" : qUnion([Q0]), "operationType" : NewBodyOperationType.REMOVE, "oppositeDirection" : true, "depth" : 1.5 * mm});
        }
        {
            var Q0;
            Q0=makeQuery(id+"F6.boolean.opBoolean","COPY",EDGE,{"derivedFrom":makeQuery(id+"F6.opExtrude","SWEPT_EDGE",EDGE,{"disambiguationData":[OSD([sQuery(id+"F2.wireOp",EDGE,"E27.bottom"),sQuery(id+"F2.wireOp",EDGE,"E27.left")])]})});
            var Q1;
            Q1=makeQuery(id+"F6.boolean.opBoolean","COPY",EDGE,{"derivedFrom":makeQuery(id+"F6.opExtrude","SWEPT_EDGE",EDGE,{"disambiguationData":[OSD([sQuery(id+"F2.wireOp",EDGE,"E27.top"),sQuery(id+"F2.wireOp",EDGE,"E27.right")])]})});
            var Q2;
            Q2=makeQuery(id+"F6.boolean.opBoolean","COPY",EDGE,{"derivedFrom":makeQuery(id+"F6.opExtrude","SWEPT_EDGE",EDGE,{"disambiguationData":[OSD([sQuery(id+"F2.wireOp",EDGE,"E28.bottom"),sQuery(id+"F2.wireOp",EDGE,"E28.right")])]})});
            var Q3;
            Q3=makeQuery(id+"F6.boolean.opBoolean","COPY",EDGE,{"derivedFrom":makeQuery(id+"F6.opExtrude","SWEPT_EDGE",EDGE,{"disambiguationData":[OSD([sQuery(id+"F2.wireOp",EDGE,"E28.top"),sQuery(id+"F2.wireOp",EDGE,"E28.right")])]})});
            var Q4;
            Q4=makeQuery(id+"F6.boolean.opBoolean","COPY",EDGE,{"derivedFrom":makeQuery(id+"F6.opExtrude","SWEPT_EDGE",EDGE,{"disambiguationData":[OSD([sQuery(id+"F2.wireOp",EDGE,"E29.bottom"),sQuery(id+"F2.wireOp",EDGE,"E29.right")])]})});
            var Q5;
            Q5=makeQuery(id+"F6.boolean.opBoolean","COPY",EDGE,{"derivedFrom":makeQuery(id+"F6.opExtrude","SWEPT_EDGE",EDGE,{"disambiguationData":[OSD([sQuery(id+"F2.wireOp",EDGE,"E29.top"),sQuery(id+"F2.wireOp",EDGE,"E29.right")])]})});
            var Q6;
            Q6=makeQuery(id+"F5.opExtrude","SWEPT_EDGE",EDGE,{"disambiguationData":[OSD([sQuery(id+"F0.wireOp",EDGE,"E0.top"),sQuery(id+"F0.wireOp",EDGE,"E0.right")])]});
            var Q7;
            Q7=makeQuery(id+"F5.opExtrude","SWEPT_EDGE",EDGE,{"disambiguationData":[OSD([sQuery(id+"F0.wireOp",EDGE,"E0.top"),sQuery(id+"F0.wireOp",EDGE,"E0.left")])]});
            var Q8;
            Q8=makeQuery(id+"F6.boolean.opBoolean","COPY",EDGE,{"derivedFrom":makeQuery(id+"F6.opExtrude","SWEPT_EDGE",EDGE,{"disambiguationData":[OSD([sQuery(id+"F2.wireOp",EDGE,"E26.top"),sQuery(id+"F2.wireOp",EDGE,"E26.left")])]})});
            var Q9;
            Q9=makeQuery(id+"F6.boolean.opBoolean","COPY",EDGE,{"derivedFrom":makeQuery(id+"F6.opExtrude","SWEPT_EDGE",EDGE,{"disambiguationData":[OSD([sQuery(id+"F2.wireOp",EDGE,"E26.bottom"),sQuery(id+"F2.wireOp",EDGE,"E26.left")])]})});
            var Q10;
            Q10=makeQuery(id+"F6.boolean.opBoolean","COPY",EDGE,{"derivedFrom":makeQuery(id+"F6.opExtrude","SWEPT_EDGE",EDGE,{"disambiguationData":[OSD([sQuery(id+"F2.wireOp",EDGE,"E25.top"),sQuery(id+"F2.wireOp",EDGE,"E25.left")])]})});
            var Q11;
            Q11=makeQuery(id+"F6.boolean.opBoolean","COPY",EDGE,{"derivedFrom":makeQuery(id+"F6.opExtrude","SWEPT_EDGE",EDGE,{"disambiguationData":[OSD([sQuery(id+"F2.wireOp",EDGE,"E25.bottom"),sQuery(id+"F2.wireOp",EDGE,"E25.left")])]})});
            var Q12;
            Q12=makeQuery(id+"F6.boolean.opBoolean","COPY",EDGE,{"derivedFrom":makeQuery(id+"F6.opExtrude","SWEPT_EDGE",EDGE,{"disambiguationData":[OSD([sQuery(id+"F2.wireOp",EDGE,"E24.top"),sQuery(id+"F2.wireOp",EDGE,"E24.left")])]})});
            var Q13;
            Q13=makeQuery(id+"F6.boolean.opBoolean","COPY",EDGE,{"derivedFrom":makeQuery(id+"F6.opExtrude","SWEPT_EDGE",EDGE,{"disambiguationData":[OSD([sQuery(id+"F2.wireOp",EDGE,"E24.bottom"),sQuery(id+"F2.wireOp",EDGE,"E24.right")])]})});
            fillet(context, id + "F10", {"entities" : qUnion([Q0, Q1, Q2, Q3, Q4, Q5, Q6, Q7, Q8, Q9, Q10, Q11, Q12, Q13]), "radius" : 4 * mm, "tangentPropagation" : true, "allowEdgeOverflow" : false});
        }
    });
